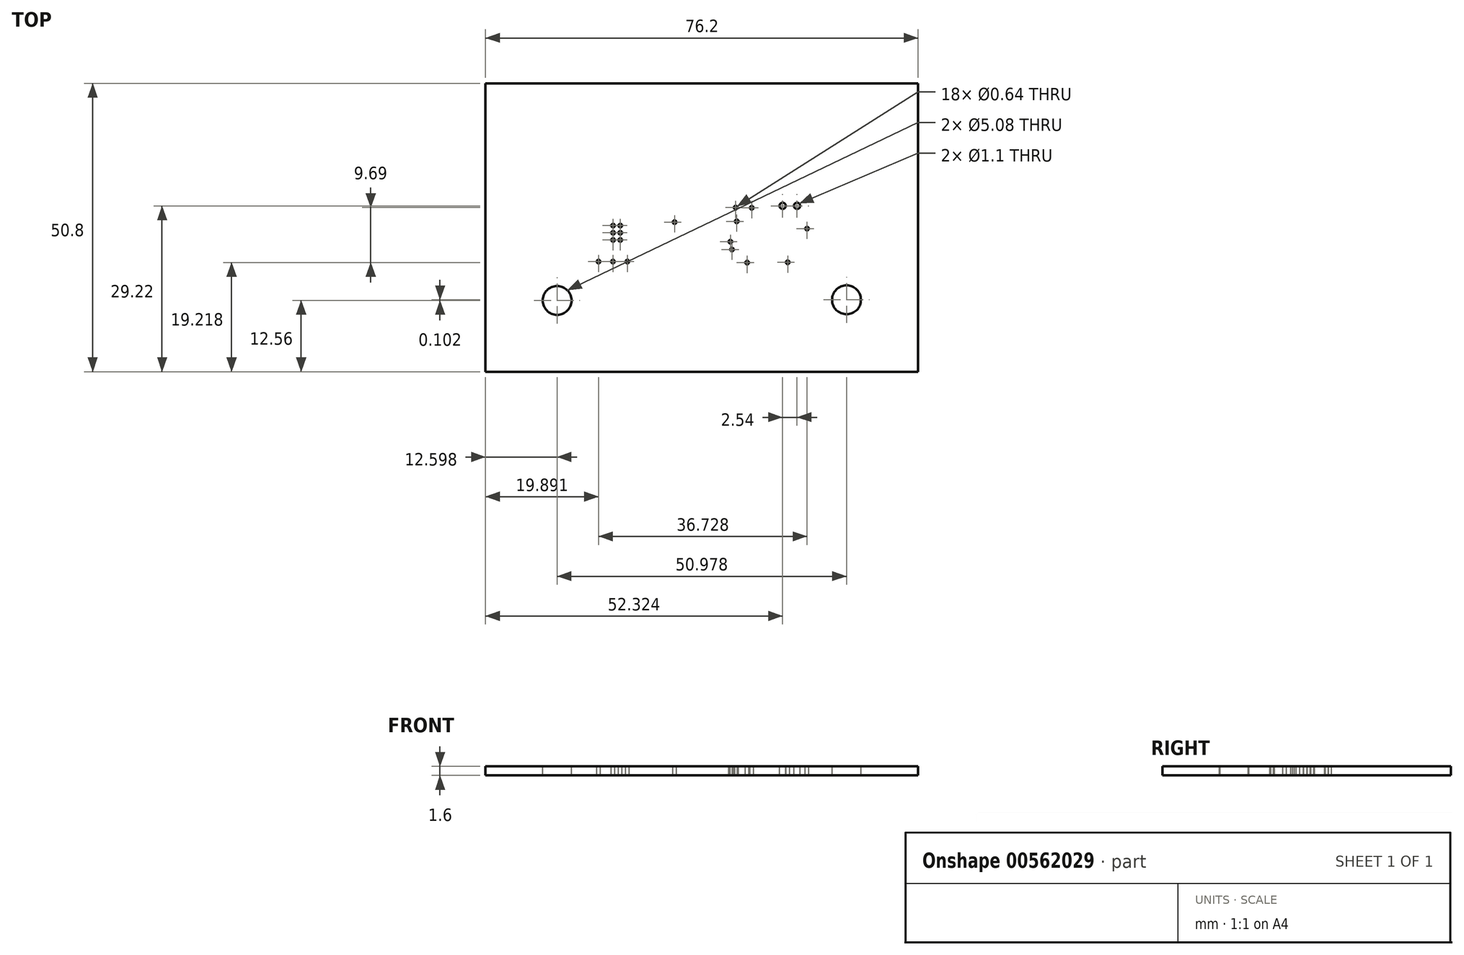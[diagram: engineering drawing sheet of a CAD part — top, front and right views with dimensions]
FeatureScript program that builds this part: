
annotation { "Feature Type Name" : "Feature", "Feature Type Description" : "" }
export const myFeature = defineFeature(function(context is Context, id is Id, definition is map)
    precondition{}
    {
        {
            var Q0;
            Q0=qCreatedBy(makeId("Top.planeOp"),FACE);
            var sketch = newSketch(context, id + "F0", { "sketchPlane" : qUnion([Q0])});
            skArc(sketch, "E0", {"start": v(-12.89, -6) * mm, "mid": v(-13.13, -5.75) * mm, "end": v(-13.37, -6) * mm});
            skArc(sketch, "E1", {"start": v(-13.37, -6) * mm, "mid": v(-13.13, -6.24) * mm, "end": v(-12.89, -6) * mm});
            skArc(sketch, "E2", {"start": v(-15.43, -6) * mm, "mid": v(-15.67, -5.75) * mm, "end": v(-15.91, -6) * mm});
            skArc(sketch, "E3", {"start": v(-15.91, -6) * mm, "mid": v(-15.67, -6.24) * mm, "end": v(-15.43, -6) * mm});
            skArc(sketch, "E4", {"start": v(-17.97, -6) * mm, "mid": v(-18.2, -5.75) * mm, "end": v(-18.45, -6) * mm});
            skArc(sketch, "E5", {"start": v(-18.45, -6) * mm, "mid": v(-18.2, -6.24) * mm, "end": v(-17.97, -6) * mm});
            skArc(sketch, "E6", {"start": v(18.76, -0.2) * mm, "mid": v(18.52, 0.05) * mm, "end": v(18.28, -0.2) * mm});
            skArc(sketch, "E7", {"start": v(18.28, -0.2) * mm, "mid": v(18.52, -0.43) * mm, "end": v(18.76, -0.2) * mm});
            skArc(sketch, "E8", {"start": v(5.26, -2.5) * mm, "mid": v(5.02, -2.26) * mm, "end": v(4.78, -2.5) * mm});
            skArc(sketch, "E9", {"start": v(4.78, -2.5) * mm, "mid": v(5.02, -2.74) * mm, "end": v(5.26, -2.5) * mm});
            skArc(sketch, "E10", {"start": v(5.54, -3.88) * mm, "mid": v(5.3, -3.63) * mm, "end": v(5.06, -3.88) * mm});
            skArc(sketch, "E11", {"start": v(5.06, -3.88) * mm, "mid": v(5.3, -4.12) * mm, "end": v(5.54, -3.88) * mm});
            skArc(sketch, "E12", {"start": v(-4.57, 0.95) * mm, "mid": v(-4.81, 1.19) * mm, "end": v(-5.05, 0.95) * mm});
            skArc(sketch, "E13", {"start": v(-5.05, 0.95) * mm, "mid": v(-4.81, 0.7) * mm, "end": v(-4.57, 0.95) * mm});
            skArc(sketch, "E14", {"start": v(6.2, 3.5) * mm, "mid": v(5.96, 3.75) * mm, "end": v(5.72, 3.5) * mm});
            skArc(sketch, "E15", {"start": v(5.72, 3.5) * mm, "mid": v(5.96, 3.27) * mm, "end": v(6.2, 3.5) * mm});
            skArc(sketch, "E16", {"start": v(9.03, 3.47) * mm, "mid": v(8.79, 3.71) * mm, "end": v(8.54, 3.47) * mm});
            skArc(sketch, "E17", {"start": v(8.54, 3.47) * mm, "mid": v(8.79, 3.23) * mm, "end": v(9.03, 3.47) * mm});
            skArc(sketch, "E18", {"start": v(6.38, 1.09) * mm, "mid": v(6.14, 1.33) * mm, "end": v(5.9, 1.09) * mm});
            skArc(sketch, "E19", {"start": v(5.9, 1.09) * mm, "mid": v(6.14, 0.85) * mm, "end": v(6.38, 1.09) * mm});
            skArc(sketch, "E20", {"start": v(28.86, -23.7) * mm, "mid": v(28.39, -23.22) * mm, "end": v(27.91, -23.7) * mm});
            skArc(sketch, "E21", {"start": v(27.91, -23.7) * mm, "mid": v(28.39, -24.17) * mm, "end": v(28.86, -23.7) * mm});
            skArc(sketch, "E22", {"start": v(26.32, -23.7) * mm, "mid": v(25.85, -23.22) * mm, "end": v(25.37, -23.7) * mm});
            skArc(sketch, "E23", {"start": v(25.37, -23.7) * mm, "mid": v(25.85, -24.17) * mm, "end": v(26.32, -23.7) * mm});
            skArc(sketch, "E24", {"start": v(23.78, -23.7) * mm, "mid": v(23.3, -23.22) * mm, "end": v(22.83, -23.7) * mm});
            skArc(sketch, "E25", {"start": v(22.83, -23.7) * mm, "mid": v(23.3, -24.17) * mm, "end": v(23.78, -23.7) * mm});
            skArc(sketch, "E26", {"start": v(21.24, -23.7) * mm, "mid": v(20.77, -23.22) * mm, "end": v(20.3, -23.7) * mm});
            skArc(sketch, "E27", {"start": v(20.3, -23.7) * mm, "mid": v(20.77, -24.17) * mm, "end": v(21.24, -23.7) * mm});
            skArc(sketch, "E28", {"start": v(18.7, -23.7) * mm, "mid": v(18.23, -23.22) * mm, "end": v(17.75, -23.7) * mm});
            skArc(sketch, "E29", {"start": v(17.75, -23.7) * mm, "mid": v(18.23, -24.17) * mm, "end": v(18.7, -23.7) * mm});
            skArc(sketch, "E30", {"start": v(16.16, -23.7) * mm, "mid": v(15.69, -23.22) * mm, "end": v(15.21, -23.7) * mm});
            skArc(sketch, "E31", {"start": v(15.21, -23.7) * mm, "mid": v(15.69, -24.17) * mm, "end": v(16.16, -23.7) * mm});
            skArc(sketch, "E32", {"start": v(13.62, -23.7) * mm, "mid": v(13.15, -23.22) * mm, "end": v(12.67, -23.7) * mm});
            skArc(sketch, "E33", {"start": v(12.67, -23.7) * mm, "mid": v(13.15, -24.17) * mm, "end": v(13.62, -23.7) * mm});
            skArc(sketch, "E34", {"start": v(11.08, -23.7) * mm, "mid": v(10.6, -23.22) * mm, "end": v(10.13, -23.7) * mm});
            skArc(sketch, "E35", {"start": v(10.13, -23.7) * mm, "mid": v(10.6, -24.17) * mm, "end": v(11.08, -23.7) * mm});
            skArc(sketch, "E36", {"start": v(8.54, -23.7) * mm, "mid": v(8.07, -23.22) * mm, "end": v(7.6, -23.7) * mm});
            skArc(sketch, "E37", {"start": v(7.6, -23.7) * mm, "mid": v(8.07, -24.17) * mm, "end": v(8.54, -23.7) * mm});
            skArc(sketch, "E38", {"start": v(6, -23.7) * mm, "mid": v(5.53, -23.22) * mm, "end": v(5.05, -23.7) * mm});
            skArc(sketch, "E39", {"start": v(5.05, -23.7) * mm, "mid": v(5.53, -24.17) * mm, "end": v(6, -23.7) * mm});
            skArc(sketch, "E40", {"start": v(3.46, -23.7) * mm, "mid": v(2.99, -23.22) * mm, "end": v(2.51, -23.7) * mm});
            skArc(sketch, "E41", {"start": v(2.51, -23.7) * mm, "mid": v(2.99, -24.17) * mm, "end": v(3.46, -23.7) * mm});
            skArc(sketch, "E42", {"start": v(0.92, -23.7) * mm, "mid": v(0.45, -23.22) * mm, "end": v(-0.03, -23.7) * mm});
            skArc(sketch, "E43", {"start": v(-0.03, -23.7) * mm, "mid": v(0.45, -24.17) * mm, "end": v(0.92, -23.7) * mm});
            skArc(sketch, "E44", {"start": v(-1.62, -23.7) * mm, "mid": v(-2.1, -23.22) * mm, "end": v(-2.57, -23.7) * mm});
            skArc(sketch, "E45", {"start": v(-2.57, -23.7) * mm, "mid": v(-2.1, -24.17) * mm, "end": v(-1.62, -23.7) * mm});
            skArc(sketch, "E46", {"start": v(-4.16, -23.7) * mm, "mid": v(-4.63, -23.22) * mm, "end": v(-5.1, -23.7) * mm});
            skArc(sketch, "E47", {"start": v(-5.1, -23.7) * mm, "mid": v(-4.63, -24.17) * mm, "end": v(-4.16, -23.7) * mm});
            skArc(sketch, "E48", {"start": v(-6.7, -23.7) * mm, "mid": v(-7.17, -23.22) * mm, "end": v(-7.65, -23.7) * mm});
            skArc(sketch, "E49", {"start": v(-7.65, -23.7) * mm, "mid": v(-7.17, -24.17) * mm, "end": v(-6.7, -23.7) * mm});
            skArc(sketch, "E50", {"start": v(-9.24, -23.7) * mm, "mid": v(-9.71, -23.22) * mm, "end": v(-10.19, -23.7) * mm});
            skArc(sketch, "E51", {"start": v(-10.19, -23.7) * mm, "mid": v(-9.71, -24.17) * mm, "end": v(-9.24, -23.7) * mm});
            skArc(sketch, "E52", {"start": v(-11.78, -23.7) * mm, "mid": v(-12.25, -23.22) * mm, "end": v(-12.73, -23.7) * mm});
            skArc(sketch, "E53", {"start": v(-12.73, -23.7) * mm, "mid": v(-12.25, -24.17) * mm, "end": v(-11.78, -23.7) * mm});
            skArc(sketch, "E54", {"start": v(-15.4, 0.34) * mm, "mid": v(-15.65, 0.58) * mm, "end": v(-15.89, 0.34) * mm});
            skArc(sketch, "E55", {"start": v(-15.89, 0.34) * mm, "mid": v(-15.65, 0.1) * mm, "end": v(-15.4, 0.34) * mm});
            skArc(sketch, "E56", {"start": v(-14.14, 0.34) * mm, "mid": v(-14.38, 0.58) * mm, "end": v(-14.62, 0.34) * mm});
            skArc(sketch, "E57", {"start": v(-14.62, 0.34) * mm, "mid": v(-14.38, 0.1) * mm, "end": v(-14.14, 0.34) * mm});
            skArc(sketch, "E58", {"start": v(-14.14, -0.93) * mm, "mid": v(-14.38, -0.69) * mm, "end": v(-14.62, -0.93) * mm});
            skArc(sketch, "E59", {"start": v(-14.62, -0.93) * mm, "mid": v(-14.38, -1.17) * mm, "end": v(-14.14, -0.93) * mm});
            skArc(sketch, "E60", {"start": v(-14.14, -2.2) * mm, "mid": v(-14.38, -1.96) * mm, "end": v(-14.62, -2.2) * mm});
            skArc(sketch, "E61", {"start": v(-14.62, -2.2) * mm, "mid": v(-14.38, -2.44) * mm, "end": v(-14.14, -2.2) * mm});
            skArc(sketch, "E62", {"start": v(-15.4, -0.93) * mm, "mid": v(-15.65, -0.69) * mm, "end": v(-15.89, -0.93) * mm});
            skArc(sketch, "E63", {"start": v(-15.89, -0.93) * mm, "mid": v(-15.65, -1.17) * mm, "end": v(-15.4, -0.93) * mm});
            skArc(sketch, "E64", {"start": v(-15.4, -2.2) * mm, "mid": v(-15.65, -1.96) * mm, "end": v(-15.89, -2.2) * mm});
            skArc(sketch, "E65", {"start": v(-15.89, -2.2) * mm, "mid": v(-15.65, -2.44) * mm, "end": v(-15.4, -2.2) * mm});
            skArc(sketch, "E66", {"start": v(37.09, 19.86) * mm, "mid": v(36.61, 20.34) * mm, "end": v(36.13, 19.86) * mm});
            skArc(sketch, "E67", {"start": v(36.13, 19.86) * mm, "mid": v(36.61, 19.38) * mm, "end": v(37.09, 19.86) * mm});
            skArc(sketch, "E68", {"start": v(37.09, 17.32) * mm, "mid": v(36.61, 17.8) * mm, "end": v(36.13, 17.32) * mm});
            skArc(sketch, "E69", {"start": v(36.13, 17.32) * mm, "mid": v(36.61, 16.84) * mm, "end": v(37.09, 17.32) * mm});
            skArc(sketch, "E70", {"start": v(37.09, 14.78) * mm, "mid": v(36.61, 15.26) * mm, "end": v(36.13, 14.78) * mm});
            skArc(sketch, "E71", {"start": v(36.13, 14.78) * mm, "mid": v(36.61, 14.3) * mm, "end": v(37.09, 14.78) * mm});
            skArc(sketch, "E72", {"start": v(37.09, 12.24) * mm, "mid": v(36.61, 12.72) * mm, "end": v(36.13, 12.24) * mm});
            skArc(sketch, "E73", {"start": v(36.13, 12.24) * mm, "mid": v(36.61, 11.76) * mm, "end": v(37.09, 12.24) * mm});
            skArc(sketch, "E74", {"start": v(37.09, 9.7) * mm, "mid": v(36.61, 10.18) * mm, "end": v(36.13, 9.7) * mm});
            skArc(sketch, "E75", {"start": v(36.13, 9.7) * mm, "mid": v(36.61, 9.22) * mm, "end": v(37.09, 9.7) * mm});
            skArc(sketch, "E76", {"start": v(37, -12.53) * mm, "mid": v(36.53, -12.06) * mm, "end": v(36.06, -12.53) * mm});
            skArc(sketch, "E77", {"start": v(36.06, -12.53) * mm, "mid": v(36.53, -13) * mm, "end": v(37, -12.53) * mm});
            skArc(sketch, "E78", {"start": v(17.24, 3.82) * mm, "mid": v(16.76, 4.3) * mm, "end": v(16.29, 3.82) * mm});
            skArc(sketch, "E79", {"start": v(16.29, 3.82) * mm, "mid": v(16.76, 3.34) * mm, "end": v(17.24, 3.82) * mm});
            skArc(sketch, "E80", {"start": v(16.8, 23.69) * mm, "mid": v(16.33, 24.16) * mm, "end": v(15.85, 23.69) * mm});
            skArc(sketch, "E81", {"start": v(15.85, 23.69) * mm, "mid": v(16.33, 23.21) * mm, "end": v(16.8, 23.69) * mm});
            skArc(sketch, "E82", {"start": v(-12.94, -6) * mm, "mid": v(-13.13, -5.8) * mm, "end": v(-13.32, -6) * mm});
            skArc(sketch, "E83", {"start": v(-13.32, -6) * mm, "mid": v(-13.13, -6.18) * mm, "end": v(-12.94, -6) * mm});
            skArc(sketch, "E84", {"start": v(-15.48, -6) * mm, "mid": v(-15.67, -5.8) * mm, "end": v(-15.86, -6) * mm});
            skArc(sketch, "E85", {"start": v(-15.86, -6) * mm, "mid": v(-15.67, -6.18) * mm, "end": v(-15.48, -6) * mm});
            skArc(sketch, "E86", {"start": v(-18.02, -6) * mm, "mid": v(-18.2, -5.8) * mm, "end": v(-18.4, -6) * mm});
            skArc(sketch, "E87", {"start": v(-18.4, -6) * mm, "mid": v(-18.2, -6.18) * mm, "end": v(-18.02, -6) * mm});
            skArc(sketch, "E88", {"start": v(18.7, -0.2) * mm, "mid": v(18.52, 0) * mm, "end": v(18.33, -0.2) * mm});
            skArc(sketch, "E89", {"start": v(18.33, -0.2) * mm, "mid": v(18.52, -0.38) * mm, "end": v(18.7, -0.2) * mm});
            skArc(sketch, "E90", {"start": v(5.2, -2.5) * mm, "mid": v(5.02, -2.3) * mm, "end": v(4.83, -2.5) * mm});
            skArc(sketch, "E91", {"start": v(4.83, -2.5) * mm, "mid": v(5.02, -2.69) * mm, "end": v(5.2, -2.5) * mm});
            skArc(sketch, "E92", {"start": v(5.5, -3.88) * mm, "mid": v(5.3, -3.69) * mm, "end": v(5.11, -3.88) * mm});
            skArc(sketch, "E93", {"start": v(5.11, -3.88) * mm, "mid": v(5.3, -4.07) * mm, "end": v(5.5, -3.88) * mm});
            skArc(sketch, "E94", {"start": v(-4.62, 0.95) * mm, "mid": v(-4.81, 1.14) * mm, "end": v(-5, 0.95) * mm});
            skArc(sketch, "E95", {"start": v(-5, 0.95) * mm, "mid": v(-4.81, 0.76) * mm, "end": v(-4.62, 0.95) * mm});
            skArc(sketch, "E96", {"start": v(6.15, 3.5) * mm, "mid": v(5.96, 3.7) * mm, "end": v(5.77, 3.5) * mm});
            skArc(sketch, "E97", {"start": v(5.77, 3.5) * mm, "mid": v(5.96, 3.32) * mm, "end": v(6.15, 3.5) * mm});
            skArc(sketch, "E98", {"start": v(8.98, 3.47) * mm, "mid": v(8.79, 3.66) * mm, "end": v(8.6, 3.47) * mm});
            skArc(sketch, "E99", {"start": v(8.6, 3.47) * mm, "mid": v(8.79, 3.28) * mm, "end": v(8.98, 3.47) * mm});
            skArc(sketch, "E100", {"start": v(6.33, 1.09) * mm, "mid": v(6.14, 1.28) * mm, "end": v(5.95, 1.09) * mm});
            skArc(sketch, "E101", {"start": v(5.95, 1.09) * mm, "mid": v(6.14, 0.9) * mm, "end": v(6.33, 1.09) * mm});
            skArc(sketch, "E102", {"start": v(28.81, -23.7) * mm, "mid": v(28.39, -23.27) * mm, "end": v(27.97, -23.7) * mm});
            skArc(sketch, "E103", {"start": v(27.97, -23.7) * mm, "mid": v(28.39, -24.11) * mm, "end": v(28.81, -23.7) * mm});
            skArc(sketch, "E104", {"start": v(26.27, -23.7) * mm, "mid": v(25.85, -23.27) * mm, "end": v(25.43, -23.7) * mm});
            skArc(sketch, "E105", {"start": v(25.43, -23.7) * mm, "mid": v(25.85, -24.11) * mm, "end": v(26.27, -23.7) * mm});
            skArc(sketch, "E106", {"start": v(23.73, -23.7) * mm, "mid": v(23.3, -23.27) * mm, "end": v(22.89, -23.7) * mm});
            skArc(sketch, "E107", {"start": v(22.89, -23.7) * mm, "mid": v(23.3, -24.11) * mm, "end": v(23.73, -23.7) * mm});
            skArc(sketch, "E108", {"start": v(21.2, -23.7) * mm, "mid": v(20.77, -23.27) * mm, "end": v(20.35, -23.7) * mm});
            skArc(sketch, "E109", {"start": v(20.35, -23.7) * mm, "mid": v(20.77, -24.11) * mm, "end": v(21.2, -23.7) * mm});
            skArc(sketch, "E110", {"start": v(18.65, -23.7) * mm, "mid": v(18.23, -23.27) * mm, "end": v(17.8, -23.7) * mm});
            skArc(sketch, "E111", {"start": v(17.8, -23.7) * mm, "mid": v(18.23, -24.11) * mm, "end": v(18.65, -23.7) * mm});
            skArc(sketch, "E112", {"start": v(16.11, -23.7) * mm, "mid": v(15.69, -23.27) * mm, "end": v(15.27, -23.7) * mm});
            skArc(sketch, "E113", {"start": v(15.27, -23.7) * mm, "mid": v(15.69, -24.11) * mm, "end": v(16.11, -23.7) * mm});
            skArc(sketch, "E114", {"start": v(13.57, -23.7) * mm, "mid": v(13.15, -23.27) * mm, "end": v(12.73, -23.7) * mm});
            skArc(sketch, "E115", {"start": v(12.73, -23.7) * mm, "mid": v(13.15, -24.11) * mm, "end": v(13.57, -23.7) * mm});
            skArc(sketch, "E116", {"start": v(11.03, -23.7) * mm, "mid": v(10.6, -23.27) * mm, "end": v(10.19, -23.7) * mm});
            skArc(sketch, "E117", {"start": v(10.19, -23.7) * mm, "mid": v(10.6, -24.11) * mm, "end": v(11.03, -23.7) * mm});
            skArc(sketch, "E118", {"start": v(8.5, -23.7) * mm, "mid": v(8.07, -23.27) * mm, "end": v(7.65, -23.7) * mm});
            skArc(sketch, "E119", {"start": v(7.65, -23.7) * mm, "mid": v(8.07, -24.11) * mm, "end": v(8.5, -23.7) * mm});
            skArc(sketch, "E120", {"start": v(5.95, -23.7) * mm, "mid": v(5.53, -23.27) * mm, "end": v(5.1, -23.7) * mm});
            skArc(sketch, "E121", {"start": v(5.1, -23.7) * mm, "mid": v(5.53, -24.11) * mm, "end": v(5.95, -23.7) * mm});
            skArc(sketch, "E122", {"start": v(3.41, -23.7) * mm, "mid": v(2.99, -23.27) * mm, "end": v(2.57, -23.7) * mm});
            skArc(sketch, "E123", {"start": v(2.57, -23.7) * mm, "mid": v(2.99, -24.11) * mm, "end": v(3.41, -23.7) * mm});
            skArc(sketch, "E124", {"start": v(0.87, -23.7) * mm, "mid": v(0.45, -23.27) * mm, "end": v(0.03, -23.7) * mm});
            skArc(sketch, "E125", {"start": v(0.03, -23.7) * mm, "mid": v(0.45, -24.11) * mm, "end": v(0.87, -23.7) * mm});
            skArc(sketch, "E126", {"start": v(-1.67, -23.7) * mm, "mid": v(-2.1, -23.27) * mm, "end": v(-2.51, -23.7) * mm});
            skArc(sketch, "E127", {"start": v(-2.51, -23.7) * mm, "mid": v(-2.1, -24.11) * mm, "end": v(-1.67, -23.7) * mm});
            skArc(sketch, "E128", {"start": v(-4.2, -23.7) * mm, "mid": v(-4.63, -23.27) * mm, "end": v(-5.05, -23.7) * mm});
            skArc(sketch, "E129", {"start": v(-5.05, -23.7) * mm, "mid": v(-4.63, -24.11) * mm, "end": v(-4.2, -23.7) * mm});
            skArc(sketch, "E130", {"start": v(-6.75, -23.7) * mm, "mid": v(-7.17, -23.27) * mm, "end": v(-7.6, -23.7) * mm});
            skArc(sketch, "E131", {"start": v(-7.6, -23.7) * mm, "mid": v(-7.17, -24.11) * mm, "end": v(-6.75, -23.7) * mm});
            skArc(sketch, "E132", {"start": v(-9.29, -23.7) * mm, "mid": v(-9.71, -23.27) * mm, "end": v(-10.13, -23.7) * mm});
            skArc(sketch, "E133", {"start": v(-10.13, -23.7) * mm, "mid": v(-9.71, -24.11) * mm, "end": v(-9.29, -23.7) * mm});
            skArc(sketch, "E134", {"start": v(-11.83, -23.7) * mm, "mid": v(-12.25, -23.27) * mm, "end": v(-12.67, -23.7) * mm});
            skArc(sketch, "E135", {"start": v(-12.67, -23.7) * mm, "mid": v(-12.25, -24.11) * mm, "end": v(-11.83, -23.7) * mm});
            skArc(sketch, "E136", {"start": v(-15.46, 0.34) * mm, "mid": v(-15.65, 0.53) * mm, "end": v(-15.84, 0.34) * mm});
            skArc(sketch, "E137", {"start": v(-15.84, 0.34) * mm, "mid": v(-15.65, 0.15) * mm, "end": v(-15.46, 0.34) * mm});
            skArc(sketch, "E138", {"start": v(-14.19, 0.34) * mm, "mid": v(-14.38, 0.53) * mm, "end": v(-14.57, 0.34) * mm});
            skArc(sketch, "E139", {"start": v(-14.57, 0.34) * mm, "mid": v(-14.38, 0.15) * mm, "end": v(-14.19, 0.34) * mm});
            skArc(sketch, "E140", {"start": v(-14.19, -0.93) * mm, "mid": v(-14.38, -0.74) * mm, "end": v(-14.57, -0.93) * mm});
            skArc(sketch, "E141", {"start": v(-14.57, -0.93) * mm, "mid": v(-14.38, -1.12) * mm, "end": v(-14.19, -0.93) * mm});
            skArc(sketch, "E142", {"start": v(-14.19, -2.2) * mm, "mid": v(-14.38, -2) * mm, "end": v(-14.57, -2.2) * mm});
            skArc(sketch, "E143", {"start": v(-14.57, -2.2) * mm, "mid": v(-14.38, -2.39) * mm, "end": v(-14.19, -2.2) * mm});
            skArc(sketch, "E144", {"start": v(-15.46, -0.93) * mm, "mid": v(-15.65, -0.74) * mm, "end": v(-15.84, -0.93) * mm});
            skArc(sketch, "E145", {"start": v(-15.84, -0.93) * mm, "mid": v(-15.65, -1.12) * mm, "end": v(-15.46, -0.93) * mm});
            skArc(sketch, "E146", {"start": v(-15.46, -2.2) * mm, "mid": v(-15.65, -2) * mm, "end": v(-15.84, -2.2) * mm});
            skArc(sketch, "E147", {"start": v(-15.84, -2.2) * mm, "mid": v(-15.65, -2.39) * mm, "end": v(-15.46, -2.2) * mm});
            skArc(sketch, "E148", {"start": v(37.04, 19.86) * mm, "mid": v(36.61, 20.29) * mm, "end": v(36.18, 19.86) * mm});
            skArc(sketch, "E149", {"start": v(36.18, 19.86) * mm, "mid": v(36.61, 19.43) * mm, "end": v(37.04, 19.86) * mm});
            skArc(sketch, "E150", {"start": v(37.04, 17.32) * mm, "mid": v(36.61, 17.75) * mm, "end": v(36.18, 17.32) * mm});
            skArc(sketch, "E151", {"start": v(36.18, 17.32) * mm, "mid": v(36.61, 16.9) * mm, "end": v(37.04, 17.32) * mm});
            skArc(sketch, "E152", {"start": v(37.04, 14.78) * mm, "mid": v(36.61, 15.2) * mm, "end": v(36.18, 14.78) * mm});
            skArc(sketch, "E153", {"start": v(36.18, 14.78) * mm, "mid": v(36.61, 14.35) * mm, "end": v(37.04, 14.78) * mm});
            skArc(sketch, "E154", {"start": v(37.04, 12.24) * mm, "mid": v(36.61, 12.67) * mm, "end": v(36.18, 12.24) * mm});
            skArc(sketch, "E155", {"start": v(36.18, 12.24) * mm, "mid": v(36.61, 11.81) * mm, "end": v(37.04, 12.24) * mm});
            skArc(sketch, "E156", {"start": v(37.04, 9.7) * mm, "mid": v(36.61, 10.13) * mm, "end": v(36.18, 9.7) * mm});
            skArc(sketch, "E157", {"start": v(36.18, 9.7) * mm, "mid": v(36.61, 9.27) * mm, "end": v(37.04, 9.7) * mm});
            skArc(sketch, "E158", {"start": v(36.95, -12.53) * mm, "mid": v(36.53, -12.1) * mm, "end": v(36.1, -12.53) * mm});
            skArc(sketch, "E159", {"start": v(36.1, -12.53) * mm, "mid": v(36.53, -12.96) * mm, "end": v(36.95, -12.53) * mm});
            skArc(sketch, "E160", {"start": v(17.19, 3.82) * mm, "mid": v(16.76, 4.25) * mm, "end": v(16.34, 3.82) * mm});
            skArc(sketch, "E161", {"start": v(16.34, 3.82) * mm, "mid": v(16.76, 3.4) * mm, "end": v(17.19, 3.82) * mm});
            skArc(sketch, "E162", {"start": v(16.75, 23.69) * mm, "mid": v(16.33, 24.1) * mm, "end": v(15.9, 23.69) * mm});
            skArc(sketch, "E163", {"start": v(15.9, 23.69) * mm, "mid": v(16.33, 23.26) * mm, "end": v(16.75, 23.69) * mm});
            skLineSegment(sketch, "E164", {"start": v(15.12, -6.13) * mm, "end": v(15.12, -7.88) * mm});
            skArc(sketch, "E165", {"start": v(15.08, -6.13) * mm, "mid": v(15.12, -6.16) * mm, "end": v(15.16, -6.13) * mm});
            skArc(sketch, "E166", {"start": v(15.16, -6.13) * mm, "mid": v(15.12, -6.09) * mm, "end": v(15.08, -6.13) * mm});
            skArc(sketch, "E167", {"start": v(15.08, -7.88) * mm, "mid": v(15.12, -7.92) * mm, "end": v(15.16, -7.88) * mm});
            skArc(sketch, "E168", {"start": v(15.16, -7.88) * mm, "mid": v(15.12, -7.84) * mm, "end": v(15.08, -7.88) * mm});
            skLineSegment(sketch, "E169", {"start": v(15.12, -7.88) * mm, "end": v(30.93, -23.7) * mm});
            skArc(sketch, "E170", {"start": v(30.9, -23.7) * mm, "mid": v(30.93, -23.73) * mm, "end": v(30.97, -23.7) * mm});
            skArc(sketch, "E171", {"start": v(30.97, -23.7) * mm, "mid": v(30.93, -23.65) * mm, "end": v(30.9, -23.7) * mm});
            skLineSegment(sketch, "E172", {"start": v(15.12, -6.13) * mm, "end": v(30.12, -6.13) * mm});
            skArc(sketch, "E173", {"start": v(30.09, -6.13) * mm, "mid": v(30.12, -6.16) * mm, "end": v(30.16, -6.13) * mm});
            skArc(sketch, "E174", {"start": v(30.16, -6.13) * mm, "mid": v(30.12, -6.09) * mm, "end": v(30.09, -6.13) * mm});
            skLineSegment(sketch, "E175", {"start": v(30.12, -6.13) * mm, "end": v(36.53, -12.53) * mm});
            skArc(sketch, "E176", {"start": v(36.5, -12.53) * mm, "mid": v(36.53, -12.57) * mm, "end": v(36.57, -12.53) * mm});
            skArc(sketch, "E177", {"start": v(36.57, -12.53) * mm, "mid": v(36.53, -12.5) * mm, "end": v(36.5, -12.53) * mm});
            skLineSegment(sketch, "E178", {"start": v(-14.38, -0.93) * mm, "end": v(-14.24, -0.93) * mm});
            skArc(sketch, "E179", {"start": v(-14.41, -0.93) * mm, "mid": v(-14.38, -0.97) * mm, "end": v(-14.34, -0.93) * mm});
            skArc(sketch, "E180", {"start": v(-14.34, -0.93) * mm, "mid": v(-14.38, -0.89) * mm, "end": v(-14.41, -0.93) * mm});
            skArc(sketch, "E181", {"start": v(-14.28, -0.93) * mm, "mid": v(-14.24, -0.97) * mm, "end": v(-14.2, -0.93) * mm});
            skArc(sketch, "E182", {"start": v(-14.2, -0.93) * mm, "mid": v(-14.24, -0.89) * mm, "end": v(-14.28, -0.93) * mm});
            skLineSegment(sketch, "E183", {"start": v(-14.24, -0.93) * mm, "end": v(-14.01, -0.7) * mm});
            skArc(sketch, "E184", {"start": v(-14.05, -0.7) * mm, "mid": v(-14.01, -0.73) * mm, "end": v(-13.97, -0.7) * mm});
            skArc(sketch, "E185", {"start": v(-13.97, -0.7) * mm, "mid": v(-14.01, -0.66) * mm, "end": v(-14.05, -0.7) * mm});
            skLineSegment(sketch, "E186", {"start": v(-14.01, -0.7) * mm, "end": v(-12.24, -0.7) * mm});
            skArc(sketch, "E187", {"start": v(-12.28, -0.7) * mm, "mid": v(-12.24, -0.73) * mm, "end": v(-12.2, -0.7) * mm});
            skArc(sketch, "E188", {"start": v(-12.2, -0.7) * mm, "mid": v(-12.24, -0.66) * mm, "end": v(-12.28, -0.7) * mm});
            skLineSegment(sketch, "E189", {"start": v(-12.24, -0.7) * mm, "end": v(-8.8, -4.14) * mm});
            skArc(sketch, "E190", {"start": v(-8.83, -4.14) * mm, "mid": v(-8.8, -4.18) * mm, "end": v(-8.76, -4.14) * mm});
            skArc(sketch, "E191", {"start": v(-8.76, -4.14) * mm, "mid": v(-8.8, -4.1) * mm, "end": v(-8.83, -4.14) * mm});
            skLineSegment(sketch, "E192", {"start": v(-8.8, -4.14) * mm, "end": v(-8.8, -9.37) * mm});
            skArc(sketch, "E193", {"start": v(-8.83, -9.37) * mm, "mid": v(-8.8, -9.4) * mm, "end": v(-8.76, -9.37) * mm});
            skArc(sketch, "E194", {"start": v(-8.76, -9.37) * mm, "mid": v(-8.8, -9.33) * mm, "end": v(-8.83, -9.37) * mm});
            skLineSegment(sketch, "E195", {"start": v(-8.8, -9.37) * mm, "end": v(5.53, -23.7) * mm});
            skArc(sketch, "E196", {"start": v(5.5, -23.7) * mm, "mid": v(5.53, -23.73) * mm, "end": v(5.57, -23.7) * mm});
            skArc(sketch, "E197", {"start": v(5.57, -23.7) * mm, "mid": v(5.53, -23.65) * mm, "end": v(5.5, -23.7) * mm});
            skLineSegment(sketch, "E198", {"start": v(7.97, -6.18) * mm, "end": v(10.72, -6.18) * mm});
            skArc(sketch, "E199", {"start": v(7.93, -6.18) * mm, "mid": v(7.97, -6.22) * mm, "end": v(8.01, -6.18) * mm});
            skArc(sketch, "E200", {"start": v(8.01, -6.18) * mm, "mid": v(7.97, -6.14) * mm, "end": v(7.93, -6.18) * mm});
            skArc(sketch, "E201", {"start": v(10.68, -6.18) * mm, "mid": v(10.72, -6.22) * mm, "end": v(10.75, -6.18) * mm});
            skArc(sketch, "E202", {"start": v(10.75, -6.18) * mm, "mid": v(10.72, -6.14) * mm, "end": v(10.68, -6.18) * mm});
            skLineSegment(sketch, "E203", {"start": v(10.72, -6.18) * mm, "end": v(13.39, -8.85) * mm});
            skArc(sketch, "E204", {"start": v(13.35, -8.85) * mm, "mid": v(13.39, -8.9) * mm, "end": v(13.42, -8.85) * mm});
            skArc(sketch, "E205", {"start": v(13.42, -8.85) * mm, "mid": v(13.39, -8.82) * mm, "end": v(13.35, -8.85) * mm});
            skLineSegment(sketch, "E206", {"start": v(13.39, -8.85) * mm, "end": v(13.55, -8.85) * mm});
            skArc(sketch, "E207", {"start": v(13.52, -8.85) * mm, "mid": v(13.55, -8.9) * mm, "end": v(13.6, -8.85) * mm});
            skArc(sketch, "E208", {"start": v(13.6, -8.85) * mm, "mid": v(13.55, -8.82) * mm, "end": v(13.52, -8.85) * mm});
            skLineSegment(sketch, "E209", {"start": v(13.55, -8.85) * mm, "end": v(28.39, -23.7) * mm});
            skArc(sketch, "E210", {"start": v(28.35, -23.7) * mm, "mid": v(28.39, -23.73) * mm, "end": v(28.43, -23.7) * mm});
            skArc(sketch, "E211", {"start": v(28.43, -23.7) * mm, "mid": v(28.39, -23.65) * mm, "end": v(28.35, -23.7) * mm});
            skLineSegment(sketch, "E212", {"start": v(7.97, -6.18) * mm, "end": v(12.31, -6.18) * mm});
            skArc(sketch, "E213", {"start": v(12.28, -6.18) * mm, "mid": v(12.31, -6.22) * mm, "end": v(12.35, -6.18) * mm});
            skArc(sketch, "E214", {"start": v(12.35, -6.18) * mm, "mid": v(12.31, -6.14) * mm, "end": v(12.28, -6.18) * mm});
            skLineSegment(sketch, "E215", {"start": v(12.31, -6.18) * mm, "end": v(14.23, -4.26) * mm});
            skArc(sketch, "E216", {"start": v(14.2, -4.26) * mm, "mid": v(14.23, -4.3) * mm, "end": v(14.27, -4.26) * mm});
            skArc(sketch, "E217", {"start": v(14.27, -4.26) * mm, "mid": v(14.23, -4.22) * mm, "end": v(14.2, -4.26) * mm});
            skLineSegment(sketch, "E218", {"start": v(14.23, -4.26) * mm, "end": v(30.8, -4.26) * mm});
            skArc(sketch, "E219", {"start": v(30.76, -4.26) * mm, "mid": v(30.8, -4.3) * mm, "end": v(30.84, -4.26) * mm});
            skArc(sketch, "E220", {"start": v(30.84, -4.26) * mm, "mid": v(30.8, -4.22) * mm, "end": v(30.76, -4.26) * mm});
            skLineSegment(sketch, "E221", {"start": v(30.8, -4.26) * mm, "end": v(36.53, -10) * mm});
            skArc(sketch, "E222", {"start": v(36.5, -10) * mm, "mid": v(36.53, -10.03) * mm, "end": v(36.57, -10) * mm});
            skArc(sketch, "E223", {"start": v(36.57, -10) * mm, "mid": v(36.53, -9.95) * mm, "end": v(36.5, -10) * mm});
            skLineSegment(sketch, "E224", {"start": v(18.52, -0.2) * mm, "end": v(12, -0.2) * mm});
            skArc(sketch, "E225", {"start": v(18.48, -0.2) * mm, "mid": v(18.52, -0.23) * mm, "end": v(18.56, -0.2) * mm});
            skArc(sketch, "E226", {"start": v(18.56, -0.2) * mm, "mid": v(18.52, -0.15) * mm, "end": v(18.48, -0.2) * mm});
            skArc(sketch, "E227", {"start": v(11.97, -0.2) * mm, "mid": v(12, -0.23) * mm, "end": v(12.04, -0.2) * mm});
            skArc(sketch, "E228", {"start": v(12.04, -0.2) * mm, "mid": v(12, -0.15) * mm, "end": v(11.97, -0.2) * mm});
            skLineSegment(sketch, "E229", {"start": v(12, -0.2) * mm, "end": v(6.55, -5.65) * mm});
            skArc(sketch, "E230", {"start": v(6.5, -5.65) * mm, "mid": v(6.55, -5.69) * mm, "end": v(6.58, -5.65) * mm});
            skArc(sketch, "E231", {"start": v(6.58, -5.65) * mm, "mid": v(6.55, -5.61) * mm, "end": v(6.5, -5.65) * mm});
            skLineSegment(sketch, "E232", {"start": v(6.55, -5.65) * mm, "end": v(6.55, -6.96) * mm});
            skArc(sketch, "E233", {"start": v(6.5, -6.96) * mm, "mid": v(6.55, -7) * mm, "end": v(6.58, -6.96) * mm});
            skArc(sketch, "E234", {"start": v(6.58, -6.96) * mm, "mid": v(6.55, -6.92) * mm, "end": v(6.5, -6.96) * mm});
            skLineSegment(sketch, "E235", {"start": v(6.55, -6.96) * mm, "end": v(7.84, -8.25) * mm});
            skArc(sketch, "E236", {"start": v(7.8, -8.25) * mm, "mid": v(7.84, -8.3) * mm, "end": v(7.87, -8.25) * mm});
            skArc(sketch, "E237", {"start": v(7.87, -8.25) * mm, "mid": v(7.84, -8.21) * mm, "end": v(7.8, -8.25) * mm});
            skLineSegment(sketch, "E238", {"start": v(7.84, -8.25) * mm, "end": v(10.34, -8.25) * mm});
            skArc(sketch, "E239", {"start": v(10.3, -8.25) * mm, "mid": v(10.34, -8.3) * mm, "end": v(10.38, -8.25) * mm});
            skArc(sketch, "E240", {"start": v(10.38, -8.25) * mm, "mid": v(10.34, -8.21) * mm, "end": v(10.3, -8.25) * mm});
            skLineSegment(sketch, "E241", {"start": v(10.34, -8.25) * mm, "end": v(23.07, -20.98) * mm});
            skArc(sketch, "E242", {"start": v(23.04, -20.98) * mm, "mid": v(23.07, -21.02) * mm, "end": v(23.11, -20.98) * mm});
            skArc(sketch, "E243", {"start": v(23.11, -20.98) * mm, "mid": v(23.07, -20.94) * mm, "end": v(23.04, -20.98) * mm});
            skLineSegment(sketch, "E244", {"start": v(23.07, -20.98) * mm, "end": v(23.14, -20.98) * mm});
            skArc(sketch, "E245", {"start": v(23.1, -20.98) * mm, "mid": v(23.14, -21.02) * mm, "end": v(23.18, -20.98) * mm});
            skArc(sketch, "E246", {"start": v(23.18, -20.98) * mm, "mid": v(23.14, -20.94) * mm, "end": v(23.1, -20.98) * mm});
            skLineSegment(sketch, "E247", {"start": v(23.14, -20.98) * mm, "end": v(25.85, -23.7) * mm});
            skArc(sketch, "E248", {"start": v(25.81, -23.7) * mm, "mid": v(25.85, -23.73) * mm, "end": v(25.89, -23.7) * mm});
            skArc(sketch, "E249", {"start": v(25.89, -23.7) * mm, "mid": v(25.85, -23.65) * mm, "end": v(25.81, -23.7) * mm});
            skLineSegment(sketch, "E250", {"start": v(8.79, 3.47) * mm, "end": v(8.79, -2.32) * mm});
            skArc(sketch, "E251", {"start": v(8.75, 3.47) * mm, "mid": v(8.79, 3.43) * mm, "end": v(8.82, 3.47) * mm});
            skArc(sketch, "E252", {"start": v(8.82, 3.47) * mm, "mid": v(8.79, 3.5) * mm, "end": v(8.75, 3.47) * mm});
            skArc(sketch, "E253", {"start": v(8.75, -2.32) * mm, "mid": v(8.79, -2.36) * mm, "end": v(8.82, -2.32) * mm});
            skArc(sketch, "E254", {"start": v(8.82, -2.32) * mm, "mid": v(8.79, -2.28) * mm, "end": v(8.75, -2.32) * mm});
            skLineSegment(sketch, "E255", {"start": v(8.79, -2.32) * mm, "end": v(4.84, -6.27) * mm});
            skArc(sketch, "E256", {"start": v(4.8, -6.27) * mm, "mid": v(4.84, -6.3) * mm, "end": v(4.88, -6.27) * mm});
            skArc(sketch, "E257", {"start": v(4.88, -6.27) * mm, "mid": v(4.84, -6.23) * mm, "end": v(4.8, -6.27) * mm});
            skLineSegment(sketch, "E258", {"start": v(4.84, -6.27) * mm, "end": v(4.84, -6.38) * mm});
            skArc(sketch, "E259", {"start": v(4.8, -6.38) * mm, "mid": v(4.84, -6.41) * mm, "end": v(4.88, -6.38) * mm});
            skArc(sketch, "E260", {"start": v(4.88, -6.38) * mm, "mid": v(4.84, -6.34) * mm, "end": v(4.8, -6.38) * mm});
            skLineSegment(sketch, "E261", {"start": v(4.84, -6.38) * mm, "end": v(7.43, -8.97) * mm});
            skArc(sketch, "E262", {"start": v(7.4, -8.97) * mm, "mid": v(7.43, -9) * mm, "end": v(7.47, -8.97) * mm});
            skArc(sketch, "E263", {"start": v(7.47, -8.97) * mm, "mid": v(7.43, -8.93) * mm, "end": v(7.4, -8.97) * mm});
            skLineSegment(sketch, "E264", {"start": v(7.43, -8.97) * mm, "end": v(8.57, -8.97) * mm});
            skArc(sketch, "E265", {"start": v(8.53, -8.97) * mm, "mid": v(8.57, -9) * mm, "end": v(8.61, -8.97) * mm});
            skArc(sketch, "E266", {"start": v(8.61, -8.97) * mm, "mid": v(8.57, -8.93) * mm, "end": v(8.53, -8.97) * mm});
            skLineSegment(sketch, "E267", {"start": v(8.57, -8.97) * mm, "end": v(9.38, -9.77) * mm});
            skArc(sketch, "E268", {"start": v(9.34, -9.77) * mm, "mid": v(9.38, -9.81) * mm, "end": v(9.42, -9.77) * mm});
            skArc(sketch, "E269", {"start": v(9.42, -9.77) * mm, "mid": v(9.38, -9.74) * mm, "end": v(9.34, -9.77) * mm});
            skLineSegment(sketch, "E270", {"start": v(9.38, -9.77) * mm, "end": v(9.4, -9.77) * mm});
            skArc(sketch, "E271", {"start": v(9.35, -9.77) * mm, "mid": v(9.4, -9.81) * mm, "end": v(9.43, -9.77) * mm});
            skArc(sketch, "E272", {"start": v(9.43, -9.77) * mm, "mid": v(9.4, -9.74) * mm, "end": v(9.35, -9.77) * mm});
            skLineSegment(sketch, "E273", {"start": v(9.4, -9.77) * mm, "end": v(23.3, -23.7) * mm});
            skArc(sketch, "E274", {"start": v(23.27, -23.7) * mm, "mid": v(23.3, -23.73) * mm, "end": v(23.35, -23.7) * mm});
            skArc(sketch, "E275", {"start": v(23.35, -23.7) * mm, "mid": v(23.3, -23.65) * mm, "end": v(23.27, -23.7) * mm});
            skLineSegment(sketch, "E276", {"start": v(5.3, -3.88) * mm, "end": v(5.08, -3.88) * mm});
            skArc(sketch, "E277", {"start": v(5.27, -3.88) * mm, "mid": v(5.3, -3.91) * mm, "end": v(5.34, -3.88) * mm});
            skArc(sketch, "E278", {"start": v(5.34, -3.88) * mm, "mid": v(5.3, -3.84) * mm, "end": v(5.27, -3.88) * mm});
            skArc(sketch, "E279", {"start": v(5.04, -3.88) * mm, "mid": v(5.08, -3.91) * mm, "end": v(5.12, -3.88) * mm});
            skArc(sketch, "E280", {"start": v(5.12, -3.88) * mm, "mid": v(5.08, -3.84) * mm, "end": v(5.04, -3.88) * mm});
            skLineSegment(sketch, "E281", {"start": v(5.08, -3.88) * mm, "end": v(3.66, -5.3) * mm});
            skArc(sketch, "E282", {"start": v(3.62, -5.3) * mm, "mid": v(3.66, -5.34) * mm, "end": v(3.7, -5.3) * mm});
            skArc(sketch, "E283", {"start": v(3.7, -5.3) * mm, "mid": v(3.66, -5.26) * mm, "end": v(3.62, -5.3) * mm});
            skLineSegment(sketch, "E284", {"start": v(3.66, -5.3) * mm, "end": v(3.66, -6.6) * mm});
            skArc(sketch, "E285", {"start": v(3.62, -6.6) * mm, "mid": v(3.66, -6.63) * mm, "end": v(3.7, -6.6) * mm});
            skArc(sketch, "E286", {"start": v(3.7, -6.6) * mm, "mid": v(3.66, -6.56) * mm, "end": v(3.62, -6.6) * mm});
            skLineSegment(sketch, "E287", {"start": v(3.66, -6.6) * mm, "end": v(16.5, -19.44) * mm});
            skArc(sketch, "E288", {"start": v(16.47, -19.44) * mm, "mid": v(16.5, -19.48) * mm, "end": v(16.55, -19.44) * mm});
            skArc(sketch, "E289", {"start": v(16.55, -19.44) * mm, "mid": v(16.5, -19.4) * mm, "end": v(16.47, -19.44) * mm});
            skLineSegment(sketch, "E290", {"start": v(16.5, -19.44) * mm, "end": v(16.52, -19.44) * mm});
            skArc(sketch, "E291", {"start": v(16.48, -19.44) * mm, "mid": v(16.52, -19.48) * mm, "end": v(16.56, -19.44) * mm});
            skArc(sketch, "E292", {"start": v(16.56, -19.44) * mm, "mid": v(16.52, -19.4) * mm, "end": v(16.48, -19.44) * mm});
            skLineSegment(sketch, "E293", {"start": v(16.52, -19.44) * mm, "end": v(20.77, -23.7) * mm});
            skArc(sketch, "E294", {"start": v(20.73, -23.7) * mm, "mid": v(20.77, -23.73) * mm, "end": v(20.8, -23.7) * mm});
            skArc(sketch, "E295", {"start": v(20.8, -23.7) * mm, "mid": v(20.77, -23.65) * mm, "end": v(20.73, -23.7) * mm});
            skLineSegment(sketch, "E296", {"start": v(5.02, -2.5) * mm, "end": v(5.02, -2.76) * mm});
            skArc(sketch, "E297", {"start": v(4.98, -2.5) * mm, "mid": v(5.02, -2.54) * mm, "end": v(5.06, -2.5) * mm});
            skArc(sketch, "E298", {"start": v(5.06, -2.5) * mm, "mid": v(5.02, -2.46) * mm, "end": v(4.98, -2.5) * mm});
            skArc(sketch, "E299", {"start": v(4.98, -2.76) * mm, "mid": v(5.02, -2.8) * mm, "end": v(5.06, -2.76) * mm});
            skArc(sketch, "E300", {"start": v(5.06, -2.76) * mm, "mid": v(5.02, -2.73) * mm, "end": v(4.98, -2.76) * mm});
            skLineSegment(sketch, "E301", {"start": v(5.02, -2.76) * mm, "end": v(1.15, -6.63) * mm});
            skArc(sketch, "E302", {"start": v(1.11, -6.63) * mm, "mid": v(1.15, -6.67) * mm, "end": v(1.19, -6.63) * mm});
            skArc(sketch, "E303", {"start": v(1.19, -6.63) * mm, "mid": v(1.15, -6.6) * mm, "end": v(1.11, -6.63) * mm});
            skLineSegment(sketch, "E304", {"start": v(1.15, -6.63) * mm, "end": v(6.99, -12.47) * mm});
            skArc(sketch, "E305", {"start": v(6.95, -12.47) * mm, "mid": v(6.99, -12.5) * mm, "end": v(7.03, -12.47) * mm});
            skArc(sketch, "E306", {"start": v(7.03, -12.47) * mm, "mid": v(6.99, -12.43) * mm, "end": v(6.95, -12.47) * mm});
            skLineSegment(sketch, "E307", {"start": v(6.99, -12.47) * mm, "end": v(7.01, -12.47) * mm});
            skArc(sketch, "E308", {"start": v(6.97, -12.47) * mm, "mid": v(7.01, -12.5) * mm, "end": v(7.05, -12.47) * mm});
            skArc(sketch, "E309", {"start": v(7.05, -12.47) * mm, "mid": v(7.01, -12.43) * mm, "end": v(6.97, -12.47) * mm});
            skLineSegment(sketch, "E310", {"start": v(7.01, -12.47) * mm, "end": v(18.23, -23.7) * mm});
            skArc(sketch, "E311", {"start": v(18.2, -23.7) * mm, "mid": v(18.23, -23.73) * mm, "end": v(18.27, -23.7) * mm});
            skArc(sketch, "E312", {"start": v(18.27, -23.7) * mm, "mid": v(18.23, -23.65) * mm, "end": v(18.2, -23.7) * mm});
            skLineSegment(sketch, "E313", {"start": v(6.14, 1.09) * mm, "end": v(5.96, 1.09) * mm});
            skArc(sketch, "E314", {"start": v(6.1, 1.09) * mm, "mid": v(6.14, 1.05) * mm, "end": v(6.18, 1.09) * mm});
            skArc(sketch, "E315", {"start": v(6.18, 1.09) * mm, "mid": v(6.14, 1.13) * mm, "end": v(6.1, 1.09) * mm});
            skArc(sketch, "E316", {"start": v(5.92, 1.09) * mm, "mid": v(5.96, 1.05) * mm, "end": v(6, 1.09) * mm});
            skArc(sketch, "E317", {"start": v(6, 1.09) * mm, "mid": v(5.96, 1.13) * mm, "end": v(5.92, 1.09) * mm});
            skLineSegment(sketch, "E318", {"start": v(5.96, 1.09) * mm, "end": v(-1.29, -6.16) * mm});
            skArc(sketch, "E319", {"start": v(-1.33, -6.16) * mm, "mid": v(-1.29, -6.2) * mm, "end": v(-1.25, -6.16) * mm});
            skArc(sketch, "E320", {"start": v(-1.25, -6.16) * mm, "mid": v(-1.29, -6.12) * mm, "end": v(-1.33, -6.16) * mm});
            skLineSegment(sketch, "E321", {"start": v(-1.29, -6.16) * mm, "end": v(-1.29, -6.7) * mm});
            skArc(sketch, "E322", {"start": v(-1.33, -6.7) * mm, "mid": v(-1.29, -6.73) * mm, "end": v(-1.25, -6.7) * mm});
            skArc(sketch, "E323", {"start": v(-1.25, -6.7) * mm, "mid": v(-1.29, -6.65) * mm, "end": v(-1.33, -6.7) * mm});
            skLineSegment(sketch, "E324", {"start": v(-1.29, -6.7) * mm, "end": v(6.29, -14.27) * mm});
            skArc(sketch, "E325", {"start": v(6.25, -14.27) * mm, "mid": v(6.29, -14.3) * mm, "end": v(6.33, -14.27) * mm});
            skArc(sketch, "E326", {"start": v(6.33, -14.27) * mm, "mid": v(6.29, -14.23) * mm, "end": v(6.25, -14.27) * mm});
            skLineSegment(sketch, "E327", {"start": v(6.29, -14.27) * mm, "end": v(6.29, -14.3) * mm});
            skArc(sketch, "E328", {"start": v(6.25, -14.3) * mm, "mid": v(6.29, -14.33) * mm, "end": v(6.33, -14.3) * mm});
            skArc(sketch, "E329", {"start": v(6.33, -14.3) * mm, "mid": v(6.29, -14.25) * mm, "end": v(6.25, -14.3) * mm});
            skLineSegment(sketch, "E330", {"start": v(6.29, -14.3) * mm, "end": v(15.69, -23.7) * mm});
            skArc(sketch, "E331", {"start": v(15.65, -23.7) * mm, "mid": v(15.69, -23.73) * mm, "end": v(15.73, -23.7) * mm});
            skArc(sketch, "E332", {"start": v(15.73, -23.7) * mm, "mid": v(15.69, -23.65) * mm, "end": v(15.65, -23.7) * mm});
            skLineSegment(sketch, "E333", {"start": v(5.96, 3.5) * mm, "end": v(5.96, 3.27) * mm});
            skArc(sketch, "E334", {"start": v(5.92, 3.5) * mm, "mid": v(5.96, 3.47) * mm, "end": v(6, 3.5) * mm});
            skArc(sketch, "E335", {"start": v(6, 3.5) * mm, "mid": v(5.96, 3.55) * mm, "end": v(5.92, 3.5) * mm});
            skArc(sketch, "E336", {"start": v(5.92, 3.27) * mm, "mid": v(5.96, 3.23) * mm, "end": v(6, 3.27) * mm});
            skArc(sketch, "E337", {"start": v(6, 3.27) * mm, "mid": v(5.96, 3.3) * mm, "end": v(5.92, 3.27) * mm});
            skLineSegment(sketch, "E338", {"start": v(5.96, 3.27) * mm, "end": v(-4.03, -6.72) * mm});
            skArc(sketch, "E339", {"start": v(-4.07, -6.72) * mm, "mid": v(-4.03, -6.76) * mm, "end": v(-4, -6.72) * mm});
            skArc(sketch, "E340", {"start": v(-4, -6.72) * mm, "mid": v(-4.03, -6.69) * mm, "end": v(-4.07, -6.72) * mm});
            skLineSegment(sketch, "E341", {"start": v(-4.03, -6.72) * mm, "end": v(4.64, -15.4) * mm});
            skArc(sketch, "E342", {"start": v(4.6, -15.4) * mm, "mid": v(4.64, -15.43) * mm, "end": v(4.67, -15.4) * mm});
            skArc(sketch, "E343", {"start": v(4.67, -15.4) * mm, "mid": v(4.64, -15.35) * mm, "end": v(4.6, -15.4) * mm});
            skLineSegment(sketch, "E344", {"start": v(4.64, -15.4) * mm, "end": v(4.66, -15.4) * mm});
            skArc(sketch, "E345", {"start": v(4.62, -15.4) * mm, "mid": v(4.66, -15.43) * mm, "end": v(4.7, -15.4) * mm});
            skArc(sketch, "E346", {"start": v(4.7, -15.4) * mm, "mid": v(4.66, -15.35) * mm, "end": v(4.62, -15.4) * mm});
            skLineSegment(sketch, "E347", {"start": v(4.66, -15.4) * mm, "end": v(8.5, -19.24) * mm});
            skArc(sketch, "E348", {"start": v(8.47, -19.24) * mm, "mid": v(8.5, -19.28) * mm, "end": v(8.55, -19.24) * mm});
            skArc(sketch, "E349", {"start": v(8.55, -19.24) * mm, "mid": v(8.5, -19.2) * mm, "end": v(8.47, -19.24) * mm});
            skLineSegment(sketch, "E350", {"start": v(8.5, -19.24) * mm, "end": v(8.5, -19.2) * mm});
            skArc(sketch, "E351", {"start": v(8.47, -19.2) * mm, "mid": v(8.5, -19.24) * mm, "end": v(8.55, -19.2) * mm});
            skArc(sketch, "E352", {"start": v(8.55, -19.2) * mm, "mid": v(8.5, -19.16) * mm, "end": v(8.47, -19.2) * mm});
            skLineSegment(sketch, "E353", {"start": v(8.5, -19.2) * mm, "end": v(13, -23.7) * mm});
            skArc(sketch, "E354", {"start": v(12.96, -23.7) * mm, "mid": v(13, -23.73) * mm, "end": v(13.04, -23.7) * mm});
            skArc(sketch, "E355", {"start": v(13.04, -23.7) * mm, "mid": v(13, -23.65) * mm, "end": v(12.96, -23.7) * mm});
            skLineSegment(sketch, "E356", {"start": v(13, -23.7) * mm, "end": v(13.15, -23.7) * mm});
            skArc(sketch, "E357", {"start": v(13.11, -23.7) * mm, "mid": v(13.15, -23.73) * mm, "end": v(13.19, -23.7) * mm});
            skArc(sketch, "E358", {"start": v(13.19, -23.7) * mm, "mid": v(13.15, -23.65) * mm, "end": v(13.11, -23.7) * mm});
            skLineSegment(sketch, "E359", {"start": v(10.6, -23.7) * mm, "end": v(-5.75, -7.33) * mm});
            skArc(sketch, "E360", {"start": v(10.57, -23.7) * mm, "mid": v(10.6, -23.73) * mm, "end": v(10.65, -23.7) * mm});
            skArc(sketch, "E361", {"start": v(10.65, -23.7) * mm, "mid": v(10.6, -23.65) * mm, "end": v(10.57, -23.7) * mm});
            skArc(sketch, "E362", {"start": v(-5.78, -7.33) * mm, "mid": v(-5.75, -7.37) * mm, "end": v(-5.7, -7.33) * mm});
            skArc(sketch, "E363", {"start": v(-5.7, -7.33) * mm, "mid": v(-5.75, -7.3) * mm, "end": v(-5.78, -7.33) * mm});
            skLineSegment(sketch, "E364", {"start": v(-5.75, -7.33) * mm, "end": v(-5.75, -6.68) * mm});
            skArc(sketch, "E365", {"start": v(-5.78, -6.68) * mm, "mid": v(-5.75, -6.72) * mm, "end": v(-5.7, -6.68) * mm});
            skArc(sketch, "E366", {"start": v(-5.7, -6.68) * mm, "mid": v(-5.75, -6.64) * mm, "end": v(-5.78, -6.68) * mm});
            skLineSegment(sketch, "E367", {"start": v(-5.75, -6.68) * mm, "end": v(-4.4, -5.33) * mm});
            skArc(sketch, "E368", {"start": v(-4.43, -5.33) * mm, "mid": v(-4.4, -5.37) * mm, "end": v(-4.36, -5.33) * mm});
            skArc(sketch, "E369", {"start": v(-4.36, -5.33) * mm, "mid": v(-4.4, -5.3) * mm, "end": v(-4.43, -5.33) * mm});
            skLineSegment(sketch, "E370", {"start": v(-4.4, -5.33) * mm, "end": v(-4.4, 0.79) * mm});
            skArc(sketch, "E371", {"start": v(-4.43, 0.79) * mm, "mid": v(-4.4, 0.75) * mm, "end": v(-4.36, 0.79) * mm});
            skArc(sketch, "E372", {"start": v(-4.36, 0.79) * mm, "mid": v(-4.4, 0.83) * mm, "end": v(-4.43, 0.79) * mm});
            skLineSegment(sketch, "E373", {"start": v(-4.4, 0.79) * mm, "end": v(-4.65, 0.79) * mm});
            skArc(sketch, "E374", {"start": v(-4.69, 0.79) * mm, "mid": v(-4.65, 0.75) * mm, "end": v(-4.61, 0.79) * mm});
            skArc(sketch, "E375", {"start": v(-4.61, 0.79) * mm, "mid": v(-4.65, 0.83) * mm, "end": v(-4.69, 0.79) * mm});
            skLineSegment(sketch, "E376", {"start": v(-4.65, 0.79) * mm, "end": v(-4.81, 0.95) * mm});
            skArc(sketch, "E377", {"start": v(-4.85, 0.95) * mm, "mid": v(-4.81, 0.9) * mm, "end": v(-4.77, 0.95) * mm});
            skArc(sketch, "E378", {"start": v(-4.77, 0.95) * mm, "mid": v(-4.81, 0.99) * mm, "end": v(-4.85, 0.95) * mm});
            skLineSegment(sketch, "E379", {"start": v(-14.38, 0.34) * mm, "end": v(-11.81, 0.34) * mm});
            skArc(sketch, "E380", {"start": v(-14.41, 0.34) * mm, "mid": v(-14.38, 0.3) * mm, "end": v(-14.34, 0.34) * mm});
            skArc(sketch, "E381", {"start": v(-14.34, 0.34) * mm, "mid": v(-14.38, 0.38) * mm, "end": v(-14.41, 0.34) * mm});
            skArc(sketch, "E382", {"start": v(-11.85, 0.34) * mm, "mid": v(-11.81, 0.3) * mm, "end": v(-11.78, 0.34) * mm});
            skArc(sketch, "E383", {"start": v(-11.78, 0.34) * mm, "mid": v(-11.81, 0.38) * mm, "end": v(-11.85, 0.34) * mm});
            skLineSegment(sketch, "E384", {"start": v(-11.81, 0.34) * mm, "end": v(-7.74, -3.73) * mm});
            skArc(sketch, "E385", {"start": v(-7.78, -3.73) * mm, "mid": v(-7.74, -3.76) * mm, "end": v(-7.7, -3.73) * mm});
            skArc(sketch, "E386", {"start": v(-7.7, -3.73) * mm, "mid": v(-7.74, -3.69) * mm, "end": v(-7.78, -3.73) * mm});
            skLineSegment(sketch, "E387", {"start": v(-7.74, -3.73) * mm, "end": v(-7.74, -7.88) * mm});
            skArc(sketch, "E388", {"start": v(-7.78, -7.88) * mm, "mid": v(-7.74, -7.91) * mm, "end": v(-7.7, -7.88) * mm});
            skArc(sketch, "E389", {"start": v(-7.7, -7.88) * mm, "mid": v(-7.74, -7.84) * mm, "end": v(-7.78, -7.88) * mm});
            skLineSegment(sketch, "E390", {"start": v(-7.74, -7.88) * mm, "end": v(8.07, -23.7) * mm});
            skArc(sketch, "E391", {"start": v(8.03, -23.7) * mm, "mid": v(8.07, -23.73) * mm, "end": v(8.1, -23.7) * mm});
            skArc(sketch, "E392", {"start": v(8.1, -23.7) * mm, "mid": v(8.07, -23.65) * mm, "end": v(8.03, -23.7) * mm});
            skLineSegment(sketch, "E393", {"start": v(-14.38, -2.2) * mm, "end": v(-12.18, -2.2) * mm});
            skArc(sketch, "E394", {"start": v(-14.41, -2.2) * mm, "mid": v(-14.38, -2.24) * mm, "end": v(-14.34, -2.2) * mm});
            skArc(sketch, "E395", {"start": v(-14.34, -2.2) * mm, "mid": v(-14.38, -2.16) * mm, "end": v(-14.41, -2.2) * mm});
            skArc(sketch, "E396", {"start": v(-12.22, -2.2) * mm, "mid": v(-12.18, -2.24) * mm, "end": v(-12.14, -2.2) * mm});
            skArc(sketch, "E397", {"start": v(-12.14, -2.2) * mm, "mid": v(-12.18, -2.16) * mm, "end": v(-12.22, -2.2) * mm});
            skLineSegment(sketch, "E398", {"start": v(-12.18, -2.2) * mm, "end": v(-10.41, -3.96) * mm});
            skArc(sketch, "E399", {"start": v(-10.45, -3.96) * mm, "mid": v(-10.41, -4) * mm, "end": v(-10.38, -3.96) * mm});
            skArc(sketch, "E400", {"start": v(-10.38, -3.96) * mm, "mid": v(-10.41, -3.92) * mm, "end": v(-10.45, -3.96) * mm});
            skLineSegment(sketch, "E401", {"start": v(-10.41, -3.96) * mm, "end": v(-10.41, -10.29) * mm});
            skArc(sketch, "E402", {"start": v(-10.45, -10.29) * mm, "mid": v(-10.41, -10.33) * mm, "end": v(-10.38, -10.29) * mm});
            skArc(sketch, "E403", {"start": v(-10.38, -10.29) * mm, "mid": v(-10.41, -10.25) * mm, "end": v(-10.45, -10.29) * mm});
            skLineSegment(sketch, "E404", {"start": v(-10.41, -10.29) * mm, "end": v(2.99, -23.7) * mm});
            skArc(sketch, "E405", {"start": v(2.95, -23.7) * mm, "mid": v(2.99, -23.73) * mm, "end": v(3.03, -23.7) * mm});
            skArc(sketch, "E406", {"start": v(3.03, -23.7) * mm, "mid": v(2.99, -23.65) * mm, "end": v(2.95, -23.7) * mm});
            skLineSegment(sketch, "E407", {"start": v(-13.13, -6) * mm, "end": v(-13.13, -10.1) * mm});
            skArc(sketch, "E408", {"start": v(-13.17, -6) * mm, "mid": v(-13.13, -6.03) * mm, "end": v(-13.1, -6) * mm});
            skArc(sketch, "E409", {"start": v(-13.1, -6) * mm, "mid": v(-13.13, -5.96) * mm, "end": v(-13.17, -6) * mm});
            skArc(sketch, "E410", {"start": v(-13.17, -10.1) * mm, "mid": v(-13.13, -10.15) * mm, "end": v(-13.1, -10.1) * mm});
            skArc(sketch, "E411", {"start": v(-13.1, -10.1) * mm, "mid": v(-13.13, -10.07) * mm, "end": v(-13.17, -10.1) * mm});
            skLineSegment(sketch, "E412", {"start": v(-13.13, -10.1) * mm, "end": v(0.45, -23.7) * mm});
            skArc(sketch, "E413", {"start": v(0.41, -23.7) * mm, "mid": v(0.45, -23.73) * mm, "end": v(0.49, -23.7) * mm});
            skArc(sketch, "E414", {"start": v(0.49, -23.7) * mm, "mid": v(0.45, -23.65) * mm, "end": v(0.41, -23.7) * mm});
            skLineSegment(sketch, "E415", {"start": v(-15.67, -6) * mm, "end": v(-15.67, -10.1) * mm});
            skArc(sketch, "E416", {"start": v(-15.7, -6) * mm, "mid": v(-15.67, -6.03) * mm, "end": v(-15.63, -6) * mm});
            skArc(sketch, "E417", {"start": v(-15.63, -6) * mm, "mid": v(-15.67, -5.96) * mm, "end": v(-15.7, -6) * mm});
            skArc(sketch, "E418", {"start": v(-15.7, -10.1) * mm, "mid": v(-15.67, -10.15) * mm, "end": v(-15.63, -10.1) * mm});
            skArc(sketch, "E419", {"start": v(-15.63, -10.1) * mm, "mid": v(-15.67, -10.07) * mm, "end": v(-15.7, -10.1) * mm});
            skLineSegment(sketch, "E420", {"start": v(-15.67, -10.1) * mm, "end": v(-2.1, -23.7) * mm});
            skArc(sketch, "E421", {"start": v(-2.13, -23.7) * mm, "mid": v(-2.1, -23.73) * mm, "end": v(-2.05, -23.7) * mm});
            skArc(sketch, "E422", {"start": v(-2.05, -23.7) * mm, "mid": v(-2.1, -23.65) * mm, "end": v(-2.13, -23.7) * mm});
            skLineSegment(sketch, "E423", {"start": v(-15.65, -0.93) * mm, "end": v(-17.84, -0.93) * mm});
            skArc(sketch, "E424", {"start": v(-15.68, -0.93) * mm, "mid": v(-15.65, -0.97) * mm, "end": v(-15.6, -0.93) * mm});
            skArc(sketch, "E425", {"start": v(-15.6, -0.93) * mm, "mid": v(-15.65, -0.89) * mm, "end": v(-15.68, -0.93) * mm});
            skArc(sketch, "E426", {"start": v(-17.88, -0.93) * mm, "mid": v(-17.84, -0.97) * mm, "end": v(-17.8, -0.93) * mm});
            skArc(sketch, "E427", {"start": v(-17.8, -0.93) * mm, "mid": v(-17.84, -0.89) * mm, "end": v(-17.88, -0.93) * mm});
            skLineSegment(sketch, "E428", {"start": v(-17.84, -0.93) * mm, "end": v(-20.72, -3.8) * mm});
            skArc(sketch, "E429", {"start": v(-20.75, -3.8) * mm, "mid": v(-20.72, -3.84) * mm, "end": v(-20.68, -3.8) * mm});
            skArc(sketch, "E430", {"start": v(-20.68, -3.8) * mm, "mid": v(-20.72, -3.76) * mm, "end": v(-20.75, -3.8) * mm});
            skLineSegment(sketch, "E431", {"start": v(-20.72, -3.8) * mm, "end": v(-20.72, -12.68) * mm});
            skArc(sketch, "E432", {"start": v(-20.75, -12.68) * mm, "mid": v(-20.72, -12.72) * mm, "end": v(-20.68, -12.68) * mm});
            skArc(sketch, "E433", {"start": v(-20.68, -12.68) * mm, "mid": v(-20.72, -12.64) * mm, "end": v(-20.75, -12.68) * mm});
            skLineSegment(sketch, "E434", {"start": v(-20.72, -12.68) * mm, "end": v(-9.71, -23.7) * mm});
            skArc(sketch, "E435", {"start": v(-9.75, -23.7) * mm, "mid": v(-9.71, -23.73) * mm, "end": v(-9.67, -23.7) * mm});
            skArc(sketch, "E436", {"start": v(-9.67, -23.7) * mm, "mid": v(-9.71, -23.65) * mm, "end": v(-9.75, -23.7) * mm});
            skLineSegment(sketch, "E437", {"start": v(-15.65, 0.34) * mm, "end": v(-20.12, 0.34) * mm});
            skArc(sketch, "E438", {"start": v(-15.68, 0.34) * mm, "mid": v(-15.65, 0.3) * mm, "end": v(-15.6, 0.34) * mm});
            skArc(sketch, "E439", {"start": v(-15.6, 0.34) * mm, "mid": v(-15.65, 0.38) * mm, "end": v(-15.68, 0.34) * mm});
            skArc(sketch, "E440", {"start": v(-20.15, 0.34) * mm, "mid": v(-20.12, 0.3) * mm, "end": v(-20.08, 0.34) * mm});
            skArc(sketch, "E441", {"start": v(-20.08, 0.34) * mm, "mid": v(-20.12, 0.38) * mm, "end": v(-20.15, 0.34) * mm});
            skLineSegment(sketch, "E442", {"start": v(-20.12, 0.34) * mm, "end": v(-22.16, -1.7) * mm});
            skArc(sketch, "E443", {"start": v(-22.2, -1.7) * mm, "mid": v(-22.16, -1.74) * mm, "end": v(-22.13, -1.7) * mm});
            skArc(sketch, "E444", {"start": v(-22.13, -1.7) * mm, "mid": v(-22.16, -1.67) * mm, "end": v(-22.2, -1.7) * mm});
            skLineSegment(sketch, "E445", {"start": v(-22.16, -1.7) * mm, "end": v(-22.16, -13.78) * mm});
            skArc(sketch, "E446", {"start": v(-22.2, -13.78) * mm, "mid": v(-22.16, -13.82) * mm, "end": v(-22.13, -13.78) * mm});
            skArc(sketch, "E447", {"start": v(-22.13, -13.78) * mm, "mid": v(-22.16, -13.74) * mm, "end": v(-22.2, -13.78) * mm});
            skLineSegment(sketch, "E448", {"start": v(-22.16, -13.78) * mm, "end": v(-12.25, -23.7) * mm});
            skArc(sketch, "E449", {"start": v(-12.29, -23.7) * mm, "mid": v(-12.25, -23.73) * mm, "end": v(-12.21, -23.7) * mm});
            skArc(sketch, "E450", {"start": v(-12.21, -23.7) * mm, "mid": v(-12.25, -23.65) * mm, "end": v(-12.29, -23.7) * mm});
            skLineSegment(sketch, "E451", {"start": v(16.76, 3.82) * mm, "end": v(16.76, 23.25) * mm});
            skArc(sketch, "E452", {"start": v(16.45, 3.82) * mm, "mid": v(16.76, 3.5) * mm, "end": v(17.08, 3.82) * mm});
            skArc(sketch, "E453", {"start": v(17.08, 3.82) * mm, "mid": v(16.76, 4.14) * mm, "end": v(16.45, 3.82) * mm});
            skArc(sketch, "E454", {"start": v(16.45, 23.25) * mm, "mid": v(16.76, 22.94) * mm, "end": v(17.08, 23.25) * mm});
            skArc(sketch, "E455", {"start": v(17.08, 23.25) * mm, "mid": v(16.76, 23.57) * mm, "end": v(16.45, 23.25) * mm});
            skLineSegment(sketch, "E456", {"start": v(16.76, 23.25) * mm, "end": v(16.33, 23.69) * mm});
            skArc(sketch, "E457", {"start": v(16.73, 23.25) * mm, "mid": v(16.76, 23.22) * mm, "end": v(16.8, 23.25) * mm});
            skArc(sketch, "E458", {"start": v(16.8, 23.25) * mm, "mid": v(16.76, 23.3) * mm, "end": v(16.73, 23.25) * mm});
            skArc(sketch, "E459", {"start": v(16.3, 23.69) * mm, "mid": v(16.33, 23.65) * mm, "end": v(16.37, 23.69) * mm});
            skArc(sketch, "E460", {"start": v(16.37, 23.69) * mm, "mid": v(16.33, 23.72) * mm, "end": v(16.3, 23.69) * mm});
            skLineSegment(sketch, "E461", {"start": v(14.22, 3.82) * mm, "end": v(14.22, 23.25) * mm});
            skArc(sketch, "E462", {"start": v(13.9, 3.82) * mm, "mid": v(14.22, 3.5) * mm, "end": v(14.54, 3.82) * mm});
            skArc(sketch, "E463", {"start": v(14.54, 3.82) * mm, "mid": v(14.22, 4.14) * mm, "end": v(13.9, 3.82) * mm});
            skArc(sketch, "E464", {"start": v(13.9, 23.25) * mm, "mid": v(14.22, 22.94) * mm, "end": v(14.54, 23.25) * mm});
            skArc(sketch, "E465", {"start": v(14.54, 23.25) * mm, "mid": v(14.22, 23.57) * mm, "end": v(13.9, 23.25) * mm});
            skLineSegment(sketch, "E466", {"start": v(14.22, 23.25) * mm, "end": v(13.79, 23.69) * mm});
            skArc(sketch, "E467", {"start": v(14.19, 23.25) * mm, "mid": v(14.22, 23.22) * mm, "end": v(14.26, 23.25) * mm});
            skArc(sketch, "E468", {"start": v(14.26, 23.25) * mm, "mid": v(14.22, 23.3) * mm, "end": v(14.19, 23.25) * mm});
            skArc(sketch, "E469", {"start": v(13.75, 23.69) * mm, "mid": v(13.79, 23.65) * mm, "end": v(13.83, 23.69) * mm});
            skArc(sketch, "E470", {"start": v(13.83, 23.69) * mm, "mid": v(13.79, 23.72) * mm, "end": v(13.75, 23.69) * mm});
            skLineSegment(sketch, "E471", {"start": v(36.6, 14.78) * mm, "end": v(-20.06, 14.78) * mm});
            skArc(sketch, "E472", {"start": v(36.57, 14.78) * mm, "mid": v(36.6, 14.74) * mm, "end": v(36.65, 14.78) * mm});
            skArc(sketch, "E473", {"start": v(36.65, 14.78) * mm, "mid": v(36.6, 14.82) * mm, "end": v(36.57, 14.78) * mm});
            skArc(sketch, "E474", {"start": v(-20.1, 14.78) * mm, "mid": v(-20.06, 14.74) * mm, "end": v(-20.02, 14.78) * mm});
            skArc(sketch, "E475", {"start": v(-20.02, 14.78) * mm, "mid": v(-20.06, 14.82) * mm, "end": v(-20.1, 14.78) * mm});
            skLineSegment(sketch, "E476", {"start": v(-20.06, 14.78) * mm, "end": v(-24.33, 10.5) * mm});
            skArc(sketch, "E477", {"start": v(-24.37, 10.5) * mm, "mid": v(-24.33, 10.46) * mm, "end": v(-24.3, 10.5) * mm});
            skArc(sketch, "E478", {"start": v(-24.3, 10.5) * mm, "mid": v(-24.33, 10.54) * mm, "end": v(-24.37, 10.5) * mm});
            skLineSegment(sketch, "E479", {"start": v(-24.33, 10.5) * mm, "end": v(-24.33, 3.76) * mm});
            skArc(sketch, "E480", {"start": v(-24.37, 3.76) * mm, "mid": v(-24.33, 3.73) * mm, "end": v(-24.3, 3.76) * mm});
            skArc(sketch, "E481", {"start": v(-24.3, 3.76) * mm, "mid": v(-24.33, 3.8) * mm, "end": v(-24.37, 3.76) * mm});
            skLineSegment(sketch, "E482", {"start": v(-24.33, 3.76) * mm, "end": v(-20.28, -0.29) * mm});
            skArc(sketch, "E483", {"start": v(-20.32, -0.29) * mm, "mid": v(-20.28, -0.33) * mm, "end": v(-20.24, -0.29) * mm});
            skArc(sketch, "E484", {"start": v(-20.24, -0.29) * mm, "mid": v(-20.28, -0.25) * mm, "end": v(-20.32, -0.29) * mm});
            skLineSegment(sketch, "E485", {"start": v(-20.28, -0.29) * mm, "end": v(-15.01, -0.29) * mm});
            skArc(sketch, "E486", {"start": v(-15.05, -0.29) * mm, "mid": v(-15.01, -0.33) * mm, "end": v(-14.98, -0.29) * mm});
            skArc(sketch, "E487", {"start": v(-14.98, -0.29) * mm, "mid": v(-15.01, -0.25) * mm, "end": v(-15.05, -0.29) * mm});
            skLineSegment(sketch, "E488", {"start": v(-15.01, -0.29) * mm, "end": v(-14.38, -0.93) * mm});
            skLineSegment(sketch, "E489", {"start": v(36.6, 9.7) * mm, "end": v(-19.47, 9.7) * mm});
            skArc(sketch, "E490", {"start": v(36.57, 9.7) * mm, "mid": v(36.6, 9.66) * mm, "end": v(36.65, 9.7) * mm});
            skArc(sketch, "E491", {"start": v(36.65, 9.7) * mm, "mid": v(36.6, 9.74) * mm, "end": v(36.57, 9.7) * mm});
            skArc(sketch, "E492", {"start": v(-19.51, 9.7) * mm, "mid": v(-19.47, 9.66) * mm, "end": v(-19.44, 9.7) * mm});
            skArc(sketch, "E493", {"start": v(-19.44, 9.7) * mm, "mid": v(-19.47, 9.74) * mm, "end": v(-19.51, 9.7) * mm});
            skLineSegment(sketch, "E494", {"start": v(-19.47, 9.7) * mm, "end": v(-21.1, 8.06) * mm});
            skArc(sketch, "E495", {"start": v(-21.15, 8.06) * mm, "mid": v(-21.1, 8.03) * mm, "end": v(-21.07, 8.06) * mm});
            skArc(sketch, "E496", {"start": v(-21.07, 8.06) * mm, "mid": v(-21.1, 8.1) * mm, "end": v(-21.15, 8.06) * mm});
            skLineSegment(sketch, "E497", {"start": v(-21.1, 8.06) * mm, "end": v(-21.1, 3.76) * mm});
            skArc(sketch, "E498", {"start": v(-21.15, 3.76) * mm, "mid": v(-21.1, 3.72) * mm, "end": v(-21.07, 3.76) * mm});
            skArc(sketch, "E499", {"start": v(-21.07, 3.76) * mm, "mid": v(-21.1, 3.8) * mm, "end": v(-21.15, 3.76) * mm});
            skLineSegment(sketch, "E500", {"start": v(-21.1, 3.76) * mm, "end": v(-18.99, 1.64) * mm});
            skArc(sketch, "E501", {"start": v(-19.03, 1.64) * mm, "mid": v(-18.99, 1.6) * mm, "end": v(-18.95, 1.64) * mm});
            skArc(sketch, "E502", {"start": v(-18.95, 1.64) * mm, "mid": v(-18.99, 1.67) * mm, "end": v(-19.03, 1.64) * mm});
            skLineSegment(sketch, "E503", {"start": v(-18.99, 1.64) * mm, "end": v(-15.67, 1.64) * mm});
            skArc(sketch, "E504", {"start": v(-15.7, 1.64) * mm, "mid": v(-15.67, 1.6) * mm, "end": v(-15.63, 1.64) * mm});
            skArc(sketch, "E505", {"start": v(-15.63, 1.64) * mm, "mid": v(-15.67, 1.67) * mm, "end": v(-15.7, 1.64) * mm});
            skLineSegment(sketch, "E506", {"start": v(-15.67, 1.64) * mm, "end": v(-14.38, 0.34) * mm});
            skLineSegment(sketch, "E507", {"start": v(36.6, 19.86) * mm, "end": v(-17.28, 19.86) * mm});
            skArc(sketch, "E508", {"start": v(36.57, 19.86) * mm, "mid": v(36.6, 19.82) * mm, "end": v(36.65, 19.86) * mm});
            skArc(sketch, "E509", {"start": v(36.65, 19.86) * mm, "mid": v(36.6, 19.9) * mm, "end": v(36.57, 19.86) * mm});
            skArc(sketch, "E510", {"start": v(-17.32, 19.86) * mm, "mid": v(-17.28, 19.82) * mm, "end": v(-17.24, 19.86) * mm});
            skArc(sketch, "E511", {"start": v(-17.24, 19.86) * mm, "mid": v(-17.28, 19.9) * mm, "end": v(-17.32, 19.86) * mm});
            skLineSegment(sketch, "E512", {"start": v(-17.28, 19.86) * mm, "end": v(-26.38, 10.76) * mm});
            skArc(sketch, "E513", {"start": v(-26.42, 10.76) * mm, "mid": v(-26.38, 10.73) * mm, "end": v(-26.34, 10.76) * mm});
            skArc(sketch, "E514", {"start": v(-26.34, 10.76) * mm, "mid": v(-26.38, 10.8) * mm, "end": v(-26.42, 10.76) * mm});
            skLineSegment(sketch, "E515", {"start": v(-26.38, 10.76) * mm, "end": v(-26.38, 2.47) * mm});
            skArc(sketch, "E516", {"start": v(-26.42, 2.47) * mm, "mid": v(-26.38, 2.43) * mm, "end": v(-26.34, 2.47) * mm});
            skArc(sketch, "E517", {"start": v(-26.34, 2.47) * mm, "mid": v(-26.38, 2.5) * mm, "end": v(-26.42, 2.47) * mm});
            skLineSegment(sketch, "E518", {"start": v(-26.38, 2.47) * mm, "end": v(-18.7, -5.21) * mm});
            skArc(sketch, "E519", {"start": v(-18.74, -5.21) * mm, "mid": v(-18.7, -5.25) * mm, "end": v(-18.66, -5.21) * mm});
            skArc(sketch, "E520", {"start": v(-18.66, -5.21) * mm, "mid": v(-18.7, -5.17) * mm, "end": v(-18.74, -5.21) * mm});
            skLineSegment(sketch, "E521", {"start": v(-18.7, -5.21) * mm, "end": v(-17.4, -5.21) * mm});
            skArc(sketch, "E522", {"start": v(-17.43, -5.21) * mm, "mid": v(-17.4, -5.25) * mm, "end": v(-17.36, -5.21) * mm});
            skArc(sketch, "E523", {"start": v(-17.36, -5.21) * mm, "mid": v(-17.4, -5.17) * mm, "end": v(-17.43, -5.21) * mm});
            skLineSegment(sketch, "E524", {"start": v(-17.4, -5.21) * mm, "end": v(-14.38, -2.2) * mm});
            skLineSegment(sketch, "E525", {"start": v(36.6, 17.32) * mm, "end": v(-18.74, 17.32) * mm});
            skArc(sketch, "E526", {"start": v(36.57, 17.32) * mm, "mid": v(36.6, 17.28) * mm, "end": v(36.65, 17.32) * mm});
            skArc(sketch, "E527", {"start": v(36.65, 17.32) * mm, "mid": v(36.6, 17.36) * mm, "end": v(36.57, 17.32) * mm});
            skArc(sketch, "E528", {"start": v(-18.78, 17.32) * mm, "mid": v(-18.74, 17.28) * mm, "end": v(-18.7, 17.32) * mm});
            skArc(sketch, "E529", {"start": v(-18.7, 17.32) * mm, "mid": v(-18.74, 17.36) * mm, "end": v(-18.78, 17.32) * mm});
            skLineSegment(sketch, "E530", {"start": v(-18.74, 17.32) * mm, "end": v(-25.12, 10.94) * mm});
            skArc(sketch, "E531", {"start": v(-25.16, 10.94) * mm, "mid": v(-25.12, 10.9) * mm, "end": v(-25.08, 10.94) * mm});
            skArc(sketch, "E532", {"start": v(-25.08, 10.94) * mm, "mid": v(-25.12, 10.98) * mm, "end": v(-25.16, 10.94) * mm});
            skLineSegment(sketch, "E533", {"start": v(-25.12, 10.94) * mm, "end": v(-25.12, 3.35) * mm});
            skArc(sketch, "E534", {"start": v(-25.16, 3.35) * mm, "mid": v(-25.12, 3.31) * mm, "end": v(-25.08, 3.35) * mm});
            skArc(sketch, "E535", {"start": v(-25.08, 3.35) * mm, "mid": v(-25.12, 3.39) * mm, "end": v(-25.16, 3.35) * mm});
            skLineSegment(sketch, "E536", {"start": v(-25.12, 3.35) * mm, "end": v(-20.9, -0.87) * mm});
            skArc(sketch, "E537", {"start": v(-20.94, -0.87) * mm, "mid": v(-20.9, -0.9) * mm, "end": v(-20.86, -0.87) * mm});
            skArc(sketch, "E538", {"start": v(-20.86, -0.87) * mm, "mid": v(-20.9, -0.83) * mm, "end": v(-20.94, -0.87) * mm});
            skLineSegment(sketch, "E539", {"start": v(-20.9, -0.87) * mm, "end": v(-15.7, -0.87) * mm});
            skArc(sketch, "E540", {"start": v(-15.74, -0.87) * mm, "mid": v(-15.7, -0.9) * mm, "end": v(-15.66, -0.87) * mm});
            skArc(sketch, "E541", {"start": v(-15.66, -0.87) * mm, "mid": v(-15.7, -0.83) * mm, "end": v(-15.74, -0.87) * mm});
            skLineSegment(sketch, "E542", {"start": v(-15.7, -0.87) * mm, "end": v(-15.65, -0.93) * mm});
            skLineSegment(sketch, "E543", {"start": v(36.6, 12.24) * mm, "end": v(-20.34, 12.24) * mm});
            skArc(sketch, "E544", {"start": v(36.57, 12.24) * mm, "mid": v(36.6, 12.2) * mm, "end": v(36.65, 12.24) * mm});
            skArc(sketch, "E545", {"start": v(36.65, 12.24) * mm, "mid": v(36.6, 12.28) * mm, "end": v(36.57, 12.24) * mm});
            skArc(sketch, "E546", {"start": v(-20.38, 12.24) * mm, "mid": v(-20.34, 12.2) * mm, "end": v(-20.3, 12.24) * mm});
            skArc(sketch, "E547", {"start": v(-20.3, 12.24) * mm, "mid": v(-20.34, 12.28) * mm, "end": v(-20.38, 12.24) * mm});
            skLineSegment(sketch, "E548", {"start": v(-20.34, 12.24) * mm, "end": v(-22.97, 9.6) * mm});
            skArc(sketch, "E549", {"start": v(-23.01, 9.6) * mm, "mid": v(-22.97, 9.57) * mm, "end": v(-22.94, 9.6) * mm});
            skArc(sketch, "E550", {"start": v(-22.94, 9.6) * mm, "mid": v(-22.97, 9.64) * mm, "end": v(-23.01, 9.6) * mm});
            skLineSegment(sketch, "E551", {"start": v(-22.97, 9.6) * mm, "end": v(-22.97, 3.7) * mm});
            skArc(sketch, "E552", {"start": v(-23.01, 3.7) * mm, "mid": v(-22.97, 3.66) * mm, "end": v(-22.94, 3.7) * mm});
            skArc(sketch, "E553", {"start": v(-22.94, 3.7) * mm, "mid": v(-22.97, 3.73) * mm, "end": v(-23.01, 3.7) * mm});
            skLineSegment(sketch, "E554", {"start": v(-22.97, 3.7) * mm, "end": v(-19.82, 0.54) * mm});
            skArc(sketch, "E555", {"start": v(-19.86, 0.54) * mm, "mid": v(-19.82, 0.5) * mm, "end": v(-19.78, 0.54) * mm});
            skArc(sketch, "E556", {"start": v(-19.78, 0.54) * mm, "mid": v(-19.82, 0.58) * mm, "end": v(-19.86, 0.54) * mm});
            skLineSegment(sketch, "E557", {"start": v(-19.82, 0.54) * mm, "end": v(-15.85, 0.54) * mm});
            skArc(sketch, "E558", {"start": v(-15.89, 0.54) * mm, "mid": v(-15.85, 0.5) * mm, "end": v(-15.8, 0.54) * mm});
            skArc(sketch, "E559", {"start": v(-15.8, 0.54) * mm, "mid": v(-15.85, 0.58) * mm, "end": v(-15.89, 0.54) * mm});
            skLineSegment(sketch, "E560", {"start": v(-15.85, 0.54) * mm, "end": v(-15.65, 0.34) * mm});
            skCircle(sketch, "E561", {"center": v(-13.13, -6) * mm, "radius": 0.32 * mm});
            skCircle(sketch, "E562", {"center": v(-15.67, -6) * mm, "radius": 0.32 * mm});
            skCircle(sketch, "E563", {"center": v(-18.2, -6) * mm, "radius": 0.32 * mm});
            skCircle(sketch, "E564", {"center": v(18.52, -0.2) * mm, "radius": 0.32 * mm});
            skCircle(sketch, "E565", {"center": v(5.02, -2.5) * mm, "radius": 0.32 * mm});
            skCircle(sketch, "E566", {"center": v(5.3, -3.88) * mm, "radius": 0.32 * mm});
            skCircle(sketch, "E567", {"center": v(-4.81, 0.95) * mm, "radius": 0.32 * mm});
            skCircle(sketch, "E568", {"center": v(5.96, 3.5) * mm, "radius": 0.32 * mm});
            skCircle(sketch, "E569", {"center": v(8.79, 3.47) * mm, "radius": 0.32 * mm});
            skCircle(sketch, "E570", {"center": v(6.14, 1.09) * mm, "radius": 0.32 * mm});
            skCircle(sketch, "E571", {"center": v(15.12, -6.13) * mm, "radius": 0.32 * mm});
            skCircle(sketch, "E572", {"center": v(7.97, -6.18) * mm, "radius": 0.32 * mm});
            skCircle(sketch, "E573", {"center": v(30.93, -23.7) * mm, "radius": 0.55 * mm});
            skCircle(sketch, "E574", {"center": v(28.39, -23.7) * mm, "radius": 0.55 * mm});
            skCircle(sketch, "E575", {"center": v(25.85, -23.7) * mm, "radius": 0.55 * mm});
            skCircle(sketch, "E576", {"center": v(23.3, -23.7) * mm, "radius": 0.55 * mm});
            skCircle(sketch, "E577", {"center": v(20.77, -23.7) * mm, "radius": 0.55 * mm});
            skCircle(sketch, "E578", {"center": v(18.23, -23.7) * mm, "radius": 0.55 * mm});
            skCircle(sketch, "E579", {"center": v(15.69, -23.7) * mm, "radius": 0.55 * mm});
            skCircle(sketch, "E580", {"center": v(13.15, -23.7) * mm, "radius": 0.55 * mm});
            skCircle(sketch, "E581", {"center": v(10.6, -23.7) * mm, "radius": 0.55 * mm});
            skCircle(sketch, "E582", {"center": v(8.07, -23.7) * mm, "radius": 0.55 * mm});
            skCircle(sketch, "E583", {"center": v(5.53, -23.7) * mm, "radius": 0.55 * mm});
            skCircle(sketch, "E584", {"center": v(2.99, -23.7) * mm, "radius": 0.55 * mm});
            skCircle(sketch, "E585", {"center": v(0.45, -23.7) * mm, "radius": 0.55 * mm});
            skCircle(sketch, "E586", {"center": v(-2.1, -23.7) * mm, "radius": 0.55 * mm});
            skCircle(sketch, "E587", {"center": v(-4.63, -23.7) * mm, "radius": 0.55 * mm});
            skCircle(sketch, "E588", {"center": v(-7.17, -23.7) * mm, "radius": 0.55 * mm});
            skCircle(sketch, "E589", {"center": v(-9.71, -23.7) * mm, "radius": 0.55 * mm});
            skCircle(sketch, "E590", {"center": v(-12.25, -23.7) * mm, "radius": 0.55 * mm});
            skCircle(sketch, "E591", {"center": v(-15.65, 0.34) * mm, "radius": 0.32 * mm});
            skCircle(sketch, "E592", {"center": v(-14.38, 0.34) * mm, "radius": 0.32 * mm});
            skCircle(sketch, "E593", {"center": v(-14.38, -0.93) * mm, "radius": 0.32 * mm});
            skCircle(sketch, "E594", {"center": v(-14.38, -2.2) * mm, "radius": 0.32 * mm});
            skCircle(sketch, "E595", {"center": v(-15.65, -0.93) * mm, "radius": 0.32 * mm});
            skCircle(sketch, "E596", {"center": v(-15.65, -2.2) * mm, "radius": 0.32 * mm});
            skCircle(sketch, "E597", {"center": v(36.6, 22.4) * mm, "radius": 0.55 * mm});
            skCircle(sketch, "E598", {"center": v(36.6, 19.86) * mm, "radius": 0.55 * mm});
            skCircle(sketch, "E599", {"center": v(36.6, 17.32) * mm, "radius": 0.55 * mm});
            skCircle(sketch, "E600", {"center": v(36.6, 14.78) * mm, "radius": 0.55 * mm});
            skCircle(sketch, "E601", {"center": v(36.6, 12.24) * mm, "radius": 0.55 * mm});
            skCircle(sketch, "E602", {"center": v(36.6, 9.7) * mm, "radius": 0.55 * mm});
            skCircle(sketch, "E603", {"center": v(36.53, -10) * mm, "radius": 0.55 * mm});
            skCircle(sketch, "E604", {"center": v(36.53, -12.53) * mm, "radius": 0.55 * mm});
            skCircle(sketch, "E605", {"center": v(14.22, 3.82) * mm, "radius": 0.55 * mm});
            skCircle(sketch, "E606", {"center": v(16.76, 3.82) * mm, "radius": 0.55 * mm});
            skCircle(sketch, "E607", {"center": v(13.79, 23.69) * mm, "radius": 0.55 * mm});
            skCircle(sketch, "E608", {"center": v(16.33, 23.69) * mm, "radius": 0.55 * mm});
            skCircle(sketch, "E609", {"center": v(-25.5, -12.84) * mm, "radius": 2.54 * mm});
            skCircle(sketch, "E610", {"center": v(25.48, -12.74) * mm, "radius": 2.54 * mm});
            skCircle(sketch, "E611", {"center": v(25.5, -12.74) * mm, "radius": 0.5 * mm});
            skLineSegment(sketch, "E612", {"start": v(-38.1, -25.4) * mm, "end": v(38.1, -25.4) * mm});
            skLineSegment(sketch, "E613", {"start": v(38.1, -25.4) * mm, "end": v(38.1, 25.4) * mm});
            skLineSegment(sketch, "E614", {"start": v(38.1, 25.4) * mm, "end": v(-38.1, 25.4) * mm});
            skLineSegment(sketch, "E615", {"start": v(-38.1, 25.4) * mm, "end": v(-38.1, -25.4) * mm});
            skLineSegment(sketch, "E616", {"start": v(-12.65, -6.03) * mm, "end": v(-12.67, -6.14) * mm});
            skLineSegment(sketch, "E617", {"start": v(-12.67, -6.14) * mm, "end": v(-12.72, -6.25) * mm});
            skLineSegment(sketch, "E618", {"start": v(-12.72, -6.25) * mm, "end": v(-12.79, -6.33) * mm});
            skLineSegment(sketch, "E619", {"start": v(-12.79, -6.33) * mm, "end": v(-12.88, -6.4) * mm});
            skLineSegment(sketch, "E620", {"start": v(-12.88, -6.4) * mm, "end": v(-12.95, -6.44) * mm});
            skLineSegment(sketch, "E621", {"start": v(-12.95, -6.44) * mm, "end": v(-12.95, -10.04) * mm});
            skLineSegment(sketch, "E622", {"start": v(-12.95, -10.04) * mm, "end": v(-0.09, -22.9) * mm});
            skLineSegment(sketch, "E623", {"start": v(-0.09, -22.9) * mm, "end": v(0.09, -22.81) * mm});
            skLineSegment(sketch, "E624", {"start": v(0.09, -22.81) * mm, "end": v(0.23, -22.76) * mm});
            skLineSegment(sketch, "E625", {"start": v(0.23, -22.76) * mm, "end": v(0.38, -22.74) * mm});
            skLineSegment(sketch, "E626", {"start": v(0.38, -22.74) * mm, "end": v(0.53, -22.74) * mm});
            skLineSegment(sketch, "E627", {"start": v(0.53, -22.74) * mm, "end": v(0.67, -22.76) * mm});
            skLineSegment(sketch, "E628", {"start": v(0.67, -22.76) * mm, "end": v(0.82, -22.81) * mm});
            skLineSegment(sketch, "E629", {"start": v(0.82, -22.81) * mm, "end": v(0.95, -22.88) * mm});
            skLineSegment(sketch, "E630", {"start": v(0.95, -22.88) * mm, "end": v(1.07, -22.97) * mm});
            skLineSegment(sketch, "E631", {"start": v(1.07, -22.97) * mm, "end": v(1.17, -23.07) * mm});
            skLineSegment(sketch, "E632", {"start": v(1.17, -23.07) * mm, "end": v(1.26, -23.2) * mm});
            skLineSegment(sketch, "E633", {"start": v(1.26, -23.2) * mm, "end": v(1.33, -23.32) * mm});
            skLineSegment(sketch, "E634", {"start": v(1.33, -23.32) * mm, "end": v(1.37, -23.47) * mm});
            skLineSegment(sketch, "E635", {"start": v(1.37, -23.47) * mm, "end": v(1.4, -23.61) * mm});
            skLineSegment(sketch, "E636", {"start": v(1.4, -23.61) * mm, "end": v(1.4, -23.76) * mm});
            skLineSegment(sketch, "E637", {"start": v(1.4, -23.76) * mm, "end": v(1.37, -23.91) * mm});
            skLineSegment(sketch, "E638", {"start": v(1.37, -23.91) * mm, "end": v(1.33, -24.05) * mm});
            skLineSegment(sketch, "E639", {"start": v(1.33, -24.05) * mm, "end": v(1.26, -24.19) * mm});
            skLineSegment(sketch, "E640", {"start": v(1.26, -24.19) * mm, "end": v(1.17, -24.3) * mm});
            skLineSegment(sketch, "E641", {"start": v(1.17, -24.3) * mm, "end": v(1.07, -24.41) * mm});
            skLineSegment(sketch, "E642", {"start": v(1.07, -24.41) * mm, "end": v(0.95, -24.5) * mm});
            skLineSegment(sketch, "E643", {"start": v(0.95, -24.5) * mm, "end": v(0.82, -24.57) * mm});
            skLineSegment(sketch, "E644", {"start": v(0.82, -24.57) * mm, "end": v(0.67, -24.62) * mm});
            skLineSegment(sketch, "E645", {"start": v(0.67, -24.62) * mm, "end": v(0.53, -24.64) * mm});
            skLineSegment(sketch, "E646", {"start": v(0.53, -24.64) * mm, "end": v(0.38, -24.64) * mm});
            skLineSegment(sketch, "E647", {"start": v(0.38, -24.64) * mm, "end": v(0.23, -24.62) * mm});
            skLineSegment(sketch, "E648", {"start": v(0.23, -24.62) * mm, "end": v(0.09, -24.57) * mm});
            skLineSegment(sketch, "E649", {"start": v(0.09, -24.57) * mm, "end": v(-0.05, -24.5) * mm});
            skLineSegment(sketch, "E650", {"start": v(-0.05, -24.5) * mm, "end": v(-0.17, -24.41) * mm});
            skLineSegment(sketch, "E651", {"start": v(-0.17, -24.41) * mm, "end": v(-0.27, -24.3) * mm});
            skLineSegment(sketch, "E652", {"start": v(-0.27, -24.3) * mm, "end": v(-0.36, -24.19) * mm});
            skLineSegment(sketch, "E653", {"start": v(-0.36, -24.19) * mm, "end": v(-0.43, -24.05) * mm});
            skLineSegment(sketch, "E654", {"start": v(-0.43, -24.05) * mm, "end": v(-0.47, -23.91) * mm});
            skLineSegment(sketch, "E655", {"start": v(-0.47, -23.91) * mm, "end": v(-0.5, -23.76) * mm});
            skLineSegment(sketch, "E656", {"start": v(-0.5, -23.76) * mm, "end": v(-0.5, -23.61) * mm});
            skLineSegment(sketch, "E657", {"start": v(-0.5, -23.61) * mm, "end": v(-0.47, -23.47) * mm});
            skLineSegment(sketch, "E658", {"start": v(-0.47, -23.47) * mm, "end": v(-0.43, -23.32) * mm});
            skLineSegment(sketch, "E659", {"start": v(-0.43, -23.32) * mm, "end": v(-0.36, -23.2) * mm});
            skLineSegment(sketch, "E660", {"start": v(-0.36, -23.2) * mm, "end": v(-0.34, -23.15) * mm});
            skLineSegment(sketch, "E661", {"start": v(-0.34, -23.15) * mm, "end": v(-13.27, -10.21) * mm});
            skLineSegment(sketch, "E662", {"start": v(-13.27, -10.21) * mm, "end": v(-13.3, -10.15) * mm});
            skLineSegment(sketch, "E663", {"start": v(-13.3, -10.15) * mm, "end": v(-13.3, -10.1) * mm});
            skLineSegment(sketch, "E664", {"start": v(-13.3, -10.1) * mm, "end": v(-13.3, -6.44) * mm});
            skLineSegment(sketch, "E665", {"start": v(-13.3, -6.44) * mm, "end": v(-13.38, -6.4) * mm});
            skLineSegment(sketch, "E666", {"start": v(-13.38, -6.4) * mm, "end": v(-13.47, -6.33) * mm});
            skLineSegment(sketch, "E667", {"start": v(-13.47, -6.33) * mm, "end": v(-13.54, -6.25) * mm});
            skLineSegment(sketch, "E668", {"start": v(-13.54, -6.25) * mm, "end": v(-13.59, -6.14) * mm});
            skLineSegment(sketch, "E669", {"start": v(-13.59, -6.14) * mm, "end": v(-13.61, -6.03) * mm});
            skLineSegment(sketch, "E670", {"start": v(-13.61, -6.03) * mm, "end": v(-13.6, -5.92) * mm});
            skLineSegment(sketch, "E671", {"start": v(-13.6, -5.92) * mm, "end": v(-13.58, -5.8) * mm});
            skLineSegment(sketch, "E672", {"start": v(-13.58, -5.8) * mm, "end": v(-13.52, -5.7) * mm});
            skLineSegment(sketch, "E673", {"start": v(-13.52, -5.7) * mm, "end": v(-13.44, -5.63) * mm});
            skLineSegment(sketch, "E674", {"start": v(-13.44, -5.63) * mm, "end": v(-13.35, -5.56) * mm});
            skLineSegment(sketch, "E675", {"start": v(-13.35, -5.56) * mm, "end": v(-13.24, -5.52) * mm});
            skLineSegment(sketch, "E676", {"start": v(-13.24, -5.52) * mm, "end": v(-13.13, -5.51) * mm});
            skLineSegment(sketch, "E677", {"start": v(-13.13, -5.51) * mm, "end": v(-13.02, -5.52) * mm});
            skLineSegment(sketch, "E678", {"start": v(-13.02, -5.52) * mm, "end": v(-12.91, -5.56) * mm});
            skLineSegment(sketch, "E679", {"start": v(-12.91, -5.56) * mm, "end": v(-12.82, -5.63) * mm});
            skLineSegment(sketch, "E680", {"start": v(-12.82, -5.63) * mm, "end": v(-12.74, -5.7) * mm});
            skLineSegment(sketch, "E681", {"start": v(-12.74, -5.7) * mm, "end": v(-12.68, -5.8) * mm});
            skLineSegment(sketch, "E682", {"start": v(-12.68, -5.8) * mm, "end": v(-12.65, -5.92) * mm});
            skLineSegment(sketch, "E683", {"start": v(-12.65, -5.92) * mm, "end": v(-12.65, -6.03) * mm});
            skLineSegment(sketch, "E684", {"start": v(-15.19, -6.03) * mm, "end": v(-15.21, -6.14) * mm});
            skLineSegment(sketch, "E685", {"start": v(-15.21, -6.14) * mm, "end": v(-15.26, -6.25) * mm});
            skLineSegment(sketch, "E686", {"start": v(-15.26, -6.25) * mm, "end": v(-15.33, -6.33) * mm});
            skLineSegment(sketch, "E687", {"start": v(-15.33, -6.33) * mm, "end": v(-15.42, -6.4) * mm});
            skLineSegment(sketch, "E688", {"start": v(-15.42, -6.4) * mm, "end": v(-15.5, -6.44) * mm});
            skLineSegment(sketch, "E689", {"start": v(-15.5, -6.44) * mm, "end": v(-15.5, -10.04) * mm});
            skLineSegment(sketch, "E690", {"start": v(-15.5, -10.04) * mm, "end": v(-2.63, -22.9) * mm});
            skLineSegment(sketch, "E691", {"start": v(-2.63, -22.9) * mm, "end": v(-2.45, -22.81) * mm});
            skLineSegment(sketch, "E692", {"start": v(-2.45, -22.81) * mm, "end": v(-2.31, -22.76) * mm});
            skLineSegment(sketch, "E693", {"start": v(-2.31, -22.76) * mm, "end": v(-2.16, -22.74) * mm});
            skLineSegment(sketch, "E694", {"start": v(-2.16, -22.74) * mm, "end": v(-2.01, -22.74) * mm});
            skLineSegment(sketch, "E695", {"start": v(-2.01, -22.74) * mm, "end": v(-1.87, -22.76) * mm});
            skLineSegment(sketch, "E696", {"start": v(-1.87, -22.76) * mm, "end": v(-1.72, -22.81) * mm});
            skLineSegment(sketch, "E697", {"start": v(-1.72, -22.81) * mm, "end": v(-1.6, -22.88) * mm});
            skLineSegment(sketch, "E698", {"start": v(-1.6, -22.88) * mm, "end": v(-1.47, -22.97) * mm});
            skLineSegment(sketch, "E699", {"start": v(-1.47, -22.97) * mm, "end": v(-1.37, -23.07) * mm});
            skLineSegment(sketch, "E700", {"start": v(-1.37, -23.07) * mm, "end": v(-1.28, -23.2) * mm});
            skLineSegment(sketch, "E701", {"start": v(-1.28, -23.2) * mm, "end": v(-1.21, -23.32) * mm});
            skLineSegment(sketch, "E702", {"start": v(-1.21, -23.32) * mm, "end": v(-1.17, -23.47) * mm});
            skLineSegment(sketch, "E703", {"start": v(-1.17, -23.47) * mm, "end": v(-1.14, -23.61) * mm});
            skLineSegment(sketch, "E704", {"start": v(-1.14, -23.61) * mm, "end": v(-1.14, -23.76) * mm});
            skLineSegment(sketch, "E705", {"start": v(-1.14, -23.76) * mm, "end": v(-1.17, -23.91) * mm});
            skLineSegment(sketch, "E706", {"start": v(-1.17, -23.91) * mm, "end": v(-1.21, -24.05) * mm});
            skLineSegment(sketch, "E707", {"start": v(-1.21, -24.05) * mm, "end": v(-1.28, -24.19) * mm});
            skLineSegment(sketch, "E708", {"start": v(-1.28, -24.19) * mm, "end": v(-1.37, -24.3) * mm});
            skLineSegment(sketch, "E709", {"start": v(-1.37, -24.3) * mm, "end": v(-1.47, -24.41) * mm});
            skLineSegment(sketch, "E710", {"start": v(-1.47, -24.41) * mm, "end": v(-1.6, -24.5) * mm});
            skLineSegment(sketch, "E711", {"start": v(-1.6, -24.5) * mm, "end": v(-1.72, -24.57) * mm});
            skLineSegment(sketch, "E712", {"start": v(-1.72, -24.57) * mm, "end": v(-1.87, -24.62) * mm});
            skLineSegment(sketch, "E713", {"start": v(-1.87, -24.62) * mm, "end": v(-2.01, -24.64) * mm});
            skLineSegment(sketch, "E714", {"start": v(-2.01, -24.64) * mm, "end": v(-2.16, -24.64) * mm});
            skLineSegment(sketch, "E715", {"start": v(-2.16, -24.64) * mm, "end": v(-2.31, -24.62) * mm});
            skLineSegment(sketch, "E716", {"start": v(-2.31, -24.62) * mm, "end": v(-2.45, -24.57) * mm});
            skLineSegment(sketch, "E717", {"start": v(-2.45, -24.57) * mm, "end": v(-2.59, -24.5) * mm});
            skLineSegment(sketch, "E718", {"start": v(-2.59, -24.5) * mm, "end": v(-2.7, -24.41) * mm});
            skLineSegment(sketch, "E719", {"start": v(-2.7, -24.41) * mm, "end": v(-2.81, -24.3) * mm});
            skLineSegment(sketch, "E720", {"start": v(-2.81, -24.3) * mm, "end": v(-2.9, -24.19) * mm});
            skLineSegment(sketch, "E721", {"start": v(-2.9, -24.19) * mm, "end": v(-2.97, -24.05) * mm});
            skLineSegment(sketch, "E722", {"start": v(-2.97, -24.05) * mm, "end": v(-3.01, -23.91) * mm});
            skLineSegment(sketch, "E723", {"start": v(-3.01, -23.91) * mm, "end": v(-3.04, -23.76) * mm});
            skLineSegment(sketch, "E724", {"start": v(-3.04, -23.76) * mm, "end": v(-3.04, -23.61) * mm});
            skLineSegment(sketch, "E725", {"start": v(-3.04, -23.61) * mm, "end": v(-3.01, -23.47) * mm});
            skLineSegment(sketch, "E726", {"start": v(-3.01, -23.47) * mm, "end": v(-2.97, -23.32) * mm});
            skLineSegment(sketch, "E727", {"start": v(-2.97, -23.32) * mm, "end": v(-2.9, -23.2) * mm});
            skLineSegment(sketch, "E728", {"start": v(-2.9, -23.2) * mm, "end": v(-2.88, -23.15) * mm});
            skLineSegment(sketch, "E729", {"start": v(-2.88, -23.15) * mm, "end": v(-15.81, -10.21) * mm});
            skLineSegment(sketch, "E730", {"start": v(-15.81, -10.21) * mm, "end": v(-15.84, -10.15) * mm});
            skLineSegment(sketch, "E731", {"start": v(-15.84, -10.15) * mm, "end": v(-15.85, -10.1) * mm});
            skLineSegment(sketch, "E732", {"start": v(-15.85, -10.1) * mm, "end": v(-15.85, -6.44) * mm});
            skLineSegment(sketch, "E733", {"start": v(-15.85, -6.44) * mm, "end": v(-15.92, -6.4) * mm});
            skLineSegment(sketch, "E734", {"start": v(-15.92, -6.4) * mm, "end": v(-16.01, -6.33) * mm});
            skLineSegment(sketch, "E735", {"start": v(-16.01, -6.33) * mm, "end": v(-16.08, -6.25) * mm});
            skLineSegment(sketch, "E736", {"start": v(-16.08, -6.25) * mm, "end": v(-16.13, -6.14) * mm});
            skLineSegment(sketch, "E737", {"start": v(-16.13, -6.14) * mm, "end": v(-16.15, -6.03) * mm});
            skLineSegment(sketch, "E738", {"start": v(-16.15, -6.03) * mm, "end": v(-16.15, -5.92) * mm});
            skLineSegment(sketch, "E739", {"start": v(-16.15, -5.92) * mm, "end": v(-16.12, -5.8) * mm});
            skLineSegment(sketch, "E740", {"start": v(-16.12, -5.8) * mm, "end": v(-16.06, -5.7) * mm});
            skLineSegment(sketch, "E741", {"start": v(-16.06, -5.7) * mm, "end": v(-15.98, -5.63) * mm});
            skLineSegment(sketch, "E742", {"start": v(-15.98, -5.63) * mm, "end": v(-15.9, -5.56) * mm});
            skLineSegment(sketch, "E743", {"start": v(-15.9, -5.56) * mm, "end": v(-15.78, -5.52) * mm});
            skLineSegment(sketch, "E744", {"start": v(-15.78, -5.52) * mm, "end": v(-15.67, -5.51) * mm});
            skLineSegment(sketch, "E745", {"start": v(-15.67, -5.51) * mm, "end": v(-15.56, -5.52) * mm});
            skLineSegment(sketch, "E746", {"start": v(-15.56, -5.52) * mm, "end": v(-15.45, -5.56) * mm});
            skLineSegment(sketch, "E747", {"start": v(-15.45, -5.56) * mm, "end": v(-15.36, -5.63) * mm});
            skLineSegment(sketch, "E748", {"start": v(-15.36, -5.63) * mm, "end": v(-15.28, -5.7) * mm});
            skLineSegment(sketch, "E749", {"start": v(-15.28, -5.7) * mm, "end": v(-15.22, -5.8) * mm});
            skLineSegment(sketch, "E750", {"start": v(-15.22, -5.8) * mm, "end": v(-15.2, -5.92) * mm});
            skLineSegment(sketch, "E751", {"start": v(-15.2, -5.92) * mm, "end": v(-15.19, -6.03) * mm});
            skLineSegment(sketch, "E752", {"start": v(-17.73, -6.03) * mm, "end": v(-17.75, -6.14) * mm});
            skLineSegment(sketch, "E753", {"start": v(-17.75, -6.14) * mm, "end": v(-17.8, -6.25) * mm});
            skLineSegment(sketch, "E754", {"start": v(-17.8, -6.25) * mm, "end": v(-17.87, -6.33) * mm});
            skLineSegment(sketch, "E755", {"start": v(-17.87, -6.33) * mm, "end": v(-17.96, -6.4) * mm});
            skLineSegment(sketch, "E756", {"start": v(-17.96, -6.4) * mm, "end": v(-18.06, -6.45) * mm});
            skLineSegment(sketch, "E757", {"start": v(-18.06, -6.45) * mm, "end": v(-18.17, -6.47) * mm});
            skLineSegment(sketch, "E758", {"start": v(-18.17, -6.47) * mm, "end": v(-18.29, -6.47) * mm});
            skLineSegment(sketch, "E759", {"start": v(-18.29, -6.47) * mm, "end": v(-18.4, -6.44) * mm});
            skLineSegment(sketch, "E760", {"start": v(-18.4, -6.44) * mm, "end": v(-18.5, -6.38) * mm});
            skLineSegment(sketch, "E761", {"start": v(-18.5, -6.38) * mm, "end": v(-18.58, -6.3) * mm});
            skLineSegment(sketch, "E762", {"start": v(-18.58, -6.3) * mm, "end": v(-18.64, -6.21) * mm});
            skLineSegment(sketch, "E763", {"start": v(-18.64, -6.21) * mm, "end": v(-18.68, -6.1) * mm});
            skLineSegment(sketch, "E764", {"start": v(-18.68, -6.1) * mm, "end": v(-18.7, -6) * mm});
            skLineSegment(sketch, "E765", {"start": v(-18.7, -6) * mm, "end": v(-18.68, -5.88) * mm});
            skLineSegment(sketch, "E766", {"start": v(-18.68, -5.88) * mm, "end": v(-18.64, -5.77) * mm});
            skLineSegment(sketch, "E767", {"start": v(-18.64, -5.77) * mm, "end": v(-18.58, -5.68) * mm});
            skLineSegment(sketch, "E768", {"start": v(-18.58, -5.68) * mm, "end": v(-18.5, -5.6) * mm});
            skLineSegment(sketch, "E769", {"start": v(-18.5, -5.6) * mm, "end": v(-18.4, -5.55) * mm});
            skLineSegment(sketch, "E770", {"start": v(-18.4, -5.55) * mm, "end": v(-18.29, -5.52) * mm});
            skLineSegment(sketch, "E771", {"start": v(-18.29, -5.52) * mm, "end": v(-18.17, -5.51) * mm});
            skLineSegment(sketch, "E772", {"start": v(-18.17, -5.51) * mm, "end": v(-18.06, -5.53) * mm});
            skLineSegment(sketch, "E773", {"start": v(-18.06, -5.53) * mm, "end": v(-17.96, -5.58) * mm});
            skLineSegment(sketch, "E774", {"start": v(-17.96, -5.58) * mm, "end": v(-17.87, -5.65) * mm});
            skLineSegment(sketch, "E775", {"start": v(-17.87, -5.65) * mm, "end": v(-17.8, -5.74) * mm});
            skLineSegment(sketch, "E776", {"start": v(-17.8, -5.74) * mm, "end": v(-17.75, -5.84) * mm});
            skLineSegment(sketch, "E777", {"start": v(-17.75, -5.84) * mm, "end": v(-17.73, -5.96) * mm});
            skLineSegment(sketch, "E778", {"start": v(-17.73, -5.96) * mm, "end": v(-17.73, -6.03) * mm});
            skLineSegment(sketch, "E779", {"start": v(19, -0.23) * mm, "end": v(18.98, -0.34) * mm});
            skLineSegment(sketch, "E780", {"start": v(18.98, -0.34) * mm, "end": v(18.93, -0.44) * mm});
            skLineSegment(sketch, "E781", {"start": v(18.93, -0.44) * mm, "end": v(18.86, -0.53) * mm});
            skLineSegment(sketch, "E782", {"start": v(18.86, -0.53) * mm, "end": v(18.77, -0.6) * mm});
            skLineSegment(sketch, "E783", {"start": v(18.77, -0.6) * mm, "end": v(18.67, -0.65) * mm});
            skLineSegment(sketch, "E784", {"start": v(18.67, -0.65) * mm, "end": v(18.56, -0.68) * mm});
            skLineSegment(sketch, "E785", {"start": v(18.56, -0.68) * mm, "end": v(18.45, -0.67) * mm});
            skLineSegment(sketch, "E786", {"start": v(18.45, -0.67) * mm, "end": v(18.34, -0.64) * mm});
            skLineSegment(sketch, "E787", {"start": v(18.34, -0.64) * mm, "end": v(18.24, -0.58) * mm});
            skLineSegment(sketch, "E788", {"start": v(18.24, -0.58) * mm, "end": v(18.15, -0.5) * mm});
            skLineSegment(sketch, "E789", {"start": v(18.15, -0.5) * mm, "end": v(18.09, -0.41) * mm});
            skLineSegment(sketch, "E790", {"start": v(18.09, -0.41) * mm, "end": v(18.07, -0.37) * mm});
            skLineSegment(sketch, "E791", {"start": v(18.07, -0.37) * mm, "end": v(12.07, -0.37) * mm});
            skLineSegment(sketch, "E792", {"start": v(12.07, -0.37) * mm, "end": v(11.36, -1.08) * mm});
            skLineSegment(sketch, "E793", {"start": v(11.36, -1.08) * mm, "end": v(6.72, -5.73) * mm});
            skLineSegment(sketch, "E794", {"start": v(6.72, -5.73) * mm, "end": v(6.72, -6.9) * mm});
            skLineSegment(sketch, "E795", {"start": v(6.72, -6.9) * mm, "end": v(7.9, -8.07) * mm});
            skLineSegment(sketch, "E796", {"start": v(7.9, -8.07) * mm, "end": v(10.36, -8.08) * mm});
            skLineSegment(sketch, "E797", {"start": v(10.36, -8.08) * mm, "end": v(10.42, -8.1) * mm});
            skLineSegment(sketch, "E798", {"start": v(10.42, -8.1) * mm, "end": v(10.47, -8.13) * mm});
            skLineSegment(sketch, "E799", {"start": v(10.47, -8.13) * mm, "end": v(23.15, -20.8) * mm});
            skLineSegment(sketch, "E800", {"start": v(23.15, -20.8) * mm, "end": v(23.21, -20.82) * mm});
            skLineSegment(sketch, "E801", {"start": v(23.21, -20.82) * mm, "end": v(23.27, -20.86) * mm});
            skLineSegment(sketch, "E802", {"start": v(23.27, -20.86) * mm, "end": v(25.31, -22.9) * mm});
            skLineSegment(sketch, "E803", {"start": v(25.31, -22.9) * mm, "end": v(25.49, -22.81) * mm});
            skLineSegment(sketch, "E804", {"start": v(25.49, -22.81) * mm, "end": v(25.63, -22.76) * mm});
            skLineSegment(sketch, "E805", {"start": v(25.63, -22.76) * mm, "end": v(25.78, -22.74) * mm});
            skLineSegment(sketch, "E806", {"start": v(25.78, -22.74) * mm, "end": v(25.93, -22.74) * mm});
            skLineSegment(sketch, "E807", {"start": v(25.93, -22.74) * mm, "end": v(26.07, -22.76) * mm});
            skLineSegment(sketch, "E808", {"start": v(26.07, -22.76) * mm, "end": v(26.22, -22.81) * mm});
            skLineSegment(sketch, "E809", {"start": v(26.22, -22.81) * mm, "end": v(26.35, -22.88) * mm});
            skLineSegment(sketch, "E810", {"start": v(26.35, -22.88) * mm, "end": v(26.47, -22.97) * mm});
            skLineSegment(sketch, "E811", {"start": v(26.47, -22.97) * mm, "end": v(26.57, -23.07) * mm});
            skLineSegment(sketch, "E812", {"start": v(26.57, -23.07) * mm, "end": v(26.66, -23.2) * mm});
            skLineSegment(sketch, "E813", {"start": v(26.66, -23.2) * mm, "end": v(26.73, -23.32) * mm});
            skLineSegment(sketch, "E814", {"start": v(26.73, -23.32) * mm, "end": v(26.77, -23.47) * mm});
            skLineSegment(sketch, "E815", {"start": v(26.77, -23.47) * mm, "end": v(26.8, -23.61) * mm});
            skLineSegment(sketch, "E816", {"start": v(26.8, -23.61) * mm, "end": v(26.8, -23.76) * mm});
            skLineSegment(sketch, "E817", {"start": v(26.8, -23.76) * mm, "end": v(26.77, -23.91) * mm});
            skLineSegment(sketch, "E818", {"start": v(26.77, -23.91) * mm, "end": v(26.73, -24.05) * mm});
            skLineSegment(sketch, "E819", {"start": v(26.73, -24.05) * mm, "end": v(26.66, -24.19) * mm});
            skLineSegment(sketch, "E820", {"start": v(26.66, -24.19) * mm, "end": v(26.57, -24.3) * mm});
            skLineSegment(sketch, "E821", {"start": v(26.57, -24.3) * mm, "end": v(26.47, -24.41) * mm});
            skLineSegment(sketch, "E822", {"start": v(26.47, -24.41) * mm, "end": v(26.35, -24.5) * mm});
            skLineSegment(sketch, "E823", {"start": v(26.35, -24.5) * mm, "end": v(26.22, -24.57) * mm});
            skLineSegment(sketch, "E824", {"start": v(26.22, -24.57) * mm, "end": v(26.07, -24.62) * mm});
            skLineSegment(sketch, "E825", {"start": v(26.07, -24.62) * mm, "end": v(25.93, -24.64) * mm});
            skLineSegment(sketch, "E826", {"start": v(25.93, -24.64) * mm, "end": v(25.78, -24.64) * mm});
            skLineSegment(sketch, "E827", {"start": v(25.78, -24.64) * mm, "end": v(25.63, -24.62) * mm});
            skLineSegment(sketch, "E828", {"start": v(25.63, -24.62) * mm, "end": v(25.49, -24.57) * mm});
            skLineSegment(sketch, "E829", {"start": v(25.49, -24.57) * mm, "end": v(25.35, -24.5) * mm});
            skLineSegment(sketch, "E830", {"start": v(25.35, -24.5) * mm, "end": v(25.23, -24.41) * mm});
            skLineSegment(sketch, "E831", {"start": v(25.23, -24.41) * mm, "end": v(25.13, -24.3) * mm});
            skLineSegment(sketch, "E832", {"start": v(25.13, -24.3) * mm, "end": v(25.04, -24.19) * mm});
            skLineSegment(sketch, "E833", {"start": v(25.04, -24.19) * mm, "end": v(24.97, -24.05) * mm});
            skLineSegment(sketch, "E834", {"start": v(24.97, -24.05) * mm, "end": v(24.93, -23.91) * mm});
            skLineSegment(sketch, "E835", {"start": v(24.93, -23.91) * mm, "end": v(24.9, -23.76) * mm});
            skLineSegment(sketch, "E836", {"start": v(24.9, -23.76) * mm, "end": v(24.9, -23.61) * mm});
            skLineSegment(sketch, "E837", {"start": v(24.9, -23.61) * mm, "end": v(24.93, -23.47) * mm});
            skLineSegment(sketch, "E838", {"start": v(24.93, -23.47) * mm, "end": v(24.97, -23.32) * mm});
            skLineSegment(sketch, "E839", {"start": v(24.97, -23.32) * mm, "end": v(25.04, -23.2) * mm});
            skLineSegment(sketch, "E840", {"start": v(25.04, -23.2) * mm, "end": v(25.06, -23.15) * mm});
            skLineSegment(sketch, "E841", {"start": v(25.06, -23.15) * mm, "end": v(23.07, -21.16) * mm});
            skLineSegment(sketch, "E842", {"start": v(23.07, -21.16) * mm, "end": v(23, -21.15) * mm});
            skLineSegment(sketch, "E843", {"start": v(23, -21.15) * mm, "end": v(22.95, -21.1) * mm});
            skLineSegment(sketch, "E844", {"start": v(22.95, -21.1) * mm, "end": v(10.27, -8.43) * mm});
            skLineSegment(sketch, "E845", {"start": v(10.27, -8.43) * mm, "end": v(7.8, -8.43) * mm});
            skLineSegment(sketch, "E846", {"start": v(7.8, -8.43) * mm, "end": v(7.74, -8.4) * mm});
            skLineSegment(sketch, "E847", {"start": v(7.74, -8.4) * mm, "end": v(7.71, -8.38) * mm});
            skLineSegment(sketch, "E848", {"start": v(7.71, -8.38) * mm, "end": v(6.4, -7.06) * mm});
            skLineSegment(sketch, "E849", {"start": v(6.4, -7.06) * mm, "end": v(6.37, -7) * mm});
            skLineSegment(sketch, "E850", {"start": v(6.37, -7) * mm, "end": v(6.37, -6.29) * mm});
            skLineSegment(sketch, "E851", {"start": v(6.37, -6.29) * mm, "end": v(6.37, -5.6) * mm});
            skLineSegment(sketch, "E852", {"start": v(6.37, -5.6) * mm, "end": v(6.4, -5.54) * mm});
            skLineSegment(sketch, "E853", {"start": v(6.4, -5.54) * mm, "end": v(6.9, -5.04) * mm});
            skLineSegment(sketch, "E854", {"start": v(6.9, -5.04) * mm, "end": v(11.91, -0.04) * mm});
            skLineSegment(sketch, "E855", {"start": v(11.91, -0.04) * mm, "end": v(11.98, -0.02) * mm});
            skLineSegment(sketch, "E856", {"start": v(11.98, -0.02) * mm, "end": v(12.68, -0.02) * mm});
            skLineSegment(sketch, "E857", {"start": v(12.68, -0.02) * mm, "end": v(18.07, -0.02) * mm});
            skLineSegment(sketch, "E858", {"start": v(18.07, -0.02) * mm, "end": v(18.13, 0.1) * mm});
            skLineSegment(sketch, "E859", {"start": v(18.13, 0.1) * mm, "end": v(18.2, 0.17) * mm});
            skLineSegment(sketch, "E860", {"start": v(18.2, 0.17) * mm, "end": v(18.3, 0.24) * mm});
            skLineSegment(sketch, "E861", {"start": v(18.3, 0.24) * mm, "end": v(18.4, 0.28) * mm});
            skLineSegment(sketch, "E862", {"start": v(18.4, 0.28) * mm, "end": v(18.52, 0.29) * mm});
            skLineSegment(sketch, "E863", {"start": v(18.52, 0.29) * mm, "end": v(18.63, 0.28) * mm});
            skLineSegment(sketch, "E864", {"start": v(18.63, 0.28) * mm, "end": v(18.74, 0.24) * mm});
            skLineSegment(sketch, "E865", {"start": v(18.74, 0.24) * mm, "end": v(18.83, 0.17) * mm});
            skLineSegment(sketch, "E866", {"start": v(18.83, 0.17) * mm, "end": v(18.91, 0.1) * mm});
            skLineSegment(sketch, "E867", {"start": v(18.91, 0.1) * mm, "end": v(18.97, 0) * mm});
            skLineSegment(sketch, "E868", {"start": v(18.97, 0) * mm, "end": v(19, -0.12) * mm});
            skLineSegment(sketch, "E869", {"start": v(19, -0.12) * mm, "end": v(19, -0.23) * mm});
            skLineSegment(sketch, "E870", {"start": v(5.5, -2.54) * mm, "end": v(5.48, -2.65) * mm});
            skLineSegment(sketch, "E871", {"start": v(5.48, -2.65) * mm, "end": v(5.43, -2.75) * mm});
            skLineSegment(sketch, "E872", {"start": v(5.43, -2.75) * mm, "end": v(5.36, -2.84) * mm});
            skLineSegment(sketch, "E873", {"start": v(5.36, -2.84) * mm, "end": v(5.27, -2.91) * mm});
            skLineSegment(sketch, "E874", {"start": v(5.27, -2.91) * mm, "end": v(5.17, -2.96) * mm});
            skLineSegment(sketch, "E875", {"start": v(5.17, -2.96) * mm, "end": v(5.05, -2.98) * mm});
            skLineSegment(sketch, "E876", {"start": v(5.05, -2.98) * mm, "end": v(1.4, -6.63) * mm});
            skLineSegment(sketch, "E877", {"start": v(1.4, -6.63) * mm, "end": v(7.08, -12.3) * mm});
            skLineSegment(sketch, "E878", {"start": v(7.08, -12.3) * mm, "end": v(7.13, -12.34) * mm});
            skLineSegment(sketch, "E879", {"start": v(7.13, -12.34) * mm, "end": v(17.7, -22.9) * mm});
            skLineSegment(sketch, "E880", {"start": v(17.7, -22.9) * mm, "end": v(17.87, -22.81) * mm});
            skLineSegment(sketch, "E881", {"start": v(17.87, -22.81) * mm, "end": v(18, -22.76) * mm});
            skLineSegment(sketch, "E882", {"start": v(18, -22.76) * mm, "end": v(18.16, -22.74) * mm});
            skLineSegment(sketch, "E883", {"start": v(18.16, -22.74) * mm, "end": v(18.3, -22.74) * mm});
            skLineSegment(sketch, "E884", {"start": v(18.3, -22.74) * mm, "end": v(18.45, -22.76) * mm});
            skLineSegment(sketch, "E885", {"start": v(18.45, -22.76) * mm, "end": v(18.6, -22.81) * mm});
            skLineSegment(sketch, "E886", {"start": v(18.6, -22.81) * mm, "end": v(18.73, -22.88) * mm});
            skLineSegment(sketch, "E887", {"start": v(18.73, -22.88) * mm, "end": v(18.85, -22.97) * mm});
            skLineSegment(sketch, "E888", {"start": v(18.85, -22.97) * mm, "end": v(18.95, -23.07) * mm});
            skLineSegment(sketch, "E889", {"start": v(18.95, -23.07) * mm, "end": v(19.04, -23.2) * mm});
            skLineSegment(sketch, "E890", {"start": v(19.04, -23.2) * mm, "end": v(19.1, -23.32) * mm});
            skLineSegment(sketch, "E891", {"start": v(19.1, -23.32) * mm, "end": v(19.15, -23.47) * mm});
            skLineSegment(sketch, "E892", {"start": v(19.15, -23.47) * mm, "end": v(19.18, -23.61) * mm});
            skLineSegment(sketch, "E893", {"start": v(19.18, -23.61) * mm, "end": v(19.18, -23.76) * mm});
            skLineSegment(sketch, "E894", {"start": v(19.18, -23.76) * mm, "end": v(19.15, -23.91) * mm});
            skLineSegment(sketch, "E895", {"start": v(19.15, -23.91) * mm, "end": v(19.1, -24.05) * mm});
            skLineSegment(sketch, "E896", {"start": v(19.1, -24.05) * mm, "end": v(19.04, -24.19) * mm});
            skLineSegment(sketch, "E897", {"start": v(19.04, -24.19) * mm, "end": v(18.95, -24.3) * mm});
            skLineSegment(sketch, "E898", {"start": v(18.95, -24.3) * mm, "end": v(18.85, -24.41) * mm});
            skLineSegment(sketch, "E899", {"start": v(18.85, -24.41) * mm, "end": v(18.73, -24.5) * mm});
            skLineSegment(sketch, "E900", {"start": v(18.73, -24.5) * mm, "end": v(18.6, -24.57) * mm});
            skLineSegment(sketch, "E901", {"start": v(18.6, -24.57) * mm, "end": v(18.45, -24.62) * mm});
            skLineSegment(sketch, "E902", {"start": v(18.45, -24.62) * mm, "end": v(18.3, -24.64) * mm});
            skLineSegment(sketch, "E903", {"start": v(18.3, -24.64) * mm, "end": v(18.16, -24.64) * mm});
            skLineSegment(sketch, "E904", {"start": v(18.16, -24.64) * mm, "end": v(18, -24.62) * mm});
            skLineSegment(sketch, "E905", {"start": v(18, -24.62) * mm, "end": v(17.87, -24.57) * mm});
            skLineSegment(sketch, "E906", {"start": v(17.87, -24.57) * mm, "end": v(17.73, -24.5) * mm});
            skLineSegment(sketch, "E907", {"start": v(17.73, -24.5) * mm, "end": v(17.61, -24.41) * mm});
            skLineSegment(sketch, "E908", {"start": v(17.61, -24.41) * mm, "end": v(17.5, -24.3) * mm});
            skLineSegment(sketch, "E909", {"start": v(17.5, -24.3) * mm, "end": v(17.42, -24.19) * mm});
            skLineSegment(sketch, "E910", {"start": v(17.42, -24.19) * mm, "end": v(17.35, -24.05) * mm});
            skLineSegment(sketch, "E911", {"start": v(17.35, -24.05) * mm, "end": v(17.3, -23.91) * mm});
            skLineSegment(sketch, "E912", {"start": v(17.3, -23.91) * mm, "end": v(17.28, -23.76) * mm});
            skLineSegment(sketch, "E913", {"start": v(17.28, -23.76) * mm, "end": v(17.28, -23.61) * mm});
            skLineSegment(sketch, "E914", {"start": v(17.28, -23.61) * mm, "end": v(17.3, -23.47) * mm});
            skLineSegment(sketch, "E915", {"start": v(17.3, -23.47) * mm, "end": v(17.35, -23.32) * mm});
            skLineSegment(sketch, "E916", {"start": v(17.35, -23.32) * mm, "end": v(17.42, -23.2) * mm});
            skLineSegment(sketch, "E917", {"start": v(17.42, -23.2) * mm, "end": v(17.44, -23.15) * mm});
            skLineSegment(sketch, "E918", {"start": v(17.44, -23.15) * mm, "end": v(6.92, -12.64) * mm});
            skLineSegment(sketch, "E919", {"start": v(6.92, -12.64) * mm, "end": v(6.87, -12.6) * mm});
            skLineSegment(sketch, "E920", {"start": v(6.87, -12.6) * mm, "end": v(1, -6.74) * mm});
            skLineSegment(sketch, "E921", {"start": v(1, -6.74) * mm, "end": v(0.98, -6.68) * mm});
            skLineSegment(sketch, "E922", {"start": v(0.98, -6.68) * mm, "end": v(0.98, -6.6) * mm});
            skLineSegment(sketch, "E923", {"start": v(0.98, -6.6) * mm, "end": v(1, -6.54) * mm});
            skLineSegment(sketch, "E924", {"start": v(1, -6.54) * mm, "end": v(1.02, -6.5) * mm});
            skLineSegment(sketch, "E925", {"start": v(1.02, -6.5) * mm, "end": v(4.69, -2.85) * mm});
            skLineSegment(sketch, "E926", {"start": v(4.69, -2.85) * mm, "end": v(4.6, -2.75) * mm});
            skLineSegment(sketch, "E927", {"start": v(4.6, -2.75) * mm, "end": v(4.56, -2.65) * mm});
            skLineSegment(sketch, "E928", {"start": v(4.56, -2.65) * mm, "end": v(4.54, -2.54) * mm});
            skLineSegment(sketch, "E929", {"start": v(4.54, -2.54) * mm, "end": v(4.54, -2.43) * mm});
            skLineSegment(sketch, "E930", {"start": v(4.54, -2.43) * mm, "end": v(4.57, -2.32) * mm});
            skLineSegment(sketch, "E931", {"start": v(4.57, -2.32) * mm, "end": v(4.63, -2.22) * mm});
            skLineSegment(sketch, "E932", {"start": v(4.63, -2.22) * mm, "end": v(4.7, -2.13) * mm});
            skLineSegment(sketch, "E933", {"start": v(4.7, -2.13) * mm, "end": v(4.8, -2.07) * mm});
            skLineSegment(sketch, "E934", {"start": v(4.8, -2.07) * mm, "end": v(4.9, -2.03) * mm});
            skLineSegment(sketch, "E935", {"start": v(4.9, -2.03) * mm, "end": v(5.02, -2.02) * mm});
            skLineSegment(sketch, "E936", {"start": v(5.02, -2.02) * mm, "end": v(5.13, -2.03) * mm});
            skLineSegment(sketch, "E937", {"start": v(5.13, -2.03) * mm, "end": v(5.24, -2.07) * mm});
            skLineSegment(sketch, "E938", {"start": v(5.24, -2.07) * mm, "end": v(5.33, -2.13) * mm});
            skLineSegment(sketch, "E939", {"start": v(5.33, -2.13) * mm, "end": v(5.41, -2.22) * mm});
            skLineSegment(sketch, "E940", {"start": v(5.41, -2.22) * mm, "end": v(5.47, -2.32) * mm});
            skLineSegment(sketch, "E941", {"start": v(5.47, -2.32) * mm, "end": v(5.5, -2.43) * mm});
            skLineSegment(sketch, "E942", {"start": v(5.5, -2.43) * mm, "end": v(5.5, -2.54) * mm});
            skLineSegment(sketch, "E943", {"start": v(5.78, -3.91) * mm, "end": v(5.76, -4.03) * mm});
            skLineSegment(sketch, "E944", {"start": v(5.76, -4.03) * mm, "end": v(5.72, -4.13) * mm});
            skLineSegment(sketch, "E945", {"start": v(5.72, -4.13) * mm, "end": v(5.64, -4.22) * mm});
            skLineSegment(sketch, "E946", {"start": v(5.64, -4.22) * mm, "end": v(5.55, -4.29) * mm});
            skLineSegment(sketch, "E947", {"start": v(5.55, -4.29) * mm, "end": v(5.45, -4.34) * mm});
            skLineSegment(sketch, "E948", {"start": v(5.45, -4.34) * mm, "end": v(5.34, -4.36) * mm});
            skLineSegment(sketch, "E949", {"start": v(5.34, -4.36) * mm, "end": v(5.23, -4.35) * mm});
            skLineSegment(sketch, "E950", {"start": v(5.23, -4.35) * mm, "end": v(5.12, -4.32) * mm});
            skLineSegment(sketch, "E951", {"start": v(5.12, -4.32) * mm, "end": v(5.02, -4.27) * mm});
            skLineSegment(sketch, "E952", {"start": v(5.02, -4.27) * mm, "end": v(4.98, -4.23) * mm});
            skLineSegment(sketch, "E953", {"start": v(4.98, -4.23) * mm, "end": v(3.84, -5.37) * mm});
            skLineSegment(sketch, "E954", {"start": v(3.84, -5.37) * mm, "end": v(3.84, -6.52) * mm});
            skLineSegment(sketch, "E955", {"start": v(3.84, -6.52) * mm, "end": v(16.6, -19.28) * mm});
            skLineSegment(sketch, "E956", {"start": v(16.6, -19.28) * mm, "end": v(16.65, -19.32) * mm});
            skLineSegment(sketch, "E957", {"start": v(16.65, -19.32) * mm, "end": v(20.23, -22.9) * mm});
            skLineSegment(sketch, "E958", {"start": v(20.23, -22.9) * mm, "end": v(20.4, -22.81) * mm});
            skLineSegment(sketch, "E959", {"start": v(20.4, -22.81) * mm, "end": v(20.55, -22.76) * mm});
            skLineSegment(sketch, "E960", {"start": v(20.55, -22.76) * mm, "end": v(20.7, -22.74) * mm});
            skLineSegment(sketch, "E961", {"start": v(20.7, -22.74) * mm, "end": v(20.85, -22.74) * mm});
            skLineSegment(sketch, "E962", {"start": v(20.85, -22.74) * mm, "end": v(21, -22.76) * mm});
            skLineSegment(sketch, "E963", {"start": v(21, -22.76) * mm, "end": v(21.14, -22.81) * mm});
            skLineSegment(sketch, "E964", {"start": v(21.14, -22.81) * mm, "end": v(21.27, -22.88) * mm});
            skLineSegment(sketch, "E965", {"start": v(21.27, -22.88) * mm, "end": v(21.39, -22.97) * mm});
            skLineSegment(sketch, "E966", {"start": v(21.39, -22.97) * mm, "end": v(21.5, -23.07) * mm});
            skLineSegment(sketch, "E967", {"start": v(21.5, -23.07) * mm, "end": v(21.58, -23.2) * mm});
            skLineSegment(sketch, "E968", {"start": v(21.58, -23.2) * mm, "end": v(21.65, -23.32) * mm});
            skLineSegment(sketch, "E969", {"start": v(21.65, -23.32) * mm, "end": v(21.7, -23.47) * mm});
            skLineSegment(sketch, "E970", {"start": v(21.7, -23.47) * mm, "end": v(21.72, -23.61) * mm});
            skLineSegment(sketch, "E971", {"start": v(21.72, -23.61) * mm, "end": v(21.72, -23.76) * mm});
            skLineSegment(sketch, "E972", {"start": v(21.72, -23.76) * mm, "end": v(21.7, -23.91) * mm});
            skLineSegment(sketch, "E973", {"start": v(21.7, -23.91) * mm, "end": v(21.65, -24.05) * mm});
            skLineSegment(sketch, "E974", {"start": v(21.65, -24.05) * mm, "end": v(21.58, -24.19) * mm});
            skLineSegment(sketch, "E975", {"start": v(21.58, -24.19) * mm, "end": v(21.5, -24.3) * mm});
            skLineSegment(sketch, "E976", {"start": v(21.5, -24.3) * mm, "end": v(21.39, -24.41) * mm});
            skLineSegment(sketch, "E977", {"start": v(21.39, -24.41) * mm, "end": v(21.27, -24.5) * mm});
            skLineSegment(sketch, "E978", {"start": v(21.27, -24.5) * mm, "end": v(21.14, -24.57) * mm});
            skLineSegment(sketch, "E979", {"start": v(21.14, -24.57) * mm, "end": v(21, -24.62) * mm});
            skLineSegment(sketch, "E980", {"start": v(21, -24.62) * mm, "end": v(20.85, -24.64) * mm});
            skLineSegment(sketch, "E981", {"start": v(20.85, -24.64) * mm, "end": v(20.7, -24.64) * mm});
            skLineSegment(sketch, "E982", {"start": v(20.7, -24.64) * mm, "end": v(20.55, -24.62) * mm});
            skLineSegment(sketch, "E983", {"start": v(20.55, -24.62) * mm, "end": v(20.4, -24.57) * mm});
            skLineSegment(sketch, "E984", {"start": v(20.4, -24.57) * mm, "end": v(20.27, -24.5) * mm});
            skLineSegment(sketch, "E985", {"start": v(20.27, -24.5) * mm, "end": v(20.15, -24.41) * mm});
            skLineSegment(sketch, "E986", {"start": v(20.15, -24.41) * mm, "end": v(20.05, -24.3) * mm});
            skLineSegment(sketch, "E987", {"start": v(20.05, -24.3) * mm, "end": v(19.96, -24.19) * mm});
            skLineSegment(sketch, "E988", {"start": v(19.96, -24.19) * mm, "end": v(19.9, -24.05) * mm});
            skLineSegment(sketch, "E989", {"start": v(19.9, -24.05) * mm, "end": v(19.85, -23.91) * mm});
            skLineSegment(sketch, "E990", {"start": v(19.85, -23.91) * mm, "end": v(19.82, -23.76) * mm});
            skLineSegment(sketch, "E991", {"start": v(19.82, -23.76) * mm, "end": v(19.82, -23.61) * mm});
            skLineSegment(sketch, "E992", {"start": v(19.82, -23.61) * mm, "end": v(19.85, -23.47) * mm});
            skLineSegment(sketch, "E993", {"start": v(19.85, -23.47) * mm, "end": v(19.9, -23.32) * mm});
            skLineSegment(sketch, "E994", {"start": v(19.9, -23.32) * mm, "end": v(19.96, -23.2) * mm});
            skLineSegment(sketch, "E995", {"start": v(19.96, -23.2) * mm, "end": v(19.98, -23.15) * mm});
            skLineSegment(sketch, "E996", {"start": v(19.98, -23.15) * mm, "end": v(16.43, -19.6) * mm});
            skLineSegment(sketch, "E997", {"start": v(16.43, -19.6) * mm, "end": v(16.38, -19.57) * mm});
            skLineSegment(sketch, "E998", {"start": v(16.38, -19.57) * mm, "end": v(3.5, -6.69) * mm});
            skLineSegment(sketch, "E999", {"start": v(3.5, -6.69) * mm, "end": v(3.48, -6.62) * mm});
            skLineSegment(sketch, "E1000", {"start": v(3.48, -6.62) * mm, "end": v(3.48, -5.92) * mm});
            skLineSegment(sketch, "E1001", {"start": v(3.48, -5.92) * mm, "end": v(3.48, -5.26) * mm});
            skLineSegment(sketch, "E1002", {"start": v(3.48, -5.26) * mm, "end": v(3.51, -5.2) * mm});
            skLineSegment(sketch, "E1003", {"start": v(3.51, -5.2) * mm, "end": v(4.01, -4.7) * mm});
            skLineSegment(sketch, "E1004", {"start": v(4.01, -4.7) * mm, "end": v(4.82, -3.88) * mm});
            skLineSegment(sketch, "E1005", {"start": v(4.82, -3.88) * mm, "end": v(4.83, -3.76) * mm});
            skLineSegment(sketch, "E1006", {"start": v(4.83, -3.76) * mm, "end": v(4.87, -3.66) * mm});
            skLineSegment(sketch, "E1007", {"start": v(4.87, -3.66) * mm, "end": v(4.94, -3.56) * mm});
            skLineSegment(sketch, "E1008", {"start": v(4.94, -3.56) * mm, "end": v(5.02, -3.49) * mm});
            skLineSegment(sketch, "E1009", {"start": v(5.02, -3.49) * mm, "end": v(5.12, -3.43) * mm});
            skLineSegment(sketch, "E1010", {"start": v(5.12, -3.43) * mm, "end": v(5.23, -3.4) * mm});
            skLineSegment(sketch, "E1011", {"start": v(5.23, -3.4) * mm, "end": v(5.34, -3.4) * mm});
            skLineSegment(sketch, "E1012", {"start": v(5.34, -3.4) * mm, "end": v(5.45, -3.42) * mm});
            skLineSegment(sketch, "E1013", {"start": v(5.45, -3.42) * mm, "end": v(5.55, -3.46) * mm});
            skLineSegment(sketch, "E1014", {"start": v(5.55, -3.46) * mm, "end": v(5.64, -3.54) * mm});
            skLineSegment(sketch, "E1015", {"start": v(5.64, -3.54) * mm, "end": v(5.72, -3.62) * mm});
            skLineSegment(sketch, "E1016", {"start": v(5.72, -3.62) * mm, "end": v(5.76, -3.73) * mm});
            skLineSegment(sketch, "E1017", {"start": v(5.76, -3.73) * mm, "end": v(5.78, -3.84) * mm});
            skLineSegment(sketch, "E1018", {"start": v(5.78, -3.84) * mm, "end": v(5.78, -3.91) * mm});
            skLineSegment(sketch, "E1019", {"start": v(-4.57, 0.53) * mm, "end": v(-4.66, 0.49) * mm});
            skLineSegment(sketch, "E1020", {"start": v(-4.66, 0.49) * mm, "end": v(-4.77, 0.46) * mm});
            skLineSegment(sketch, "E1021", {"start": v(-4.77, 0.46) * mm, "end": v(-4.88, 0.47) * mm});
            skLineSegment(sketch, "E1022", {"start": v(-4.88, 0.47) * mm, "end": v(-5, 0.5) * mm});
            skLineSegment(sketch, "E1023", {"start": v(-5, 0.5) * mm, "end": v(-5.1, 0.56) * mm});
            skLineSegment(sketch, "E1024", {"start": v(-5.1, 0.56) * mm, "end": v(-5.18, 0.63) * mm});
            skLineSegment(sketch, "E1025", {"start": v(-5.18, 0.63) * mm, "end": v(-5.24, 0.73) * mm});
            skLineSegment(sketch, "E1026", {"start": v(-5.24, 0.73) * mm, "end": v(-5.28, 0.83) * mm});
            skLineSegment(sketch, "E1027", {"start": v(-5.28, 0.83) * mm, "end": v(-5.3, 0.95) * mm});
            skLineSegment(sketch, "E1028", {"start": v(-5.3, 0.95) * mm, "end": v(-5.28, 1.06) * mm});
            skLineSegment(sketch, "E1029", {"start": v(-5.28, 1.06) * mm, "end": v(-5.24, 1.17) * mm});
            skLineSegment(sketch, "E1030", {"start": v(-5.24, 1.17) * mm, "end": v(-5.18, 1.26) * mm});
            skLineSegment(sketch, "E1031", {"start": v(-5.18, 1.26) * mm, "end": v(-5.1, 1.34) * mm});
            skLineSegment(sketch, "E1032", {"start": v(-5.1, 1.34) * mm, "end": v(-5, 1.4) * mm});
            skLineSegment(sketch, "E1033", {"start": v(-5, 1.4) * mm, "end": v(-4.88, 1.42) * mm});
            skLineSegment(sketch, "E1034", {"start": v(-4.88, 1.42) * mm, "end": v(-4.77, 1.43) * mm});
            skLineSegment(sketch, "E1035", {"start": v(-4.77, 1.43) * mm, "end": v(-4.66, 1.4) * mm});
            skLineSegment(sketch, "E1036", {"start": v(-4.66, 1.4) * mm, "end": v(-4.56, 1.36) * mm});
            skLineSegment(sketch, "E1037", {"start": v(-4.56, 1.36) * mm, "end": v(-4.47, 1.29) * mm});
            skLineSegment(sketch, "E1038", {"start": v(-4.47, 1.29) * mm, "end": v(-4.4, 1.2) * mm});
            skLineSegment(sketch, "E1039", {"start": v(-4.4, 1.2) * mm, "end": v(-4.35, 1.1) * mm});
            skLineSegment(sketch, "E1040", {"start": v(-4.35, 1.1) * mm, "end": v(-4.33, 0.99) * mm});
            skLineSegment(sketch, "E1041", {"start": v(-4.33, 0.99) * mm, "end": v(-4.33, 0.95) * mm});
            skLineSegment(sketch, "E1042", {"start": v(-4.33, 0.95) * mm, "end": v(-4.27, 0.91) * mm});
            skLineSegment(sketch, "E1043", {"start": v(-4.27, 0.91) * mm, "end": v(-4.23, 0.86) * mm});
            skLineSegment(sketch, "E1044", {"start": v(-4.23, 0.86) * mm, "end": v(-4.22, 0.79) * mm});
            skLineSegment(sketch, "E1045", {"start": v(-4.22, 0.79) * mm, "end": v(-4.22, 0.78) * mm});
            skLineSegment(sketch, "E1046", {"start": v(-4.22, 0.78) * mm, "end": v(-4.22, -5.37) * mm});
            skLineSegment(sketch, "E1047", {"start": v(-4.22, -5.37) * mm, "end": v(-4.25, -5.44) * mm});
            skLineSegment(sketch, "E1048", {"start": v(-4.25, -5.44) * mm, "end": v(-4.75, -5.93) * mm});
            skLineSegment(sketch, "E1049", {"start": v(-4.75, -5.93) * mm, "end": v(-5.57, -6.75) * mm});
            skLineSegment(sketch, "E1050", {"start": v(-5.57, -6.75) * mm, "end": v(-5.57, -7.26) * mm});
            skLineSegment(sketch, "E1051", {"start": v(-5.57, -7.26) * mm, "end": v(10.07, -22.9) * mm});
            skLineSegment(sketch, "E1052", {"start": v(10.07, -22.9) * mm, "end": v(10.25, -22.81) * mm});
            skLineSegment(sketch, "E1053", {"start": v(10.25, -22.81) * mm, "end": v(10.39, -22.76) * mm});
            skLineSegment(sketch, "E1054", {"start": v(10.39, -22.76) * mm, "end": v(10.54, -22.74) * mm});
            skLineSegment(sketch, "E1055", {"start": v(10.54, -22.74) * mm, "end": v(10.69, -22.74) * mm});
            skLineSegment(sketch, "E1056", {"start": v(10.69, -22.74) * mm, "end": v(10.83, -22.76) * mm});
            skLineSegment(sketch, "E1057", {"start": v(10.83, -22.76) * mm, "end": v(10.98, -22.81) * mm});
            skLineSegment(sketch, "E1058", {"start": v(10.98, -22.81) * mm, "end": v(11.1, -22.88) * mm});
            skLineSegment(sketch, "E1059", {"start": v(11.1, -22.88) * mm, "end": v(11.23, -22.97) * mm});
            skLineSegment(sketch, "E1060", {"start": v(11.23, -22.97) * mm, "end": v(11.33, -23.07) * mm});
            skLineSegment(sketch, "E1061", {"start": v(11.33, -23.07) * mm, "end": v(11.42, -23.2) * mm});
            skLineSegment(sketch, "E1062", {"start": v(11.42, -23.2) * mm, "end": v(11.49, -23.32) * mm});
            skLineSegment(sketch, "E1063", {"start": v(11.49, -23.32) * mm, "end": v(11.53, -23.47) * mm});
            skLineSegment(sketch, "E1064", {"start": v(11.53, -23.47) * mm, "end": v(11.56, -23.61) * mm});
            skLineSegment(sketch, "E1065", {"start": v(11.56, -23.61) * mm, "end": v(11.56, -23.76) * mm});
            skLineSegment(sketch, "E1066", {"start": v(11.56, -23.76) * mm, "end": v(11.53, -23.91) * mm});
            skLineSegment(sketch, "E1067", {"start": v(11.53, -23.91) * mm, "end": v(11.49, -24.05) * mm});
            skLineSegment(sketch, "E1068", {"start": v(11.49, -24.05) * mm, "end": v(11.42, -24.19) * mm});
            skLineSegment(sketch, "E1069", {"start": v(11.42, -24.19) * mm, "end": v(11.33, -24.3) * mm});
            skLineSegment(sketch, "E1070", {"start": v(11.33, -24.3) * mm, "end": v(11.23, -24.41) * mm});
            skLineSegment(sketch, "E1071", {"start": v(11.23, -24.41) * mm, "end": v(11.1, -24.5) * mm});
            skLineSegment(sketch, "E1072", {"start": v(11.1, -24.5) * mm, "end": v(10.98, -24.57) * mm});
            skLineSegment(sketch, "E1073", {"start": v(10.98, -24.57) * mm, "end": v(10.83, -24.62) * mm});
            skLineSegment(sketch, "E1074", {"start": v(10.83, -24.62) * mm, "end": v(10.69, -24.64) * mm});
            skLineSegment(sketch, "E1075", {"start": v(10.69, -24.64) * mm, "end": v(10.54, -24.64) * mm});
            skLineSegment(sketch, "E1076", {"start": v(10.54, -24.64) * mm, "end": v(10.39, -24.62) * mm});
            skLineSegment(sketch, "E1077", {"start": v(10.39, -24.62) * mm, "end": v(10.25, -24.57) * mm});
            skLineSegment(sketch, "E1078", {"start": v(10.25, -24.57) * mm, "end": v(10.11, -24.5) * mm});
            skLineSegment(sketch, "E1079", {"start": v(10.11, -24.5) * mm, "end": v(10, -24.41) * mm});
            skLineSegment(sketch, "E1080", {"start": v(10, -24.41) * mm, "end": v(9.89, -24.3) * mm});
            skLineSegment(sketch, "E1081", {"start": v(9.89, -24.3) * mm, "end": v(9.8, -24.19) * mm});
            skLineSegment(sketch, "E1082", {"start": v(9.8, -24.19) * mm, "end": v(9.73, -24.05) * mm});
            skLineSegment(sketch, "E1083", {"start": v(9.73, -24.05) * mm, "end": v(9.69, -23.91) * mm});
            skLineSegment(sketch, "E1084", {"start": v(9.69, -23.91) * mm, "end": v(9.66, -23.76) * mm});
            skLineSegment(sketch, "E1085", {"start": v(9.66, -23.76) * mm, "end": v(9.66, -23.61) * mm});
            skLineSegment(sketch, "E1086", {"start": v(9.66, -23.61) * mm, "end": v(9.69, -23.47) * mm});
            skLineSegment(sketch, "E1087", {"start": v(9.69, -23.47) * mm, "end": v(9.73, -23.32) * mm});
            skLineSegment(sketch, "E1088", {"start": v(9.73, -23.32) * mm, "end": v(9.8, -23.2) * mm});
            skLineSegment(sketch, "E1089", {"start": v(9.8, -23.2) * mm, "end": v(9.82, -23.15) * mm});
            skLineSegment(sketch, "E1090", {"start": v(9.82, -23.15) * mm, "end": v(-5.88, -7.45) * mm});
            skLineSegment(sketch, "E1091", {"start": v(-5.88, -7.45) * mm, "end": v(-5.92, -7.39) * mm});
            skLineSegment(sketch, "E1092", {"start": v(-5.92, -7.39) * mm, "end": v(-5.92, -7.33) * mm});
            skLineSegment(sketch, "E1093", {"start": v(-5.92, -7.33) * mm, "end": v(-5.92, -6.64) * mm});
            skLineSegment(sketch, "E1094", {"start": v(-5.92, -6.64) * mm, "end": v(-5.9, -6.58) * mm});
            skLineSegment(sketch, "E1095", {"start": v(-5.9, -6.58) * mm, "end": v(-5.4, -6.08) * mm});
            skLineSegment(sketch, "E1096", {"start": v(-5.4, -6.08) * mm, "end": v(-4.58, -5.26) * mm});
            skLineSegment(sketch, "E1097", {"start": v(-4.58, -5.26) * mm, "end": v(-4.57, 0.53) * mm});
            skLineSegment(sketch, "E1098", {"start": v(6.44, 3.47) * mm, "end": v(6.42, 3.36) * mm});
            skLineSegment(sketch, "E1099", {"start": v(6.42, 3.36) * mm, "end": v(6.37, 3.25) * mm});
            skLineSegment(sketch, "E1100", {"start": v(6.37, 3.25) * mm, "end": v(6.3, 3.16) * mm});
            skLineSegment(sketch, "E1101", {"start": v(6.3, 3.16) * mm, "end": v(6.21, 3.1) * mm});
            skLineSegment(sketch, "E1102", {"start": v(6.21, 3.1) * mm, "end": v(6.1, 3.05) * mm});
            skLineSegment(sketch, "E1103", {"start": v(6.1, 3.05) * mm, "end": v(6, 3.03) * mm});
            skLineSegment(sketch, "E1104", {"start": v(6, 3.03) * mm, "end": v(5.97, 3.03) * mm});
            skLineSegment(sketch, "E1105", {"start": v(5.97, 3.03) * mm, "end": v(-3.78, -6.73) * mm});
            skLineSegment(sketch, "E1106", {"start": v(-3.78, -6.73) * mm, "end": v(-1.9, -8.6) * mm});
            skLineSegment(sketch, "E1107", {"start": v(-1.9, -8.6) * mm, "end": v(4.73, -15.23) * mm});
            skLineSegment(sketch, "E1108", {"start": v(4.73, -15.23) * mm, "end": v(4.79, -15.27) * mm});
            skLineSegment(sketch, "E1109", {"start": v(4.79, -15.27) * mm, "end": v(8.55, -19.03) * mm});
            skLineSegment(sketch, "E1110", {"start": v(8.55, -19.03) * mm, "end": v(8.62, -19.06) * mm});
            skLineSegment(sketch, "E1111", {"start": v(8.62, -19.06) * mm, "end": v(9.78, -20.23) * mm});
            skLineSegment(sketch, "E1112", {"start": v(9.78, -20.23) * mm, "end": v(12.53, -22.97) * mm});
            skLineSegment(sketch, "E1113", {"start": v(12.53, -22.97) * mm, "end": v(12.65, -22.88) * mm});
            skLineSegment(sketch, "E1114", {"start": v(12.65, -22.88) * mm, "end": v(12.79, -22.81) * mm});
            skLineSegment(sketch, "E1115", {"start": v(12.79, -22.81) * mm, "end": v(12.93, -22.76) * mm});
            skLineSegment(sketch, "E1116", {"start": v(12.93, -22.76) * mm, "end": v(13.08, -22.74) * mm});
            skLineSegment(sketch, "E1117", {"start": v(13.08, -22.74) * mm, "end": v(13.23, -22.74) * mm});
            skLineSegment(sketch, "E1118", {"start": v(13.23, -22.74) * mm, "end": v(13.37, -22.76) * mm});
            skLineSegment(sketch, "E1119", {"start": v(13.37, -22.76) * mm, "end": v(13.52, -22.81) * mm});
            skLineSegment(sketch, "E1120", {"start": v(13.52, -22.81) * mm, "end": v(13.65, -22.88) * mm});
            skLineSegment(sketch, "E1121", {"start": v(13.65, -22.88) * mm, "end": v(13.77, -22.97) * mm});
            skLineSegment(sketch, "E1122", {"start": v(13.77, -22.97) * mm, "end": v(13.87, -23.07) * mm});
            skLineSegment(sketch, "E1123", {"start": v(13.87, -23.07) * mm, "end": v(13.96, -23.2) * mm});
            skLineSegment(sketch, "E1124", {"start": v(13.96, -23.2) * mm, "end": v(14.03, -23.32) * mm});
            skLineSegment(sketch, "E1125", {"start": v(14.03, -23.32) * mm, "end": v(14.07, -23.47) * mm});
            skLineSegment(sketch, "E1126", {"start": v(14.07, -23.47) * mm, "end": v(14.1, -23.61) * mm});
            skLineSegment(sketch, "E1127", {"start": v(14.1, -23.61) * mm, "end": v(14.1, -23.76) * mm});
            skLineSegment(sketch, "E1128", {"start": v(14.1, -23.76) * mm, "end": v(14.07, -23.91) * mm});
            skLineSegment(sketch, "E1129", {"start": v(14.07, -23.91) * mm, "end": v(14.03, -24.05) * mm});
            skLineSegment(sketch, "E1130", {"start": v(14.03, -24.05) * mm, "end": v(13.96, -24.19) * mm});
            skLineSegment(sketch, "E1131", {"start": v(13.96, -24.19) * mm, "end": v(13.87, -24.3) * mm});
            skLineSegment(sketch, "E1132", {"start": v(13.87, -24.3) * mm, "end": v(13.77, -24.41) * mm});
            skLineSegment(sketch, "E1133", {"start": v(13.77, -24.41) * mm, "end": v(13.65, -24.5) * mm});
            skLineSegment(sketch, "E1134", {"start": v(13.65, -24.5) * mm, "end": v(13.52, -24.57) * mm});
            skLineSegment(sketch, "E1135", {"start": v(13.52, -24.57) * mm, "end": v(13.37, -24.62) * mm});
            skLineSegment(sketch, "E1136", {"start": v(13.37, -24.62) * mm, "end": v(13.23, -24.64) * mm});
            skLineSegment(sketch, "E1137", {"start": v(13.23, -24.64) * mm, "end": v(13.08, -24.64) * mm});
            skLineSegment(sketch, "E1138", {"start": v(13.08, -24.64) * mm, "end": v(12.93, -24.62) * mm});
            skLineSegment(sketch, "E1139", {"start": v(12.93, -24.62) * mm, "end": v(12.79, -24.57) * mm});
            skLineSegment(sketch, "E1140", {"start": v(12.79, -24.57) * mm, "end": v(12.65, -24.5) * mm});
            skLineSegment(sketch, "E1141", {"start": v(12.65, -24.5) * mm, "end": v(12.53, -24.41) * mm});
            skLineSegment(sketch, "E1142", {"start": v(12.53, -24.41) * mm, "end": v(12.43, -24.3) * mm});
            skLineSegment(sketch, "E1143", {"start": v(12.43, -24.3) * mm, "end": v(12.34, -24.19) * mm});
            skLineSegment(sketch, "E1144", {"start": v(12.34, -24.19) * mm, "end": v(12.27, -24.05) * mm});
            skLineSegment(sketch, "E1145", {"start": v(12.27, -24.05) * mm, "end": v(12.23, -23.91) * mm});
            skLineSegment(sketch, "E1146", {"start": v(12.23, -23.91) * mm, "end": v(12.2, -23.76) * mm});
            skLineSegment(sketch, "E1147", {"start": v(12.2, -23.76) * mm, "end": v(12.2, -23.61) * mm});
            skLineSegment(sketch, "E1148", {"start": v(12.2, -23.61) * mm, "end": v(12.23, -23.47) * mm});
            skLineSegment(sketch, "E1149", {"start": v(12.23, -23.47) * mm, "end": v(12.27, -23.32) * mm});
            skLineSegment(sketch, "E1150", {"start": v(12.27, -23.32) * mm, "end": v(12.3, -23.25) * mm});
            skLineSegment(sketch, "E1151", {"start": v(12.3, -23.25) * mm, "end": v(8.47, -19.42) * mm});
            skLineSegment(sketch, "E1152", {"start": v(8.47, -19.42) * mm, "end": v(8.4, -19.39) * mm});
            skLineSegment(sketch, "E1153", {"start": v(8.4, -19.39) * mm, "end": v(7.23, -18.22) * mm});
            skLineSegment(sketch, "E1154", {"start": v(7.23, -18.22) * mm, "end": v(4.57, -15.56) * mm});
            skLineSegment(sketch, "E1155", {"start": v(4.57, -15.56) * mm, "end": v(4.51, -15.52) * mm});
            skLineSegment(sketch, "E1156", {"start": v(4.51, -15.52) * mm, "end": v(-4.18, -6.83) * mm});
            skLineSegment(sketch, "E1157", {"start": v(-4.18, -6.83) * mm, "end": v(-4.2, -6.76) * mm});
            skLineSegment(sketch, "E1158", {"start": v(-4.2, -6.76) * mm, "end": v(-4.2, -6.7) * mm});
            skLineSegment(sketch, "E1159", {"start": v(-4.2, -6.7) * mm, "end": v(-4.19, -6.63) * mm});
            skLineSegment(sketch, "E1160", {"start": v(-4.19, -6.63) * mm, "end": v(-4.16, -6.6) * mm});
            skLineSegment(sketch, "E1161", {"start": v(-4.16, -6.6) * mm, "end": v(5.6, 3.17) * mm});
            skLineSegment(sketch, "E1162", {"start": v(5.6, 3.17) * mm, "end": v(5.53, 3.29) * mm});
            skLineSegment(sketch, "E1163", {"start": v(5.53, 3.29) * mm, "end": v(5.5, 3.4) * mm});
            skLineSegment(sketch, "E1164", {"start": v(5.5, 3.4) * mm, "end": v(5.48, 3.5) * mm});
            skLineSegment(sketch, "E1165", {"start": v(5.48, 3.5) * mm, "end": v(5.5, 3.62) * mm});
            skLineSegment(sketch, "E1166", {"start": v(5.5, 3.62) * mm, "end": v(5.53, 3.73) * mm});
            skLineSegment(sketch, "E1167", {"start": v(5.53, 3.73) * mm, "end": v(5.6, 3.82) * mm});
            skLineSegment(sketch, "E1168", {"start": v(5.6, 3.82) * mm, "end": v(5.68, 3.9) * mm});
            skLineSegment(sketch, "E1169", {"start": v(5.68, 3.9) * mm, "end": v(5.78, 3.95) * mm});
            skLineSegment(sketch, "E1170", {"start": v(5.78, 3.95) * mm, "end": v(5.89, 3.98) * mm});
            skLineSegment(sketch, "E1171", {"start": v(5.89, 3.98) * mm, "end": v(6, 3.99) * mm});
            skLineSegment(sketch, "E1172", {"start": v(6, 3.99) * mm, "end": v(6.1, 3.96) * mm});
            skLineSegment(sketch, "E1173", {"start": v(6.1, 3.96) * mm, "end": v(6.21, 3.92) * mm});
            skLineSegment(sketch, "E1174", {"start": v(6.21, 3.92) * mm, "end": v(6.3, 3.85) * mm});
            skLineSegment(sketch, "E1175", {"start": v(6.3, 3.85) * mm, "end": v(6.37, 3.76) * mm});
            skLineSegment(sketch, "E1176", {"start": v(6.37, 3.76) * mm, "end": v(6.42, 3.66) * mm});
            skLineSegment(sketch, "E1177", {"start": v(6.42, 3.66) * mm, "end": v(6.44, 3.54) * mm});
            skLineSegment(sketch, "E1178", {"start": v(6.44, 3.54) * mm, "end": v(6.44, 3.47) * mm});
            skLineSegment(sketch, "E1179", {"start": v(9.27, 3.43) * mm, "end": v(9.25, 3.32) * mm});
            skLineSegment(sketch, "E1180", {"start": v(9.25, 3.32) * mm, "end": v(9.2, 3.22) * mm});
            skLineSegment(sketch, "E1181", {"start": v(9.2, 3.22) * mm, "end": v(9.13, 3.13) * mm});
            skLineSegment(sketch, "E1182", {"start": v(9.13, 3.13) * mm, "end": v(9.04, 3.06) * mm});
            skLineSegment(sketch, "E1183", {"start": v(9.04, 3.06) * mm, "end": v(8.96, 3.02) * mm});
            skLineSegment(sketch, "E1184", {"start": v(8.96, 3.02) * mm, "end": v(8.96, -2.35) * mm});
            skLineSegment(sketch, "E1185", {"start": v(8.96, -2.35) * mm, "end": v(8.94, -2.41) * mm});
            skLineSegment(sketch, "E1186", {"start": v(8.94, -2.41) * mm, "end": v(8.91, -2.45) * mm});
            skLineSegment(sketch, "E1187", {"start": v(8.91, -2.45) * mm, "end": v(5.04, -6.32) * mm});
            skLineSegment(sketch, "E1188", {"start": v(5.04, -6.32) * mm, "end": v(7.5, -8.8) * mm});
            skLineSegment(sketch, "E1189", {"start": v(7.5, -8.8) * mm, "end": v(8.62, -8.8) * mm});
            skLineSegment(sketch, "E1190", {"start": v(8.62, -8.8) * mm, "end": v(8.68, -8.83) * mm});
            skLineSegment(sketch, "E1191", {"start": v(8.68, -8.83) * mm, "end": v(9.18, -9.32) * mm});
            skLineSegment(sketch, "E1192", {"start": v(9.18, -9.32) * mm, "end": v(9.49, -9.62) * mm});
            skLineSegment(sketch, "E1193", {"start": v(9.49, -9.62) * mm, "end": v(9.61, -9.74) * mm});
            skLineSegment(sketch, "E1194", {"start": v(9.61, -9.74) * mm, "end": v(22.78, -22.9) * mm});
            skLineSegment(sketch, "E1195", {"start": v(22.78, -22.9) * mm, "end": v(22.88, -22.84) * mm});
            skLineSegment(sketch, "E1196", {"start": v(22.88, -22.84) * mm, "end": v(23.01, -22.78) * mm});
            skLineSegment(sketch, "E1197", {"start": v(23.01, -22.78) * mm, "end": v(23.16, -22.75) * mm});
            skLineSegment(sketch, "E1198", {"start": v(23.16, -22.75) * mm, "end": v(23.3, -22.74) * mm});
            skLineSegment(sketch, "E1199", {"start": v(23.3, -22.74) * mm, "end": v(23.46, -22.75) * mm});
            skLineSegment(sketch, "E1200", {"start": v(23.46, -22.75) * mm, "end": v(23.6, -22.78) * mm});
            skLineSegment(sketch, "E1201", {"start": v(23.6, -22.78) * mm, "end": v(23.74, -22.84) * mm});
            skLineSegment(sketch, "E1202", {"start": v(23.74, -22.84) * mm, "end": v(23.87, -22.92) * mm});
            skLineSegment(sketch, "E1203", {"start": v(23.87, -22.92) * mm, "end": v(23.98, -23.02) * mm});
            skLineSegment(sketch, "E1204", {"start": v(23.98, -23.02) * mm, "end": v(24.08, -23.13) * mm});
            skLineSegment(sketch, "E1205", {"start": v(24.08, -23.13) * mm, "end": v(24.16, -23.26) * mm});
            skLineSegment(sketch, "E1206", {"start": v(24.16, -23.26) * mm, "end": v(24.21, -23.4) * mm});
            skLineSegment(sketch, "E1207", {"start": v(24.21, -23.4) * mm, "end": v(24.25, -23.54) * mm});
            skLineSegment(sketch, "E1208", {"start": v(24.25, -23.54) * mm, "end": v(24.26, -23.7) * mm});
            skLineSegment(sketch, "E1209", {"start": v(24.26, -23.7) * mm, "end": v(24.25, -23.84) * mm});
            skLineSegment(sketch, "E1210", {"start": v(24.25, -23.84) * mm, "end": v(24.21, -23.99) * mm});
            skLineSegment(sketch, "E1211", {"start": v(24.21, -23.99) * mm, "end": v(24.16, -24.12) * mm});
            skLineSegment(sketch, "E1212", {"start": v(24.16, -24.12) * mm, "end": v(24.08, -24.25) * mm});
            skLineSegment(sketch, "E1213", {"start": v(24.08, -24.25) * mm, "end": v(23.98, -24.36) * mm});
            skLineSegment(sketch, "E1214", {"start": v(23.98, -24.36) * mm, "end": v(23.87, -24.46) * mm});
            skLineSegment(sketch, "E1215", {"start": v(23.87, -24.46) * mm, "end": v(23.74, -24.54) * mm});
            skLineSegment(sketch, "E1216", {"start": v(23.74, -24.54) * mm, "end": v(23.6, -24.6) * mm});
            skLineSegment(sketch, "E1217", {"start": v(23.6, -24.6) * mm, "end": v(23.46, -24.63) * mm});
            skLineSegment(sketch, "E1218", {"start": v(23.46, -24.63) * mm, "end": v(23.3, -24.64) * mm});
            skLineSegment(sketch, "E1219", {"start": v(23.3, -24.64) * mm, "end": v(23.16, -24.63) * mm});
            skLineSegment(sketch, "E1220", {"start": v(23.16, -24.63) * mm, "end": v(23.01, -24.6) * mm});
            skLineSegment(sketch, "E1221", {"start": v(23.01, -24.6) * mm, "end": v(22.88, -24.54) * mm});
            skLineSegment(sketch, "E1222", {"start": v(22.88, -24.54) * mm, "end": v(22.75, -24.46) * mm});
            skLineSegment(sketch, "E1223", {"start": v(22.75, -24.46) * mm, "end": v(22.64, -24.36) * mm});
            skLineSegment(sketch, "E1224", {"start": v(22.64, -24.36) * mm, "end": v(22.54, -24.25) * mm});
            skLineSegment(sketch, "E1225", {"start": v(22.54, -24.25) * mm, "end": v(22.46, -24.12) * mm});
            skLineSegment(sketch, "E1226", {"start": v(22.46, -24.12) * mm, "end": v(22.4, -23.99) * mm});
            skLineSegment(sketch, "E1227", {"start": v(22.4, -23.99) * mm, "end": v(22.37, -23.84) * mm});
            skLineSegment(sketch, "E1228", {"start": v(22.37, -23.84) * mm, "end": v(22.36, -23.7) * mm});
            skLineSegment(sketch, "E1229", {"start": v(22.36, -23.7) * mm, "end": v(22.37, -23.54) * mm});
            skLineSegment(sketch, "E1230", {"start": v(22.37, -23.54) * mm, "end": v(22.4, -23.4) * mm});
            skLineSegment(sketch, "E1231", {"start": v(22.4, -23.4) * mm, "end": v(22.46, -23.26) * mm});
            skLineSegment(sketch, "E1232", {"start": v(22.46, -23.26) * mm, "end": v(22.52, -23.15) * mm});
            skLineSegment(sketch, "E1233", {"start": v(22.52, -23.15) * mm, "end": v(9.3, -9.94) * mm});
            skLineSegment(sketch, "E1234", {"start": v(9.3, -9.94) * mm, "end": v(9.25, -9.9) * mm});
            skLineSegment(sketch, "E1235", {"start": v(9.25, -9.9) * mm, "end": v(8.5, -9.15) * mm});
            skLineSegment(sketch, "E1236", {"start": v(8.5, -9.15) * mm, "end": v(7.4, -9.14) * mm});
            skLineSegment(sketch, "E1237", {"start": v(7.4, -9.14) * mm, "end": v(7.33, -9.11) * mm});
            skLineSegment(sketch, "E1238", {"start": v(7.33, -9.11) * mm, "end": v(6.83, -8.62) * mm});
            skLineSegment(sketch, "E1239", {"start": v(6.83, -8.62) * mm, "end": v(4.69, -6.47) * mm});
            skLineSegment(sketch, "E1240", {"start": v(4.69, -6.47) * mm, "end": v(4.66, -6.4) * mm});
            skLineSegment(sketch, "E1241", {"start": v(4.66, -6.4) * mm, "end": v(4.66, -6.24) * mm});
            skLineSegment(sketch, "E1242", {"start": v(4.66, -6.24) * mm, "end": v(4.69, -6.17) * mm});
            skLineSegment(sketch, "E1243", {"start": v(4.69, -6.17) * mm, "end": v(4.71, -6.14) * mm});
            skLineSegment(sketch, "E1244", {"start": v(4.71, -6.14) * mm, "end": v(8.6, -2.25) * mm});
            skLineSegment(sketch, "E1245", {"start": v(8.6, -2.25) * mm, "end": v(8.6, 3.02) * mm});
            skLineSegment(sketch, "E1246", {"start": v(8.6, 3.02) * mm, "end": v(8.5, 3.08) * mm});
            skLineSegment(sketch, "E1247", {"start": v(8.5, 3.08) * mm, "end": v(8.42, 3.16) * mm});
            skLineSegment(sketch, "E1248", {"start": v(8.42, 3.16) * mm, "end": v(8.36, 3.25) * mm});
            skLineSegment(sketch, "E1249", {"start": v(8.36, 3.25) * mm, "end": v(8.32, 3.36) * mm});
            skLineSegment(sketch, "E1250", {"start": v(8.32, 3.36) * mm, "end": v(8.3, 3.47) * mm});
            skLineSegment(sketch, "E1251", {"start": v(8.3, 3.47) * mm, "end": v(8.32, 3.58) * mm});
            skLineSegment(sketch, "E1252", {"start": v(8.32, 3.58) * mm, "end": v(8.36, 3.69) * mm});
            skLineSegment(sketch, "E1253", {"start": v(8.36, 3.69) * mm, "end": v(8.42, 3.78) * mm});
            skLineSegment(sketch, "E1254", {"start": v(8.42, 3.78) * mm, "end": v(8.5, 3.86) * mm});
            skLineSegment(sketch, "E1255", {"start": v(8.5, 3.86) * mm, "end": v(8.6, 3.92) * mm});
            skLineSegment(sketch, "E1256", {"start": v(8.6, 3.92) * mm, "end": v(8.71, 3.95) * mm});
            skLineSegment(sketch, "E1257", {"start": v(8.71, 3.95) * mm, "end": v(8.82, 3.95) * mm});
            skLineSegment(sketch, "E1258", {"start": v(8.82, 3.95) * mm, "end": v(8.94, 3.93) * mm});
            skLineSegment(sketch, "E1259", {"start": v(8.94, 3.93) * mm, "end": v(9.04, 3.88) * mm});
            skLineSegment(sketch, "E1260", {"start": v(9.04, 3.88) * mm, "end": v(9.13, 3.8) * mm});
            skLineSegment(sketch, "E1261", {"start": v(9.13, 3.8) * mm, "end": v(9.2, 3.72) * mm});
            skLineSegment(sketch, "E1262", {"start": v(9.2, 3.72) * mm, "end": v(9.25, 3.62) * mm});
            skLineSegment(sketch, "E1263", {"start": v(9.25, 3.62) * mm, "end": v(9.27, 3.5) * mm});
            skLineSegment(sketch, "E1264", {"start": v(9.27, 3.5) * mm, "end": v(9.27, 3.43) * mm});
            skLineSegment(sketch, "E1265", {"start": v(6.62, 1.05) * mm, "end": v(6.6, 0.94) * mm});
            skLineSegment(sketch, "E1266", {"start": v(6.6, 0.94) * mm, "end": v(6.55, 0.84) * mm});
            skLineSegment(sketch, "E1267", {"start": v(6.55, 0.84) * mm, "end": v(6.48, 0.74) * mm});
            skLineSegment(sketch, "E1268", {"start": v(6.48, 0.74) * mm, "end": v(6.4, 0.68) * mm});
            skLineSegment(sketch, "E1269", {"start": v(6.4, 0.68) * mm, "end": v(6.29, 0.63) * mm});
            skLineSegment(sketch, "E1270", {"start": v(6.29, 0.63) * mm, "end": v(6.18, 0.6) * mm});
            skLineSegment(sketch, "E1271", {"start": v(6.18, 0.6) * mm, "end": v(6.07, 0.6) * mm});
            skLineSegment(sketch, "E1272", {"start": v(6.07, 0.6) * mm, "end": v(5.96, 0.64) * mm});
            skLineSegment(sketch, "E1273", {"start": v(5.96, 0.64) * mm, "end": v(5.86, 0.7) * mm});
            skLineSegment(sketch, "E1274", {"start": v(5.86, 0.7) * mm, "end": v(5.84, 0.71) * mm});
            skLineSegment(sketch, "E1275", {"start": v(5.84, 0.71) * mm, "end": v(-1.1, -6.23) * mm});
            skLineSegment(sketch, "E1276", {"start": v(-1.1, -6.23) * mm, "end": v(-1.1, -6.62) * mm});
            skLineSegment(sketch, "E1277", {"start": v(-1.1, -6.62) * mm, "end": v(6.44, -14.17) * mm});
            skLineSegment(sketch, "E1278", {"start": v(6.44, -14.17) * mm, "end": v(6.46, -14.2) * mm});
            skLineSegment(sketch, "E1279", {"start": v(6.46, -14.2) * mm, "end": v(15.15, -22.9) * mm});
            skLineSegment(sketch, "E1280", {"start": v(15.15, -22.9) * mm, "end": v(15.33, -22.81) * mm});
            skLineSegment(sketch, "E1281", {"start": v(15.33, -22.81) * mm, "end": v(15.47, -22.76) * mm});
            skLineSegment(sketch, "E1282", {"start": v(15.47, -22.76) * mm, "end": v(15.62, -22.74) * mm});
            skLineSegment(sketch, "E1283", {"start": v(15.62, -22.74) * mm, "end": v(15.77, -22.74) * mm});
            skLineSegment(sketch, "E1284", {"start": v(15.77, -22.74) * mm, "end": v(15.91, -22.76) * mm});
            skLineSegment(sketch, "E1285", {"start": v(15.91, -22.76) * mm, "end": v(16.06, -22.81) * mm});
            skLineSegment(sketch, "E1286", {"start": v(16.06, -22.81) * mm, "end": v(16.19, -22.88) * mm});
            skLineSegment(sketch, "E1287", {"start": v(16.19, -22.88) * mm, "end": v(16.3, -22.97) * mm});
            skLineSegment(sketch, "E1288", {"start": v(16.3, -22.97) * mm, "end": v(16.41, -23.07) * mm});
            skLineSegment(sketch, "E1289", {"start": v(16.41, -23.07) * mm, "end": v(16.5, -23.2) * mm});
            skLineSegment(sketch, "E1290", {"start": v(16.5, -23.2) * mm, "end": v(16.57, -23.32) * mm});
            skLineSegment(sketch, "E1291", {"start": v(16.57, -23.32) * mm, "end": v(16.61, -23.47) * mm});
            skLineSegment(sketch, "E1292", {"start": v(16.61, -23.47) * mm, "end": v(16.64, -23.61) * mm});
            skLineSegment(sketch, "E1293", {"start": v(16.64, -23.61) * mm, "end": v(16.64, -23.76) * mm});
            skLineSegment(sketch, "E1294", {"start": v(16.64, -23.76) * mm, "end": v(16.61, -23.91) * mm});
            skLineSegment(sketch, "E1295", {"start": v(16.61, -23.91) * mm, "end": v(16.57, -24.05) * mm});
            skLineSegment(sketch, "E1296", {"start": v(16.57, -24.05) * mm, "end": v(16.5, -24.19) * mm});
            skLineSegment(sketch, "E1297", {"start": v(16.5, -24.19) * mm, "end": v(16.41, -24.3) * mm});
            skLineSegment(sketch, "E1298", {"start": v(16.41, -24.3) * mm, "end": v(16.3, -24.41) * mm});
            skLineSegment(sketch, "E1299", {"start": v(16.3, -24.41) * mm, "end": v(16.19, -24.5) * mm});
            skLineSegment(sketch, "E1300", {"start": v(16.19, -24.5) * mm, "end": v(16.06, -24.57) * mm});
            skLineSegment(sketch, "E1301", {"start": v(16.06, -24.57) * mm, "end": v(15.91, -24.62) * mm});
            skLineSegment(sketch, "E1302", {"start": v(15.91, -24.62) * mm, "end": v(15.77, -24.64) * mm});
            skLineSegment(sketch, "E1303", {"start": v(15.77, -24.64) * mm, "end": v(15.62, -24.64) * mm});
            skLineSegment(sketch, "E1304", {"start": v(15.62, -24.64) * mm, "end": v(15.47, -24.62) * mm});
            skLineSegment(sketch, "E1305", {"start": v(15.47, -24.62) * mm, "end": v(15.33, -24.57) * mm});
            skLineSegment(sketch, "E1306", {"start": v(15.33, -24.57) * mm, "end": v(15.2, -24.5) * mm});
            skLineSegment(sketch, "E1307", {"start": v(15.2, -24.5) * mm, "end": v(15.07, -24.41) * mm});
            skLineSegment(sketch, "E1308", {"start": v(15.07, -24.41) * mm, "end": v(14.97, -24.3) * mm});
            skLineSegment(sketch, "E1309", {"start": v(14.97, -24.3) * mm, "end": v(14.88, -24.19) * mm});
            skLineSegment(sketch, "E1310", {"start": v(14.88, -24.19) * mm, "end": v(14.81, -24.05) * mm});
            skLineSegment(sketch, "E1311", {"start": v(14.81, -24.05) * mm, "end": v(14.77, -23.91) * mm});
            skLineSegment(sketch, "E1312", {"start": v(14.77, -23.91) * mm, "end": v(14.74, -23.76) * mm});
            skLineSegment(sketch, "E1313", {"start": v(14.74, -23.76) * mm, "end": v(14.74, -23.61) * mm});
            skLineSegment(sketch, "E1314", {"start": v(14.74, -23.61) * mm, "end": v(14.77, -23.47) * mm});
            skLineSegment(sketch, "E1315", {"start": v(14.77, -23.47) * mm, "end": v(14.81, -23.32) * mm});
            skLineSegment(sketch, "E1316", {"start": v(14.81, -23.32) * mm, "end": v(14.88, -23.2) * mm});
            skLineSegment(sketch, "E1317", {"start": v(14.88, -23.2) * mm, "end": v(14.9, -23.15) * mm});
            skLineSegment(sketch, "E1318", {"start": v(14.9, -23.15) * mm, "end": v(6.15, -14.4) * mm});
            skLineSegment(sketch, "E1319", {"start": v(6.15, -14.4) * mm, "end": v(6.12, -14.35) * mm});
            skLineSegment(sketch, "E1320", {"start": v(6.12, -14.35) * mm, "end": v(-1.43, -6.8) * mm});
            skLineSegment(sketch, "E1321", {"start": v(-1.43, -6.8) * mm, "end": v(-1.46, -6.73) * mm});
            skLineSegment(sketch, "E1322", {"start": v(-1.46, -6.73) * mm, "end": v(-1.47, -6.7) * mm});
            skLineSegment(sketch, "E1323", {"start": v(-1.47, -6.7) * mm, "end": v(-1.46, -6.12) * mm});
            skLineSegment(sketch, "E1324", {"start": v(-1.46, -6.12) * mm, "end": v(-1.43, -6.06) * mm});
            skLineSegment(sketch, "E1325", {"start": v(-1.43, -6.06) * mm, "end": v(-0.93, -5.55) * mm});
            skLineSegment(sketch, "E1326", {"start": v(-0.93, -5.55) * mm, "end": v(5.66, 1.04) * mm});
            skLineSegment(sketch, "E1327", {"start": v(5.66, 1.04) * mm, "end": v(5.66, 1.13) * mm});
            skLineSegment(sketch, "E1328", {"start": v(5.66, 1.13) * mm, "end": v(5.68, 1.24) * mm});
            skLineSegment(sketch, "E1329", {"start": v(5.68, 1.24) * mm, "end": v(5.73, 1.34) * mm});
            skLineSegment(sketch, "E1330", {"start": v(5.73, 1.34) * mm, "end": v(5.8, 1.43) * mm});
            skLineSegment(sketch, "E1331", {"start": v(5.8, 1.43) * mm, "end": v(5.89, 1.5) * mm});
            skLineSegment(sketch, "E1332", {"start": v(5.89, 1.5) * mm, "end": v(6, 1.55) * mm});
            skLineSegment(sketch, "E1333", {"start": v(6, 1.55) * mm, "end": v(6.1, 1.57) * mm});
            skLineSegment(sketch, "E1334", {"start": v(6.1, 1.57) * mm, "end": v(6.22, 1.56) * mm});
            skLineSegment(sketch, "E1335", {"start": v(6.22, 1.56) * mm, "end": v(6.32, 1.53) * mm});
            skLineSegment(sketch, "E1336", {"start": v(6.32, 1.53) * mm, "end": v(6.42, 1.48) * mm});
            skLineSegment(sketch, "E1337", {"start": v(6.42, 1.48) * mm, "end": v(6.5, 1.4) * mm});
            skLineSegment(sketch, "E1338", {"start": v(6.5, 1.4) * mm, "end": v(6.57, 1.3) * mm});
            skLineSegment(sketch, "E1339", {"start": v(6.57, 1.3) * mm, "end": v(6.6, 1.2) * mm});
            skLineSegment(sketch, "E1340", {"start": v(6.6, 1.2) * mm, "end": v(6.62, 1.09) * mm});
            skLineSegment(sketch, "E1341", {"start": v(6.62, 1.09) * mm, "end": v(6.62, 1.05) * mm});
            skLineSegment(sketch, "E1342", {"start": v(14.77, -5.64) * mm, "end": v(15.6, -5.64) * mm});
            skLineSegment(sketch, "E1343", {"start": v(15.6, -5.64) * mm, "end": v(15.6, -5.95) * mm});
            skLineSegment(sketch, "E1344", {"start": v(15.6, -5.95) * mm, "end": v(16.07, -5.95) * mm});
            skLineSegment(sketch, "E1345", {"start": v(16.07, -5.95) * mm, "end": v(30.17, -5.95) * mm});
            skLineSegment(sketch, "E1346", {"start": v(30.17, -5.95) * mm, "end": v(30.23, -5.98) * mm});
            skLineSegment(sketch, "E1347", {"start": v(30.23, -5.98) * mm, "end": v(30.73, -6.48) * mm});
            skLineSegment(sketch, "E1348", {"start": v(30.73, -6.48) * mm, "end": v(36, -11.74) * mm});
            skLineSegment(sketch, "E1349", {"start": v(36, -11.74) * mm, "end": v(36.17, -11.65) * mm});
            skLineSegment(sketch, "E1350", {"start": v(36.17, -11.65) * mm, "end": v(36.3, -11.6) * mm});
            skLineSegment(sketch, "E1351", {"start": v(36.3, -11.6) * mm, "end": v(36.45, -11.58) * mm});
            skLineSegment(sketch, "E1352", {"start": v(36.45, -11.58) * mm, "end": v(36.6, -11.58) * mm});
            skLineSegment(sketch, "E1353", {"start": v(36.6, -11.58) * mm, "end": v(36.75, -11.6) * mm});
            skLineSegment(sketch, "E1354", {"start": v(36.75, -11.6) * mm, "end": v(36.9, -11.65) * mm});
            skLineSegment(sketch, "E1355", {"start": v(36.9, -11.65) * mm, "end": v(37.03, -11.72) * mm});
            skLineSegment(sketch, "E1356", {"start": v(37.03, -11.72) * mm, "end": v(37.15, -11.81) * mm});
            skLineSegment(sketch, "E1357", {"start": v(37.15, -11.81) * mm, "end": v(37.25, -11.92) * mm});
            skLineSegment(sketch, "E1358", {"start": v(37.25, -11.92) * mm, "end": v(37.34, -12.04) * mm});
            skLineSegment(sketch, "E1359", {"start": v(37.34, -12.04) * mm, "end": v(37.4, -12.17) * mm});
            skLineSegment(sketch, "E1360", {"start": v(37.4, -12.17) * mm, "end": v(37.45, -12.31) * mm});
            skLineSegment(sketch, "E1361", {"start": v(37.45, -12.31) * mm, "end": v(37.48, -12.46) * mm});
            skLineSegment(sketch, "E1362", {"start": v(37.48, -12.46) * mm, "end": v(37.48, -12.6) * mm});
            skLineSegment(sketch, "E1363", {"start": v(37.48, -12.6) * mm, "end": v(37.45, -12.76) * mm});
            skLineSegment(sketch, "E1364", {"start": v(37.45, -12.76) * mm, "end": v(37.4, -12.9) * mm});
            skLineSegment(sketch, "E1365", {"start": v(37.4, -12.9) * mm, "end": v(37.34, -13.03) * mm});
            skLineSegment(sketch, "E1366", {"start": v(37.34, -13.03) * mm, "end": v(37.25, -13.15) * mm});
            skLineSegment(sketch, "E1367", {"start": v(37.25, -13.15) * mm, "end": v(37.15, -13.26) * mm});
            skLineSegment(sketch, "E1368", {"start": v(37.15, -13.26) * mm, "end": v(37.03, -13.35) * mm});
            skLineSegment(sketch, "E1369", {"start": v(37.03, -13.35) * mm, "end": v(36.9, -13.41) * mm});
            skLineSegment(sketch, "E1370", {"start": v(36.9, -13.41) * mm, "end": v(36.75, -13.46) * mm});
            skLineSegment(sketch, "E1371", {"start": v(36.75, -13.46) * mm, "end": v(36.6, -13.48) * mm});
            skLineSegment(sketch, "E1372", {"start": v(36.6, -13.48) * mm, "end": v(36.45, -13.48) * mm});
            skLineSegment(sketch, "E1373", {"start": v(36.45, -13.48) * mm, "end": v(36.3, -13.46) * mm});
            skLineSegment(sketch, "E1374", {"start": v(36.3, -13.46) * mm, "end": v(36.17, -13.41) * mm});
            skLineSegment(sketch, "E1375", {"start": v(36.17, -13.41) * mm, "end": v(36.03, -13.35) * mm});
            skLineSegment(sketch, "E1376", {"start": v(36.03, -13.35) * mm, "end": v(35.91, -13.26) * mm});
            skLineSegment(sketch, "E1377", {"start": v(35.91, -13.26) * mm, "end": v(35.8, -13.15) * mm});
            skLineSegment(sketch, "E1378", {"start": v(35.8, -13.15) * mm, "end": v(35.72, -13.03) * mm});
            skLineSegment(sketch, "E1379", {"start": v(35.72, -13.03) * mm, "end": v(35.65, -12.9) * mm});
            skLineSegment(sketch, "E1380", {"start": v(35.65, -12.9) * mm, "end": v(35.6, -12.76) * mm});
            skLineSegment(sketch, "E1381", {"start": v(35.6, -12.76) * mm, "end": v(35.58, -12.6) * mm});
            skLineSegment(sketch, "E1382", {"start": v(35.58, -12.6) * mm, "end": v(35.58, -12.46) * mm});
            skLineSegment(sketch, "E1383", {"start": v(35.58, -12.46) * mm, "end": v(35.6, -12.31) * mm});
            skLineSegment(sketch, "E1384", {"start": v(35.6, -12.31) * mm, "end": v(35.65, -12.17) * mm});
            skLineSegment(sketch, "E1385", {"start": v(35.65, -12.17) * mm, "end": v(35.72, -12.04) * mm});
            skLineSegment(sketch, "E1386", {"start": v(35.72, -12.04) * mm, "end": v(35.74, -12) * mm});
            skLineSegment(sketch, "E1387", {"start": v(35.74, -12) * mm, "end": v(30.05, -6.3) * mm});
            skLineSegment(sketch, "E1388", {"start": v(30.05, -6.3) * mm, "end": v(25.11, -6.3) * mm});
            skLineSegment(sketch, "E1389", {"start": v(25.11, -6.3) * mm, "end": v(15.6, -6.3) * mm});
            skLineSegment(sketch, "E1390", {"start": v(15.6, -6.3) * mm, "end": v(15.6, -6.6) * mm});
            skLineSegment(sketch, "E1391", {"start": v(15.6, -6.6) * mm, "end": v(15.3, -6.6) * mm});
            skLineSegment(sketch, "E1392", {"start": v(15.3, -6.6) * mm, "end": v(15.3, -7.07) * mm});
            skLineSegment(sketch, "E1393", {"start": v(15.3, -7.07) * mm, "end": v(15.3, -7.8) * mm});
            skLineSegment(sketch, "E1394", {"start": v(15.3, -7.8) * mm, "end": v(22.81, -15.32) * mm});
            skLineSegment(sketch, "E1395", {"start": v(22.81, -15.32) * mm, "end": v(30.23, -22.74) * mm});
            skLineSegment(sketch, "E1396", {"start": v(30.23, -22.74) * mm, "end": v(31.88, -22.74) * mm});
            skLineSegment(sketch, "E1397", {"start": v(31.88, -22.74) * mm, "end": v(31.88, -24.64) * mm});
            skLineSegment(sketch, "E1398", {"start": v(31.88, -24.64) * mm, "end": v(29.98, -24.64) * mm});
            skLineSegment(sketch, "E1399", {"start": v(29.98, -24.64) * mm, "end": v(29.98, -22.99) * mm});
            skLineSegment(sketch, "E1400", {"start": v(29.98, -22.99) * mm, "end": v(28.7, -21.7) * mm});
            skLineSegment(sketch, "E1401", {"start": v(28.7, -21.7) * mm, "end": v(14.97, -7.97) * mm});
            skLineSegment(sketch, "E1402", {"start": v(14.97, -7.97) * mm, "end": v(14.95, -7.9) * mm});
            skLineSegment(sketch, "E1403", {"start": v(14.95, -7.9) * mm, "end": v(14.94, -7.2) * mm});
            skLineSegment(sketch, "E1404", {"start": v(14.94, -7.2) * mm, "end": v(14.94, -6.6) * mm});
            skLineSegment(sketch, "E1405", {"start": v(14.94, -6.6) * mm, "end": v(14.64, -6.6) * mm});
            skLineSegment(sketch, "E1406", {"start": v(14.64, -6.6) * mm, "end": v(14.64, -5.64) * mm});
            skLineSegment(sketch, "E1407", {"start": v(14.64, -5.64) * mm, "end": v(14.77, -5.64) * mm});
            skLineSegment(sketch, "E1408", {"start": v(7.63, -5.7) * mm, "end": v(8.46, -5.7) * mm});
            skLineSegment(sketch, "E1409", {"start": v(8.46, -5.7) * mm, "end": v(8.46, -6) * mm});
            skLineSegment(sketch, "E1410", {"start": v(8.46, -6) * mm, "end": v(8.92, -6) * mm});
            skLineSegment(sketch, "E1411", {"start": v(8.92, -6) * mm, "end": v(12.24, -6) * mm});
            skLineSegment(sketch, "E1412", {"start": v(12.24, -6) * mm, "end": v(13.82, -4.43) * mm});
            skLineSegment(sketch, "E1413", {"start": v(13.82, -4.43) * mm, "end": v(14.14, -4.11) * mm});
            skLineSegment(sketch, "E1414", {"start": v(14.14, -4.11) * mm, "end": v(14.2, -4.09) * mm});
            skLineSegment(sketch, "E1415", {"start": v(14.2, -4.09) * mm, "end": v(14.9, -4.08) * mm});
            skLineSegment(sketch, "E1416", {"start": v(14.9, -4.08) * mm, "end": v(30.84, -4.09) * mm});
            skLineSegment(sketch, "E1417", {"start": v(30.84, -4.09) * mm, "end": v(30.9, -4.12) * mm});
            skLineSegment(sketch, "E1418", {"start": v(30.9, -4.12) * mm, "end": v(31.4, -4.62) * mm});
            skLineSegment(sketch, "E1419", {"start": v(31.4, -4.62) * mm, "end": v(35.83, -9.04) * mm});
            skLineSegment(sketch, "E1420", {"start": v(35.83, -9.04) * mm, "end": v(37.48, -9.04) * mm});
            skLineSegment(sketch, "E1421", {"start": v(37.48, -9.04) * mm, "end": v(37.48, -10.94) * mm});
            skLineSegment(sketch, "E1422", {"start": v(37.48, -10.94) * mm, "end": v(35.58, -10.94) * mm});
            skLineSegment(sketch, "E1423", {"start": v(35.58, -10.94) * mm, "end": v(35.58, -9.29) * mm});
            skLineSegment(sketch, "E1424", {"start": v(35.58, -9.29) * mm, "end": v(34.3, -8.01) * mm});
            skLineSegment(sketch, "E1425", {"start": v(34.3, -8.01) * mm, "end": v(30.73, -4.44) * mm});
            skLineSegment(sketch, "E1426", {"start": v(30.73, -4.44) * mm, "end": v(14.3, -4.44) * mm});
            skLineSegment(sketch, "E1427", {"start": v(14.3, -4.44) * mm, "end": v(13.5, -5.25) * mm});
            skLineSegment(sketch, "E1428", {"start": v(13.5, -5.25) * mm, "end": v(12.4, -6.33) * mm});
            skLineSegment(sketch, "E1429", {"start": v(12.4, -6.33) * mm, "end": v(12.34, -6.36) * mm});
            skLineSegment(sketch, "E1430", {"start": v(12.34, -6.36) * mm, "end": v(11.64, -6.36) * mm});
            skLineSegment(sketch, "E1431", {"start": v(11.64, -6.36) * mm, "end": v(11.15, -6.36) * mm});
            skLineSegment(sketch, "E1432", {"start": v(11.15, -6.36) * mm, "end": v(13.46, -8.68) * mm});
            skLineSegment(sketch, "E1433", {"start": v(13.46, -8.68) * mm, "end": v(13.6, -8.68) * mm});
            skLineSegment(sketch, "E1434", {"start": v(13.6, -8.68) * mm, "end": v(13.66, -8.7) * mm});
            skLineSegment(sketch, "E1435", {"start": v(13.66, -8.7) * mm, "end": v(14.16, -9.2) * mm});
            skLineSegment(sketch, "E1436", {"start": v(14.16, -9.2) * mm, "end": v(27.85, -22.9) * mm});
            skLineSegment(sketch, "E1437", {"start": v(27.85, -22.9) * mm, "end": v(28.03, -22.81) * mm});
            skLineSegment(sketch, "E1438", {"start": v(28.03, -22.81) * mm, "end": v(28.17, -22.76) * mm});
            skLineSegment(sketch, "E1439", {"start": v(28.17, -22.76) * mm, "end": v(28.32, -22.74) * mm});
            skLineSegment(sketch, "E1440", {"start": v(28.32, -22.74) * mm, "end": v(28.47, -22.74) * mm});
            skLineSegment(sketch, "E1441", {"start": v(28.47, -22.74) * mm, "end": v(28.61, -22.76) * mm});
            skLineSegment(sketch, "E1442", {"start": v(28.61, -22.76) * mm, "end": v(28.76, -22.81) * mm});
            skLineSegment(sketch, "E1443", {"start": v(28.76, -22.81) * mm, "end": v(28.89, -22.88) * mm});
            skLineSegment(sketch, "E1444", {"start": v(28.89, -22.88) * mm, "end": v(29, -22.97) * mm});
            skLineSegment(sketch, "E1445", {"start": v(29, -22.97) * mm, "end": v(29.11, -23.07) * mm});
            skLineSegment(sketch, "E1446", {"start": v(29.11, -23.07) * mm, "end": v(29.2, -23.2) * mm});
            skLineSegment(sketch, "E1447", {"start": v(29.2, -23.2) * mm, "end": v(29.27, -23.32) * mm});
            skLineSegment(sketch, "E1448", {"start": v(29.27, -23.32) * mm, "end": v(29.31, -23.47) * mm});
            skLineSegment(sketch, "E1449", {"start": v(29.31, -23.47) * mm, "end": v(29.34, -23.61) * mm});
            skLineSegment(sketch, "E1450", {"start": v(29.34, -23.61) * mm, "end": v(29.34, -23.76) * mm});
            skLineSegment(sketch, "E1451", {"start": v(29.34, -23.76) * mm, "end": v(29.31, -23.91) * mm});
            skLineSegment(sketch, "E1452", {"start": v(29.31, -23.91) * mm, "end": v(29.27, -24.05) * mm});
            skLineSegment(sketch, "E1453", {"start": v(29.27, -24.05) * mm, "end": v(29.2, -24.19) * mm});
            skLineSegment(sketch, "E1454", {"start": v(29.2, -24.19) * mm, "end": v(29.11, -24.3) * mm});
            skLineSegment(sketch, "E1455", {"start": v(29.11, -24.3) * mm, "end": v(29, -24.41) * mm});
            skLineSegment(sketch, "E1456", {"start": v(29, -24.41) * mm, "end": v(28.89, -24.5) * mm});
            skLineSegment(sketch, "E1457", {"start": v(28.89, -24.5) * mm, "end": v(28.76, -24.57) * mm});
            skLineSegment(sketch, "E1458", {"start": v(28.76, -24.57) * mm, "end": v(28.61, -24.62) * mm});
            skLineSegment(sketch, "E1459", {"start": v(28.61, -24.62) * mm, "end": v(28.47, -24.64) * mm});
            skLineSegment(sketch, "E1460", {"start": v(28.47, -24.64) * mm, "end": v(28.32, -24.64) * mm});
            skLineSegment(sketch, "E1461", {"start": v(28.32, -24.64) * mm, "end": v(28.17, -24.62) * mm});
            skLineSegment(sketch, "E1462", {"start": v(28.17, -24.62) * mm, "end": v(28.03, -24.57) * mm});
            skLineSegment(sketch, "E1463", {"start": v(28.03, -24.57) * mm, "end": v(27.9, -24.5) * mm});
            skLineSegment(sketch, "E1464", {"start": v(27.9, -24.5) * mm, "end": v(27.77, -24.41) * mm});
            skLineSegment(sketch, "E1465", {"start": v(27.77, -24.41) * mm, "end": v(27.67, -24.3) * mm});
            skLineSegment(sketch, "E1466", {"start": v(27.67, -24.3) * mm, "end": v(27.58, -24.19) * mm});
            skLineSegment(sketch, "E1467", {"start": v(27.58, -24.19) * mm, "end": v(27.51, -24.05) * mm});
            skLineSegment(sketch, "E1468", {"start": v(27.51, -24.05) * mm, "end": v(27.47, -23.91) * mm});
            skLineSegment(sketch, "E1469", {"start": v(27.47, -23.91) * mm, "end": v(27.44, -23.76) * mm});
            skLineSegment(sketch, "E1470", {"start": v(27.44, -23.76) * mm, "end": v(27.44, -23.61) * mm});
            skLineSegment(sketch, "E1471", {"start": v(27.44, -23.61) * mm, "end": v(27.47, -23.47) * mm});
            skLineSegment(sketch, "E1472", {"start": v(27.47, -23.47) * mm, "end": v(27.51, -23.32) * mm});
            skLineSegment(sketch, "E1473", {"start": v(27.51, -23.32) * mm, "end": v(27.58, -23.2) * mm});
            skLineSegment(sketch, "E1474", {"start": v(27.58, -23.2) * mm, "end": v(27.6, -23.15) * mm});
            skLineSegment(sketch, "E1475", {"start": v(27.6, -23.15) * mm, "end": v(13.48, -9.03) * mm});
            skLineSegment(sketch, "E1476", {"start": v(13.48, -9.03) * mm, "end": v(13.35, -9.03) * mm});
            skLineSegment(sketch, "E1477", {"start": v(13.35, -9.03) * mm, "end": v(13.28, -9) * mm});
            skLineSegment(sketch, "E1478", {"start": v(13.28, -9) * mm, "end": v(12.78, -8.5) * mm});
            skLineSegment(sketch, "E1479", {"start": v(12.78, -8.5) * mm, "end": v(10.64, -6.36) * mm});
            skLineSegment(sketch, "E1480", {"start": v(10.64, -6.36) * mm, "end": v(8.45, -6.36) * mm});
            skLineSegment(sketch, "E1481", {"start": v(8.45, -6.36) * mm, "end": v(8.46, -6.66) * mm});
            skLineSegment(sketch, "E1482", {"start": v(8.46, -6.66) * mm, "end": v(7.5, -6.66) * mm});
            skLineSegment(sketch, "E1483", {"start": v(7.5, -6.66) * mm, "end": v(7.5, -5.7) * mm});
            skLineSegment(sketch, "E1484", {"start": v(7.5, -5.7) * mm, "end": v(7.63, -5.7) * mm});
            skLineSegment(sketch, "E1485", {"start": v(9.02, -23.76) * mm, "end": v(9, -23.91) * mm});
            skLineSegment(sketch, "E1486", {"start": v(9, -23.91) * mm, "end": v(8.95, -24.05) * mm});
            skLineSegment(sketch, "E1487", {"start": v(8.95, -24.05) * mm, "end": v(8.88, -24.19) * mm});
            skLineSegment(sketch, "E1488", {"start": v(8.88, -24.19) * mm, "end": v(8.8, -24.3) * mm});
            skLineSegment(sketch, "E1489", {"start": v(8.8, -24.3) * mm, "end": v(8.69, -24.41) * mm});
            skLineSegment(sketch, "E1490", {"start": v(8.69, -24.41) * mm, "end": v(8.57, -24.5) * mm});
            skLineSegment(sketch, "E1491", {"start": v(8.57, -24.5) * mm, "end": v(8.44, -24.57) * mm});
            skLineSegment(sketch, "E1492", {"start": v(8.44, -24.57) * mm, "end": v(8.3, -24.62) * mm});
            skLineSegment(sketch, "E1493", {"start": v(8.3, -24.62) * mm, "end": v(8.15, -24.64) * mm});
            skLineSegment(sketch, "E1494", {"start": v(8.15, -24.64) * mm, "end": v(8, -24.64) * mm});
            skLineSegment(sketch, "E1495", {"start": v(8, -24.64) * mm, "end": v(7.85, -24.62) * mm});
            skLineSegment(sketch, "E1496", {"start": v(7.85, -24.62) * mm, "end": v(7.7, -24.57) * mm});
            skLineSegment(sketch, "E1497", {"start": v(7.7, -24.57) * mm, "end": v(7.57, -24.5) * mm});
            skLineSegment(sketch, "E1498", {"start": v(7.57, -24.5) * mm, "end": v(7.45, -24.41) * mm});
            skLineSegment(sketch, "E1499", {"start": v(7.45, -24.41) * mm, "end": v(7.35, -24.3) * mm});
            skLineSegment(sketch, "E1500", {"start": v(7.35, -24.3) * mm, "end": v(7.26, -24.19) * mm});
            skLineSegment(sketch, "E1501", {"start": v(7.26, -24.19) * mm, "end": v(7.2, -24.05) * mm});
            skLineSegment(sketch, "E1502", {"start": v(7.2, -24.05) * mm, "end": v(7.15, -23.91) * mm});
            skLineSegment(sketch, "E1503", {"start": v(7.15, -23.91) * mm, "end": v(7.12, -23.76) * mm});
            skLineSegment(sketch, "E1504", {"start": v(7.12, -23.76) * mm, "end": v(7.12, -23.61) * mm});
            skLineSegment(sketch, "E1505", {"start": v(7.12, -23.61) * mm, "end": v(7.15, -23.47) * mm});
            skLineSegment(sketch, "E1506", {"start": v(7.15, -23.47) * mm, "end": v(7.2, -23.32) * mm});
            skLineSegment(sketch, "E1507", {"start": v(7.2, -23.32) * mm, "end": v(7.26, -23.2) * mm});
            skLineSegment(sketch, "E1508", {"start": v(7.26, -23.2) * mm, "end": v(7.28, -23.15) * mm});
            skLineSegment(sketch, "E1509", {"start": v(7.28, -23.15) * mm, "end": v(-7.89, -7.98) * mm});
            skLineSegment(sketch, "E1510", {"start": v(-7.89, -7.98) * mm, "end": v(-7.92, -7.92) * mm});
            skLineSegment(sketch, "E1511", {"start": v(-7.92, -7.92) * mm, "end": v(-7.92, -7.88) * mm});
            skLineSegment(sketch, "E1512", {"start": v(-7.92, -7.88) * mm, "end": v(-7.92, -3.8) * mm});
            skLineSegment(sketch, "E1513", {"start": v(-7.92, -3.8) * mm, "end": v(-11.89, 0.17) * mm});
            skLineSegment(sketch, "E1514", {"start": v(-11.89, 0.17) * mm, "end": v(-13.93, 0.17) * mm});
            skLineSegment(sketch, "E1515", {"start": v(-13.93, 0.17) * mm, "end": v(-13.99, 0.06) * mm});
            skLineSegment(sketch, "E1516", {"start": v(-13.99, 0.06) * mm, "end": v(-14.06, -0.02) * mm});
            skLineSegment(sketch, "E1517", {"start": v(-14.06, -0.02) * mm, "end": v(-14.16, -0.09) * mm});
            skLineSegment(sketch, "E1518", {"start": v(-14.16, -0.09) * mm, "end": v(-14.26, -0.13) * mm});
            skLineSegment(sketch, "E1519", {"start": v(-14.26, -0.13) * mm, "end": v(-14.38, -0.14) * mm});
            skLineSegment(sketch, "E1520", {"start": v(-14.38, -0.14) * mm, "end": v(-14.49, -0.13) * mm});
            skLineSegment(sketch, "E1521", {"start": v(-14.49, -0.13) * mm, "end": v(-14.6, -0.09) * mm});
            skLineSegment(sketch, "E1522", {"start": v(-14.6, -0.09) * mm, "end": v(-14.7, -0.02) * mm});
            skLineSegment(sketch, "E1523", {"start": v(-14.7, -0.02) * mm, "end": v(-14.77, 0.06) * mm});
            skLineSegment(sketch, "E1524", {"start": v(-14.77, 0.06) * mm, "end": v(-14.82, 0.16) * mm});
            skLineSegment(sketch, "E1525", {"start": v(-14.82, 0.16) * mm, "end": v(-14.85, 0.27) * mm});
            skLineSegment(sketch, "E1526", {"start": v(-14.85, 0.27) * mm, "end": v(-14.86, 0.38) * mm});
            skLineSegment(sketch, "E1527", {"start": v(-14.86, 0.38) * mm, "end": v(-14.84, 0.5) * mm});
            skLineSegment(sketch, "E1528", {"start": v(-14.84, 0.5) * mm, "end": v(-14.79, 0.6) * mm});
            skLineSegment(sketch, "E1529", {"start": v(-14.79, 0.6) * mm, "end": v(-14.72, 0.69) * mm});
            skLineSegment(sketch, "E1530", {"start": v(-14.72, 0.69) * mm, "end": v(-14.63, 0.75) * mm});
            skLineSegment(sketch, "E1531", {"start": v(-14.63, 0.75) * mm, "end": v(-14.53, 0.8) * mm});
            skLineSegment(sketch, "E1532", {"start": v(-14.53, 0.8) * mm, "end": v(-14.41, 0.83) * mm});
            skLineSegment(sketch, "E1533", {"start": v(-14.41, 0.83) * mm, "end": v(-14.3, 0.82) * mm});
            skLineSegment(sketch, "E1534", {"start": v(-14.3, 0.82) * mm, "end": v(-14.2, 0.79) * mm});
            skLineSegment(sketch, "E1535", {"start": v(-14.2, 0.79) * mm, "end": v(-14.1, 0.73) * mm});
            skLineSegment(sketch, "E1536", {"start": v(-14.1, 0.73) * mm, "end": v(-14.01, 0.66) * mm});
            skLineSegment(sketch, "E1537", {"start": v(-14.01, 0.66) * mm, "end": v(-13.95, 0.56) * mm});
            skLineSegment(sketch, "E1538", {"start": v(-13.95, 0.56) * mm, "end": v(-13.93, 0.52) * mm});
            skLineSegment(sketch, "E1539", {"start": v(-13.93, 0.52) * mm, "end": v(-11.79, 0.52) * mm});
            skLineSegment(sketch, "E1540", {"start": v(-11.79, 0.52) * mm, "end": v(-11.72, 0.5) * mm});
            skLineSegment(sketch, "E1541", {"start": v(-11.72, 0.5) * mm, "end": v(-11.69, 0.47) * mm});
            skLineSegment(sketch, "E1542", {"start": v(-11.69, 0.47) * mm, "end": v(-7.6, -3.63) * mm});
            skLineSegment(sketch, "E1543", {"start": v(-7.6, -3.63) * mm, "end": v(-7.57, -3.7) * mm});
            skLineSegment(sketch, "E1544", {"start": v(-7.57, -3.7) * mm, "end": v(-7.57, -4.4) * mm});
            skLineSegment(sketch, "E1545", {"start": v(-7.57, -4.4) * mm, "end": v(-7.57, -7.8) * mm});
            skLineSegment(sketch, "E1546", {"start": v(-7.57, -7.8) * mm, "end": v(7.53, -22.9) * mm});
            skLineSegment(sketch, "E1547", {"start": v(7.53, -22.9) * mm, "end": v(7.7, -22.81) * mm});
            skLineSegment(sketch, "E1548", {"start": v(7.7, -22.81) * mm, "end": v(7.85, -22.76) * mm});
            skLineSegment(sketch, "E1549", {"start": v(7.85, -22.76) * mm, "end": v(8, -22.74) * mm});
            skLineSegment(sketch, "E1550", {"start": v(8, -22.74) * mm, "end": v(8.15, -22.74) * mm});
            skLineSegment(sketch, "E1551", {"start": v(8.15, -22.74) * mm, "end": v(8.3, -22.76) * mm});
            skLineSegment(sketch, "E1552", {"start": v(8.3, -22.76) * mm, "end": v(8.44, -22.81) * mm});
            skLineSegment(sketch, "E1553", {"start": v(8.44, -22.81) * mm, "end": v(8.57, -22.88) * mm});
            skLineSegment(sketch, "E1554", {"start": v(8.57, -22.88) * mm, "end": v(8.69, -22.97) * mm});
            skLineSegment(sketch, "E1555", {"start": v(8.69, -22.97) * mm, "end": v(8.8, -23.07) * mm});
            skLineSegment(sketch, "E1556", {"start": v(8.8, -23.07) * mm, "end": v(8.88, -23.2) * mm});
            skLineSegment(sketch, "E1557", {"start": v(8.88, -23.2) * mm, "end": v(8.95, -23.32) * mm});
            skLineSegment(sketch, "E1558", {"start": v(8.95, -23.32) * mm, "end": v(9, -23.47) * mm});
            skLineSegment(sketch, "E1559", {"start": v(9, -23.47) * mm, "end": v(9.02, -23.61) * mm});
            skLineSegment(sketch, "E1560", {"start": v(9.02, -23.61) * mm, "end": v(9.02, -23.76) * mm});
            skLineSegment(sketch, "E1561", {"start": v(6.48, -23.76) * mm, "end": v(6.45, -23.91) * mm});
            skLineSegment(sketch, "E1562", {"start": v(6.45, -23.91) * mm, "end": v(6.4, -24.05) * mm});
            skLineSegment(sketch, "E1563", {"start": v(6.4, -24.05) * mm, "end": v(6.34, -24.19) * mm});
            skLineSegment(sketch, "E1564", {"start": v(6.34, -24.19) * mm, "end": v(6.25, -24.3) * mm});
            skLineSegment(sketch, "E1565", {"start": v(6.25, -24.3) * mm, "end": v(6.15, -24.41) * mm});
            skLineSegment(sketch, "E1566", {"start": v(6.15, -24.41) * mm, "end": v(6.03, -24.5) * mm});
            skLineSegment(sketch, "E1567", {"start": v(6.03, -24.5) * mm, "end": v(5.9, -24.57) * mm});
            skLineSegment(sketch, "E1568", {"start": v(5.9, -24.57) * mm, "end": v(5.75, -24.62) * mm});
            skLineSegment(sketch, "E1569", {"start": v(5.75, -24.62) * mm, "end": v(5.6, -24.64) * mm});
            skLineSegment(sketch, "E1570", {"start": v(5.6, -24.64) * mm, "end": v(5.46, -24.64) * mm});
            skLineSegment(sketch, "E1571", {"start": v(5.46, -24.64) * mm, "end": v(5.3, -24.62) * mm});
            skLineSegment(sketch, "E1572", {"start": v(5.3, -24.62) * mm, "end": v(5.17, -24.57) * mm});
            skLineSegment(sketch, "E1573", {"start": v(5.17, -24.57) * mm, "end": v(5.03, -24.5) * mm});
            skLineSegment(sketch, "E1574", {"start": v(5.03, -24.5) * mm, "end": v(4.91, -24.41) * mm});
            skLineSegment(sketch, "E1575", {"start": v(4.91, -24.41) * mm, "end": v(4.8, -24.3) * mm});
            skLineSegment(sketch, "E1576", {"start": v(4.8, -24.3) * mm, "end": v(4.72, -24.19) * mm});
            skLineSegment(sketch, "E1577", {"start": v(4.72, -24.19) * mm, "end": v(4.65, -24.05) * mm});
            skLineSegment(sketch, "E1578", {"start": v(4.65, -24.05) * mm, "end": v(4.6, -23.91) * mm});
            skLineSegment(sketch, "E1579", {"start": v(4.6, -23.91) * mm, "end": v(4.58, -23.76) * mm});
            skLineSegment(sketch, "E1580", {"start": v(4.58, -23.76) * mm, "end": v(4.58, -23.61) * mm});
            skLineSegment(sketch, "E1581", {"start": v(4.58, -23.61) * mm, "end": v(4.6, -23.47) * mm});
            skLineSegment(sketch, "E1582", {"start": v(4.6, -23.47) * mm, "end": v(4.65, -23.32) * mm});
            skLineSegment(sketch, "E1583", {"start": v(4.65, -23.32) * mm, "end": v(4.72, -23.2) * mm});
            skLineSegment(sketch, "E1584", {"start": v(4.72, -23.2) * mm, "end": v(4.74, -23.15) * mm});
            skLineSegment(sketch, "E1585", {"start": v(4.74, -23.15) * mm, "end": v(-8.94, -9.47) * mm});
            skLineSegment(sketch, "E1586", {"start": v(-8.94, -9.47) * mm, "end": v(-8.97, -9.4) * mm});
            skLineSegment(sketch, "E1587", {"start": v(-8.97, -9.4) * mm, "end": v(-8.97, -9.37) * mm});
            skLineSegment(sketch, "E1588", {"start": v(-8.97, -9.37) * mm, "end": v(-8.97, -4.22) * mm});
            skLineSegment(sketch, "E1589", {"start": v(-8.97, -4.22) * mm, "end": v(-12.32, -0.87) * mm});
            skLineSegment(sketch, "E1590", {"start": v(-12.32, -0.87) * mm, "end": v(-13.9, -0.87) * mm});
            skLineSegment(sketch, "E1591", {"start": v(-13.9, -0.87) * mm, "end": v(-13.9, -1) * mm});
            skLineSegment(sketch, "E1592", {"start": v(-13.9, -1) * mm, "end": v(-13.93, -1.11) * mm});
            skLineSegment(sketch, "E1593", {"start": v(-13.93, -1.11) * mm, "end": v(-13.99, -1.21) * mm});
            skLineSegment(sketch, "E1594", {"start": v(-13.99, -1.21) * mm, "end": v(-14.06, -1.3) * mm});
            skLineSegment(sketch, "E1595", {"start": v(-14.06, -1.3) * mm, "end": v(-14.16, -1.36) * mm});
            skLineSegment(sketch, "E1596", {"start": v(-14.16, -1.36) * mm, "end": v(-14.26, -1.4) * mm});
            skLineSegment(sketch, "E1597", {"start": v(-14.26, -1.4) * mm, "end": v(-14.38, -1.4) * mm});
            skLineSegment(sketch, "E1598", {"start": v(-14.38, -1.4) * mm, "end": v(-14.49, -1.4) * mm});
            skLineSegment(sketch, "E1599", {"start": v(-14.49, -1.4) * mm, "end": v(-14.6, -1.36) * mm});
            skLineSegment(sketch, "E1600", {"start": v(-14.6, -1.36) * mm, "end": v(-14.7, -1.3) * mm});
            skLineSegment(sketch, "E1601", {"start": v(-14.7, -1.3) * mm, "end": v(-14.77, -1.21) * mm});
            skLineSegment(sketch, "E1602", {"start": v(-14.77, -1.21) * mm, "end": v(-14.82, -1.11) * mm});
            skLineSegment(sketch, "E1603", {"start": v(-14.82, -1.11) * mm, "end": v(-14.85, -1) * mm});
            skLineSegment(sketch, "E1604", {"start": v(-14.85, -1) * mm, "end": v(-14.86, -0.89) * mm});
            skLineSegment(sketch, "E1605", {"start": v(-14.86, -0.89) * mm, "end": v(-14.84, -0.78) * mm});
            skLineSegment(sketch, "E1606", {"start": v(-14.84, -0.78) * mm, "end": v(-14.79, -0.68) * mm});
            skLineSegment(sketch, "E1607", {"start": v(-14.79, -0.68) * mm, "end": v(-14.72, -0.58) * mm});
            skLineSegment(sketch, "E1608", {"start": v(-14.72, -0.58) * mm, "end": v(-14.63, -0.52) * mm});
            skLineSegment(sketch, "E1609", {"start": v(-14.63, -0.52) * mm, "end": v(-14.53, -0.47) * mm});
            skLineSegment(sketch, "E1610", {"start": v(-14.53, -0.47) * mm, "end": v(-14.41, -0.44) * mm});
            skLineSegment(sketch, "E1611", {"start": v(-14.41, -0.44) * mm, "end": v(-14.3, -0.45) * mm});
            skLineSegment(sketch, "E1612", {"start": v(-14.3, -0.45) * mm, "end": v(-14.2, -0.48) * mm});
            skLineSegment(sketch, "E1613", {"start": v(-14.2, -0.48) * mm, "end": v(-14.09, -0.54) * mm});
            skLineSegment(sketch, "E1614", {"start": v(-14.09, -0.54) * mm, "end": v(-14.02, -0.52) * mm});
            skLineSegment(sketch, "E1615", {"start": v(-14.02, -0.52) * mm, "end": v(-12.21, -0.52) * mm});
            skLineSegment(sketch, "E1616", {"start": v(-12.21, -0.52) * mm, "end": v(-12.15, -0.55) * mm});
            skLineSegment(sketch, "E1617", {"start": v(-12.15, -0.55) * mm, "end": v(-12.11, -0.57) * mm});
            skLineSegment(sketch, "E1618", {"start": v(-12.11, -0.57) * mm, "end": v(-8.64, -4.05) * mm});
            skLineSegment(sketch, "E1619", {"start": v(-8.64, -4.05) * mm, "end": v(-8.62, -4.11) * mm});
            skLineSegment(sketch, "E1620", {"start": v(-8.62, -4.11) * mm, "end": v(-8.62, -4.82) * mm});
            skLineSegment(sketch, "E1621", {"start": v(-8.62, -4.82) * mm, "end": v(-8.62, -9.3) * mm});
            skLineSegment(sketch, "E1622", {"start": v(-8.62, -9.3) * mm, "end": v(5, -22.9) * mm});
            skLineSegment(sketch, "E1623", {"start": v(5, -22.9) * mm, "end": v(5.1, -22.84) * mm});
            skLineSegment(sketch, "E1624", {"start": v(5.1, -22.84) * mm, "end": v(5.23, -22.78) * mm});
            skLineSegment(sketch, "E1625", {"start": v(5.23, -22.78) * mm, "end": v(5.38, -22.75) * mm});
            skLineSegment(sketch, "E1626", {"start": v(5.38, -22.75) * mm, "end": v(5.53, -22.74) * mm});
            skLineSegment(sketch, "E1627", {"start": v(5.53, -22.74) * mm, "end": v(5.68, -22.75) * mm});
            skLineSegment(sketch, "E1628", {"start": v(5.68, -22.75) * mm, "end": v(5.82, -22.78) * mm});
            skLineSegment(sketch, "E1629", {"start": v(5.82, -22.78) * mm, "end": v(5.96, -22.84) * mm});
            skLineSegment(sketch, "E1630", {"start": v(5.96, -22.84) * mm, "end": v(6.09, -22.92) * mm});
            skLineSegment(sketch, "E1631", {"start": v(6.09, -22.92) * mm, "end": v(6.2, -23.02) * mm});
            skLineSegment(sketch, "E1632", {"start": v(6.2, -23.02) * mm, "end": v(6.3, -23.13) * mm});
            skLineSegment(sketch, "E1633", {"start": v(6.3, -23.13) * mm, "end": v(6.38, -23.26) * mm});
            skLineSegment(sketch, "E1634", {"start": v(6.38, -23.26) * mm, "end": v(6.43, -23.4) * mm});
            skLineSegment(sketch, "E1635", {"start": v(6.43, -23.4) * mm, "end": v(6.47, -23.54) * mm});
            skLineSegment(sketch, "E1636", {"start": v(6.47, -23.54) * mm, "end": v(6.48, -23.7) * mm});
            skLineSegment(sketch, "E1637", {"start": v(6.48, -23.7) * mm, "end": v(6.48, -23.76) * mm});
            skLineSegment(sketch, "E1638", {"start": v(3.94, -23.76) * mm, "end": v(3.91, -23.91) * mm});
            skLineSegment(sketch, "E1639", {"start": v(3.91, -23.91) * mm, "end": v(3.87, -24.05) * mm});
            skLineSegment(sketch, "E1640", {"start": v(3.87, -24.05) * mm, "end": v(3.8, -24.19) * mm});
            skLineSegment(sketch, "E1641", {"start": v(3.8, -24.19) * mm, "end": v(3.71, -24.3) * mm});
            skLineSegment(sketch, "E1642", {"start": v(3.71, -24.3) * mm, "end": v(3.6, -24.41) * mm});
            skLineSegment(sketch, "E1643", {"start": v(3.6, -24.41) * mm, "end": v(3.49, -24.5) * mm});
            skLineSegment(sketch, "E1644", {"start": v(3.49, -24.5) * mm, "end": v(3.36, -24.57) * mm});
            skLineSegment(sketch, "E1645", {"start": v(3.36, -24.57) * mm, "end": v(3.21, -24.62) * mm});
            skLineSegment(sketch, "E1646", {"start": v(3.21, -24.62) * mm, "end": v(3.07, -24.64) * mm});
            skLineSegment(sketch, "E1647", {"start": v(3.07, -24.64) * mm, "end": v(2.92, -24.64) * mm});
            skLineSegment(sketch, "E1648", {"start": v(2.92, -24.64) * mm, "end": v(2.77, -24.62) * mm});
            skLineSegment(sketch, "E1649", {"start": v(2.77, -24.62) * mm, "end": v(2.63, -24.57) * mm});
            skLineSegment(sketch, "E1650", {"start": v(2.63, -24.57) * mm, "end": v(2.5, -24.5) * mm});
            skLineSegment(sketch, "E1651", {"start": v(2.5, -24.5) * mm, "end": v(2.37, -24.41) * mm});
            skLineSegment(sketch, "E1652", {"start": v(2.37, -24.41) * mm, "end": v(2.27, -24.3) * mm});
            skLineSegment(sketch, "E1653", {"start": v(2.27, -24.3) * mm, "end": v(2.18, -24.19) * mm});
            skLineSegment(sketch, "E1654", {"start": v(2.18, -24.19) * mm, "end": v(2.11, -24.05) * mm});
            skLineSegment(sketch, "E1655", {"start": v(2.11, -24.05) * mm, "end": v(2.07, -23.91) * mm});
            skLineSegment(sketch, "E1656", {"start": v(2.07, -23.91) * mm, "end": v(2.04, -23.76) * mm});
            skLineSegment(sketch, "E1657", {"start": v(2.04, -23.76) * mm, "end": v(2.04, -23.61) * mm});
            skLineSegment(sketch, "E1658", {"start": v(2.04, -23.61) * mm, "end": v(2.07, -23.47) * mm});
            skLineSegment(sketch, "E1659", {"start": v(2.07, -23.47) * mm, "end": v(2.11, -23.32) * mm});
            skLineSegment(sketch, "E1660", {"start": v(2.11, -23.32) * mm, "end": v(2.18, -23.2) * mm});
            skLineSegment(sketch, "E1661", {"start": v(2.18, -23.2) * mm, "end": v(2.2, -23.15) * mm});
            skLineSegment(sketch, "E1662", {"start": v(2.2, -23.15) * mm, "end": v(-10.56, -10.4) * mm});
            skLineSegment(sketch, "E1663", {"start": v(-10.56, -10.4) * mm, "end": v(-10.59, -10.33) * mm});
            skLineSegment(sketch, "E1664", {"start": v(-10.59, -10.33) * mm, "end": v(-10.6, -10.29) * mm});
            skLineSegment(sketch, "E1665", {"start": v(-10.6, -10.29) * mm, "end": v(-10.6, -4.04) * mm});
            skLineSegment(sketch, "E1666", {"start": v(-10.6, -4.04) * mm, "end": v(-12.26, -2.37) * mm});
            skLineSegment(sketch, "E1667", {"start": v(-12.26, -2.37) * mm, "end": v(-13.93, -2.37) * mm});
            skLineSegment(sketch, "E1668", {"start": v(-13.93, -2.37) * mm, "end": v(-13.99, -2.48) * mm});
            skLineSegment(sketch, "E1669", {"start": v(-13.99, -2.48) * mm, "end": v(-14.06, -2.56) * mm});
            skLineSegment(sketch, "E1670", {"start": v(-14.06, -2.56) * mm, "end": v(-14.16, -2.63) * mm});
            skLineSegment(sketch, "E1671", {"start": v(-14.16, -2.63) * mm, "end": v(-14.26, -2.67) * mm});
            skLineSegment(sketch, "E1672", {"start": v(-14.26, -2.67) * mm, "end": v(-14.38, -2.68) * mm});
            skLineSegment(sketch, "E1673", {"start": v(-14.38, -2.68) * mm, "end": v(-14.49, -2.67) * mm});
            skLineSegment(sketch, "E1674", {"start": v(-14.49, -2.67) * mm, "end": v(-14.6, -2.63) * mm});
            skLineSegment(sketch, "E1675", {"start": v(-14.6, -2.63) * mm, "end": v(-14.7, -2.56) * mm});
            skLineSegment(sketch, "E1676", {"start": v(-14.7, -2.56) * mm, "end": v(-14.77, -2.48) * mm});
            skLineSegment(sketch, "E1677", {"start": v(-14.77, -2.48) * mm, "end": v(-14.82, -2.38) * mm});
            skLineSegment(sketch, "E1678", {"start": v(-14.82, -2.38) * mm, "end": v(-14.85, -2.27) * mm});
            skLineSegment(sketch, "E1679", {"start": v(-14.85, -2.27) * mm, "end": v(-14.86, -2.16) * mm});
            skLineSegment(sketch, "E1680", {"start": v(-14.86, -2.16) * mm, "end": v(-14.84, -2.05) * mm});
            skLineSegment(sketch, "E1681", {"start": v(-14.84, -2.05) * mm, "end": v(-14.79, -1.95) * mm});
            skLineSegment(sketch, "E1682", {"start": v(-14.79, -1.95) * mm, "end": v(-14.72, -1.85) * mm});
            skLineSegment(sketch, "E1683", {"start": v(-14.72, -1.85) * mm, "end": v(-14.63, -1.79) * mm});
            skLineSegment(sketch, "E1684", {"start": v(-14.63, -1.79) * mm, "end": v(-14.53, -1.74) * mm});
            skLineSegment(sketch, "E1685", {"start": v(-14.53, -1.74) * mm, "end": v(-14.41, -1.71) * mm});
            skLineSegment(sketch, "E1686", {"start": v(-14.41, -1.71) * mm, "end": v(-14.3, -1.72) * mm});
            skLineSegment(sketch, "E1687", {"start": v(-14.3, -1.72) * mm, "end": v(-14.2, -1.75) * mm});
            skLineSegment(sketch, "E1688", {"start": v(-14.2, -1.75) * mm, "end": v(-14.1, -1.8) * mm});
            skLineSegment(sketch, "E1689", {"start": v(-14.1, -1.8) * mm, "end": v(-14.01, -1.88) * mm});
            skLineSegment(sketch, "E1690", {"start": v(-14.01, -1.88) * mm, "end": v(-13.95, -1.98) * mm});
            skLineSegment(sketch, "E1691", {"start": v(-13.95, -1.98) * mm, "end": v(-13.93, -2.02) * mm});
            skLineSegment(sketch, "E1692", {"start": v(-13.93, -2.02) * mm, "end": v(-12.15, -2.02) * mm});
            skLineSegment(sketch, "E1693", {"start": v(-12.15, -2.02) * mm, "end": v(-12.09, -2.04) * mm});
            skLineSegment(sketch, "E1694", {"start": v(-12.09, -2.04) * mm, "end": v(-12.05, -2.07) * mm});
            skLineSegment(sketch, "E1695", {"start": v(-12.05, -2.07) * mm, "end": v(-10.26, -3.87) * mm});
            skLineSegment(sketch, "E1696", {"start": v(-10.26, -3.87) * mm, "end": v(-10.24, -3.93) * mm});
            skLineSegment(sketch, "E1697", {"start": v(-10.24, -3.93) * mm, "end": v(-10.24, -4.64) * mm});
            skLineSegment(sketch, "E1698", {"start": v(-10.24, -4.64) * mm, "end": v(-10.24, -10.22) * mm});
            skLineSegment(sketch, "E1699", {"start": v(-10.24, -10.22) * mm, "end": v(2.46, -22.9) * mm});
            skLineSegment(sketch, "E1700", {"start": v(2.46, -22.9) * mm, "end": v(2.56, -22.84) * mm});
            skLineSegment(sketch, "E1701", {"start": v(2.56, -22.84) * mm, "end": v(2.7, -22.78) * mm});
            skLineSegment(sketch, "E1702", {"start": v(2.7, -22.78) * mm, "end": v(2.84, -22.75) * mm});
            skLineSegment(sketch, "E1703", {"start": v(2.84, -22.75) * mm, "end": v(2.99, -22.74) * mm});
            skLineSegment(sketch, "E1704", {"start": v(2.99, -22.74) * mm, "end": v(3.14, -22.75) * mm});
            skLineSegment(sketch, "E1705", {"start": v(3.14, -22.75) * mm, "end": v(3.28, -22.78) * mm});
            skLineSegment(sketch, "E1706", {"start": v(3.28, -22.78) * mm, "end": v(3.42, -22.84) * mm});
            skLineSegment(sketch, "E1707", {"start": v(3.42, -22.84) * mm, "end": v(3.55, -22.92) * mm});
            skLineSegment(sketch, "E1708", {"start": v(3.55, -22.92) * mm, "end": v(3.66, -23.02) * mm});
            skLineSegment(sketch, "E1709", {"start": v(3.66, -23.02) * mm, "end": v(3.76, -23.13) * mm});
            skLineSegment(sketch, "E1710", {"start": v(3.76, -23.13) * mm, "end": v(3.84, -23.26) * mm});
            skLineSegment(sketch, "E1711", {"start": v(3.84, -23.26) * mm, "end": v(3.9, -23.4) * mm});
            skLineSegment(sketch, "E1712", {"start": v(3.9, -23.4) * mm, "end": v(3.93, -23.54) * mm});
            skLineSegment(sketch, "E1713", {"start": v(3.93, -23.54) * mm, "end": v(3.94, -23.7) * mm});
            skLineSegment(sketch, "E1714", {"start": v(3.94, -23.7) * mm, "end": v(3.94, -23.76) * mm});
            skLineSegment(sketch, "E1715", {"start": v(-3.68, -23.76) * mm, "end": v(-3.7, -23.91) * mm});
            skLineSegment(sketch, "E1716", {"start": v(-3.7, -23.91) * mm, "end": v(-3.75, -24.05) * mm});
            skLineSegment(sketch, "E1717", {"start": v(-3.75, -24.05) * mm, "end": v(-3.82, -24.19) * mm});
            skLineSegment(sketch, "E1718", {"start": v(-3.82, -24.19) * mm, "end": v(-3.9, -24.3) * mm});
            skLineSegment(sketch, "E1719", {"start": v(-3.9, -24.3) * mm, "end": v(-4.01, -24.41) * mm});
            skLineSegment(sketch, "E1720", {"start": v(-4.01, -24.41) * mm, "end": v(-4.13, -24.5) * mm});
            skLineSegment(sketch, "E1721", {"start": v(-4.13, -24.5) * mm, "end": v(-4.26, -24.57) * mm});
            skLineSegment(sketch, "E1722", {"start": v(-4.26, -24.57) * mm, "end": v(-4.4, -24.62) * mm});
            skLineSegment(sketch, "E1723", {"start": v(-4.4, -24.62) * mm, "end": v(-4.55, -24.64) * mm});
            skLineSegment(sketch, "E1724", {"start": v(-4.55, -24.64) * mm, "end": v(-4.7, -24.64) * mm});
            skLineSegment(sketch, "E1725", {"start": v(-4.7, -24.64) * mm, "end": v(-4.85, -24.62) * mm});
            skLineSegment(sketch, "E1726", {"start": v(-4.85, -24.62) * mm, "end": v(-5, -24.57) * mm});
            skLineSegment(sketch, "E1727", {"start": v(-5, -24.57) * mm, "end": v(-5.13, -24.5) * mm});
            skLineSegment(sketch, "E1728", {"start": v(-5.13, -24.5) * mm, "end": v(-5.25, -24.41) * mm});
            skLineSegment(sketch, "E1729", {"start": v(-5.25, -24.41) * mm, "end": v(-5.35, -24.3) * mm});
            skLineSegment(sketch, "E1730", {"start": v(-5.35, -24.3) * mm, "end": v(-5.44, -24.19) * mm});
            skLineSegment(sketch, "E1731", {"start": v(-5.44, -24.19) * mm, "end": v(-5.5, -24.05) * mm});
            skLineSegment(sketch, "E1732", {"start": v(-5.5, -24.05) * mm, "end": v(-5.55, -23.91) * mm});
            skLineSegment(sketch, "E1733", {"start": v(-5.55, -23.91) * mm, "end": v(-5.58, -23.76) * mm});
            skLineSegment(sketch, "E1734", {"start": v(-5.58, -23.76) * mm, "end": v(-5.58, -23.61) * mm});
            skLineSegment(sketch, "E1735", {"start": v(-5.58, -23.61) * mm, "end": v(-5.55, -23.47) * mm});
            skLineSegment(sketch, "E1736", {"start": v(-5.55, -23.47) * mm, "end": v(-5.5, -23.32) * mm});
            skLineSegment(sketch, "E1737", {"start": v(-5.5, -23.32) * mm, "end": v(-5.44, -23.2) * mm});
            skLineSegment(sketch, "E1738", {"start": v(-5.44, -23.2) * mm, "end": v(-5.35, -23.07) * mm});
            skLineSegment(sketch, "E1739", {"start": v(-5.35, -23.07) * mm, "end": v(-5.25, -22.97) * mm});
            skLineSegment(sketch, "E1740", {"start": v(-5.25, -22.97) * mm, "end": v(-5.13, -22.88) * mm});
            skLineSegment(sketch, "E1741", {"start": v(-5.13, -22.88) * mm, "end": v(-5, -22.81) * mm});
            skLineSegment(sketch, "E1742", {"start": v(-5, -22.81) * mm, "end": v(-4.85, -22.76) * mm});
            skLineSegment(sketch, "E1743", {"start": v(-4.85, -22.76) * mm, "end": v(-4.7, -22.74) * mm});
            skLineSegment(sketch, "E1744", {"start": v(-4.7, -22.74) * mm, "end": v(-4.55, -22.74) * mm});
            skLineSegment(sketch, "E1745", {"start": v(-4.55, -22.74) * mm, "end": v(-4.4, -22.76) * mm});
            skLineSegment(sketch, "E1746", {"start": v(-4.4, -22.76) * mm, "end": v(-4.26, -22.81) * mm});
            skLineSegment(sketch, "E1747", {"start": v(-4.26, -22.81) * mm, "end": v(-4.13, -22.88) * mm});
            skLineSegment(sketch, "E1748", {"start": v(-4.13, -22.88) * mm, "end": v(-4.01, -22.97) * mm});
            skLineSegment(sketch, "E1749", {"start": v(-4.01, -22.97) * mm, "end": v(-3.9, -23.07) * mm});
            skLineSegment(sketch, "E1750", {"start": v(-3.9, -23.07) * mm, "end": v(-3.82, -23.2) * mm});
            skLineSegment(sketch, "E1751", {"start": v(-3.82, -23.2) * mm, "end": v(-3.75, -23.32) * mm});
            skLineSegment(sketch, "E1752", {"start": v(-3.75, -23.32) * mm, "end": v(-3.7, -23.47) * mm});
            skLineSegment(sketch, "E1753", {"start": v(-3.7, -23.47) * mm, "end": v(-3.68, -23.61) * mm});
            skLineSegment(sketch, "E1754", {"start": v(-3.68, -23.61) * mm, "end": v(-3.68, -23.76) * mm});
            skLineSegment(sketch, "E1755", {"start": v(-6.22, -23.76) * mm, "end": v(-6.25, -23.91) * mm});
            skLineSegment(sketch, "E1756", {"start": v(-6.25, -23.91) * mm, "end": v(-6.3, -24.05) * mm});
            skLineSegment(sketch, "E1757", {"start": v(-6.3, -24.05) * mm, "end": v(-6.36, -24.19) * mm});
            skLineSegment(sketch, "E1758", {"start": v(-6.36, -24.19) * mm, "end": v(-6.45, -24.3) * mm});
            skLineSegment(sketch, "E1759", {"start": v(-6.45, -24.3) * mm, "end": v(-6.55, -24.41) * mm});
            skLineSegment(sketch, "E1760", {"start": v(-6.55, -24.41) * mm, "end": v(-6.67, -24.5) * mm});
            skLineSegment(sketch, "E1761", {"start": v(-6.67, -24.5) * mm, "end": v(-6.8, -24.57) * mm});
            skLineSegment(sketch, "E1762", {"start": v(-6.8, -24.57) * mm, "end": v(-6.95, -24.62) * mm});
            skLineSegment(sketch, "E1763", {"start": v(-6.95, -24.62) * mm, "end": v(-7.1, -24.64) * mm});
            skLineSegment(sketch, "E1764", {"start": v(-7.1, -24.64) * mm, "end": v(-7.24, -24.64) * mm});
            skLineSegment(sketch, "E1765", {"start": v(-7.24, -24.64) * mm, "end": v(-7.4, -24.62) * mm});
            skLineSegment(sketch, "E1766", {"start": v(-7.4, -24.62) * mm, "end": v(-7.53, -24.57) * mm});
            skLineSegment(sketch, "E1767", {"start": v(-7.53, -24.57) * mm, "end": v(-7.67, -24.5) * mm});
            skLineSegment(sketch, "E1768", {"start": v(-7.67, -24.5) * mm, "end": v(-7.79, -24.41) * mm});
            skLineSegment(sketch, "E1769", {"start": v(-7.79, -24.41) * mm, "end": v(-7.9, -24.3) * mm});
            skLineSegment(sketch, "E1770", {"start": v(-7.9, -24.3) * mm, "end": v(-7.98, -24.19) * mm});
            skLineSegment(sketch, "E1771", {"start": v(-7.98, -24.19) * mm, "end": v(-8.05, -24.05) * mm});
            skLineSegment(sketch, "E1772", {"start": v(-8.05, -24.05) * mm, "end": v(-8.1, -23.91) * mm});
            skLineSegment(sketch, "E1773", {"start": v(-8.1, -23.91) * mm, "end": v(-8.12, -23.76) * mm});
            skLineSegment(sketch, "E1774", {"start": v(-8.12, -23.76) * mm, "end": v(-8.12, -23.61) * mm});
            skLineSegment(sketch, "E1775", {"start": v(-8.12, -23.61) * mm, "end": v(-8.1, -23.47) * mm});
            skLineSegment(sketch, "E1776", {"start": v(-8.1, -23.47) * mm, "end": v(-8.05, -23.32) * mm});
            skLineSegment(sketch, "E1777", {"start": v(-8.05, -23.32) * mm, "end": v(-7.98, -23.2) * mm});
            skLineSegment(sketch, "E1778", {"start": v(-7.98, -23.2) * mm, "end": v(-7.9, -23.07) * mm});
            skLineSegment(sketch, "E1779", {"start": v(-7.9, -23.07) * mm, "end": v(-7.79, -22.97) * mm});
            skLineSegment(sketch, "E1780", {"start": v(-7.79, -22.97) * mm, "end": v(-7.67, -22.88) * mm});
            skLineSegment(sketch, "E1781", {"start": v(-7.67, -22.88) * mm, "end": v(-7.53, -22.81) * mm});
            skLineSegment(sketch, "E1782", {"start": v(-7.53, -22.81) * mm, "end": v(-7.4, -22.76) * mm});
            skLineSegment(sketch, "E1783", {"start": v(-7.4, -22.76) * mm, "end": v(-7.24, -22.74) * mm});
            skLineSegment(sketch, "E1784", {"start": v(-7.24, -22.74) * mm, "end": v(-7.1, -22.74) * mm});
            skLineSegment(sketch, "E1785", {"start": v(-7.1, -22.74) * mm, "end": v(-6.95, -22.76) * mm});
            skLineSegment(sketch, "E1786", {"start": v(-6.95, -22.76) * mm, "end": v(-6.8, -22.81) * mm});
            skLineSegment(sketch, "E1787", {"start": v(-6.8, -22.81) * mm, "end": v(-6.67, -22.88) * mm});
            skLineSegment(sketch, "E1788", {"start": v(-6.67, -22.88) * mm, "end": v(-6.55, -22.97) * mm});
            skLineSegment(sketch, "E1789", {"start": v(-6.55, -22.97) * mm, "end": v(-6.45, -23.07) * mm});
            skLineSegment(sketch, "E1790", {"start": v(-6.45, -23.07) * mm, "end": v(-6.36, -23.2) * mm});
            skLineSegment(sketch, "E1791", {"start": v(-6.36, -23.2) * mm, "end": v(-6.3, -23.32) * mm});
            skLineSegment(sketch, "E1792", {"start": v(-6.3, -23.32) * mm, "end": v(-6.25, -23.47) * mm});
            skLineSegment(sketch, "E1793", {"start": v(-6.25, -23.47) * mm, "end": v(-6.22, -23.61) * mm});
            skLineSegment(sketch, "E1794", {"start": v(-6.22, -23.61) * mm, "end": v(-6.22, -23.76) * mm});
            skLineSegment(sketch, "E1795", {"start": v(-8.76, -23.76) * mm, "end": v(-8.79, -23.91) * mm});
            skLineSegment(sketch, "E1796", {"start": v(-8.79, -23.91) * mm, "end": v(-8.83, -24.05) * mm});
            skLineSegment(sketch, "E1797", {"start": v(-8.83, -24.05) * mm, "end": v(-8.9, -24.19) * mm});
            skLineSegment(sketch, "E1798", {"start": v(-8.9, -24.19) * mm, "end": v(-8.99, -24.3) * mm});
            skLineSegment(sketch, "E1799", {"start": v(-8.99, -24.3) * mm, "end": v(-9.1, -24.41) * mm});
            skLineSegment(sketch, "E1800", {"start": v(-9.1, -24.41) * mm, "end": v(-9.21, -24.5) * mm});
            skLineSegment(sketch, "E1801", {"start": v(-9.21, -24.5) * mm, "end": v(-9.34, -24.57) * mm});
            skLineSegment(sketch, "E1802", {"start": v(-9.34, -24.57) * mm, "end": v(-9.49, -24.62) * mm});
            skLineSegment(sketch, "E1803", {"start": v(-9.49, -24.62) * mm, "end": v(-9.63, -24.64) * mm});
            skLineSegment(sketch, "E1804", {"start": v(-9.63, -24.64) * mm, "end": v(-9.78, -24.64) * mm});
            skLineSegment(sketch, "E1805", {"start": v(-9.78, -24.64) * mm, "end": v(-9.93, -24.62) * mm});
            skLineSegment(sketch, "E1806", {"start": v(-9.93, -24.62) * mm, "end": v(-10.07, -24.57) * mm});
            skLineSegment(sketch, "E1807", {"start": v(-10.07, -24.57) * mm, "end": v(-10.2, -24.5) * mm});
            skLineSegment(sketch, "E1808", {"start": v(-10.2, -24.5) * mm, "end": v(-10.33, -24.41) * mm});
            skLineSegment(sketch, "E1809", {"start": v(-10.33, -24.41) * mm, "end": v(-10.43, -24.3) * mm});
            skLineSegment(sketch, "E1810", {"start": v(-10.43, -24.3) * mm, "end": v(-10.52, -24.19) * mm});
            skLineSegment(sketch, "E1811", {"start": v(-10.52, -24.19) * mm, "end": v(-10.59, -24.05) * mm});
            skLineSegment(sketch, "E1812", {"start": v(-10.59, -24.05) * mm, "end": v(-10.63, -23.91) * mm});
            skLineSegment(sketch, "E1813", {"start": v(-10.63, -23.91) * mm, "end": v(-10.66, -23.76) * mm});
            skLineSegment(sketch, "E1814", {"start": v(-10.66, -23.76) * mm, "end": v(-10.66, -23.61) * mm});
            skLineSegment(sketch, "E1815", {"start": v(-10.66, -23.61) * mm, "end": v(-10.63, -23.47) * mm});
            skLineSegment(sketch, "E1816", {"start": v(-10.63, -23.47) * mm, "end": v(-10.59, -23.32) * mm});
            skLineSegment(sketch, "E1817", {"start": v(-10.59, -23.32) * mm, "end": v(-10.52, -23.2) * mm});
            skLineSegment(sketch, "E1818", {"start": v(-10.52, -23.2) * mm, "end": v(-10.5, -23.15) * mm});
            skLineSegment(sketch, "E1819", {"start": v(-10.5, -23.15) * mm, "end": v(-20.86, -12.79) * mm});
            skLineSegment(sketch, "E1820", {"start": v(-20.86, -12.79) * mm, "end": v(-20.89, -12.73) * mm});
            skLineSegment(sketch, "E1821", {"start": v(-20.89, -12.73) * mm, "end": v(-20.9, -12.68) * mm});
            skLineSegment(sketch, "E1822", {"start": v(-20.9, -12.68) * mm, "end": v(-20.89, -3.76) * mm});
            skLineSegment(sketch, "E1823", {"start": v(-20.89, -3.76) * mm, "end": v(-20.86, -3.7) * mm});
            skLineSegment(sketch, "E1824", {"start": v(-20.86, -3.7) * mm, "end": v(-20.36, -3.2) * mm});
            skLineSegment(sketch, "E1825", {"start": v(-20.36, -3.2) * mm, "end": v(-17.93, -0.77) * mm});
            skLineSegment(sketch, "E1826", {"start": v(-17.93, -0.77) * mm, "end": v(-17.87, -0.75) * mm});
            skLineSegment(sketch, "E1827", {"start": v(-17.87, -0.75) * mm, "end": v(-17.16, -0.75) * mm});
            skLineSegment(sketch, "E1828", {"start": v(-17.16, -0.75) * mm, "end": v(-16.1, -0.75) * mm});
            skLineSegment(sketch, "E1829", {"start": v(-16.1, -0.75) * mm, "end": v(-16.06, -0.68) * mm});
            skLineSegment(sketch, "E1830", {"start": v(-16.06, -0.68) * mm, "end": v(-15.99, -0.58) * mm});
            skLineSegment(sketch, "E1831", {"start": v(-15.99, -0.58) * mm, "end": v(-15.9, -0.52) * mm});
            skLineSegment(sketch, "E1832", {"start": v(-15.9, -0.52) * mm, "end": v(-15.8, -0.47) * mm});
            skLineSegment(sketch, "E1833", {"start": v(-15.8, -0.47) * mm, "end": v(-15.68, -0.44) * mm});
            skLineSegment(sketch, "E1834", {"start": v(-15.68, -0.44) * mm, "end": v(-15.57, -0.45) * mm});
            skLineSegment(sketch, "E1835", {"start": v(-15.57, -0.45) * mm, "end": v(-15.46, -0.48) * mm});
            skLineSegment(sketch, "E1836", {"start": v(-15.46, -0.48) * mm, "end": v(-15.36, -0.54) * mm});
            skLineSegment(sketch, "E1837", {"start": v(-15.36, -0.54) * mm, "end": v(-15.28, -0.61) * mm});
            skLineSegment(sketch, "E1838", {"start": v(-15.28, -0.61) * mm, "end": v(-15.22, -0.7) * mm});
            skLineSegment(sketch, "E1839", {"start": v(-15.22, -0.7) * mm, "end": v(-15.18, -0.81) * mm});
            skLineSegment(sketch, "E1840", {"start": v(-15.18, -0.81) * mm, "end": v(-15.16, -0.93) * mm});
            skLineSegment(sketch, "E1841", {"start": v(-15.16, -0.93) * mm, "end": v(-15.18, -1.04) * mm});
            skLineSegment(sketch, "E1842", {"start": v(-15.18, -1.04) * mm, "end": v(-15.22, -1.15) * mm});
            skLineSegment(sketch, "E1843", {"start": v(-15.22, -1.15) * mm, "end": v(-15.28, -1.24) * mm});
            skLineSegment(sketch, "E1844", {"start": v(-15.28, -1.24) * mm, "end": v(-15.36, -1.32) * mm});
            skLineSegment(sketch, "E1845", {"start": v(-15.36, -1.32) * mm, "end": v(-15.46, -1.37) * mm});
            skLineSegment(sketch, "E1846", {"start": v(-15.46, -1.37) * mm, "end": v(-15.57, -1.4) * mm});
            skLineSegment(sketch, "E1847", {"start": v(-15.57, -1.4) * mm, "end": v(-15.68, -1.4) * mm});
            skLineSegment(sketch, "E1848", {"start": v(-15.68, -1.4) * mm, "end": v(-15.8, -1.39) * mm});
            skLineSegment(sketch, "E1849", {"start": v(-15.8, -1.39) * mm, "end": v(-15.9, -1.34) * mm});
            skLineSegment(sketch, "E1850", {"start": v(-15.9, -1.34) * mm, "end": v(-15.99, -1.27) * mm});
            skLineSegment(sketch, "E1851", {"start": v(-15.99, -1.27) * mm, "end": v(-16.06, -1.18) * mm});
            skLineSegment(sketch, "E1852", {"start": v(-16.06, -1.18) * mm, "end": v(-16.1, -1.1) * mm});
            skLineSegment(sketch, "E1853", {"start": v(-16.1, -1.1) * mm, "end": v(-17.77, -1.1) * mm});
            skLineSegment(sketch, "E1854", {"start": v(-17.77, -1.1) * mm, "end": v(-20.54, -3.88) * mm});
            skLineSegment(sketch, "E1855", {"start": v(-20.54, -3.88) * mm, "end": v(-20.54, -9.63) * mm});
            skLineSegment(sketch, "E1856", {"start": v(-20.54, -9.63) * mm, "end": v(-20.54, -12.61) * mm});
            skLineSegment(sketch, "E1857", {"start": v(-20.54, -12.61) * mm, "end": v(-10.24, -22.9) * mm});
            skLineSegment(sketch, "E1858", {"start": v(-10.24, -22.9) * mm, "end": v(-10.14, -22.84) * mm});
            skLineSegment(sketch, "E1859", {"start": v(-10.14, -22.84) * mm, "end": v(-10, -22.78) * mm});
            skLineSegment(sketch, "E1860", {"start": v(-10, -22.78) * mm, "end": v(-9.86, -22.75) * mm});
            skLineSegment(sketch, "E1861", {"start": v(-9.86, -22.75) * mm, "end": v(-9.71, -22.74) * mm});
            skLineSegment(sketch, "E1862", {"start": v(-9.71, -22.74) * mm, "end": v(-9.56, -22.75) * mm});
            skLineSegment(sketch, "E1863", {"start": v(-9.56, -22.75) * mm, "end": v(-9.42, -22.78) * mm});
            skLineSegment(sketch, "E1864", {"start": v(-9.42, -22.78) * mm, "end": v(-9.28, -22.84) * mm});
            skLineSegment(sketch, "E1865", {"start": v(-9.28, -22.84) * mm, "end": v(-9.15, -22.92) * mm});
            skLineSegment(sketch, "E1866", {"start": v(-9.15, -22.92) * mm, "end": v(-9.04, -23.02) * mm});
            skLineSegment(sketch, "E1867", {"start": v(-9.04, -23.02) * mm, "end": v(-8.94, -23.13) * mm});
            skLineSegment(sketch, "E1868", {"start": v(-8.94, -23.13) * mm, "end": v(-8.86, -23.26) * mm});
            skLineSegment(sketch, "E1869", {"start": v(-8.86, -23.26) * mm, "end": v(-8.8, -23.4) * mm});
            skLineSegment(sketch, "E1870", {"start": v(-8.8, -23.4) * mm, "end": v(-8.77, -23.54) * mm});
            skLineSegment(sketch, "E1871", {"start": v(-8.77, -23.54) * mm, "end": v(-8.76, -23.7) * mm});
            skLineSegment(sketch, "E1872", {"start": v(-8.76, -23.7) * mm, "end": v(-8.76, -23.76) * mm});
            skLineSegment(sketch, "E1873", {"start": v(-11.3, -23.76) * mm, "end": v(-11.33, -23.91) * mm});
            skLineSegment(sketch, "E1874", {"start": v(-11.33, -23.91) * mm, "end": v(-11.37, -24.05) * mm});
            skLineSegment(sketch, "E1875", {"start": v(-11.37, -24.05) * mm, "end": v(-11.44, -24.19) * mm});
            skLineSegment(sketch, "E1876", {"start": v(-11.44, -24.19) * mm, "end": v(-11.53, -24.3) * mm});
            skLineSegment(sketch, "E1877", {"start": v(-11.53, -24.3) * mm, "end": v(-11.63, -24.41) * mm});
            skLineSegment(sketch, "E1878", {"start": v(-11.63, -24.41) * mm, "end": v(-11.75, -24.5) * mm});
            skLineSegment(sketch, "E1879", {"start": v(-11.75, -24.5) * mm, "end": v(-11.88, -24.57) * mm});
            skLineSegment(sketch, "E1880", {"start": v(-11.88, -24.57) * mm, "end": v(-12.03, -24.62) * mm});
            skLineSegment(sketch, "E1881", {"start": v(-12.03, -24.62) * mm, "end": v(-12.17, -24.64) * mm});
            skLineSegment(sketch, "E1882", {"start": v(-12.17, -24.64) * mm, "end": v(-12.32, -24.64) * mm});
            skLineSegment(sketch, "E1883", {"start": v(-12.32, -24.64) * mm, "end": v(-12.47, -24.62) * mm});
            skLineSegment(sketch, "E1884", {"start": v(-12.47, -24.62) * mm, "end": v(-12.61, -24.57) * mm});
            skLineSegment(sketch, "E1885", {"start": v(-12.61, -24.57) * mm, "end": v(-12.75, -24.5) * mm});
            skLineSegment(sketch, "E1886", {"start": v(-12.75, -24.5) * mm, "end": v(-12.87, -24.41) * mm});
            skLineSegment(sketch, "E1887", {"start": v(-12.87, -24.41) * mm, "end": v(-12.97, -24.3) * mm});
            skLineSegment(sketch, "E1888", {"start": v(-12.97, -24.3) * mm, "end": v(-13.06, -24.19) * mm});
            skLineSegment(sketch, "E1889", {"start": v(-13.06, -24.19) * mm, "end": v(-13.13, -24.05) * mm});
            skLineSegment(sketch, "E1890", {"start": v(-13.13, -24.05) * mm, "end": v(-13.17, -23.91) * mm});
            skLineSegment(sketch, "E1891", {"start": v(-13.17, -23.91) * mm, "end": v(-13.2, -23.76) * mm});
            skLineSegment(sketch, "E1892", {"start": v(-13.2, -23.76) * mm, "end": v(-13.2, -23.61) * mm});
            skLineSegment(sketch, "E1893", {"start": v(-13.2, -23.61) * mm, "end": v(-13.17, -23.47) * mm});
            skLineSegment(sketch, "E1894", {"start": v(-13.17, -23.47) * mm, "end": v(-13.13, -23.32) * mm});
            skLineSegment(sketch, "E1895", {"start": v(-13.13, -23.32) * mm, "end": v(-13.06, -23.2) * mm});
            skLineSegment(sketch, "E1896", {"start": v(-13.06, -23.2) * mm, "end": v(-13.04, -23.15) * mm});
            skLineSegment(sketch, "E1897", {"start": v(-13.04, -23.15) * mm, "end": v(-22.3, -13.88) * mm});
            skLineSegment(sketch, "E1898", {"start": v(-22.3, -13.88) * mm, "end": v(-22.34, -13.82) * mm});
            skLineSegment(sketch, "E1899", {"start": v(-22.34, -13.82) * mm, "end": v(-22.34, -13.78) * mm});
            skLineSegment(sketch, "E1900", {"start": v(-22.34, -13.78) * mm, "end": v(-22.34, -1.66) * mm});
            skLineSegment(sketch, "E1901", {"start": v(-22.34, -1.66) * mm, "end": v(-22.3, -1.6) * mm});
            skLineSegment(sketch, "E1902", {"start": v(-22.3, -1.6) * mm, "end": v(-21.81, -1.1) * mm});
            skLineSegment(sketch, "E1903", {"start": v(-21.81, -1.1) * mm, "end": v(-20.21, 0.5) * mm});
            skLineSegment(sketch, "E1904", {"start": v(-20.21, 0.5) * mm, "end": v(-20.14, 0.52) * mm});
            skLineSegment(sketch, "E1905", {"start": v(-20.14, 0.52) * mm, "end": v(-19.44, 0.52) * mm});
            skLineSegment(sketch, "E1906", {"start": v(-19.44, 0.52) * mm, "end": v(-16.1, 0.52) * mm});
            skLineSegment(sketch, "E1907", {"start": v(-16.1, 0.52) * mm, "end": v(-16.04, 0.63) * mm});
            skLineSegment(sketch, "E1908", {"start": v(-16.04, 0.63) * mm, "end": v(-15.96, 0.71) * mm});
            skLineSegment(sketch, "E1909", {"start": v(-15.96, 0.71) * mm, "end": v(-15.86, 0.77) * mm});
            skLineSegment(sketch, "E1910", {"start": v(-15.86, 0.77) * mm, "end": v(-15.76, 0.81) * mm});
            skLineSegment(sketch, "E1911", {"start": v(-15.76, 0.81) * mm, "end": v(-15.65, 0.83) * mm});
            skLineSegment(sketch, "E1912", {"start": v(-15.65, 0.83) * mm, "end": v(-15.53, 0.81) * mm});
            skLineSegment(sketch, "E1913", {"start": v(-15.53, 0.81) * mm, "end": v(-15.43, 0.77) * mm});
            skLineSegment(sketch, "E1914", {"start": v(-15.43, 0.77) * mm, "end": v(-15.33, 0.71) * mm});
            skLineSegment(sketch, "E1915", {"start": v(-15.33, 0.71) * mm, "end": v(-15.26, 0.63) * mm});
            skLineSegment(sketch, "E1916", {"start": v(-15.26, 0.63) * mm, "end": v(-15.2, 0.53) * mm});
            skLineSegment(sketch, "E1917", {"start": v(-15.2, 0.53) * mm, "end": v(-15.17, 0.42) * mm});
            skLineSegment(sketch, "E1918", {"start": v(-15.17, 0.42) * mm, "end": v(-15.17, 0.3) * mm});
            skLineSegment(sketch, "E1919", {"start": v(-15.17, 0.3) * mm, "end": v(-15.19, 0.2) * mm});
            skLineSegment(sketch, "E1920", {"start": v(-15.19, 0.2) * mm, "end": v(-15.23, 0.1) * mm});
            skLineSegment(sketch, "E1921", {"start": v(-15.23, 0.1) * mm, "end": v(-15.3, 0) * mm});
            skLineSegment(sketch, "E1922", {"start": v(-15.3, 0) * mm, "end": v(-15.4, -0.07) * mm});
            skLineSegment(sketch, "E1923", {"start": v(-15.4, -0.07) * mm, "end": v(-15.5, -0.12) * mm});
            skLineSegment(sketch, "E1924", {"start": v(-15.5, -0.12) * mm, "end": v(-15.6, -0.14) * mm});
            skLineSegment(sketch, "E1925", {"start": v(-15.6, -0.14) * mm, "end": v(-15.72, -0.13) * mm});
            skLineSegment(sketch, "E1926", {"start": v(-15.72, -0.13) * mm, "end": v(-15.83, -0.1) * mm});
            skLineSegment(sketch, "E1927", {"start": v(-15.83, -0.1) * mm, "end": v(-15.93, -0.05) * mm});
            skLineSegment(sketch, "E1928", {"start": v(-15.93, -0.05) * mm, "end": v(-16.01, 0.03) * mm});
            skLineSegment(sketch, "E1929", {"start": v(-16.01, 0.03) * mm, "end": v(-16.08, 0.12) * mm});
            skLineSegment(sketch, "E1930", {"start": v(-16.08, 0.12) * mm, "end": v(-16.1, 0.17) * mm});
            skLineSegment(sketch, "E1931", {"start": v(-16.1, 0.17) * mm, "end": v(-20.05, 0.17) * mm});
            skLineSegment(sketch, "E1932", {"start": v(-20.05, 0.17) * mm, "end": v(-21.99, -1.78) * mm});
            skLineSegment(sketch, "E1933", {"start": v(-21.99, -1.78) * mm, "end": v(-21.99, -5.5) * mm});
            skLineSegment(sketch, "E1934", {"start": v(-21.99, -5.5) * mm, "end": v(-21.99, -13.7) * mm});
            skLineSegment(sketch, "E1935", {"start": v(-21.99, -13.7) * mm, "end": v(-12.78, -22.9) * mm});
            skLineSegment(sketch, "E1936", {"start": v(-12.78, -22.9) * mm, "end": v(-12.68, -22.84) * mm});
            skLineSegment(sketch, "E1937", {"start": v(-12.68, -22.84) * mm, "end": v(-12.55, -22.78) * mm});
            skLineSegment(sketch, "E1938", {"start": v(-12.55, -22.78) * mm, "end": v(-12.4, -22.75) * mm});
            skLineSegment(sketch, "E1939", {"start": v(-12.4, -22.75) * mm, "end": v(-12.25, -22.74) * mm});
            skLineSegment(sketch, "E1940", {"start": v(-12.25, -22.74) * mm, "end": v(-12.1, -22.75) * mm});
            skLineSegment(sketch, "E1941", {"start": v(-12.1, -22.75) * mm, "end": v(-11.96, -22.78) * mm});
            skLineSegment(sketch, "E1942", {"start": v(-11.96, -22.78) * mm, "end": v(-11.82, -22.84) * mm});
            skLineSegment(sketch, "E1943", {"start": v(-11.82, -22.84) * mm, "end": v(-11.7, -22.92) * mm});
            skLineSegment(sketch, "E1944", {"start": v(-11.7, -22.92) * mm, "end": v(-11.58, -23.02) * mm});
            skLineSegment(sketch, "E1945", {"start": v(-11.58, -23.02) * mm, "end": v(-11.48, -23.13) * mm});
            skLineSegment(sketch, "E1946", {"start": v(-11.48, -23.13) * mm, "end": v(-11.4, -23.26) * mm});
            skLineSegment(sketch, "E1947", {"start": v(-11.4, -23.26) * mm, "end": v(-11.35, -23.4) * mm});
            skLineSegment(sketch, "E1948", {"start": v(-11.35, -23.4) * mm, "end": v(-11.31, -23.54) * mm});
            skLineSegment(sketch, "E1949", {"start": v(-11.31, -23.54) * mm, "end": v(-11.3, -23.7) * mm});
            skLineSegment(sketch, "E1950", {"start": v(-11.3, -23.7) * mm, "end": v(-11.3, -23.76) * mm});
            skLineSegment(sketch, "E1951", {"start": v(-15.17, -2.24) * mm, "end": v(-15.19, -2.35) * mm});
            skLineSegment(sketch, "E1952", {"start": v(-15.19, -2.35) * mm, "end": v(-15.23, -2.45) * mm});
            skLineSegment(sketch, "E1953", {"start": v(-15.23, -2.45) * mm, "end": v(-15.3, -2.54) * mm});
            skLineSegment(sketch, "E1954", {"start": v(-15.3, -2.54) * mm, "end": v(-15.4, -2.6) * mm});
            skLineSegment(sketch, "E1955", {"start": v(-15.4, -2.6) * mm, "end": v(-15.5, -2.66) * mm});
            skLineSegment(sketch, "E1956", {"start": v(-15.5, -2.66) * mm, "end": v(-15.6, -2.68) * mm});
            skLineSegment(sketch, "E1957", {"start": v(-15.6, -2.68) * mm, "end": v(-15.72, -2.67) * mm});
            skLineSegment(sketch, "E1958", {"start": v(-15.72, -2.67) * mm, "end": v(-15.83, -2.64) * mm});
            skLineSegment(sketch, "E1959", {"start": v(-15.83, -2.64) * mm, "end": v(-15.93, -2.59) * mm});
            skLineSegment(sketch, "E1960", {"start": v(-15.93, -2.59) * mm, "end": v(-16.01, -2.5) * mm});
            skLineSegment(sketch, "E1961", {"start": v(-16.01, -2.5) * mm, "end": v(-16.08, -2.42) * mm});
            skLineSegment(sketch, "E1962", {"start": v(-16.08, -2.42) * mm, "end": v(-16.12, -2.3) * mm});
            skLineSegment(sketch, "E1963", {"start": v(-16.12, -2.3) * mm, "end": v(-16.13, -2.2) * mm});
            skLineSegment(sketch, "E1964", {"start": v(-16.13, -2.2) * mm, "end": v(-16.12, -2.08) * mm});
            skLineSegment(sketch, "E1965", {"start": v(-16.12, -2.08) * mm, "end": v(-16.08, -1.98) * mm});
            skLineSegment(sketch, "E1966", {"start": v(-16.08, -1.98) * mm, "end": v(-16.01, -1.88) * mm});
            skLineSegment(sketch, "E1967", {"start": v(-16.01, -1.88) * mm, "end": v(-15.93, -1.8) * mm});
            skLineSegment(sketch, "E1968", {"start": v(-15.93, -1.8) * mm, "end": v(-15.83, -1.75) * mm});
            skLineSegment(sketch, "E1969", {"start": v(-15.83, -1.75) * mm, "end": v(-15.72, -1.72) * mm});
            skLineSegment(sketch, "E1970", {"start": v(-15.72, -1.72) * mm, "end": v(-15.6, -1.71) * mm});
            skLineSegment(sketch, "E1971", {"start": v(-15.6, -1.71) * mm, "end": v(-15.5, -1.74) * mm});
            skLineSegment(sketch, "E1972", {"start": v(-15.5, -1.74) * mm, "end": v(-15.4, -1.79) * mm});
            skLineSegment(sketch, "E1973", {"start": v(-15.4, -1.79) * mm, "end": v(-15.3, -1.85) * mm});
            skLineSegment(sketch, "E1974", {"start": v(-15.3, -1.85) * mm, "end": v(-15.23, -1.95) * mm});
            skLineSegment(sketch, "E1975", {"start": v(-15.23, -1.95) * mm, "end": v(-15.19, -2.05) * mm});
            skLineSegment(sketch, "E1976", {"start": v(-15.19, -2.05) * mm, "end": v(-15.17, -2.16) * mm});
            skLineSegment(sketch, "E1977", {"start": v(-15.17, -2.16) * mm, "end": v(-15.17, -2.24) * mm});
            skLineSegment(sketch, "E1978", {"start": v(35.8, 23.35) * mm, "end": v(37.56, 23.35) * mm});
            skLineSegment(sketch, "E1979", {"start": v(37.56, 23.35) * mm, "end": v(37.56, 21.45) * mm});
            skLineSegment(sketch, "E1980", {"start": v(37.56, 21.45) * mm, "end": v(35.66, 21.45) * mm});
            skLineSegment(sketch, "E1981", {"start": v(35.66, 21.45) * mm, "end": v(35.66, 23.35) * mm});
            skLineSegment(sketch, "E1982", {"start": v(35.66, 23.35) * mm, "end": v(35.8, 23.35) * mm});
            skLineSegment(sketch, "E1983", {"start": v(37.56, 19.79) * mm, "end": v(37.54, 19.64) * mm});
            skLineSegment(sketch, "E1984", {"start": v(37.54, 19.64) * mm, "end": v(37.5, 19.5) * mm});
            skLineSegment(sketch, "E1985", {"start": v(37.5, 19.5) * mm, "end": v(37.42, 19.36) * mm});
            skLineSegment(sketch, "E1986", {"start": v(37.42, 19.36) * mm, "end": v(37.33, 19.24) * mm});
            skLineSegment(sketch, "E1987", {"start": v(37.33, 19.24) * mm, "end": v(37.23, 19.14) * mm});
            skLineSegment(sketch, "E1988", {"start": v(37.23, 19.14) * mm, "end": v(37.1, 19.05) * mm});
            skLineSegment(sketch, "E1989", {"start": v(37.1, 19.05) * mm, "end": v(36.97, 18.98) * mm});
            skLineSegment(sketch, "E1990", {"start": v(36.97, 18.98) * mm, "end": v(36.83, 18.94) * mm});
            skLineSegment(sketch, "E1991", {"start": v(36.83, 18.94) * mm, "end": v(36.69, 18.91) * mm});
            skLineSegment(sketch, "E1992", {"start": v(36.69, 18.91) * mm, "end": v(36.54, 18.91) * mm});
            skLineSegment(sketch, "E1993", {"start": v(36.54, 18.91) * mm, "end": v(36.39, 18.94) * mm});
            skLineSegment(sketch, "E1994", {"start": v(36.39, 18.94) * mm, "end": v(36.25, 18.98) * mm});
            skLineSegment(sketch, "E1995", {"start": v(36.25, 18.98) * mm, "end": v(36.11, 19.05) * mm});
            skLineSegment(sketch, "E1996", {"start": v(36.11, 19.05) * mm, "end": v(36, 19.14) * mm});
            skLineSegment(sketch, "E1997", {"start": v(36, 19.14) * mm, "end": v(35.89, 19.24) * mm});
            skLineSegment(sketch, "E1998", {"start": v(35.89, 19.24) * mm, "end": v(35.8, 19.36) * mm});
            skLineSegment(sketch, "E1999", {"start": v(35.8, 19.36) * mm, "end": v(35.73, 19.5) * mm});
            skLineSegment(sketch, "E2000", {"start": v(35.73, 19.5) * mm, "end": v(35.68, 19.64) * mm});
            skLineSegment(sketch, "E2001", {"start": v(35.68, 19.64) * mm, "end": v(35.66, 19.79) * mm});
            skLineSegment(sketch, "E2002", {"start": v(35.66, 19.79) * mm, "end": v(35.66, 19.93) * mm});
            skLineSegment(sketch, "E2003", {"start": v(35.66, 19.93) * mm, "end": v(35.68, 20.08) * mm});
            skLineSegment(sketch, "E2004", {"start": v(35.68, 20.08) * mm, "end": v(35.73, 20.22) * mm});
            skLineSegment(sketch, "E2005", {"start": v(35.73, 20.22) * mm, "end": v(35.8, 20.36) * mm});
            skLineSegment(sketch, "E2006", {"start": v(35.8, 20.36) * mm, "end": v(35.89, 20.48) * mm});
            skLineSegment(sketch, "E2007", {"start": v(35.89, 20.48) * mm, "end": v(36, 20.58) * mm});
            skLineSegment(sketch, "E2008", {"start": v(36, 20.58) * mm, "end": v(36.11, 20.67) * mm});
            skLineSegment(sketch, "E2009", {"start": v(36.11, 20.67) * mm, "end": v(36.25, 20.74) * mm});
            skLineSegment(sketch, "E2010", {"start": v(36.25, 20.74) * mm, "end": v(36.39, 20.78) * mm});
            skLineSegment(sketch, "E2011", {"start": v(36.39, 20.78) * mm, "end": v(36.54, 20.8) * mm});
            skLineSegment(sketch, "E2012", {"start": v(36.54, 20.8) * mm, "end": v(36.69, 20.8) * mm});
            skLineSegment(sketch, "E2013", {"start": v(36.69, 20.8) * mm, "end": v(36.83, 20.78) * mm});
            skLineSegment(sketch, "E2014", {"start": v(36.83, 20.78) * mm, "end": v(36.97, 20.74) * mm});
            skLineSegment(sketch, "E2015", {"start": v(36.97, 20.74) * mm, "end": v(37.1, 20.67) * mm});
            skLineSegment(sketch, "E2016", {"start": v(37.1, 20.67) * mm, "end": v(37.23, 20.58) * mm});
            skLineSegment(sketch, "E2017", {"start": v(37.23, 20.58) * mm, "end": v(37.33, 20.48) * mm});
            skLineSegment(sketch, "E2018", {"start": v(37.33, 20.48) * mm, "end": v(37.42, 20.36) * mm});
            skLineSegment(sketch, "E2019", {"start": v(37.42, 20.36) * mm, "end": v(37.5, 20.22) * mm});
            skLineSegment(sketch, "E2020", {"start": v(37.5, 20.22) * mm, "end": v(37.54, 20.08) * mm});
            skLineSegment(sketch, "E2021", {"start": v(37.54, 20.08) * mm, "end": v(37.56, 19.93) * mm});
            skLineSegment(sketch, "E2022", {"start": v(37.56, 19.93) * mm, "end": v(37.56, 19.79) * mm});
            skLineSegment(sketch, "E2023", {"start": v(37.56, 17.25) * mm, "end": v(37.54, 17.1) * mm});
            skLineSegment(sketch, "E2024", {"start": v(37.54, 17.1) * mm, "end": v(37.5, 16.96) * mm});
            skLineSegment(sketch, "E2025", {"start": v(37.5, 16.96) * mm, "end": v(37.42, 16.82) * mm});
            skLineSegment(sketch, "E2026", {"start": v(37.42, 16.82) * mm, "end": v(37.33, 16.7) * mm});
            skLineSegment(sketch, "E2027", {"start": v(37.33, 16.7) * mm, "end": v(37.23, 16.6) * mm});
            skLineSegment(sketch, "E2028", {"start": v(37.23, 16.6) * mm, "end": v(37.1, 16.5) * mm});
            skLineSegment(sketch, "E2029", {"start": v(37.1, 16.5) * mm, "end": v(36.97, 16.44) * mm});
            skLineSegment(sketch, "E2030", {"start": v(36.97, 16.44) * mm, "end": v(36.83, 16.4) * mm});
            skLineSegment(sketch, "E2031", {"start": v(36.83, 16.4) * mm, "end": v(36.69, 16.37) * mm});
            skLineSegment(sketch, "E2032", {"start": v(36.69, 16.37) * mm, "end": v(36.54, 16.37) * mm});
            skLineSegment(sketch, "E2033", {"start": v(36.54, 16.37) * mm, "end": v(36.39, 16.4) * mm});
            skLineSegment(sketch, "E2034", {"start": v(36.39, 16.4) * mm, "end": v(36.25, 16.44) * mm});
            skLineSegment(sketch, "E2035", {"start": v(36.25, 16.44) * mm, "end": v(36.11, 16.5) * mm});
            skLineSegment(sketch, "E2036", {"start": v(36.11, 16.5) * mm, "end": v(36, 16.6) * mm});
            skLineSegment(sketch, "E2037", {"start": v(36, 16.6) * mm, "end": v(35.89, 16.7) * mm});
            skLineSegment(sketch, "E2038", {"start": v(35.89, 16.7) * mm, "end": v(35.8, 16.82) * mm});
            skLineSegment(sketch, "E2039", {"start": v(35.8, 16.82) * mm, "end": v(35.73, 16.96) * mm});
            skLineSegment(sketch, "E2040", {"start": v(35.73, 16.96) * mm, "end": v(35.68, 17.1) * mm});
            skLineSegment(sketch, "E2041", {"start": v(35.68, 17.1) * mm, "end": v(35.66, 17.25) * mm});
            skLineSegment(sketch, "E2042", {"start": v(35.66, 17.25) * mm, "end": v(35.66, 17.4) * mm});
            skLineSegment(sketch, "E2043", {"start": v(35.66, 17.4) * mm, "end": v(35.68, 17.54) * mm});
            skLineSegment(sketch, "E2044", {"start": v(35.68, 17.54) * mm, "end": v(35.73, 17.68) * mm});
            skLineSegment(sketch, "E2045", {"start": v(35.73, 17.68) * mm, "end": v(35.8, 17.82) * mm});
            skLineSegment(sketch, "E2046", {"start": v(35.8, 17.82) * mm, "end": v(35.89, 17.94) * mm});
            skLineSegment(sketch, "E2047", {"start": v(35.89, 17.94) * mm, "end": v(36, 18.04) * mm});
            skLineSegment(sketch, "E2048", {"start": v(36, 18.04) * mm, "end": v(36.11, 18.13) * mm});
            skLineSegment(sketch, "E2049", {"start": v(36.11, 18.13) * mm, "end": v(36.25, 18.2) * mm});
            skLineSegment(sketch, "E2050", {"start": v(36.25, 18.2) * mm, "end": v(36.39, 18.24) * mm});
            skLineSegment(sketch, "E2051", {"start": v(36.39, 18.24) * mm, "end": v(36.54, 18.27) * mm});
            skLineSegment(sketch, "E2052", {"start": v(36.54, 18.27) * mm, "end": v(36.69, 18.27) * mm});
            skLineSegment(sketch, "E2053", {"start": v(36.69, 18.27) * mm, "end": v(36.83, 18.24) * mm});
            skLineSegment(sketch, "E2054", {"start": v(36.83, 18.24) * mm, "end": v(36.97, 18.2) * mm});
            skLineSegment(sketch, "E2055", {"start": v(36.97, 18.2) * mm, "end": v(37.1, 18.13) * mm});
            skLineSegment(sketch, "E2056", {"start": v(37.1, 18.13) * mm, "end": v(37.23, 18.04) * mm});
            skLineSegment(sketch, "E2057", {"start": v(37.23, 18.04) * mm, "end": v(37.33, 17.94) * mm});
            skLineSegment(sketch, "E2058", {"start": v(37.33, 17.94) * mm, "end": v(37.42, 17.82) * mm});
            skLineSegment(sketch, "E2059", {"start": v(37.42, 17.82) * mm, "end": v(37.5, 17.68) * mm});
            skLineSegment(sketch, "E2060", {"start": v(37.5, 17.68) * mm, "end": v(37.54, 17.54) * mm});
            skLineSegment(sketch, "E2061", {"start": v(37.54, 17.54) * mm, "end": v(37.56, 17.4) * mm});
            skLineSegment(sketch, "E2062", {"start": v(37.56, 17.4) * mm, "end": v(37.56, 17.25) * mm});
            skLineSegment(sketch, "E2063", {"start": v(37.56, 14.7) * mm, "end": v(37.54, 14.56) * mm});
            skLineSegment(sketch, "E2064", {"start": v(37.54, 14.56) * mm, "end": v(37.5, 14.42) * mm});
            skLineSegment(sketch, "E2065", {"start": v(37.5, 14.42) * mm, "end": v(37.42, 14.28) * mm});
            skLineSegment(sketch, "E2066", {"start": v(37.42, 14.28) * mm, "end": v(37.33, 14.16) * mm});
            skLineSegment(sketch, "E2067", {"start": v(37.33, 14.16) * mm, "end": v(37.23, 14.06) * mm});
            skLineSegment(sketch, "E2068", {"start": v(37.23, 14.06) * mm, "end": v(37.1, 13.97) * mm});
            skLineSegment(sketch, "E2069", {"start": v(37.1, 13.97) * mm, "end": v(36.97, 13.9) * mm});
            skLineSegment(sketch, "E2070", {"start": v(36.97, 13.9) * mm, "end": v(36.83, 13.86) * mm});
            skLineSegment(sketch, "E2071", {"start": v(36.83, 13.86) * mm, "end": v(36.69, 13.83) * mm});
            skLineSegment(sketch, "E2072", {"start": v(36.69, 13.83) * mm, "end": v(36.54, 13.83) * mm});
            skLineSegment(sketch, "E2073", {"start": v(36.54, 13.83) * mm, "end": v(36.39, 13.86) * mm});
            skLineSegment(sketch, "E2074", {"start": v(36.39, 13.86) * mm, "end": v(36.25, 13.9) * mm});
            skLineSegment(sketch, "E2075", {"start": v(36.25, 13.9) * mm, "end": v(36.11, 13.97) * mm});
            skLineSegment(sketch, "E2076", {"start": v(36.11, 13.97) * mm, "end": v(36, 14.06) * mm});
            skLineSegment(sketch, "E2077", {"start": v(36, 14.06) * mm, "end": v(35.89, 14.16) * mm});
            skLineSegment(sketch, "E2078", {"start": v(35.89, 14.16) * mm, "end": v(35.8, 14.28) * mm});
            skLineSegment(sketch, "E2079", {"start": v(35.8, 14.28) * mm, "end": v(35.73, 14.42) * mm});
            skLineSegment(sketch, "E2080", {"start": v(35.73, 14.42) * mm, "end": v(35.68, 14.56) * mm});
            skLineSegment(sketch, "E2081", {"start": v(35.68, 14.56) * mm, "end": v(35.66, 14.7) * mm});
            skLineSegment(sketch, "E2082", {"start": v(35.66, 14.7) * mm, "end": v(35.66, 14.85) * mm});
            skLineSegment(sketch, "E2083", {"start": v(35.66, 14.85) * mm, "end": v(35.68, 15) * mm});
            skLineSegment(sketch, "E2084", {"start": v(35.68, 15) * mm, "end": v(35.73, 15.14) * mm});
            skLineSegment(sketch, "E2085", {"start": v(35.73, 15.14) * mm, "end": v(35.8, 15.28) * mm});
            skLineSegment(sketch, "E2086", {"start": v(35.8, 15.28) * mm, "end": v(35.89, 15.4) * mm});
            skLineSegment(sketch, "E2087", {"start": v(35.89, 15.4) * mm, "end": v(36, 15.5) * mm});
            skLineSegment(sketch, "E2088", {"start": v(36, 15.5) * mm, "end": v(36.11, 15.6) * mm});
            skLineSegment(sketch, "E2089", {"start": v(36.11, 15.6) * mm, "end": v(36.25, 15.66) * mm});
            skLineSegment(sketch, "E2090", {"start": v(36.25, 15.66) * mm, "end": v(36.39, 15.7) * mm});
            skLineSegment(sketch, "E2091", {"start": v(36.39, 15.7) * mm, "end": v(36.54, 15.73) * mm});
            skLineSegment(sketch, "E2092", {"start": v(36.54, 15.73) * mm, "end": v(36.69, 15.73) * mm});
            skLineSegment(sketch, "E2093", {"start": v(36.69, 15.73) * mm, "end": v(36.83, 15.7) * mm});
            skLineSegment(sketch, "E2094", {"start": v(36.83, 15.7) * mm, "end": v(36.97, 15.66) * mm});
            skLineSegment(sketch, "E2095", {"start": v(36.97, 15.66) * mm, "end": v(37.1, 15.6) * mm});
            skLineSegment(sketch, "E2096", {"start": v(37.1, 15.6) * mm, "end": v(37.23, 15.5) * mm});
            skLineSegment(sketch, "E2097", {"start": v(37.23, 15.5) * mm, "end": v(37.33, 15.4) * mm});
            skLineSegment(sketch, "E2098", {"start": v(37.33, 15.4) * mm, "end": v(37.42, 15.28) * mm});
            skLineSegment(sketch, "E2099", {"start": v(37.42, 15.28) * mm, "end": v(37.5, 15.14) * mm});
            skLineSegment(sketch, "E2100", {"start": v(37.5, 15.14) * mm, "end": v(37.54, 15) * mm});
            skLineSegment(sketch, "E2101", {"start": v(37.54, 15) * mm, "end": v(37.56, 14.85) * mm});
            skLineSegment(sketch, "E2102", {"start": v(37.56, 14.85) * mm, "end": v(37.56, 14.7) * mm});
            skLineSegment(sketch, "E2103", {"start": v(37.56, 12.17) * mm, "end": v(37.54, 12.02) * mm});
            skLineSegment(sketch, "E2104", {"start": v(37.54, 12.02) * mm, "end": v(37.5, 11.88) * mm});
            skLineSegment(sketch, "E2105", {"start": v(37.5, 11.88) * mm, "end": v(37.42, 11.74) * mm});
            skLineSegment(sketch, "E2106", {"start": v(37.42, 11.74) * mm, "end": v(37.33, 11.62) * mm});
            skLineSegment(sketch, "E2107", {"start": v(37.33, 11.62) * mm, "end": v(37.23, 11.52) * mm});
            skLineSegment(sketch, "E2108", {"start": v(37.23, 11.52) * mm, "end": v(37.1, 11.43) * mm});
            skLineSegment(sketch, "E2109", {"start": v(37.1, 11.43) * mm, "end": v(36.97, 11.36) * mm});
            skLineSegment(sketch, "E2110", {"start": v(36.97, 11.36) * mm, "end": v(36.83, 11.32) * mm});
            skLineSegment(sketch, "E2111", {"start": v(36.83, 11.32) * mm, "end": v(36.69, 11.3) * mm});
            skLineSegment(sketch, "E2112", {"start": v(36.69, 11.3) * mm, "end": v(36.54, 11.3) * mm});
            skLineSegment(sketch, "E2113", {"start": v(36.54, 11.3) * mm, "end": v(36.39, 11.32) * mm});
            skLineSegment(sketch, "E2114", {"start": v(36.39, 11.32) * mm, "end": v(36.25, 11.36) * mm});
            skLineSegment(sketch, "E2115", {"start": v(36.25, 11.36) * mm, "end": v(36.11, 11.43) * mm});
            skLineSegment(sketch, "E2116", {"start": v(36.11, 11.43) * mm, "end": v(36, 11.52) * mm});
            skLineSegment(sketch, "E2117", {"start": v(36, 11.52) * mm, "end": v(35.89, 11.62) * mm});
            skLineSegment(sketch, "E2118", {"start": v(35.89, 11.62) * mm, "end": v(35.8, 11.74) * mm});
            skLineSegment(sketch, "E2119", {"start": v(35.8, 11.74) * mm, "end": v(35.73, 11.88) * mm});
            skLineSegment(sketch, "E2120", {"start": v(35.73, 11.88) * mm, "end": v(35.68, 12.02) * mm});
            skLineSegment(sketch, "E2121", {"start": v(35.68, 12.02) * mm, "end": v(35.66, 12.17) * mm});
            skLineSegment(sketch, "E2122", {"start": v(35.66, 12.17) * mm, "end": v(35.66, 12.31) * mm});
            skLineSegment(sketch, "E2123", {"start": v(35.66, 12.31) * mm, "end": v(35.68, 12.46) * mm});
            skLineSegment(sketch, "E2124", {"start": v(35.68, 12.46) * mm, "end": v(35.73, 12.6) * mm});
            skLineSegment(sketch, "E2125", {"start": v(35.73, 12.6) * mm, "end": v(35.8, 12.74) * mm});
            skLineSegment(sketch, "E2126", {"start": v(35.8, 12.74) * mm, "end": v(35.89, 12.86) * mm});
            skLineSegment(sketch, "E2127", {"start": v(35.89, 12.86) * mm, "end": v(36, 12.96) * mm});
            skLineSegment(sketch, "E2128", {"start": v(36, 12.96) * mm, "end": v(36.11, 13.05) * mm});
            skLineSegment(sketch, "E2129", {"start": v(36.11, 13.05) * mm, "end": v(36.25, 13.12) * mm});
            skLineSegment(sketch, "E2130", {"start": v(36.25, 13.12) * mm, "end": v(36.39, 13.16) * mm});
            skLineSegment(sketch, "E2131", {"start": v(36.39, 13.16) * mm, "end": v(36.54, 13.19) * mm});
            skLineSegment(sketch, "E2132", {"start": v(36.54, 13.19) * mm, "end": v(36.69, 13.19) * mm});
            skLineSegment(sketch, "E2133", {"start": v(36.69, 13.19) * mm, "end": v(36.83, 13.16) * mm});
            skLineSegment(sketch, "E2134", {"start": v(36.83, 13.16) * mm, "end": v(36.97, 13.12) * mm});
            skLineSegment(sketch, "E2135", {"start": v(36.97, 13.12) * mm, "end": v(37.1, 13.05) * mm});
            skLineSegment(sketch, "E2136", {"start": v(37.1, 13.05) * mm, "end": v(37.23, 12.96) * mm});
            skLineSegment(sketch, "E2137", {"start": v(37.23, 12.96) * mm, "end": v(37.33, 12.86) * mm});
            skLineSegment(sketch, "E2138", {"start": v(37.33, 12.86) * mm, "end": v(37.42, 12.74) * mm});
            skLineSegment(sketch, "E2139", {"start": v(37.42, 12.74) * mm, "end": v(37.5, 12.6) * mm});
            skLineSegment(sketch, "E2140", {"start": v(37.5, 12.6) * mm, "end": v(37.54, 12.46) * mm});
            skLineSegment(sketch, "E2141", {"start": v(37.54, 12.46) * mm, "end": v(37.56, 12.31) * mm});
            skLineSegment(sketch, "E2142", {"start": v(37.56, 12.31) * mm, "end": v(37.56, 12.17) * mm});
            skLineSegment(sketch, "E2143", {"start": v(37.56, 9.63) * mm, "end": v(37.54, 9.48) * mm});
            skLineSegment(sketch, "E2144", {"start": v(37.54, 9.48) * mm, "end": v(37.5, 9.34) * mm});
            skLineSegment(sketch, "E2145", {"start": v(37.5, 9.34) * mm, "end": v(37.42, 9.2) * mm});
            skLineSegment(sketch, "E2146", {"start": v(37.42, 9.2) * mm, "end": v(37.33, 9.08) * mm});
            skLineSegment(sketch, "E2147", {"start": v(37.33, 9.08) * mm, "end": v(37.23, 8.98) * mm});
            skLineSegment(sketch, "E2148", {"start": v(37.23, 8.98) * mm, "end": v(37.1, 8.89) * mm});
            skLineSegment(sketch, "E2149", {"start": v(37.1, 8.89) * mm, "end": v(36.97, 8.82) * mm});
            skLineSegment(sketch, "E2150", {"start": v(36.97, 8.82) * mm, "end": v(36.83, 8.78) * mm});
            skLineSegment(sketch, "E2151", {"start": v(36.83, 8.78) * mm, "end": v(36.69, 8.75) * mm});
            skLineSegment(sketch, "E2152", {"start": v(36.69, 8.75) * mm, "end": v(36.54, 8.75) * mm});
            skLineSegment(sketch, "E2153", {"start": v(36.54, 8.75) * mm, "end": v(36.39, 8.78) * mm});
            skLineSegment(sketch, "E2154", {"start": v(36.39, 8.78) * mm, "end": v(36.25, 8.82) * mm});
            skLineSegment(sketch, "E2155", {"start": v(36.25, 8.82) * mm, "end": v(36.11, 8.89) * mm});
            skLineSegment(sketch, "E2156", {"start": v(36.11, 8.89) * mm, "end": v(36, 8.98) * mm});
            skLineSegment(sketch, "E2157", {"start": v(36, 8.98) * mm, "end": v(35.89, 9.08) * mm});
            skLineSegment(sketch, "E2158", {"start": v(35.89, 9.08) * mm, "end": v(35.8, 9.2) * mm});
            skLineSegment(sketch, "E2159", {"start": v(35.8, 9.2) * mm, "end": v(35.73, 9.34) * mm});
            skLineSegment(sketch, "E2160", {"start": v(35.73, 9.34) * mm, "end": v(35.68, 9.48) * mm});
            skLineSegment(sketch, "E2161", {"start": v(35.68, 9.48) * mm, "end": v(35.66, 9.63) * mm});
            skLineSegment(sketch, "E2162", {"start": v(35.66, 9.63) * mm, "end": v(35.66, 9.77) * mm});
            skLineSegment(sketch, "E2163", {"start": v(35.66, 9.77) * mm, "end": v(35.68, 9.92) * mm});
            skLineSegment(sketch, "E2164", {"start": v(35.68, 9.92) * mm, "end": v(35.73, 10.06) * mm});
            skLineSegment(sketch, "E2165", {"start": v(35.73, 10.06) * mm, "end": v(35.8, 10.2) * mm});
            skLineSegment(sketch, "E2166", {"start": v(35.8, 10.2) * mm, "end": v(35.89, 10.32) * mm});
            skLineSegment(sketch, "E2167", {"start": v(35.89, 10.32) * mm, "end": v(36, 10.42) * mm});
            skLineSegment(sketch, "E2168", {"start": v(36, 10.42) * mm, "end": v(36.11, 10.51) * mm});
            skLineSegment(sketch, "E2169", {"start": v(36.11, 10.51) * mm, "end": v(36.25, 10.58) * mm});
            skLineSegment(sketch, "E2170", {"start": v(36.25, 10.58) * mm, "end": v(36.39, 10.62) * mm});
            skLineSegment(sketch, "E2171", {"start": v(36.39, 10.62) * mm, "end": v(36.54, 10.65) * mm});
            skLineSegment(sketch, "E2172", {"start": v(36.54, 10.65) * mm, "end": v(36.69, 10.65) * mm});
            skLineSegment(sketch, "E2173", {"start": v(36.69, 10.65) * mm, "end": v(36.83, 10.62) * mm});
            skLineSegment(sketch, "E2174", {"start": v(36.83, 10.62) * mm, "end": v(36.97, 10.58) * mm});
            skLineSegment(sketch, "E2175", {"start": v(36.97, 10.58) * mm, "end": v(37.1, 10.51) * mm});
            skLineSegment(sketch, "E2176", {"start": v(37.1, 10.51) * mm, "end": v(37.23, 10.42) * mm});
            skLineSegment(sketch, "E2177", {"start": v(37.23, 10.42) * mm, "end": v(37.33, 10.32) * mm});
            skLineSegment(sketch, "E2178", {"start": v(37.33, 10.32) * mm, "end": v(37.42, 10.2) * mm});
            skLineSegment(sketch, "E2179", {"start": v(37.42, 10.2) * mm, "end": v(37.5, 10.06) * mm});
            skLineSegment(sketch, "E2180", {"start": v(37.5, 10.06) * mm, "end": v(37.54, 9.92) * mm});
            skLineSegment(sketch, "E2181", {"start": v(37.54, 9.92) * mm, "end": v(37.56, 9.77) * mm});
            skLineSegment(sketch, "E2182", {"start": v(37.56, 9.77) * mm, "end": v(37.56, 9.63) * mm});
            skLineSegment(sketch, "E2183", {"start": v(13.4, 4.77) * mm, "end": v(13.49, 4.77) * mm});
            skLineSegment(sketch, "E2184", {"start": v(13.49, 4.77) * mm, "end": v(13.49, 22.74) * mm});
            skLineSegment(sketch, "E2185", {"start": v(13.49, 22.74) * mm, "end": v(12.84, 22.74) * mm});
            skLineSegment(sketch, "E2186", {"start": v(12.84, 22.74) * mm, "end": v(12.84, 24.64) * mm});
            skLineSegment(sketch, "E2187", {"start": v(12.84, 24.64) * mm, "end": v(14.74, 24.64) * mm});
            skLineSegment(sketch, "E2188", {"start": v(14.74, 24.64) * mm, "end": v(14.74, 23.77) * mm});
            skLineSegment(sketch, "E2189", {"start": v(14.74, 23.77) * mm, "end": v(14.82, 23.69) * mm});
            skLineSegment(sketch, "E2190", {"start": v(14.82, 23.69) * mm, "end": v(14.88, 23.59) * mm});
            skLineSegment(sketch, "E2191", {"start": v(14.88, 23.59) * mm, "end": v(14.93, 23.48) * mm});
            skLineSegment(sketch, "E2192", {"start": v(14.93, 23.48) * mm, "end": v(14.95, 23.37) * mm});
            skLineSegment(sketch, "E2193", {"start": v(14.95, 23.37) * mm, "end": v(14.96, 23.25) * mm});
            skLineSegment(sketch, "E2194", {"start": v(14.96, 23.25) * mm, "end": v(14.96, 4.78) * mm});
            skLineSegment(sketch, "E2195", {"start": v(14.96, 4.78) * mm, "end": v(15.17, 4.77) * mm});
            skLineSegment(sketch, "E2196", {"start": v(15.17, 4.77) * mm, "end": v(15.17, 2.87) * mm});
            skLineSegment(sketch, "E2197", {"start": v(15.17, 2.87) * mm, "end": v(13.27, 2.87) * mm});
            skLineSegment(sketch, "E2198", {"start": v(13.27, 2.87) * mm, "end": v(13.27, 4.77) * mm});
            skLineSegment(sketch, "E2199", {"start": v(13.27, 4.77) * mm, "end": v(13.4, 4.77) * mm});
            skLineSegment(sketch, "E2200", {"start": v(17.71, 3.75) * mm, "end": v(17.69, 3.6) * mm});
            skLineSegment(sketch, "E2201", {"start": v(17.69, 3.6) * mm, "end": v(17.64, 3.46) * mm});
            skLineSegment(sketch, "E2202", {"start": v(17.64, 3.46) * mm, "end": v(17.57, 3.32) * mm});
            skLineSegment(sketch, "E2203", {"start": v(17.57, 3.32) * mm, "end": v(17.49, 3.2) * mm});
            skLineSegment(sketch, "E2204", {"start": v(17.49, 3.2) * mm, "end": v(17.38, 3.1) * mm});
            skLineSegment(sketch, "E2205", {"start": v(17.38, 3.1) * mm, "end": v(17.26, 3) * mm});
            skLineSegment(sketch, "E2206", {"start": v(17.26, 3) * mm, "end": v(17.13, 2.94) * mm});
            skLineSegment(sketch, "E2207", {"start": v(17.13, 2.94) * mm, "end": v(16.98, 2.9) * mm});
            skLineSegment(sketch, "E2208", {"start": v(16.98, 2.9) * mm, "end": v(16.84, 2.87) * mm});
            skLineSegment(sketch, "E2209", {"start": v(16.84, 2.87) * mm, "end": v(16.69, 2.87) * mm});
            skLineSegment(sketch, "E2210", {"start": v(16.69, 2.87) * mm, "end": v(16.54, 2.9) * mm});
            skLineSegment(sketch, "E2211", {"start": v(16.54, 2.9) * mm, "end": v(16.4, 2.94) * mm});
            skLineSegment(sketch, "E2212", {"start": v(16.4, 2.94) * mm, "end": v(16.27, 3) * mm});
            skLineSegment(sketch, "E2213", {"start": v(16.27, 3) * mm, "end": v(16.14, 3.1) * mm});
            skLineSegment(sketch, "E2214", {"start": v(16.14, 3.1) * mm, "end": v(16.04, 3.2) * mm});
            skLineSegment(sketch, "E2215", {"start": v(16.04, 3.2) * mm, "end": v(15.95, 3.32) * mm});
            skLineSegment(sketch, "E2216", {"start": v(15.95, 3.32) * mm, "end": v(15.89, 3.46) * mm});
            skLineSegment(sketch, "E2217", {"start": v(15.89, 3.46) * mm, "end": v(15.84, 3.6) * mm});
            skLineSegment(sketch, "E2218", {"start": v(15.84, 3.6) * mm, "end": v(15.81, 3.75) * mm});
            skLineSegment(sketch, "E2219", {"start": v(15.81, 3.75) * mm, "end": v(15.81, 3.9) * mm});
            skLineSegment(sketch, "E2220", {"start": v(15.81, 3.9) * mm, "end": v(15.84, 4.04) * mm});
            skLineSegment(sketch, "E2221", {"start": v(15.84, 4.04) * mm, "end": v(15.89, 4.18) * mm});
            skLineSegment(sketch, "E2222", {"start": v(15.89, 4.18) * mm, "end": v(15.95, 4.32) * mm});
            skLineSegment(sketch, "E2223", {"start": v(15.95, 4.32) * mm, "end": v(16.03, 4.42) * mm});
            skLineSegment(sketch, "E2224", {"start": v(16.03, 4.42) * mm, "end": v(16.03, 22.78) * mm});
            skLineSegment(sketch, "E2225", {"start": v(16.03, 22.78) * mm, "end": v(15.83, 22.88) * mm});
            skLineSegment(sketch, "E2226", {"start": v(15.83, 22.88) * mm, "end": v(15.71, 22.96) * mm});
            skLineSegment(sketch, "E2227", {"start": v(15.71, 22.96) * mm, "end": v(15.6, 23.07) * mm});
            skLineSegment(sketch, "E2228", {"start": v(15.6, 23.07) * mm, "end": v(15.52, 23.2) * mm});
            skLineSegment(sketch, "E2229", {"start": v(15.52, 23.2) * mm, "end": v(15.45, 23.32) * mm});
            skLineSegment(sketch, "E2230", {"start": v(15.45, 23.32) * mm, "end": v(15.4, 23.46) * mm});
            skLineSegment(sketch, "E2231", {"start": v(15.4, 23.46) * mm, "end": v(15.38, 23.61) * mm});
            skLineSegment(sketch, "E2232", {"start": v(15.38, 23.61) * mm, "end": v(15.38, 23.76) * mm});
            skLineSegment(sketch, "E2233", {"start": v(15.38, 23.76) * mm, "end": v(15.4, 23.9) * mm});
            skLineSegment(sketch, "E2234", {"start": v(15.4, 23.9) * mm, "end": v(15.45, 24.05) * mm});
            skLineSegment(sketch, "E2235", {"start": v(15.45, 24.05) * mm, "end": v(15.52, 24.18) * mm});
            skLineSegment(sketch, "E2236", {"start": v(15.52, 24.18) * mm, "end": v(15.6, 24.3) * mm});
            skLineSegment(sketch, "E2237", {"start": v(15.6, 24.3) * mm, "end": v(15.71, 24.4) * mm});
            skLineSegment(sketch, "E2238", {"start": v(15.71, 24.4) * mm, "end": v(15.83, 24.5) * mm});
            skLineSegment(sketch, "E2239", {"start": v(15.83, 24.5) * mm, "end": v(15.97, 24.57) * mm});
            skLineSegment(sketch, "E2240", {"start": v(15.97, 24.57) * mm, "end": v(16.1, 24.61) * mm});
            skLineSegment(sketch, "E2241", {"start": v(16.1, 24.61) * mm, "end": v(16.26, 24.64) * mm});
            skLineSegment(sketch, "E2242", {"start": v(16.26, 24.64) * mm, "end": v(16.4, 24.64) * mm});
            skLineSegment(sketch, "E2243", {"start": v(16.4, 24.64) * mm, "end": v(16.55, 24.61) * mm});
            skLineSegment(sketch, "E2244", {"start": v(16.55, 24.61) * mm, "end": v(16.7, 24.57) * mm});
            skLineSegment(sketch, "E2245", {"start": v(16.7, 24.57) * mm, "end": v(16.83, 24.5) * mm});
            skLineSegment(sketch, "E2246", {"start": v(16.83, 24.5) * mm, "end": v(16.95, 24.4) * mm});
            skLineSegment(sketch, "E2247", {"start": v(16.95, 24.4) * mm, "end": v(17.05, 24.3) * mm});
            skLineSegment(sketch, "E2248", {"start": v(17.05, 24.3) * mm, "end": v(17.14, 24.18) * mm});
            skLineSegment(sketch, "E2249", {"start": v(17.14, 24.18) * mm, "end": v(17.2, 24.05) * mm});
            skLineSegment(sketch, "E2250", {"start": v(17.2, 24.05) * mm, "end": v(17.25, 23.9) * mm});
            skLineSegment(sketch, "E2251", {"start": v(17.25, 23.9) * mm, "end": v(17.28, 23.78) * mm});
            skLineSegment(sketch, "E2252", {"start": v(17.28, 23.78) * mm, "end": v(17.36, 23.69) * mm});
            skLineSegment(sketch, "E2253", {"start": v(17.36, 23.69) * mm, "end": v(17.42, 23.59) * mm});
            skLineSegment(sketch, "E2254", {"start": v(17.42, 23.59) * mm, "end": v(17.47, 23.48) * mm});
            skLineSegment(sketch, "E2255", {"start": v(17.47, 23.48) * mm, "end": v(17.5, 23.37) * mm});
            skLineSegment(sketch, "E2256", {"start": v(17.5, 23.37) * mm, "end": v(17.5, 23.25) * mm});
            skLineSegment(sketch, "E2257", {"start": v(17.5, 23.25) * mm, "end": v(17.5, 4.42) * mm});
            skLineSegment(sketch, "E2258", {"start": v(17.5, 4.42) * mm, "end": v(17.57, 4.32) * mm});
            skLineSegment(sketch, "E2259", {"start": v(17.57, 4.32) * mm, "end": v(17.64, 4.18) * mm});
            skLineSegment(sketch, "E2260", {"start": v(17.64, 4.18) * mm, "end": v(17.69, 4.04) * mm});
            skLineSegment(sketch, "E2261", {"start": v(17.69, 4.04) * mm, "end": v(17.71, 3.9) * mm});
            skLineSegment(sketch, "E2262", {"start": v(17.71, 3.9) * mm, "end": v(17.71, 3.75) * mm});
            skLineSegment(sketch, "E2263", {"start": v(-22.86, -12.97) * mm, "end": v(-22.9, -13.24) * mm});
            skLineSegment(sketch, "E2264", {"start": v(-22.9, -13.24) * mm, "end": v(-22.95, -13.5) * mm});
            skLineSegment(sketch, "E2265", {"start": v(-22.95, -13.5) * mm, "end": v(-23.03, -13.77) * mm});
            skLineSegment(sketch, "E2266", {"start": v(-23.03, -13.77) * mm, "end": v(-23.14, -14.02) * mm});
            skLineSegment(sketch, "E2267", {"start": v(-23.14, -14.02) * mm, "end": v(-23.27, -14.25) * mm});
            skLineSegment(sketch, "E2268", {"start": v(-23.27, -14.25) * mm, "end": v(-23.43, -14.47) * mm});
            skLineSegment(sketch, "E2269", {"start": v(-23.43, -14.47) * mm, "end": v(-23.6, -14.68) * mm});
            skLineSegment(sketch, "E2270", {"start": v(-23.6, -14.68) * mm, "end": v(-23.8, -14.86) * mm});
            skLineSegment(sketch, "E2271", {"start": v(-23.8, -14.86) * mm, "end": v(-24.02, -15.02) * mm});
            skLineSegment(sketch, "E2272", {"start": v(-24.02, -15.02) * mm, "end": v(-24.25, -15.16) * mm});
            skLineSegment(sketch, "E2273", {"start": v(-24.25, -15.16) * mm, "end": v(-24.5, -15.28) * mm});
            skLineSegment(sketch, "E2274", {"start": v(-24.5, -15.28) * mm, "end": v(-24.75, -15.37) * mm});
            skLineSegment(sketch, "E2275", {"start": v(-24.75, -15.37) * mm, "end": v(-25.01, -15.44) * mm});
            skLineSegment(sketch, "E2276", {"start": v(-25.01, -15.44) * mm, "end": v(-25.28, -15.47) * mm});
            skLineSegment(sketch, "E2277", {"start": v(-25.28, -15.47) * mm, "end": v(-25.55, -15.48) * mm});
            skLineSegment(sketch, "E2278", {"start": v(-25.55, -15.48) * mm, "end": v(-25.82, -15.46) * mm});
            skLineSegment(sketch, "E2279", {"start": v(-25.82, -15.46) * mm, "end": v(-26.09, -15.42) * mm});
            skLineSegment(sketch, "E2280", {"start": v(-26.09, -15.42) * mm, "end": v(-26.35, -15.34) * mm});
            skLineSegment(sketch, "E2281", {"start": v(-26.35, -15.34) * mm, "end": v(-26.6, -15.24) * mm});
            skLineSegment(sketch, "E2282", {"start": v(-26.6, -15.24) * mm, "end": v(-26.84, -15.12) * mm});
            skLineSegment(sketch, "E2283", {"start": v(-26.84, -15.12) * mm, "end": v(-27.07, -14.97) * mm});
            skLineSegment(sketch, "E2284", {"start": v(-27.07, -14.97) * mm, "end": v(-27.28, -14.8) * mm});
            skLineSegment(sketch, "E2285", {"start": v(-27.28, -14.8) * mm, "end": v(-27.47, -14.6) * mm});
            skLineSegment(sketch, "E2286", {"start": v(-27.47, -14.6) * mm, "end": v(-27.64, -14.4) * mm});
            skLineSegment(sketch, "E2287", {"start": v(-27.64, -14.4) * mm, "end": v(-27.79, -14.17) * mm});
            skLineSegment(sketch, "E2288", {"start": v(-27.79, -14.17) * mm, "end": v(-27.9, -13.92) * mm});
            skLineSegment(sketch, "E2289", {"start": v(-27.9, -13.92) * mm, "end": v(-28, -13.67) * mm});
            skLineSegment(sketch, "E2290", {"start": v(-28, -13.67) * mm, "end": v(-28.08, -13.41) * mm});
            skLineSegment(sketch, "E2291", {"start": v(-28.08, -13.41) * mm, "end": v(-28.13, -13.14) * mm});
            skLineSegment(sketch, "E2292", {"start": v(-28.13, -13.14) * mm, "end": v(-28.14, -12.88) * mm});
            skLineSegment(sketch, "E2293", {"start": v(-28.14, -12.88) * mm, "end": v(-28.13, -12.6) * mm});
            skLineSegment(sketch, "E2294", {"start": v(-28.13, -12.6) * mm, "end": v(-28.1, -12.34) * mm});
            skLineSegment(sketch, "E2295", {"start": v(-28.1, -12.34) * mm, "end": v(-28.03, -12.07) * mm});
            skLineSegment(sketch, "E2296", {"start": v(-28.03, -12.07) * mm, "end": v(-27.94, -11.82) * mm});
            skLineSegment(sketch, "E2297", {"start": v(-27.94, -11.82) * mm, "end": v(-27.82, -11.57) * mm});
            skLineSegment(sketch, "E2298", {"start": v(-27.82, -11.57) * mm, "end": v(-27.68, -11.34) * mm});
            skLineSegment(sketch, "E2299", {"start": v(-27.68, -11.34) * mm, "end": v(-27.51, -11.13) * mm});
            skLineSegment(sketch, "E2300", {"start": v(-27.51, -11.13) * mm, "end": v(-27.33, -10.93) * mm});
            skLineSegment(sketch, "E2301", {"start": v(-27.33, -10.93) * mm, "end": v(-27.12, -10.75) * mm});
            skLineSegment(sketch, "E2302", {"start": v(-27.12, -10.75) * mm, "end": v(-26.9, -10.6) * mm});
            skLineSegment(sketch, "E2303", {"start": v(-26.9, -10.6) * mm, "end": v(-26.66, -10.47) * mm});
            skLineSegment(sketch, "E2304", {"start": v(-26.66, -10.47) * mm, "end": v(-26.42, -10.36) * mm});
            skLineSegment(sketch, "E2305", {"start": v(-26.42, -10.36) * mm, "end": v(-26.16, -10.28) * mm});
            skLineSegment(sketch, "E2306", {"start": v(-26.16, -10.28) * mm, "end": v(-25.9, -10.23) * mm});
            skLineSegment(sketch, "E2307", {"start": v(-25.9, -10.23) * mm, "end": v(-25.62, -10.2) * mm});
            skLineSegment(sketch, "E2308", {"start": v(-25.62, -10.2) * mm, "end": v(-25.35, -10.2) * mm});
            skLineSegment(sketch, "E2309", {"start": v(-25.35, -10.2) * mm, "end": v(-25.08, -10.23) * mm});
            skLineSegment(sketch, "E2310", {"start": v(-25.08, -10.23) * mm, "end": v(-24.82, -10.29) * mm});
            skLineSegment(sketch, "E2311", {"start": v(-24.82, -10.29) * mm, "end": v(-24.56, -10.37) * mm});
            skLineSegment(sketch, "E2312", {"start": v(-24.56, -10.37) * mm, "end": v(-24.31, -10.48) * mm});
            skLineSegment(sketch, "E2313", {"start": v(-24.31, -10.48) * mm, "end": v(-24.08, -10.61) * mm});
            skLineSegment(sketch, "E2314", {"start": v(-24.08, -10.61) * mm, "end": v(-23.86, -10.77) * mm});
            skLineSegment(sketch, "E2315", {"start": v(-23.86, -10.77) * mm, "end": v(-23.65, -10.95) * mm});
            skLineSegment(sketch, "E2316", {"start": v(-23.65, -10.95) * mm, "end": v(-23.47, -11.15) * mm});
            skLineSegment(sketch, "E2317", {"start": v(-23.47, -11.15) * mm, "end": v(-23.3, -11.37) * mm});
            skLineSegment(sketch, "E2318", {"start": v(-23.3, -11.37) * mm, "end": v(-23.17, -11.6) * mm});
            skLineSegment(sketch, "E2319", {"start": v(-23.17, -11.6) * mm, "end": v(-23.05, -11.84) * mm});
            skLineSegment(sketch, "E2320", {"start": v(-23.05, -11.84) * mm, "end": v(-22.96, -12.1) * mm});
            skLineSegment(sketch, "E2321", {"start": v(-22.96, -12.1) * mm, "end": v(-22.9, -12.36) * mm});
            skLineSegment(sketch, "E2322", {"start": v(-22.9, -12.36) * mm, "end": v(-22.87, -12.63) * mm});
            skLineSegment(sketch, "E2323", {"start": v(-22.87, -12.63) * mm, "end": v(-22.86, -12.84) * mm});
            skLineSegment(sketch, "E2324", {"start": v(-22.86, -12.84) * mm, "end": v(-22.86, -12.97) * mm});
            skLineSegment(sketch, "E2325", {"start": v(28.12, -12.87) * mm, "end": v(28.09, -13.14) * mm});
            skLineSegment(sketch, "E2326", {"start": v(28.09, -13.14) * mm, "end": v(28.03, -13.4) * mm});
            skLineSegment(sketch, "E2327", {"start": v(28.03, -13.4) * mm, "end": v(27.95, -13.67) * mm});
            skLineSegment(sketch, "E2328", {"start": v(27.95, -13.67) * mm, "end": v(27.84, -13.91) * mm});
            skLineSegment(sketch, "E2329", {"start": v(27.84, -13.91) * mm, "end": v(27.7, -14.15) * mm});
            skLineSegment(sketch, "E2330", {"start": v(27.7, -14.15) * mm, "end": v(27.55, -14.37) * mm});
            skLineSegment(sketch, "E2331", {"start": v(27.55, -14.37) * mm, "end": v(27.37, -14.57) * mm});
            skLineSegment(sketch, "E2332", {"start": v(27.37, -14.57) * mm, "end": v(27.18, -14.76) * mm});
            skLineSegment(sketch, "E2333", {"start": v(27.18, -14.76) * mm, "end": v(26.96, -14.92) * mm});
            skLineSegment(sketch, "E2334", {"start": v(26.96, -14.92) * mm, "end": v(26.73, -15.06) * mm});
            skLineSegment(sketch, "E2335", {"start": v(26.73, -15.06) * mm, "end": v(26.48, -15.18) * mm});
            skLineSegment(sketch, "E2336", {"start": v(26.48, -15.18) * mm, "end": v(26.23, -15.27) * mm});
            skLineSegment(sketch, "E2337", {"start": v(26.23, -15.27) * mm, "end": v(25.97, -15.33) * mm});
            skLineSegment(sketch, "E2338", {"start": v(25.97, -15.33) * mm, "end": v(25.7, -15.37) * mm});
            skLineSegment(sketch, "E2339", {"start": v(25.7, -15.37) * mm, "end": v(25.43, -15.38) * mm});
            skLineSegment(sketch, "E2340", {"start": v(25.43, -15.38) * mm, "end": v(25.16, -15.36) * mm});
            skLineSegment(sketch, "E2341", {"start": v(25.16, -15.36) * mm, "end": v(24.89, -15.31) * mm});
            skLineSegment(sketch, "E2342", {"start": v(24.89, -15.31) * mm, "end": v(24.63, -15.24) * mm});
            skLineSegment(sketch, "E2343", {"start": v(24.63, -15.24) * mm, "end": v(24.38, -15.14) * mm});
            skLineSegment(sketch, "E2344", {"start": v(24.38, -15.14) * mm, "end": v(24.14, -15.01) * mm});
            skLineSegment(sketch, "E2345", {"start": v(24.14, -15.01) * mm, "end": v(23.91, -14.86) * mm});
            skLineSegment(sketch, "E2346", {"start": v(23.91, -14.86) * mm, "end": v(23.7, -14.7) * mm});
            skLineSegment(sketch, "E2347", {"start": v(23.7, -14.7) * mm, "end": v(23.51, -14.5) * mm});
            skLineSegment(sketch, "E2348", {"start": v(23.51, -14.5) * mm, "end": v(23.34, -14.3) * mm});
            skLineSegment(sketch, "E2349", {"start": v(23.34, -14.3) * mm, "end": v(23.2, -14.06) * mm});
            skLineSegment(sketch, "E2350", {"start": v(23.2, -14.06) * mm, "end": v(23.07, -13.82) * mm});
            skLineSegment(sketch, "E2351", {"start": v(23.07, -13.82) * mm, "end": v(22.97, -13.57) * mm});
            skLineSegment(sketch, "E2352", {"start": v(22.97, -13.57) * mm, "end": v(22.9, -13.3) * mm});
            skLineSegment(sketch, "E2353", {"start": v(22.9, -13.3) * mm, "end": v(22.85, -13.04) * mm});
            skLineSegment(sketch, "E2354", {"start": v(22.85, -13.04) * mm, "end": v(22.83, -12.77) * mm});
            skLineSegment(sketch, "E2355", {"start": v(22.83, -12.77) * mm, "end": v(22.84, -12.5) * mm});
            skLineSegment(sketch, "E2356", {"start": v(22.84, -12.5) * mm, "end": v(22.88, -12.24) * mm});
            skLineSegment(sketch, "E2357", {"start": v(22.88, -12.24) * mm, "end": v(22.95, -11.97) * mm});
            skLineSegment(sketch, "E2358", {"start": v(22.95, -11.97) * mm, "end": v(23.04, -11.72) * mm});
            skLineSegment(sketch, "E2359", {"start": v(23.04, -11.72) * mm, "end": v(23.16, -11.47) * mm});
            skLineSegment(sketch, "E2360", {"start": v(23.16, -11.47) * mm, "end": v(23.3, -11.24) * mm});
            skLineSegment(sketch, "E2361", {"start": v(23.3, -11.24) * mm, "end": v(23.46, -11.03) * mm});
            skLineSegment(sketch, "E2362", {"start": v(23.46, -11.03) * mm, "end": v(23.65, -10.83) * mm});
            skLineSegment(sketch, "E2363", {"start": v(23.65, -10.83) * mm, "end": v(23.86, -10.65) * mm});
            skLineSegment(sketch, "E2364", {"start": v(23.86, -10.65) * mm, "end": v(24.08, -10.5) * mm});
            skLineSegment(sketch, "E2365", {"start": v(24.08, -10.5) * mm, "end": v(24.31, -10.37) * mm});
            skLineSegment(sketch, "E2366", {"start": v(24.31, -10.37) * mm, "end": v(24.56, -10.26) * mm});
            skLineSegment(sketch, "E2367", {"start": v(24.56, -10.26) * mm, "end": v(24.82, -10.18) * mm});
            skLineSegment(sketch, "E2368", {"start": v(24.82, -10.18) * mm, "end": v(25.09, -10.12) * mm});
            skLineSegment(sketch, "E2369", {"start": v(25.09, -10.12) * mm, "end": v(25.36, -10.1) * mm});
            skLineSegment(sketch, "E2370", {"start": v(25.36, -10.1) * mm, "end": v(25.63, -10.1) * mm});
            skLineSegment(sketch, "E2371", {"start": v(25.63, -10.1) * mm, "end": v(25.9, -10.13) * mm});
            skLineSegment(sketch, "E2372", {"start": v(25.9, -10.13) * mm, "end": v(26.16, -10.19) * mm});
            skLineSegment(sketch, "E2373", {"start": v(26.16, -10.19) * mm, "end": v(26.42, -10.27) * mm});
            skLineSegment(sketch, "E2374", {"start": v(26.42, -10.27) * mm, "end": v(26.66, -10.38) * mm});
            skLineSegment(sketch, "E2375", {"start": v(26.66, -10.38) * mm, "end": v(26.9, -10.51) * mm});
            skLineSegment(sketch, "E2376", {"start": v(26.9, -10.51) * mm, "end": v(27.12, -10.67) * mm});
            skLineSegment(sketch, "E2377", {"start": v(27.12, -10.67) * mm, "end": v(27.33, -10.85) * mm});
            skLineSegment(sketch, "E2378", {"start": v(27.33, -10.85) * mm, "end": v(27.5, -11.05) * mm});
            skLineSegment(sketch, "E2379", {"start": v(27.5, -11.05) * mm, "end": v(27.67, -11.26) * mm});
            skLineSegment(sketch, "E2380", {"start": v(27.67, -11.26) * mm, "end": v(27.81, -11.5) * mm});
            skLineSegment(sketch, "E2381", {"start": v(27.81, -11.5) * mm, "end": v(27.92, -11.74) * mm});
            skLineSegment(sketch, "E2382", {"start": v(27.92, -11.74) * mm, "end": v(28.01, -12) * mm});
            skLineSegment(sketch, "E2383", {"start": v(28.01, -12) * mm, "end": v(28.07, -12.26) * mm});
            skLineSegment(sketch, "E2384", {"start": v(28.07, -12.26) * mm, "end": v(28.11, -12.53) * mm});
            skLineSegment(sketch, "E2385", {"start": v(28.11, -12.53) * mm, "end": v(28.12, -12.74) * mm});
            skLineSegment(sketch, "E2386", {"start": v(28.12, -12.74) * mm, "end": v(28.12, -12.87) * mm});
            skLineSegment(sketch, "E2387", {"start": v(-12.88, -6.4) * mm, "end": v(-12.98, -6.45) * mm});
            skLineSegment(sketch, "E2388", {"start": v(-12.98, -6.45) * mm, "end": v(-13.1, -6.47) * mm});
            skLineSegment(sketch, "E2389", {"start": v(-13.1, -6.47) * mm, "end": v(-13.2, -6.47) * mm});
            skLineSegment(sketch, "E2390", {"start": v(-13.2, -6.47) * mm, "end": v(-13.31, -6.44) * mm});
            skLineSegment(sketch, "E2391", {"start": v(-13.31, -6.44) * mm, "end": v(-13.41, -6.38) * mm});
            skLineSegment(sketch, "E2392", {"start": v(-13.41, -6.38) * mm, "end": v(-13.5, -6.3) * mm});
            skLineSegment(sketch, "E2393", {"start": v(-13.5, -6.3) * mm, "end": v(-13.56, -6.21) * mm});
            skLineSegment(sketch, "E2394", {"start": v(-13.56, -6.21) * mm, "end": v(-13.6, -6.1) * mm});
            skLineSegment(sketch, "E2395", {"start": v(-13.6, -6.1) * mm, "end": v(-13.61, -6) * mm});
            skLineSegment(sketch, "E2396", {"start": v(-13.61, -6) * mm, "end": v(-13.6, -5.88) * mm});
            skLineSegment(sketch, "E2397", {"start": v(-13.6, -5.88) * mm, "end": v(-13.56, -5.77) * mm});
            skLineSegment(sketch, "E2398", {"start": v(-13.56, -5.77) * mm, "end": v(-13.5, -5.68) * mm});
            skLineSegment(sketch, "E2399", {"start": v(-13.5, -5.68) * mm, "end": v(-13.41, -5.6) * mm});
            skLineSegment(sketch, "E2400", {"start": v(-13.41, -5.6) * mm, "end": v(-13.31, -5.55) * mm});
            skLineSegment(sketch, "E2401", {"start": v(-13.31, -5.55) * mm, "end": v(-13.2, -5.52) * mm});
            skLineSegment(sketch, "E2402", {"start": v(-13.2, -5.52) * mm, "end": v(-13.1, -5.51) * mm});
            skLineSegment(sketch, "E2403", {"start": v(-13.1, -5.51) * mm, "end": v(-12.98, -5.53) * mm});
            skLineSegment(sketch, "E2404", {"start": v(-12.98, -5.53) * mm, "end": v(-12.88, -5.58) * mm});
            skLineSegment(sketch, "E2405", {"start": v(-12.88, -5.58) * mm, "end": v(-12.79, -5.65) * mm});
            skLineSegment(sketch, "E2406", {"start": v(-12.79, -5.65) * mm, "end": v(-12.72, -5.74) * mm});
            skLineSegment(sketch, "E2407", {"start": v(-12.72, -5.74) * mm, "end": v(-12.67, -5.84) * mm});
            skLineSegment(sketch, "E2408", {"start": v(-12.67, -5.84) * mm, "end": v(-12.65, -5.96) * mm});
            skLineSegment(sketch, "E2409", {"start": v(-12.65, -5.96) * mm, "end": v(-12.65, -6.03) * mm});
            skLineSegment(sketch, "E2410", {"start": v(-15.42, -6.4) * mm, "end": v(-15.52, -6.45) * mm});
            skLineSegment(sketch, "E2411", {"start": v(-15.52, -6.45) * mm, "end": v(-15.63, -6.47) * mm});
            skLineSegment(sketch, "E2412", {"start": v(-15.63, -6.47) * mm, "end": v(-15.75, -6.47) * mm});
            skLineSegment(sketch, "E2413", {"start": v(-15.75, -6.47) * mm, "end": v(-15.85, -6.44) * mm});
            skLineSegment(sketch, "E2414", {"start": v(-15.85, -6.44) * mm, "end": v(-15.95, -6.38) * mm});
            skLineSegment(sketch, "E2415", {"start": v(-15.95, -6.38) * mm, "end": v(-16.04, -6.3) * mm});
            skLineSegment(sketch, "E2416", {"start": v(-16.04, -6.3) * mm, "end": v(-16.1, -6.21) * mm});
            skLineSegment(sketch, "E2417", {"start": v(-16.1, -6.21) * mm, "end": v(-16.14, -6.1) * mm});
            skLineSegment(sketch, "E2418", {"start": v(-16.14, -6.1) * mm, "end": v(-16.15, -6) * mm});
            skLineSegment(sketch, "E2419", {"start": v(-16.15, -6) * mm, "end": v(-16.14, -5.88) * mm});
            skLineSegment(sketch, "E2420", {"start": v(-16.14, -5.88) * mm, "end": v(-16.1, -5.77) * mm});
            skLineSegment(sketch, "E2421", {"start": v(-16.1, -5.77) * mm, "end": v(-16.04, -5.68) * mm});
            skLineSegment(sketch, "E2422", {"start": v(-16.04, -5.68) * mm, "end": v(-15.95, -5.6) * mm});
            skLineSegment(sketch, "E2423", {"start": v(-15.95, -5.6) * mm, "end": v(-15.85, -5.55) * mm});
            skLineSegment(sketch, "E2424", {"start": v(-15.85, -5.55) * mm, "end": v(-15.75, -5.52) * mm});
            skLineSegment(sketch, "E2425", {"start": v(-15.75, -5.52) * mm, "end": v(-15.63, -5.51) * mm});
            skLineSegment(sketch, "E2426", {"start": v(-15.63, -5.51) * mm, "end": v(-15.52, -5.53) * mm});
            skLineSegment(sketch, "E2427", {"start": v(-15.52, -5.53) * mm, "end": v(-15.42, -5.58) * mm});
            skLineSegment(sketch, "E2428", {"start": v(-15.42, -5.58) * mm, "end": v(-15.33, -5.65) * mm});
            skLineSegment(sketch, "E2429", {"start": v(-15.33, -5.65) * mm, "end": v(-15.26, -5.74) * mm});
            skLineSegment(sketch, "E2430", {"start": v(-15.26, -5.74) * mm, "end": v(-15.21, -5.84) * mm});
            skLineSegment(sketch, "E2431", {"start": v(-15.21, -5.84) * mm, "end": v(-15.19, -5.96) * mm});
            skLineSegment(sketch, "E2432", {"start": v(-15.19, -5.96) * mm, "end": v(-15.19, -6.03) * mm});
            skLineSegment(sketch, "E2433", {"start": v(18.09, -0.41) * mm, "end": v(18.05, -0.3) * mm});
            skLineSegment(sketch, "E2434", {"start": v(18.05, -0.3) * mm, "end": v(18.04, -0.2) * mm});
            skLineSegment(sketch, "E2435", {"start": v(18.04, -0.2) * mm, "end": v(18.05, -0.08) * mm});
            skLineSegment(sketch, "E2436", {"start": v(18.05, -0.08) * mm, "end": v(18.09, 0.03) * mm});
            skLineSegment(sketch, "E2437", {"start": v(18.09, 0.03) * mm, "end": v(18.15, 0.12) * mm});
            skLineSegment(sketch, "E2438", {"start": v(18.15, 0.12) * mm, "end": v(18.24, 0.2) * mm});
            skLineSegment(sketch, "E2439", {"start": v(18.24, 0.2) * mm, "end": v(18.34, 0.25) * mm});
            skLineSegment(sketch, "E2440", {"start": v(18.34, 0.25) * mm, "end": v(18.45, 0.28) * mm});
            skLineSegment(sketch, "E2441", {"start": v(18.45, 0.28) * mm, "end": v(18.56, 0.29) * mm});
            skLineSegment(sketch, "E2442", {"start": v(18.56, 0.29) * mm, "end": v(18.67, 0.27) * mm});
            skLineSegment(sketch, "E2443", {"start": v(18.67, 0.27) * mm, "end": v(18.77, 0.22) * mm});
            skLineSegment(sketch, "E2444", {"start": v(18.77, 0.22) * mm, "end": v(18.86, 0.15) * mm});
            skLineSegment(sketch, "E2445", {"start": v(18.86, 0.15) * mm, "end": v(18.93, 0.06) * mm});
            skLineSegment(sketch, "E2446", {"start": v(18.93, 0.06) * mm, "end": v(18.98, -0.04) * mm});
            skLineSegment(sketch, "E2447", {"start": v(18.98, -0.04) * mm, "end": v(19, -0.15) * mm});
            skLineSegment(sketch, "E2448", {"start": v(19, -0.15) * mm, "end": v(19, -0.23) * mm});
            skLineSegment(sketch, "E2449", {"start": v(5.17, -2.96) * mm, "end": v(5.06, -2.98) * mm});
            skLineSegment(sketch, "E2450", {"start": v(5.06, -2.98) * mm, "end": v(4.95, -2.98) * mm});
            skLineSegment(sketch, "E2451", {"start": v(4.95, -2.98) * mm, "end": v(4.84, -2.95) * mm});
            skLineSegment(sketch, "E2452", {"start": v(4.84, -2.95) * mm, "end": v(4.74, -2.9) * mm});
            skLineSegment(sketch, "E2453", {"start": v(4.74, -2.9) * mm, "end": v(4.65, -2.81) * mm});
            skLineSegment(sketch, "E2454", {"start": v(4.65, -2.81) * mm, "end": v(4.59, -2.72) * mm});
            skLineSegment(sketch, "E2455", {"start": v(4.59, -2.72) * mm, "end": v(4.55, -2.61) * mm});
            skLineSegment(sketch, "E2456", {"start": v(4.55, -2.61) * mm, "end": v(4.54, -2.5) * mm});
            skLineSegment(sketch, "E2457", {"start": v(4.54, -2.5) * mm, "end": v(4.55, -2.39) * mm});
            skLineSegment(sketch, "E2458", {"start": v(4.55, -2.39) * mm, "end": v(4.59, -2.28) * mm});
            skLineSegment(sketch, "E2459", {"start": v(4.59, -2.28) * mm, "end": v(4.65, -2.19) * mm});
            skLineSegment(sketch, "E2460", {"start": v(4.65, -2.19) * mm, "end": v(4.74, -2.11) * mm});
            skLineSegment(sketch, "E2461", {"start": v(4.74, -2.11) * mm, "end": v(4.84, -2.05) * mm});
            skLineSegment(sketch, "E2462", {"start": v(4.84, -2.05) * mm, "end": v(4.95, -2.02) * mm});
            skLineSegment(sketch, "E2463", {"start": v(4.95, -2.02) * mm, "end": v(5.06, -2.02) * mm});
            skLineSegment(sketch, "E2464", {"start": v(5.06, -2.02) * mm, "end": v(5.17, -2.04) * mm});
            skLineSegment(sketch, "E2465", {"start": v(5.17, -2.04) * mm, "end": v(5.27, -2.09) * mm});
            skLineSegment(sketch, "E2466", {"start": v(5.27, -2.09) * mm, "end": v(5.36, -2.16) * mm});
            skLineSegment(sketch, "E2467", {"start": v(5.36, -2.16) * mm, "end": v(5.43, -2.25) * mm});
            skLineSegment(sketch, "E2468", {"start": v(5.43, -2.25) * mm, "end": v(5.48, -2.35) * mm});
            skLineSegment(sketch, "E2469", {"start": v(5.48, -2.35) * mm, "end": v(5.5, -2.46) * mm});
            skLineSegment(sketch, "E2470", {"start": v(5.5, -2.46) * mm, "end": v(5.5, -2.54) * mm});
            skLineSegment(sketch, "E2471", {"start": v(5.02, -4.27) * mm, "end": v(4.94, -4.2) * mm});
            skLineSegment(sketch, "E2472", {"start": v(4.94, -4.2) * mm, "end": v(4.87, -4.1) * mm});
            skLineSegment(sketch, "E2473", {"start": v(4.87, -4.1) * mm, "end": v(4.83, -4) * mm});
            skLineSegment(sketch, "E2474", {"start": v(4.83, -4) * mm, "end": v(4.82, -3.88) * mm});
            skLineSegment(sketch, "E2475", {"start": v(-4.33, 0.9) * mm, "end": v(-4.35, 0.8) * mm});
            skLineSegment(sketch, "E2476", {"start": v(-4.35, 0.8) * mm, "end": v(-4.4, 0.7) * mm});
            skLineSegment(sketch, "E2477", {"start": v(-4.4, 0.7) * mm, "end": v(-4.47, 0.6) * mm});
            skLineSegment(sketch, "E2478", {"start": v(-4.47, 0.6) * mm, "end": v(-4.56, 0.54) * mm});
            skLineSegment(sketch, "E2479", {"start": v(-4.56, 0.54) * mm, "end": v(-4.66, 0.49) * mm});
            skLineSegment(sketch, "E2480", {"start": v(-4.33, 0.99) * mm, "end": v(-4.33, 0.9) * mm});
            skLineSegment(sketch, "E2481", {"start": v(6, 3.03) * mm, "end": v(5.89, 3.03) * mm});
            skLineSegment(sketch, "E2482", {"start": v(5.89, 3.03) * mm, "end": v(5.78, 3.06) * mm});
            skLineSegment(sketch, "E2483", {"start": v(5.78, 3.06) * mm, "end": v(5.68, 3.12) * mm});
            skLineSegment(sketch, "E2484", {"start": v(5.68, 3.12) * mm, "end": v(5.6, 3.2) * mm});
            skLineSegment(sketch, "E2485", {"start": v(5.6, 3.2) * mm, "end": v(5.53, 3.29) * mm});
            skLineSegment(sketch, "E2486", {"start": v(9.04, 3.06) * mm, "end": v(8.94, 3) * mm});
            skLineSegment(sketch, "E2487", {"start": v(8.94, 3) * mm, "end": v(8.82, 2.99) * mm});
            skLineSegment(sketch, "E2488", {"start": v(8.82, 2.99) * mm, "end": v(8.71, 3) * mm});
            skLineSegment(sketch, "E2489", {"start": v(8.71, 3) * mm, "end": v(8.6, 3.03) * mm});
            skLineSegment(sketch, "E2490", {"start": v(8.6, 3.03) * mm, "end": v(8.5, 3.08) * mm});
            skLineSegment(sketch, "E2491", {"start": v(5.86, 0.7) * mm, "end": v(5.77, 0.77) * mm});
            skLineSegment(sketch, "E2492", {"start": v(5.77, 0.77) * mm, "end": v(5.7, 0.87) * mm});
            skLineSegment(sketch, "E2493", {"start": v(5.7, 0.87) * mm, "end": v(5.67, 0.97) * mm});
            skLineSegment(sketch, "E2494", {"start": v(5.67, 0.97) * mm, "end": v(5.66, 1.09) * mm});
            skLineSegment(sketch, "E2495", {"start": v(5.66, 1.09) * mm, "end": v(5.67, 1.2) * mm});
            skLineSegment(sketch, "E2496", {"start": v(5.67, 1.2) * mm, "end": v(5.7, 1.3) * mm});
            skLineSegment(sketch, "E2497", {"start": v(5.7, 1.3) * mm, "end": v(5.77, 1.4) * mm});
            skLineSegment(sketch, "E2498", {"start": v(5.77, 1.4) * mm, "end": v(5.86, 1.48) * mm});
            skLineSegment(sketch, "E2499", {"start": v(5.86, 1.48) * mm, "end": v(5.96, 1.53) * mm});
            skLineSegment(sketch, "E2500", {"start": v(5.96, 1.53) * mm, "end": v(6.07, 1.56) * mm});
            skLineSegment(sketch, "E2501", {"start": v(6.07, 1.56) * mm, "end": v(6.18, 1.57) * mm});
            skLineSegment(sketch, "E2502", {"start": v(6.18, 1.57) * mm, "end": v(6.29, 1.55) * mm});
            skLineSegment(sketch, "E2503", {"start": v(6.29, 1.55) * mm, "end": v(6.4, 1.5) * mm});
            skLineSegment(sketch, "E2504", {"start": v(6.4, 1.5) * mm, "end": v(6.48, 1.43) * mm});
            skLineSegment(sketch, "E2505", {"start": v(6.48, 1.43) * mm, "end": v(6.55, 1.34) * mm});
            skLineSegment(sketch, "E2506", {"start": v(6.55, 1.34) * mm, "end": v(6.6, 1.24) * mm});
            skLineSegment(sketch, "E2507", {"start": v(6.6, 1.24) * mm, "end": v(6.62, 1.13) * mm});
            skLineSegment(sketch, "E2508", {"start": v(6.62, 1.13) * mm, "end": v(6.62, 1.05) * mm});
            skLineSegment(sketch, "E2509", {"start": v(15.6, -5.64) * mm, "end": v(15.6, -6.6) * mm});
            skLineSegment(sketch, "E2510", {"start": v(15.6, -6.6) * mm, "end": v(14.64, -6.6) * mm});
            skLineSegment(sketch, "E2511", {"start": v(8.46, -5.7) * mm, "end": v(8.46, -6.66) * mm});
            skLineSegment(sketch, "E2512", {"start": v(30.11, -22.74) * mm, "end": v(31.88, -22.74) * mm});
            skLineSegment(sketch, "E2513", {"start": v(29.98, -24.64) * mm, "end": v(29.98, -22.74) * mm});
            skLineSegment(sketch, "E2514", {"start": v(29.98, -22.74) * mm, "end": v(30.11, -22.74) * mm});
            skLineSegment(sketch, "E2515", {"start": v(27.58, -23.2) * mm, "end": v(27.67, -23.07) * mm});
            skLineSegment(sketch, "E2516", {"start": v(27.67, -23.07) * mm, "end": v(27.77, -22.97) * mm});
            skLineSegment(sketch, "E2517", {"start": v(27.77, -22.97) * mm, "end": v(27.9, -22.88) * mm});
            skLineSegment(sketch, "E2518", {"start": v(27.9, -22.88) * mm, "end": v(28.03, -22.81) * mm});
            skLineSegment(sketch, "E2519", {"start": v(25.04, -23.2) * mm, "end": v(25.13, -23.07) * mm});
            skLineSegment(sketch, "E2520", {"start": v(25.13, -23.07) * mm, "end": v(25.23, -22.97) * mm});
            skLineSegment(sketch, "E2521", {"start": v(25.23, -22.97) * mm, "end": v(25.35, -22.88) * mm});
            skLineSegment(sketch, "E2522", {"start": v(25.35, -22.88) * mm, "end": v(25.49, -22.81) * mm});
            skLineSegment(sketch, "E2523", {"start": v(24.26, -23.76) * mm, "end": v(24.23, -23.91) * mm});
            skLineSegment(sketch, "E2524", {"start": v(24.23, -23.91) * mm, "end": v(24.19, -24.05) * mm});
            skLineSegment(sketch, "E2525", {"start": v(24.19, -24.05) * mm, "end": v(24.12, -24.19) * mm});
            skLineSegment(sketch, "E2526", {"start": v(24.12, -24.19) * mm, "end": v(24.03, -24.3) * mm});
            skLineSegment(sketch, "E2527", {"start": v(24.03, -24.3) * mm, "end": v(23.93, -24.41) * mm});
            skLineSegment(sketch, "E2528", {"start": v(23.93, -24.41) * mm, "end": v(23.8, -24.5) * mm});
            skLineSegment(sketch, "E2529", {"start": v(23.8, -24.5) * mm, "end": v(23.68, -24.57) * mm});
            skLineSegment(sketch, "E2530", {"start": v(23.68, -24.57) * mm, "end": v(23.53, -24.62) * mm});
            skLineSegment(sketch, "E2531", {"start": v(23.53, -24.62) * mm, "end": v(23.39, -24.64) * mm});
            skLineSegment(sketch, "E2532", {"start": v(23.39, -24.64) * mm, "end": v(23.24, -24.64) * mm});
            skLineSegment(sketch, "E2533", {"start": v(23.24, -24.64) * mm, "end": v(23.09, -24.62) * mm});
            skLineSegment(sketch, "E2534", {"start": v(23.09, -24.62) * mm, "end": v(22.95, -24.57) * mm});
            skLineSegment(sketch, "E2535", {"start": v(22.95, -24.57) * mm, "end": v(22.81, -24.5) * mm});
            skLineSegment(sketch, "E2536", {"start": v(22.81, -24.5) * mm, "end": v(22.7, -24.41) * mm});
            skLineSegment(sketch, "E2537", {"start": v(22.7, -24.41) * mm, "end": v(22.59, -24.3) * mm});
            skLineSegment(sketch, "E2538", {"start": v(22.59, -24.3) * mm, "end": v(22.5, -24.19) * mm});
            skLineSegment(sketch, "E2539", {"start": v(22.5, -24.19) * mm, "end": v(22.43, -24.05) * mm});
            skLineSegment(sketch, "E2540", {"start": v(22.43, -24.05) * mm, "end": v(22.39, -23.91) * mm});
            skLineSegment(sketch, "E2541", {"start": v(22.39, -23.91) * mm, "end": v(22.36, -23.76) * mm});
            skLineSegment(sketch, "E2542", {"start": v(22.36, -23.76) * mm, "end": v(22.36, -23.61) * mm});
            skLineSegment(sketch, "E2543", {"start": v(22.36, -23.61) * mm, "end": v(22.39, -23.47) * mm});
            skLineSegment(sketch, "E2544", {"start": v(22.39, -23.47) * mm, "end": v(22.43, -23.32) * mm});
            skLineSegment(sketch, "E2545", {"start": v(22.43, -23.32) * mm, "end": v(22.5, -23.2) * mm});
            skLineSegment(sketch, "E2546", {"start": v(22.5, -23.2) * mm, "end": v(22.59, -23.07) * mm});
            skLineSegment(sketch, "E2547", {"start": v(22.59, -23.07) * mm, "end": v(22.7, -22.97) * mm});
            skLineSegment(sketch, "E2548", {"start": v(22.7, -22.97) * mm, "end": v(22.81, -22.88) * mm});
            skLineSegment(sketch, "E2549", {"start": v(22.81, -22.88) * mm, "end": v(22.95, -22.81) * mm});
            skLineSegment(sketch, "E2550", {"start": v(22.95, -22.81) * mm, "end": v(23.09, -22.76) * mm});
            skLineSegment(sketch, "E2551", {"start": v(23.09, -22.76) * mm, "end": v(23.24, -22.74) * mm});
            skLineSegment(sketch, "E2552", {"start": v(23.24, -22.74) * mm, "end": v(23.39, -22.74) * mm});
            skLineSegment(sketch, "E2553", {"start": v(23.39, -22.74) * mm, "end": v(23.53, -22.76) * mm});
            skLineSegment(sketch, "E2554", {"start": v(23.53, -22.76) * mm, "end": v(23.68, -22.81) * mm});
            skLineSegment(sketch, "E2555", {"start": v(23.68, -22.81) * mm, "end": v(23.8, -22.88) * mm});
            skLineSegment(sketch, "E2556", {"start": v(23.8, -22.88) * mm, "end": v(23.93, -22.97) * mm});
            skLineSegment(sketch, "E2557", {"start": v(23.93, -22.97) * mm, "end": v(24.03, -23.07) * mm});
            skLineSegment(sketch, "E2558", {"start": v(24.03, -23.07) * mm, "end": v(24.12, -23.2) * mm});
            skLineSegment(sketch, "E2559", {"start": v(24.12, -23.2) * mm, "end": v(24.19, -23.32) * mm});
            skLineSegment(sketch, "E2560", {"start": v(24.19, -23.32) * mm, "end": v(24.23, -23.47) * mm});
            skLineSegment(sketch, "E2561", {"start": v(24.23, -23.47) * mm, "end": v(24.26, -23.61) * mm});
            skLineSegment(sketch, "E2562", {"start": v(24.26, -23.61) * mm, "end": v(24.26, -23.76) * mm});
            skLineSegment(sketch, "E2563", {"start": v(19.96, -23.2) * mm, "end": v(20.05, -23.07) * mm});
            skLineSegment(sketch, "E2564", {"start": v(20.05, -23.07) * mm, "end": v(20.15, -22.97) * mm});
            skLineSegment(sketch, "E2565", {"start": v(20.15, -22.97) * mm, "end": v(20.27, -22.88) * mm});
            skLineSegment(sketch, "E2566", {"start": v(20.27, -22.88) * mm, "end": v(20.4, -22.81) * mm});
            skLineSegment(sketch, "E2567", {"start": v(17.42, -23.2) * mm, "end": v(17.5, -23.07) * mm});
            skLineSegment(sketch, "E2568", {"start": v(17.5, -23.07) * mm, "end": v(17.61, -22.97) * mm});
            skLineSegment(sketch, "E2569", {"start": v(17.61, -22.97) * mm, "end": v(17.73, -22.88) * mm});
            skLineSegment(sketch, "E2570", {"start": v(17.73, -22.88) * mm, "end": v(17.87, -22.81) * mm});
            skLineSegment(sketch, "E2571", {"start": v(14.88, -23.2) * mm, "end": v(14.97, -23.07) * mm});
            skLineSegment(sketch, "E2572", {"start": v(14.97, -23.07) * mm, "end": v(15.07, -22.97) * mm});
            skLineSegment(sketch, "E2573", {"start": v(15.07, -22.97) * mm, "end": v(15.2, -22.88) * mm});
            skLineSegment(sketch, "E2574", {"start": v(15.2, -22.88) * mm, "end": v(15.33, -22.81) * mm});
            skLineSegment(sketch, "E2575", {"start": v(12.27, -23.32) * mm, "end": v(12.34, -23.2) * mm});
            skLineSegment(sketch, "E2576", {"start": v(12.34, -23.2) * mm, "end": v(12.43, -23.07) * mm});
            skLineSegment(sketch, "E2577", {"start": v(12.43, -23.07) * mm, "end": v(12.53, -22.97) * mm});
            skLineSegment(sketch, "E2578", {"start": v(9.8, -23.2) * mm, "end": v(9.89, -23.07) * mm});
            skLineSegment(sketch, "E2579", {"start": v(9.89, -23.07) * mm, "end": v(10, -22.97) * mm});
            skLineSegment(sketch, "E2580", {"start": v(10, -22.97) * mm, "end": v(10.11, -22.88) * mm});
            skLineSegment(sketch, "E2581", {"start": v(10.11, -22.88) * mm, "end": v(10.25, -22.81) * mm});
            skLineSegment(sketch, "E2582", {"start": v(7.26, -23.2) * mm, "end": v(7.35, -23.07) * mm});
            skLineSegment(sketch, "E2583", {"start": v(7.35, -23.07) * mm, "end": v(7.45, -22.97) * mm});
            skLineSegment(sketch, "E2584", {"start": v(7.45, -22.97) * mm, "end": v(7.57, -22.88) * mm});
            skLineSegment(sketch, "E2585", {"start": v(7.57, -22.88) * mm, "end": v(7.7, -22.81) * mm});
            skLineSegment(sketch, "E2586", {"start": v(4.72, -23.2) * mm, "end": v(4.8, -23.07) * mm});
            skLineSegment(sketch, "E2587", {"start": v(4.8, -23.07) * mm, "end": v(4.91, -22.97) * mm});
            skLineSegment(sketch, "E2588", {"start": v(4.91, -22.97) * mm, "end": v(5.03, -22.88) * mm});
            skLineSegment(sketch, "E2589", {"start": v(5.03, -22.88) * mm, "end": v(5.17, -22.81) * mm});
            skLineSegment(sketch, "E2590", {"start": v(5.17, -22.81) * mm, "end": v(5.3, -22.76) * mm});
            skLineSegment(sketch, "E2591", {"start": v(5.3, -22.76) * mm, "end": v(5.46, -22.74) * mm});
            skLineSegment(sketch, "E2592", {"start": v(5.46, -22.74) * mm, "end": v(5.6, -22.74) * mm});
            skLineSegment(sketch, "E2593", {"start": v(5.6, -22.74) * mm, "end": v(5.75, -22.76) * mm});
            skLineSegment(sketch, "E2594", {"start": v(5.75, -22.76) * mm, "end": v(5.9, -22.81) * mm});
            skLineSegment(sketch, "E2595", {"start": v(5.9, -22.81) * mm, "end": v(6.03, -22.88) * mm});
            skLineSegment(sketch, "E2596", {"start": v(6.03, -22.88) * mm, "end": v(6.15, -22.97) * mm});
            skLineSegment(sketch, "E2597", {"start": v(6.15, -22.97) * mm, "end": v(6.25, -23.07) * mm});
            skLineSegment(sketch, "E2598", {"start": v(6.25, -23.07) * mm, "end": v(6.34, -23.2) * mm});
            skLineSegment(sketch, "E2599", {"start": v(6.34, -23.2) * mm, "end": v(6.4, -23.32) * mm});
            skLineSegment(sketch, "E2600", {"start": v(6.4, -23.32) * mm, "end": v(6.45, -23.47) * mm});
            skLineSegment(sketch, "E2601", {"start": v(6.45, -23.47) * mm, "end": v(6.48, -23.61) * mm});
            skLineSegment(sketch, "E2602", {"start": v(6.48, -23.61) * mm, "end": v(6.48, -23.76) * mm});
            skLineSegment(sketch, "E2603", {"start": v(2.18, -23.2) * mm, "end": v(2.27, -23.07) * mm});
            skLineSegment(sketch, "E2604", {"start": v(2.27, -23.07) * mm, "end": v(2.37, -22.97) * mm});
            skLineSegment(sketch, "E2605", {"start": v(2.37, -22.97) * mm, "end": v(2.5, -22.88) * mm});
            skLineSegment(sketch, "E2606", {"start": v(2.5, -22.88) * mm, "end": v(2.63, -22.81) * mm});
            skLineSegment(sketch, "E2607", {"start": v(2.63, -22.81) * mm, "end": v(2.77, -22.76) * mm});
            skLineSegment(sketch, "E2608", {"start": v(2.77, -22.76) * mm, "end": v(2.92, -22.74) * mm});
            skLineSegment(sketch, "E2609", {"start": v(2.92, -22.74) * mm, "end": v(3.07, -22.74) * mm});
            skLineSegment(sketch, "E2610", {"start": v(3.07, -22.74) * mm, "end": v(3.21, -22.76) * mm});
            skLineSegment(sketch, "E2611", {"start": v(3.21, -22.76) * mm, "end": v(3.36, -22.81) * mm});
            skLineSegment(sketch, "E2612", {"start": v(3.36, -22.81) * mm, "end": v(3.49, -22.88) * mm});
            skLineSegment(sketch, "E2613", {"start": v(3.49, -22.88) * mm, "end": v(3.6, -22.97) * mm});
            skLineSegment(sketch, "E2614", {"start": v(3.6, -22.97) * mm, "end": v(3.71, -23.07) * mm});
            skLineSegment(sketch, "E2615", {"start": v(3.71, -23.07) * mm, "end": v(3.8, -23.2) * mm});
            skLineSegment(sketch, "E2616", {"start": v(3.8, -23.2) * mm, "end": v(3.87, -23.32) * mm});
            skLineSegment(sketch, "E2617", {"start": v(3.87, -23.32) * mm, "end": v(3.91, -23.47) * mm});
            skLineSegment(sketch, "E2618", {"start": v(3.91, -23.47) * mm, "end": v(3.94, -23.61) * mm});
            skLineSegment(sketch, "E2619", {"start": v(3.94, -23.61) * mm, "end": v(3.94, -23.76) * mm});
            skLineSegment(sketch, "E2620", {"start": v(-0.36, -23.2) * mm, "end": v(-0.27, -23.07) * mm});
            skLineSegment(sketch, "E2621", {"start": v(-0.27, -23.07) * mm, "end": v(-0.17, -22.97) * mm});
            skLineSegment(sketch, "E2622", {"start": v(-0.17, -22.97) * mm, "end": v(-0.05, -22.88) * mm});
            skLineSegment(sketch, "E2623", {"start": v(-0.05, -22.88) * mm, "end": v(0.09, -22.81) * mm});
            skLineSegment(sketch, "E2624", {"start": v(-2.9, -23.2) * mm, "end": v(-2.81, -23.07) * mm});
            skLineSegment(sketch, "E2625", {"start": v(-2.81, -23.07) * mm, "end": v(-2.7, -22.97) * mm});
            skLineSegment(sketch, "E2626", {"start": v(-2.7, -22.97) * mm, "end": v(-2.59, -22.88) * mm});
            skLineSegment(sketch, "E2627", {"start": v(-2.59, -22.88) * mm, "end": v(-2.45, -22.81) * mm});
            skLineSegment(sketch, "E2628", {"start": v(-10.52, -23.2) * mm, "end": v(-10.43, -23.07) * mm});
            skLineSegment(sketch, "E2629", {"start": v(-10.43, -23.07) * mm, "end": v(-10.33, -22.97) * mm});
            skLineSegment(sketch, "E2630", {"start": v(-10.33, -22.97) * mm, "end": v(-10.2, -22.88) * mm});
            skLineSegment(sketch, "E2631", {"start": v(-10.2, -22.88) * mm, "end": v(-10.07, -22.81) * mm});
            skLineSegment(sketch, "E2632", {"start": v(-10.07, -22.81) * mm, "end": v(-9.93, -22.76) * mm});
            skLineSegment(sketch, "E2633", {"start": v(-9.93, -22.76) * mm, "end": v(-9.78, -22.74) * mm});
            skLineSegment(sketch, "E2634", {"start": v(-9.78, -22.74) * mm, "end": v(-9.63, -22.74) * mm});
            skLineSegment(sketch, "E2635", {"start": v(-9.63, -22.74) * mm, "end": v(-9.49, -22.76) * mm});
            skLineSegment(sketch, "E2636", {"start": v(-9.49, -22.76) * mm, "end": v(-9.34, -22.81) * mm});
            skLineSegment(sketch, "E2637", {"start": v(-9.34, -22.81) * mm, "end": v(-9.21, -22.88) * mm});
            skLineSegment(sketch, "E2638", {"start": v(-9.21, -22.88) * mm, "end": v(-9.1, -22.97) * mm});
            skLineSegment(sketch, "E2639", {"start": v(-9.1, -22.97) * mm, "end": v(-8.99, -23.07) * mm});
            skLineSegment(sketch, "E2640", {"start": v(-8.99, -23.07) * mm, "end": v(-8.9, -23.2) * mm});
            skLineSegment(sketch, "E2641", {"start": v(-8.9, -23.2) * mm, "end": v(-8.83, -23.32) * mm});
            skLineSegment(sketch, "E2642", {"start": v(-8.83, -23.32) * mm, "end": v(-8.79, -23.47) * mm});
            skLineSegment(sketch, "E2643", {"start": v(-8.79, -23.47) * mm, "end": v(-8.76, -23.61) * mm});
            skLineSegment(sketch, "E2644", {"start": v(-8.76, -23.61) * mm, "end": v(-8.76, -23.76) * mm});
            skLineSegment(sketch, "E2645", {"start": v(-13.06, -23.2) * mm, "end": v(-12.97, -23.07) * mm});
            skLineSegment(sketch, "E2646", {"start": v(-12.97, -23.07) * mm, "end": v(-12.87, -22.97) * mm});
            skLineSegment(sketch, "E2647", {"start": v(-12.87, -22.97) * mm, "end": v(-12.75, -22.88) * mm});
            skLineSegment(sketch, "E2648", {"start": v(-12.75, -22.88) * mm, "end": v(-12.61, -22.81) * mm});
            skLineSegment(sketch, "E2649", {"start": v(-12.61, -22.81) * mm, "end": v(-12.47, -22.76) * mm});
            skLineSegment(sketch, "E2650", {"start": v(-12.47, -22.76) * mm, "end": v(-12.32, -22.74) * mm});
            skLineSegment(sketch, "E2651", {"start": v(-12.32, -22.74) * mm, "end": v(-12.17, -22.74) * mm});
            skLineSegment(sketch, "E2652", {"start": v(-12.17, -22.74) * mm, "end": v(-12.03, -22.76) * mm});
            skLineSegment(sketch, "E2653", {"start": v(-12.03, -22.76) * mm, "end": v(-11.88, -22.81) * mm});
            skLineSegment(sketch, "E2654", {"start": v(-11.88, -22.81) * mm, "end": v(-11.75, -22.88) * mm});
            skLineSegment(sketch, "E2655", {"start": v(-11.75, -22.88) * mm, "end": v(-11.63, -22.97) * mm});
            skLineSegment(sketch, "E2656", {"start": v(-11.63, -22.97) * mm, "end": v(-11.53, -23.07) * mm});
            skLineSegment(sketch, "E2657", {"start": v(-11.53, -23.07) * mm, "end": v(-11.44, -23.2) * mm});
            skLineSegment(sketch, "E2658", {"start": v(-11.44, -23.2) * mm, "end": v(-11.37, -23.32) * mm});
            skLineSegment(sketch, "E2659", {"start": v(-11.37, -23.32) * mm, "end": v(-11.33, -23.47) * mm});
            skLineSegment(sketch, "E2660", {"start": v(-11.33, -23.47) * mm, "end": v(-11.3, -23.61) * mm});
            skLineSegment(sketch, "E2661", {"start": v(-11.3, -23.61) * mm, "end": v(-11.3, -23.76) * mm});
            skLineSegment(sketch, "E2662", {"start": v(-15.4, -0.07) * mm, "end": v(-15.49, -0.11) * mm});
            skLineSegment(sketch, "E2663", {"start": v(-15.49, -0.11) * mm, "end": v(-14.97, -0.12) * mm});
            skLineSegment(sketch, "E2664", {"start": v(-14.97, -0.12) * mm, "end": v(-14.9, -0.15) * mm});
            skLineSegment(sketch, "E2665", {"start": v(-14.9, -0.15) * mm, "end": v(-14.57, -0.49) * mm});
            skLineSegment(sketch, "E2666", {"start": v(-14.57, -0.49) * mm, "end": v(-14.49, -0.46) * mm});
            skLineSegment(sketch, "E2667", {"start": v(-14.49, -0.46) * mm, "end": v(-14.38, -0.44) * mm});
            skLineSegment(sketch, "E2668", {"start": v(-14.38, -0.44) * mm, "end": v(-14.26, -0.46) * mm});
            skLineSegment(sketch, "E2669", {"start": v(-14.26, -0.46) * mm, "end": v(-14.16, -0.5) * mm});
            skLineSegment(sketch, "E2670", {"start": v(-14.16, -0.5) * mm, "end": v(-14.06, -0.56) * mm});
            skLineSegment(sketch, "E2671", {"start": v(-14.06, -0.56) * mm, "end": v(-13.99, -0.64) * mm});
            skLineSegment(sketch, "E2672", {"start": v(-13.99, -0.64) * mm, "end": v(-13.93, -0.74) * mm});
            skLineSegment(sketch, "E2673", {"start": v(-13.93, -0.74) * mm, "end": v(-13.9, -0.85) * mm});
            skLineSegment(sketch, "E2674", {"start": v(-13.9, -0.85) * mm, "end": v(-13.9, -0.97) * mm});
            skLineSegment(sketch, "E2675", {"start": v(-13.9, -0.97) * mm, "end": v(-13.92, -1.08) * mm});
            skLineSegment(sketch, "E2676", {"start": v(-13.92, -1.08) * mm, "end": v(-13.96, -1.18) * mm});
            skLineSegment(sketch, "E2677", {"start": v(-13.96, -1.18) * mm, "end": v(-14.04, -1.27) * mm});
            skLineSegment(sketch, "E2678", {"start": v(-14.04, -1.27) * mm, "end": v(-14.12, -1.34) * mm});
            skLineSegment(sketch, "E2679", {"start": v(-14.12, -1.34) * mm, "end": v(-14.23, -1.39) * mm});
            skLineSegment(sketch, "E2680", {"start": v(-14.23, -1.39) * mm, "end": v(-14.34, -1.4) * mm});
            skLineSegment(sketch, "E2681", {"start": v(-14.34, -1.4) * mm, "end": v(-14.45, -1.4) * mm});
            skLineSegment(sketch, "E2682", {"start": v(-14.45, -1.4) * mm, "end": v(-14.56, -1.37) * mm});
            skLineSegment(sketch, "E2683", {"start": v(-14.56, -1.37) * mm, "end": v(-14.66, -1.32) * mm});
            skLineSegment(sketch, "E2684", {"start": v(-14.66, -1.32) * mm, "end": v(-14.74, -1.24) * mm});
            skLineSegment(sketch, "E2685", {"start": v(-14.74, -1.24) * mm, "end": v(-14.8, -1.15) * mm});
            skLineSegment(sketch, "E2686", {"start": v(-14.8, -1.15) * mm, "end": v(-14.85, -1.04) * mm});
            skLineSegment(sketch, "E2687", {"start": v(-14.85, -1.04) * mm, "end": v(-14.86, -0.93) * mm});
            skLineSegment(sketch, "E2688", {"start": v(-14.86, -0.93) * mm, "end": v(-14.85, -0.81) * mm});
            skLineSegment(sketch, "E2689", {"start": v(-14.85, -0.81) * mm, "end": v(-14.82, -0.73) * mm});
            skLineSegment(sketch, "E2690", {"start": v(-14.82, -0.73) * mm, "end": v(-15.09, -0.47) * mm});
            skLineSegment(sketch, "E2691", {"start": v(-15.09, -0.47) * mm, "end": v(-15.5, -0.47) * mm});
            skLineSegment(sketch, "E2692", {"start": v(-15.5, -0.47) * mm, "end": v(-15.4, -0.52) * mm});
            skLineSegment(sketch, "E2693", {"start": v(-15.4, -0.52) * mm, "end": v(-15.3, -0.58) * mm});
            skLineSegment(sketch, "E2694", {"start": v(-15.3, -0.58) * mm, "end": v(-15.23, -0.68) * mm});
            skLineSegment(sketch, "E2695", {"start": v(-15.23, -0.68) * mm, "end": v(-15.19, -0.78) * mm});
            skLineSegment(sketch, "E2696", {"start": v(-15.19, -0.78) * mm, "end": v(-15.17, -0.89) * mm});
            skLineSegment(sketch, "E2697", {"start": v(-15.17, -0.89) * mm, "end": v(-15.17, -1) * mm});
            skLineSegment(sketch, "E2698", {"start": v(-15.17, -1) * mm, "end": v(-15.2, -1.11) * mm});
            skLineSegment(sketch, "E2699", {"start": v(-15.2, -1.11) * mm, "end": v(-15.26, -1.21) * mm});
            skLineSegment(sketch, "E2700", {"start": v(-15.26, -1.21) * mm, "end": v(-15.33, -1.3) * mm});
            skLineSegment(sketch, "E2701", {"start": v(-15.33, -1.3) * mm, "end": v(-15.43, -1.36) * mm});
            skLineSegment(sketch, "E2702", {"start": v(-15.43, -1.36) * mm, "end": v(-15.53, -1.4) * mm});
            skLineSegment(sketch, "E2703", {"start": v(-15.53, -1.4) * mm, "end": v(-15.65, -1.4) * mm});
            skLineSegment(sketch, "E2704", {"start": v(-15.65, -1.4) * mm, "end": v(-15.76, -1.4) * mm});
            skLineSegment(sketch, "E2705", {"start": v(-15.76, -1.4) * mm, "end": v(-15.86, -1.36) * mm});
            skLineSegment(sketch, "E2706", {"start": v(-15.86, -1.36) * mm, "end": v(-15.96, -1.3) * mm});
            skLineSegment(sketch, "E2707", {"start": v(-15.96, -1.3) * mm, "end": v(-16.04, -1.21) * mm});
            skLineSegment(sketch, "E2708", {"start": v(-16.04, -1.21) * mm, "end": v(-16.1, -1.11) * mm});
            skLineSegment(sketch, "E2709", {"start": v(-16.1, -1.11) * mm, "end": v(-16.11, -1.05) * mm});
            skLineSegment(sketch, "E2710", {"start": v(-16.11, -1.05) * mm, "end": v(-20.94, -1.04) * mm});
            skLineSegment(sketch, "E2711", {"start": v(-20.94, -1.04) * mm, "end": v(-21, -1.01) * mm});
            skLineSegment(sketch, "E2712", {"start": v(-21, -1.01) * mm, "end": v(-21.5, -0.52) * mm});
            skLineSegment(sketch, "E2713", {"start": v(-21.5, -0.52) * mm, "end": v(-25.27, 3.26) * mm});
            skLineSegment(sketch, "E2714", {"start": v(-25.27, 3.26) * mm, "end": v(-25.3, 3.32) * mm});
            skLineSegment(sketch, "E2715", {"start": v(-25.3, 3.32) * mm, "end": v(-25.3, 4.03) * mm});
            skLineSegment(sketch, "E2716", {"start": v(-25.3, 4.03) * mm, "end": v(-25.3, 10.98) * mm});
            skLineSegment(sketch, "E2717", {"start": v(-25.3, 10.98) * mm, "end": v(-25.26, 11.04) * mm});
            skLineSegment(sketch, "E2718", {"start": v(-25.26, 11.04) * mm, "end": v(-24.77, 11.54) * mm});
            skLineSegment(sketch, "E2719", {"start": v(-24.77, 11.54) * mm, "end": v(-18.83, 17.47) * mm});
            skLineSegment(sketch, "E2720", {"start": v(-18.83, 17.47) * mm, "end": v(-18.77, 17.5) * mm});
            skLineSegment(sketch, "E2721", {"start": v(-18.77, 17.5) * mm, "end": v(-18.06, 17.5) * mm});
            skLineSegment(sketch, "E2722", {"start": v(-18.06, 17.5) * mm, "end": v(35.67, 17.5) * mm});
            skLineSegment(sketch, "E2723", {"start": v(35.67, 17.5) * mm, "end": v(35.73, 17.68) * mm});
            skLineSegment(sketch, "E2724", {"start": v(35.68, 17.1) * mm, "end": v(35.68, 17.14) * mm});
            skLineSegment(sketch, "E2725", {"start": v(35.68, 17.14) * mm, "end": v(-18.66, 17.14) * mm});
            skLineSegment(sketch, "E2726", {"start": v(-18.66, 17.14) * mm, "end": v(-24.94, 10.86) * mm});
            skLineSegment(sketch, "E2727", {"start": v(-24.94, 10.86) * mm, "end": v(-24.94, 3.42) * mm});
            skLineSegment(sketch, "E2728", {"start": v(-24.94, 3.42) * mm, "end": v(-20.83, -0.7) * mm});
            skLineSegment(sketch, "E2729", {"start": v(-20.83, -0.7) * mm, "end": v(-16.3, -0.7) * mm});
            skLineSegment(sketch, "E2730", {"start": v(-16.3, -0.7) * mm, "end": v(-16.07, -0.7) * mm});
            skLineSegment(sketch, "E2731", {"start": v(-16.07, -0.7) * mm, "end": v(-15.99, -0.58) * mm});
            skLineSegment(sketch, "E2732", {"start": v(-15.8, -0.47) * mm, "end": v(-20.32, -0.46) * mm});
            skLineSegment(sketch, "E2733", {"start": v(-20.32, -0.46) * mm, "end": v(-20.38, -0.43) * mm});
            skLineSegment(sketch, "E2734", {"start": v(-20.38, -0.43) * mm, "end": v(-20.88, 0.06) * mm});
            skLineSegment(sketch, "E2735", {"start": v(-20.88, 0.06) * mm, "end": v(-24.49, 3.67) * mm});
            skLineSegment(sketch, "E2736", {"start": v(-24.49, 3.67) * mm, "end": v(-24.5, 3.74) * mm});
            skLineSegment(sketch, "E2737", {"start": v(-24.5, 3.74) * mm, "end": v(-24.51, 4.44) * mm});
            skLineSegment(sketch, "E2738", {"start": v(-24.51, 4.44) * mm, "end": v(-24.5, 10.55) * mm});
            skLineSegment(sketch, "E2739", {"start": v(-24.5, 10.55) * mm, "end": v(-24.48, 10.6) * mm});
            skLineSegment(sketch, "E2740", {"start": v(-24.48, 10.6) * mm, "end": v(-23.98, 11.1) * mm});
            skLineSegment(sketch, "E2741", {"start": v(-23.98, 11.1) * mm, "end": v(-20.15, 14.93) * mm});
            skLineSegment(sketch, "E2742", {"start": v(-20.15, 14.93) * mm, "end": v(-20.08, 14.96) * mm});
            skLineSegment(sketch, "E2743", {"start": v(-20.08, 14.96) * mm, "end": v(-19.38, 14.96) * mm});
            skLineSegment(sketch, "E2744", {"start": v(-19.38, 14.96) * mm, "end": v(35.67, 14.96) * mm});
            skLineSegment(sketch, "E2745", {"start": v(35.67, 14.96) * mm, "end": v(35.73, 15.14) * mm});
            skLineSegment(sketch, "E2746", {"start": v(35.68, 14.56) * mm, "end": v(35.68, 14.6) * mm});
            skLineSegment(sketch, "E2747", {"start": v(35.68, 14.6) * mm, "end": v(-19.98, 14.6) * mm});
            skLineSegment(sketch, "E2748", {"start": v(-19.98, 14.6) * mm, "end": v(-24.16, 10.43) * mm});
            skLineSegment(sketch, "E2749", {"start": v(-24.16, 10.43) * mm, "end": v(-24.16, 3.84) * mm});
            skLineSegment(sketch, "E2750", {"start": v(-24.16, 3.84) * mm, "end": v(-20.2, -0.11) * mm});
            skLineSegment(sketch, "E2751", {"start": v(-20.2, -0.11) * mm, "end": v(-15.8, -0.11) * mm});
            skLineSegment(sketch, "E2752", {"start": v(-15.8, -0.11) * mm, "end": v(-15.9, -0.07) * mm});
            skLineSegment(sketch, "E2753", {"start": v(-15.9, -0.07) * mm, "end": v(-15.99, 0) * mm});
            skLineSegment(sketch, "E2754", {"start": v(-15.99, 0) * mm, "end": v(-16.06, 0.1) * mm});
            skLineSegment(sketch, "E2755", {"start": v(-16.06, 0.1) * mm, "end": v(-16.1, 0.2) * mm});
            skLineSegment(sketch, "E2756", {"start": v(-16.1, 0.2) * mm, "end": v(-16.13, 0.3) * mm});
            skLineSegment(sketch, "E2757", {"start": v(-16.13, 0.3) * mm, "end": v(-16.13, 0.37) * mm});
            skLineSegment(sketch, "E2758", {"start": v(-16.13, 0.37) * mm, "end": v(-19.87, 0.37) * mm});
            skLineSegment(sketch, "E2759", {"start": v(-19.87, 0.37) * mm, "end": v(-19.93, 0.4) * mm});
            skLineSegment(sketch, "E2760", {"start": v(-19.93, 0.4) * mm, "end": v(-20.43, 0.9) * mm});
            skLineSegment(sketch, "E2761", {"start": v(-20.43, 0.9) * mm, "end": v(-23.12, 3.6) * mm});
            skLineSegment(sketch, "E2762", {"start": v(-23.12, 3.6) * mm, "end": v(-23.15, 3.67) * mm});
            skLineSegment(sketch, "E2763", {"start": v(-23.15, 3.67) * mm, "end": v(-23.15, 4.37) * mm});
            skLineSegment(sketch, "E2764", {"start": v(-23.15, 4.37) * mm, "end": v(-23.15, 9.64) * mm});
            skLineSegment(sketch, "E2765", {"start": v(-23.15, 9.64) * mm, "end": v(-23.12, 9.7) * mm});
            skLineSegment(sketch, "E2766", {"start": v(-23.12, 9.7) * mm, "end": v(-22.62, 10.2) * mm});
            skLineSegment(sketch, "E2767", {"start": v(-22.62, 10.2) * mm, "end": v(-20.43, 12.4) * mm});
            skLineSegment(sketch, "E2768", {"start": v(-20.43, 12.4) * mm, "end": v(-20.37, 12.42) * mm});
            skLineSegment(sketch, "E2769", {"start": v(-20.37, 12.42) * mm, "end": v(-19.66, 12.42) * mm});
            skLineSegment(sketch, "E2770", {"start": v(-19.66, 12.42) * mm, "end": v(35.67, 12.42) * mm});
            skLineSegment(sketch, "E2771", {"start": v(35.67, 12.42) * mm, "end": v(35.73, 12.6) * mm});
            skLineSegment(sketch, "E2772", {"start": v(35.68, 12.02) * mm, "end": v(35.68, 12.06) * mm});
            skLineSegment(sketch, "E2773", {"start": v(35.68, 12.06) * mm, "end": v(-20.26, 12.06) * mm});
            skLineSegment(sketch, "E2774", {"start": v(-20.26, 12.06) * mm, "end": v(-22.8, 9.53) * mm});
            skLineSegment(sketch, "E2775", {"start": v(-22.8, 9.53) * mm, "end": v(-22.8, 3.76) * mm});
            skLineSegment(sketch, "E2776", {"start": v(-22.8, 3.76) * mm, "end": v(-19.75, 0.72) * mm});
            skLineSegment(sketch, "E2777", {"start": v(-19.75, 0.72) * mm, "end": v(-15.95, 0.72) * mm});
            skLineSegment(sketch, "E2778", {"start": v(-15.95, 0.72) * mm, "end": v(-15.83, 0.79) * mm});
            skLineSegment(sketch, "E2779", {"start": v(-15.83, 0.79) * mm, "end": v(-15.72, 0.82) * mm});
            skLineSegment(sketch, "E2780", {"start": v(-15.72, 0.82) * mm, "end": v(-15.6, 0.83) * mm});
            skLineSegment(sketch, "E2781", {"start": v(-15.6, 0.83) * mm, "end": v(-15.5, 0.8) * mm});
            skLineSegment(sketch, "E2782", {"start": v(-15.5, 0.8) * mm, "end": v(-15.4, 0.75) * mm});
            skLineSegment(sketch, "E2783", {"start": v(-15.4, 0.75) * mm, "end": v(-15.3, 0.69) * mm});
            skLineSegment(sketch, "E2784", {"start": v(-15.3, 0.69) * mm, "end": v(-15.23, 0.6) * mm});
            skLineSegment(sketch, "E2785", {"start": v(-15.23, 0.6) * mm, "end": v(-15.19, 0.5) * mm});
            skLineSegment(sketch, "E2786", {"start": v(-15.19, 0.5) * mm, "end": v(-15.17, 0.38) * mm});
            skLineSegment(sketch, "E2787", {"start": v(-15.17, 0.38) * mm, "end": v(-15.17, 0.3) * mm});
            skLineSegment(sketch, "E2788", {"start": v(-13.9, 0.3) * mm, "end": v(-13.92, 0.2) * mm});
            skLineSegment(sketch, "E2789", {"start": v(-13.92, 0.2) * mm, "end": v(-13.96, 0.1) * mm});
            skLineSegment(sketch, "E2790", {"start": v(-13.96, 0.1) * mm, "end": v(-14.04, 0) * mm});
            skLineSegment(sketch, "E2791", {"start": v(-14.04, 0) * mm, "end": v(-14.12, -0.07) * mm});
            skLineSegment(sketch, "E2792", {"start": v(-14.12, -0.07) * mm, "end": v(-14.23, -0.12) * mm});
            skLineSegment(sketch, "E2793", {"start": v(-14.23, -0.12) * mm, "end": v(-14.34, -0.14) * mm});
            skLineSegment(sketch, "E2794", {"start": v(-14.34, -0.14) * mm, "end": v(-14.45, -0.13) * mm});
            skLineSegment(sketch, "E2795", {"start": v(-14.45, -0.13) * mm, "end": v(-14.56, -0.1) * mm});
            skLineSegment(sketch, "E2796", {"start": v(-14.56, -0.1) * mm, "end": v(-14.66, -0.05) * mm});
            skLineSegment(sketch, "E2797", {"start": v(-14.66, -0.05) * mm, "end": v(-14.74, 0.03) * mm});
            skLineSegment(sketch, "E2798", {"start": v(-14.74, 0.03) * mm, "end": v(-14.8, 0.12) * mm});
            skLineSegment(sketch, "E2799", {"start": v(-14.8, 0.12) * mm, "end": v(-14.85, 0.23) * mm});
            skLineSegment(sketch, "E2800", {"start": v(-14.85, 0.23) * mm, "end": v(-14.86, 0.34) * mm});
            skLineSegment(sketch, "E2801", {"start": v(-14.86, 0.34) * mm, "end": v(-14.85, 0.46) * mm});
            skLineSegment(sketch, "E2802", {"start": v(-14.85, 0.46) * mm, "end": v(-14.82, 0.54) * mm});
            skLineSegment(sketch, "E2803", {"start": v(-14.82, 0.54) * mm, "end": v(-15.75, 1.46) * mm});
            skLineSegment(sketch, "E2804", {"start": v(-15.75, 1.46) * mm, "end": v(-19.02, 1.46) * mm});
            skLineSegment(sketch, "E2805", {"start": v(-19.02, 1.46) * mm, "end": v(-19.08, 1.49) * mm});
            skLineSegment(sketch, "E2806", {"start": v(-19.08, 1.49) * mm, "end": v(-19.12, 1.51) * mm});
            skLineSegment(sketch, "E2807", {"start": v(-19.12, 1.51) * mm, "end": v(-21.26, 3.66) * mm});
            skLineSegment(sketch, "E2808", {"start": v(-21.26, 3.66) * mm, "end": v(-21.29, 3.73) * mm});
            skLineSegment(sketch, "E2809", {"start": v(-21.29, 3.73) * mm, "end": v(-21.29, 4.43) * mm});
            skLineSegment(sketch, "E2810", {"start": v(-21.29, 4.43) * mm, "end": v(-21.28, 8.1) * mm});
            skLineSegment(sketch, "E2811", {"start": v(-21.28, 8.1) * mm, "end": v(-21.25, 8.17) * mm});
            skLineSegment(sketch, "E2812", {"start": v(-21.25, 8.17) * mm, "end": v(-20.76, 8.67) * mm});
            skLineSegment(sketch, "E2813", {"start": v(-20.76, 8.67) * mm, "end": v(-19.57, 9.85) * mm});
            skLineSegment(sketch, "E2814", {"start": v(-19.57, 9.85) * mm, "end": v(-19.5, 9.88) * mm});
            skLineSegment(sketch, "E2815", {"start": v(-19.5, 9.88) * mm, "end": v(-18.8, 9.88) * mm});
            skLineSegment(sketch, "E2816", {"start": v(-18.8, 9.88) * mm, "end": v(35.67, 9.88) * mm});
            skLineSegment(sketch, "E2817", {"start": v(35.67, 9.88) * mm, "end": v(35.73, 10.06) * mm});
            skLineSegment(sketch, "E2818", {"start": v(35.68, 9.48) * mm, "end": v(35.68, 9.52) * mm});
            skLineSegment(sketch, "E2819", {"start": v(35.68, 9.52) * mm, "end": v(-19.4, 9.52) * mm});
            skLineSegment(sketch, "E2820", {"start": v(-19.4, 9.52) * mm, "end": v(-20.93, 8) * mm});
            skLineSegment(sketch, "E2821", {"start": v(-20.93, 8) * mm, "end": v(-20.93, 3.83) * mm});
            skLineSegment(sketch, "E2822", {"start": v(-20.93, 3.83) * mm, "end": v(-19.35, 2.25) * mm});
            skLineSegment(sketch, "E2823", {"start": v(-19.35, 2.25) * mm, "end": v(-18.92, 1.81) * mm});
            skLineSegment(sketch, "E2824", {"start": v(-18.92, 1.81) * mm, "end": v(-15.63, 1.8) * mm});
            skLineSegment(sketch, "E2825", {"start": v(-15.63, 1.8) * mm, "end": v(-15.57, 1.78) * mm});
            skLineSegment(sketch, "E2826", {"start": v(-15.57, 1.78) * mm, "end": v(-15.06, 1.28) * mm});
            skLineSegment(sketch, "E2827", {"start": v(-15.06, 1.28) * mm, "end": v(-14.56, 0.78) * mm});
            skLineSegment(sketch, "E2828", {"start": v(-14.56, 0.78) * mm, "end": v(-14.49, 0.81) * mm});
            skLineSegment(sketch, "E2829", {"start": v(-14.49, 0.81) * mm, "end": v(-14.38, 0.83) * mm});
            skLineSegment(sketch, "E2830", {"start": v(-14.38, 0.83) * mm, "end": v(-14.26, 0.81) * mm});
            skLineSegment(sketch, "E2831", {"start": v(-14.26, 0.81) * mm, "end": v(-14.16, 0.77) * mm});
            skLineSegment(sketch, "E2832", {"start": v(-14.16, 0.77) * mm, "end": v(-14.06, 0.71) * mm});
            skLineSegment(sketch, "E2833", {"start": v(-14.06, 0.71) * mm, "end": v(-13.99, 0.63) * mm});
            skLineSegment(sketch, "E2834", {"start": v(-13.99, 0.63) * mm, "end": v(-13.93, 0.53) * mm});
            skLineSegment(sketch, "E2835", {"start": v(-13.93, 0.53) * mm, "end": v(-13.9, 0.42) * mm});
            skLineSegment(sketch, "E2836", {"start": v(-13.9, 0.42) * mm, "end": v(-13.9, 0.3) * mm});
            skLineSegment(sketch, "E2837", {"start": v(-13.9, -2.24) * mm, "end": v(-13.92, -2.35) * mm});
            skLineSegment(sketch, "E2838", {"start": v(-13.92, -2.35) * mm, "end": v(-13.96, -2.45) * mm});
            skLineSegment(sketch, "E2839", {"start": v(-13.96, -2.45) * mm, "end": v(-14.04, -2.54) * mm});
            skLineSegment(sketch, "E2840", {"start": v(-14.04, -2.54) * mm, "end": v(-14.12, -2.6) * mm});
            skLineSegment(sketch, "E2841", {"start": v(-14.12, -2.6) * mm, "end": v(-14.23, -2.66) * mm});
            skLineSegment(sketch, "E2842", {"start": v(-14.23, -2.66) * mm, "end": v(-14.34, -2.68) * mm});
            skLineSegment(sketch, "E2843", {"start": v(-14.34, -2.68) * mm, "end": v(-14.45, -2.67) * mm});
            skLineSegment(sketch, "E2844", {"start": v(-14.45, -2.67) * mm, "end": v(-14.57, -2.64) * mm});
            skLineSegment(sketch, "E2845", {"start": v(-14.57, -2.64) * mm, "end": v(-17.29, -5.36) * mm});
            skLineSegment(sketch, "E2846", {"start": v(-17.29, -5.36) * mm, "end": v(-17.35, -5.39) * mm});
            skLineSegment(sketch, "E2847", {"start": v(-17.35, -5.39) * mm, "end": v(-17.4, -5.39) * mm});
            skLineSegment(sketch, "E2848", {"start": v(-17.4, -5.39) * mm, "end": v(-18.74, -5.39) * mm});
            skLineSegment(sketch, "E2849", {"start": v(-18.74, -5.39) * mm, "end": v(-18.8, -5.36) * mm});
            skLineSegment(sketch, "E2850", {"start": v(-18.8, -5.36) * mm, "end": v(-19.3, -4.86) * mm});
            skLineSegment(sketch, "E2851", {"start": v(-19.3, -4.86) * mm, "end": v(-26.53, 2.37) * mm});
            skLineSegment(sketch, "E2852", {"start": v(-26.53, 2.37) * mm, "end": v(-26.56, 2.44) * mm});
            skLineSegment(sketch, "E2853", {"start": v(-26.56, 2.44) * mm, "end": v(-26.56, 3.14) * mm});
            skLineSegment(sketch, "E2854", {"start": v(-26.56, 3.14) * mm, "end": v(-26.55, 10.8) * mm});
            skLineSegment(sketch, "E2855", {"start": v(-26.55, 10.8) * mm, "end": v(-26.52, 10.87) * mm});
            skLineSegment(sketch, "E2856", {"start": v(-26.52, 10.87) * mm, "end": v(-26.03, 11.37) * mm});
            skLineSegment(sketch, "E2857", {"start": v(-26.03, 11.37) * mm, "end": v(-17.38, 20.01) * mm});
            skLineSegment(sketch, "E2858", {"start": v(-17.38, 20.01) * mm, "end": v(-17.31, 20.04) * mm});
            skLineSegment(sketch, "E2859", {"start": v(-17.31, 20.04) * mm, "end": v(-16.6, 20.04) * mm});
            skLineSegment(sketch, "E2860", {"start": v(-16.6, 20.04) * mm, "end": v(35.67, 20.04) * mm});
            skLineSegment(sketch, "E2861", {"start": v(35.67, 20.04) * mm, "end": v(35.73, 20.22) * mm});
            skLineSegment(sketch, "E2862", {"start": v(35.68, 19.64) * mm, "end": v(35.68, 19.68) * mm});
            skLineSegment(sketch, "E2863", {"start": v(35.68, 19.68) * mm, "end": v(-17.2, 19.68) * mm});
            skLineSegment(sketch, "E2864", {"start": v(-17.2, 19.68) * mm, "end": v(-26.2, 10.69) * mm});
            skLineSegment(sketch, "E2865", {"start": v(-26.2, 10.69) * mm, "end": v(-26.2, 9.55) * mm});
            skLineSegment(sketch, "E2866", {"start": v(-26.2, 9.55) * mm, "end": v(-26.2, 2.54) * mm});
            skLineSegment(sketch, "E2867", {"start": v(-26.2, 2.54) * mm, "end": v(-20.7, -2.96) * mm});
            skLineSegment(sketch, "E2868", {"start": v(-20.7, -2.96) * mm, "end": v(-18.62, -5.04) * mm});
            skLineSegment(sketch, "E2869", {"start": v(-18.62, -5.04) * mm, "end": v(-17.47, -5.03) * mm});
            skLineSegment(sketch, "E2870", {"start": v(-17.47, -5.03) * mm, "end": v(-14.82, -2.4) * mm});
            skLineSegment(sketch, "E2871", {"start": v(-14.82, -2.4) * mm, "end": v(-14.85, -2.27) * mm});
            skLineSegment(sketch, "E2872", {"start": v(-13.95, -1.98) * mm, "end": v(-13.9, -2.08) * mm});
            skLineSegment(sketch, "E2873", {"start": v(-13.9, -2.08) * mm, "end": v(-13.9, -2.2) * mm});
            skLineSegment(sketch, "E2874", {"start": v(-13.9, -2.2) * mm, "end": v(-13.9, -2.24) * mm});
            skLineSegment(sketch, "E2875", {"start": v(35.71, -9.04) * mm, "end": v(37.48, -9.04) * mm});
            skLineSegment(sketch, "E2876", {"start": v(35.58, -10.94) * mm, "end": v(35.58, -9.04) * mm});
            skLineSegment(sketch, "E2877", {"start": v(35.58, -9.04) * mm, "end": v(35.71, -9.04) * mm});
            skLineSegment(sketch, "E2878", {"start": v(35.72, -12.04) * mm, "end": v(35.8, -11.92) * mm});
            skLineSegment(sketch, "E2879", {"start": v(35.8, -11.92) * mm, "end": v(35.91, -11.81) * mm});
            skLineSegment(sketch, "E2880", {"start": v(35.91, -11.81) * mm, "end": v(36.03, -11.72) * mm});
            skLineSegment(sketch, "E2881", {"start": v(36.03, -11.72) * mm, "end": v(36.17, -11.65) * mm});
            skLineSegment(sketch, "E2882", {"start": v(13.4, 4.77) * mm, "end": v(15.17, 4.77) * mm});
            skLineSegment(sketch, "E2883", {"start": v(15.95, 4.32) * mm, "end": v(16.04, 4.44) * mm});
            skLineSegment(sketch, "E2884", {"start": v(16.04, 4.44) * mm, "end": v(16.14, 4.54) * mm});
            skLineSegment(sketch, "E2885", {"start": v(16.14, 4.54) * mm, "end": v(16.27, 4.63) * mm});
            skLineSegment(sketch, "E2886", {"start": v(16.27, 4.63) * mm, "end": v(16.4, 4.7) * mm});
            skLineSegment(sketch, "E2887", {"start": v(16.4, 4.7) * mm, "end": v(16.54, 4.74) * mm});
            skLineSegment(sketch, "E2888", {"start": v(16.54, 4.74) * mm, "end": v(16.69, 4.77) * mm});
            skLineSegment(sketch, "E2889", {"start": v(16.69, 4.77) * mm, "end": v(16.84, 4.77) * mm});
            skLineSegment(sketch, "E2890", {"start": v(16.84, 4.77) * mm, "end": v(16.98, 4.74) * mm});
            skLineSegment(sketch, "E2891", {"start": v(16.98, 4.74) * mm, "end": v(17.13, 4.7) * mm});
            skLineSegment(sketch, "E2892", {"start": v(17.13, 4.7) * mm, "end": v(17.26, 4.63) * mm});
            skLineSegment(sketch, "E2893", {"start": v(17.26, 4.63) * mm, "end": v(17.38, 4.54) * mm});
            skLineSegment(sketch, "E2894", {"start": v(17.38, 4.54) * mm, "end": v(17.49, 4.44) * mm});
            skLineSegment(sketch, "E2895", {"start": v(17.49, 4.44) * mm, "end": v(17.57, 4.32) * mm});
            skLineSegment(sketch, "E2896", {"start": v(12.97, 24.64) * mm, "end": v(14.74, 24.64) * mm});
            skLineSegment(sketch, "E2897", {"start": v(14.74, 24.64) * mm, "end": v(14.74, 22.74) * mm});
            skLineSegment(sketch, "E2898", {"start": v(14.74, 22.74) * mm, "end": v(12.84, 22.74) * mm});
            skLineSegment(sketch, "E2899", {"start": v(12.84, 24.64) * mm, "end": v(12.97, 24.64) * mm});
            skLineSegment(sketch, "E2900", {"start": v(17.28, 23.61) * mm, "end": v(17.25, 23.46) * mm});
            skLineSegment(sketch, "E2901", {"start": v(17.25, 23.46) * mm, "end": v(17.2, 23.32) * mm});
            skLineSegment(sketch, "E2902", {"start": v(17.2, 23.32) * mm, "end": v(17.14, 23.2) * mm});
            skLineSegment(sketch, "E2903", {"start": v(17.14, 23.2) * mm, "end": v(17.05, 23.07) * mm});
            skLineSegment(sketch, "E2904", {"start": v(17.05, 23.07) * mm, "end": v(16.95, 22.96) * mm});
            skLineSegment(sketch, "E2905", {"start": v(16.95, 22.96) * mm, "end": v(16.83, 22.88) * mm});
            skLineSegment(sketch, "E2906", {"start": v(16.83, 22.88) * mm, "end": v(16.7, 22.8) * mm});
            skLineSegment(sketch, "E2907", {"start": v(16.7, 22.8) * mm, "end": v(16.55, 22.76) * mm});
            skLineSegment(sketch, "E2908", {"start": v(16.55, 22.76) * mm, "end": v(16.4, 22.74) * mm});
            skLineSegment(sketch, "E2909", {"start": v(16.4, 22.74) * mm, "end": v(16.26, 22.74) * mm});
            skLineSegment(sketch, "E2910", {"start": v(16.26, 22.74) * mm, "end": v(16.1, 22.76) * mm});
            skLineSegment(sketch, "E2911", {"start": v(16.1, 22.76) * mm, "end": v(15.97, 22.8) * mm});
            skLineSegment(sketch, "E2912", {"start": v(15.97, 22.8) * mm, "end": v(15.83, 22.88) * mm});
            skLineSegment(sketch, "E2913", {"start": v(17.25, 23.9) * mm, "end": v(17.28, 23.76) * mm});
            skLineSegment(sketch, "E2914", {"start": v(17.28, 23.76) * mm, "end": v(17.28, 23.61) * mm});
            skSolve(sketch);
        }
        {
            var Q0;
            Q0=makeQuery(id+"F0.imprint","IMPRINT",FACE,{"disambiguationData":[TD([[makeQuery(id+"F0.imprint","IMPRINT",EDGE,{"derivedFrom":sQuery(id+"F0.wireOp",EDGE,"E612")}),1.0]])]});
            var sketch = newSketch(context, id + "F1", { "sketchPlane" : qUnion([Q0])});
            skLineSegment(sketch, "E2915.0", {"start": v(-38.1, 25.4) * mm, "end": v(-38.1, -25.4) * mm});
            skLineSegment(sketch, "E2916.0", {"start": v(38.1, 25.4) * mm, "end": v(-38.1, 25.4) * mm});
            skLineSegment(sketch, "E2917.0", {"start": v(38.1, -25.4) * mm, "end": v(38.1, 25.4) * mm});
            skLineSegment(sketch, "E2918.0", {"start": v(-38.1, -25.4) * mm, "end": v(38.1, -25.4) * mm});
            skSolve(sketch);
        }
        {
            var Q0;
            Q0 = qSketchRegion(id + "F1", true);
            extrude(context, id + "F2", {"entities" : qUnion([Q0]), "depth" : 1.6 * mm, "offsetDistance" : 25.4 * mm});
        }
        {
            var Q0;
            Q0=makeQuery(id+"F2.opExtrude","CAP_FACE",FACE,{"disambiguationData":[OSD([sQuery(id+"F1.wireOp",EDGE,"E2915.0"),sQuery(id+"F1.wireOp",EDGE,"E2916.0"),sQuery(id+"F1.wireOp",EDGE,"E2917.0"),sQuery(id+"F1.wireOp",EDGE,"E2918.0")])],"isStart":false});
            var sketch = newSketch(context, id + "F3", { "sketchPlane" : qUnion([Q0])});
            skCircle(sketch, "E2919.0", {"center": v(-25.5, -12.84) * mm, "radius": 2.54 * mm});
            skCircle(sketch, "E2920.0", {"center": v(25.48, -12.74) * mm, "radius": 2.54 * mm});
            skCircle(sketch, "E2921.0", {"center": v(-18.2, -6) * mm, "radius": 0.32 * mm});
            skCircle(sketch, "E2921.1", {"center": v(-15.67, -6) * mm, "radius": 0.32 * mm});
            skCircle(sketch, "E2921.2", {"center": v(-13.13, -6) * mm, "radius": 0.32 * mm});
            skCircle(sketch, "E2922.0", {"center": v(-15.65, -2.2) * mm, "radius": 0.32 * mm});
            skCircle(sketch, "E2922.1", {"center": v(-14.38, -2.2) * mm, "radius": 0.32 * mm});
            skCircle(sketch, "E2922.2", {"center": v(-14.38, -0.93) * mm, "radius": 0.32 * mm});
            skCircle(sketch, "E2922.3", {"center": v(-15.65, -0.93) * mm, "radius": 0.32 * mm});
            skCircle(sketch, "E2922.4", {"center": v(-15.65, 0.34) * mm, "radius": 0.32 * mm});
            skCircle(sketch, "E2922.5", {"center": v(-14.38, 0.34) * mm, "radius": 0.32 * mm});
            skCircle(sketch, "E2923.0", {"center": v(5.3, -3.88) * mm, "radius": 0.32 * mm});
            skCircle(sketch, "E2923.1", {"center": v(5.02, -2.5) * mm, "radius": 0.32 * mm});
            skCircle(sketch, "E2923.2", {"center": v(-4.81, 0.95) * mm, "radius": 0.32 * mm});
            skCircle(sketch, "E2923.3", {"center": v(6.14, 1.09) * mm, "radius": 0.32 * mm});
            skCircle(sketch, "E2923.4", {"center": v(5.96, 3.5) * mm, "radius": 0.32 * mm});
            skCircle(sketch, "E2923.5", {"center": v(8.79, 3.47) * mm, "radius": 0.32 * mm});
            skCircle(sketch, "E2923.6", {"center": v(14.22, 3.82) * mm, "radius": 0.55 * mm});
            skCircle(sketch, "E2923.7", {"center": v(16.76, 3.82) * mm, "radius": 0.55 * mm});
            skCircle(sketch, "E2923.8", {"center": v(18.52, -0.2) * mm, "radius": 0.32 * mm});
            skCircle(sketch, "E2923.9", {"center": v(7.97, -6.18) * mm, "radius": 0.32 * mm});
            skCircle(sketch, "E2923.10", {"center": v(15.12, -6.13) * mm, "radius": 0.32 * mm});
            skSolve(sketch);
        }
        {
            var Q0;
            Q0 = qSketchRegion(id + "F3", true);
            extrude(context, id + "F4", {"entities" : qUnion([Q0]), "operationType" : NewBodyOperationType.REMOVE, "endBound" : BoundingType.THROUGH_ALL, "oppositeDirection" : true, "depth" : 25.4 * mm, "offsetDistance" : 25.4 * mm});
        }
    });
